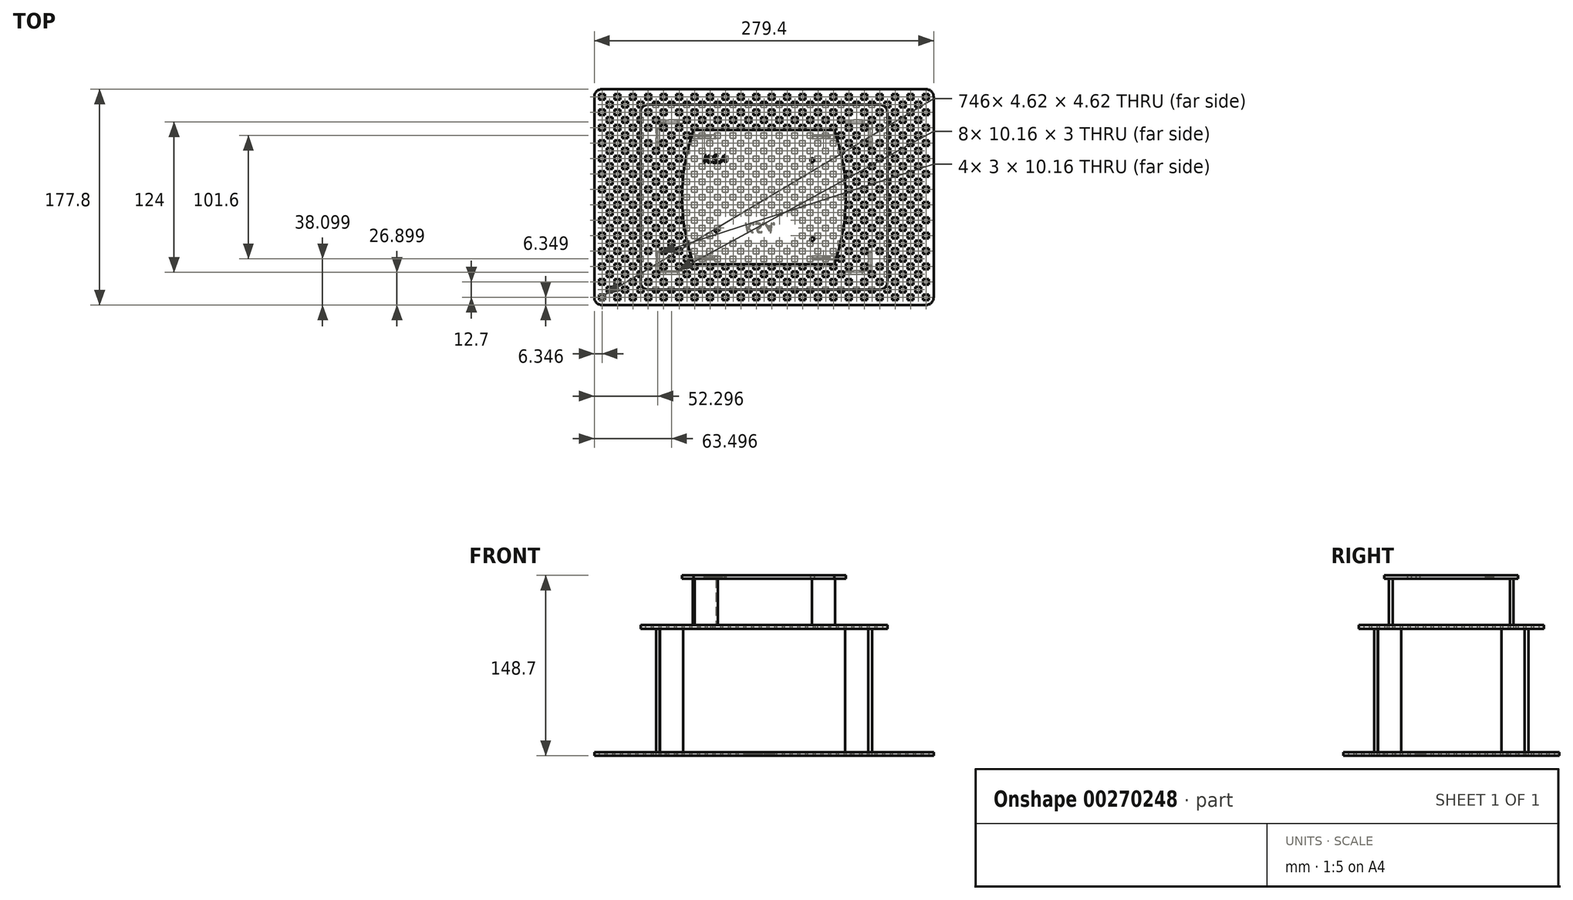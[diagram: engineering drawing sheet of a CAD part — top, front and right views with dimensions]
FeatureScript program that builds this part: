
annotation { "Feature Type Name" : "Feature", "Feature Type Description" : "" }
export const myFeature = defineFeature(function(context is Context, id is Id, definition is map)
    precondition{}
    {
        {
            var Q0;
            Q0=qCreatedBy(makeId("Top.planeOp"),FACE);
            var sketch = newSketch(context, id + "F0", { "sketchPlane" : qUnion([Q0])});
            skLineSegment(sketch, "E0.bottom", {"start": v(-86.6, 36.8) * mm, "end": v(3.9, 36.8) * mm});
            skLineSegment(sketch, "E0.top", {"start": v(-86.6, -48) * mm, "end": v(-68.74, -48) * mm});
            skLineSegment(sketch, "E0.left", {"start": v(-86.6, 36.8) * mm, "end": v(-86.6, -48) * mm});
            skLineSegment(sketch, "E0.right", {"start": v(3.9, 36.8) * mm, "end": v(3.9, -1.72) * mm});
            skLineSegment(sketch, "E1", {"start": v(-1.55, 24.76) * mm, "end": v(-1.55, -40.24) * mm});
            skLineSegment(sketch, "E2", {"start": v(-80.5, 24.76) * mm, "end": v(-1.55, 24.76) * mm});
            skLineSegment(sketch, "E3", {"start": v(-1.55, 24.76) * mm, "end": v(-1.55, 36.8) * mm});
            skLineSegment(sketch, "E4", {"start": v(-1.55, -40.24) * mm, "end": v(-1.55, -48) * mm});
            skLineSegment(sketch, "E5", {"start": v(-1.55, -40.24) * mm, "end": v(-58.83, -40.24) * mm});
            skLineSegment(sketch, "E6", {"start": v(-80.5, -40.24) * mm, "end": v(-80.5, -33.05) * mm});
            skLineSegment(sketch, "E7", {"start": v(-80.5, -33.05) * mm, "end": v(-80.5, 24.76) * mm});
            skCircle(sketch, "E8", {"center": v(-80.5, -33.05) * mm, "radius": 1.59 * mm});
            skCircle(sketch, "E9", {"center": v(-1.55, 24.76) * mm, "radius": 1.59 * mm});
            skCircle(sketch, "E10", {"center": v(-1.55, -40.24) * mm, "radius": 1.59 * mm});
            skLineSegment(sketch, "E11.bottom", {"start": v(-99.3, 49.5) * mm, "end": v(16.6, 49.5) * mm});
            skLineSegment(sketch, "E11.top", {"start": v(-99.3, -60.7) * mm, "end": v(16.6, -60.7) * mm});
            skLineSegment(sketch, "E11.left", {"start": v(-99.3, 49.5) * mm, "end": v(-99.3, -60.7) * mm});
            skLineSegment(sketch, "E11.right", {"start": v(16.6, 49.5) * mm, "end": v(16.6, -60.7) * mm});
            skLineSegment(sketch, "E12.bottom", {"start": v(-95.48, 45.7) * mm, "end": v(-85.32, 45.7) * mm});
            skLineSegment(sketch, "E12.top", {"start": v(-95.48, 42.7) * mm, "end": v(-85.32, 42.7) * mm});
            skLineSegment(sketch, "E12.left", {"start": v(-95.48, 45.7) * mm, "end": v(-95.48, 42.7) * mm});
            skLineSegment(sketch, "E12.right", {"start": v(-85.32, 45.7) * mm, "end": v(-85.32, 42.7) * mm});
            skLineSegment(sketch, "E13.bottom", {"start": v(2.64, 45.7) * mm, "end": v(12.8, 45.7) * mm});
            skLineSegment(sketch, "E13.top", {"start": v(2.64, 42.7) * mm, "end": v(12.8, 42.7) * mm});
            skLineSegment(sketch, "E13.left", {"start": v(2.64, 45.7) * mm, "end": v(2.64, 42.7) * mm});
            skLineSegment(sketch, "E13.right", {"start": v(12.8, 45.7) * mm, "end": v(12.8, 42.7) * mm});
            skLineSegment(sketch, "E14.bottom", {"start": v(-95.48, -53.88) * mm, "end": v(-85.32, -53.88) * mm});
            skLineSegment(sketch, "E14.top", {"start": v(-95.48, -56.88) * mm, "end": v(-85.32, -56.88) * mm});
            skLineSegment(sketch, "E14.left", {"start": v(-95.48, -53.88) * mm, "end": v(-95.48, -56.88) * mm});
            skLineSegment(sketch, "E14.right", {"start": v(-85.32, -53.88) * mm, "end": v(-85.32, -56.88) * mm});
            skLineSegment(sketch, "E15.bottom", {"start": v(2.64, -53.88) * mm, "end": v(12.8, -53.88) * mm});
            skLineSegment(sketch, "E15.top", {"start": v(2.64, -56.88) * mm, "end": v(12.8, -56.88) * mm});
            skLineSegment(sketch, "E15.left", {"start": v(2.64, -53.88) * mm, "end": v(2.64, -56.88) * mm});
            skLineSegment(sketch, "E15.right", {"start": v(12.8, -53.88) * mm, "end": v(12.8, -56.88) * mm});
            skPoint(sketch, "E16", {"position": v(-68.74, -48) * mm});
            skPoint(sketch, "E17", {"position": v(-60.57, -48) * mm});
            skLineSegment(sketch, "E18.trimOffspring", {"start": v(-60.57, -48) * mm, "end": v(3.9, -48) * mm});
            skLineSegment(sketch, "E19", {"start": v(12.8, 45.7) * mm, "end": v(12.8, 49.5) * mm});
            skLineSegment(sketch, "E20", {"start": v(12.8, 42.7) * mm, "end": v(16.6, 42.7) * mm});
            skLineSegment(sketch, "E21", {"start": v(-95.48, 45.7) * mm, "end": v(-95.48, 49.5) * mm});
            skLineSegment(sketch, "E22", {"start": v(-95.48, 45.7) * mm, "end": v(-99.3, 45.7) * mm});
            skLineSegment(sketch, "E23", {"start": v(12.8, -56.88) * mm, "end": v(16.6, -56.88) * mm});
            skLineSegment(sketch, "E24", {"start": v(12.8, -56.88) * mm, "end": v(12.8, -60.7) * mm});
            skLineSegment(sketch, "E25", {"start": v(-95.48, -56.88) * mm, "end": v(-95.48, -60.7) * mm});
            skLineSegment(sketch, "E26", {"start": v(-95.48, -56.88) * mm, "end": v(-99.3, -56.88) * mm});
            skPoint(sketch, "E27", {"position": v(3.9, -1.72) * mm});
            skPoint(sketch, "E28", {"position": v(3.9, -10.46) * mm});
            skLineSegment(sketch, "E29.trimOffspring", {"start": v(3.9, -10.46) * mm, "end": v(3.9, -48) * mm});
            skArc(sketch, "E30", {"start": v(-99.3, 49.5) * mm, "mid": v(-108.76, -5.6) * mm, "end": v(-99.3, -60.7) * mm});
            skArc(sketch, "E31", {"start": v(16.6, -60.7) * mm, "mid": v(26.07, -5.6) * mm, "end": v(16.6, 49.5) * mm});
            skText(sketch, "E32", { "text": "K.S.A", "fontName": "OpenSans-Italic.ttf"});
            const initialGuessF0  = {"E32": [-0.09116, 0.02265, 1, 0, 0.00642]};
            skSetInitialGuess(sketch, initialGuessF0);
            skSolve(sketch);
        }
        {
            var Q0;
            Q0 = qSketchRegion(id + "F0", true);
            extrude(context, id + "F1", {"entities" : qUnion([Q0]), "depth" : 3 * mm});
        }
        {
            var Q0;
            Q0=makeQuery(id+"F1.opExtrude","CAP_FACE",FACE,{"disambiguationData":[OSD([sQuery(id+"F0.wireOp",EDGE,"E8"),sQuery(id+"F0.wireOp",EDGE,"E9"),sQuery(id+"F0.wireOp",EDGE,"E10"),sQuery(id+"F0.wireOp",EDGE,"E11.bottom"),sQuery(id+"F0.wireOp",EDGE,"E11.top"),sQuery(id+"F0.wireOp",EDGE,"E11.left"),sQuery(id+"F0.wireOp",EDGE,"E11.right"),sQuery(id+"F0.wireOp",EDGE,"E12.bottom"),sQuery(id+"F0.wireOp",EDGE,"E12.top"),sQuery(id+"F0.wireOp",EDGE,"E12.left"),sQuery(id+"F0.wireOp",EDGE,"E12.right"),sQuery(id+"F0.wireOp",EDGE,"E13.bottom"),sQuery(id+"F0.wireOp",EDGE,"E13.top"),sQuery(id+"F0.wireOp",EDGE,"E13.left"),sQuery(id+"F0.wireOp",EDGE,"E13.right"),sQuery(id+"F0.wireOp",EDGE,"E14.bottom"),sQuery(id+"F0.wireOp",EDGE,"E14.top"),sQuery(id+"F0.wireOp",EDGE,"E14.left"),sQuery(id+"F0.wireOp",EDGE,"E14.right"),sQuery(id+"F0.wireOp",EDGE,"E15.bottom"),sQuery(id+"F0.wireOp",EDGE,"E15.top"),sQuery(id+"F0.wireOp",EDGE,"E15.left"),sQuery(id+"F0.wireOp",EDGE,"E15.right")])],"isStart":true});
            var sketch = newSketch(context, id + "F2", { "sketchPlane" : qUnion([Q0])});
            skLineSegment(sketch, "E33.bottom", {"start": v(-95.48, 56.88) * mm, "end": v(-85.32, 56.88) * mm});
            skLineSegment(sketch, "E33.top", {"start": v(-95.48, 53.88) * mm, "end": v(-85.32, 53.88) * mm});
            skLineSegment(sketch, "E33.left", {"start": v(-95.48, 56.88) * mm, "end": v(-95.48, 53.88) * mm});
            skLineSegment(sketch, "E33.right", {"start": v(-85.32, 56.88) * mm, "end": v(-85.32, 53.88) * mm});
            skLineSegment(sketch, "E34.bottom", {"start": v(2.64, 56.88) * mm, "end": v(12.8, 56.88) * mm});
            skLineSegment(sketch, "E34.top", {"start": v(2.64, 53.88) * mm, "end": v(12.8, 53.88) * mm});
            skLineSegment(sketch, "E34.left", {"start": v(2.64, 56.88) * mm, "end": v(2.64, 53.88) * mm});
            skLineSegment(sketch, "E34.right", {"start": v(12.8, 56.88) * mm, "end": v(12.8, 53.88) * mm});
            skLineSegment(sketch, "E35.bottom", {"start": v(-95.48, -42.7) * mm, "end": v(-85.32, -42.7) * mm});
            skLineSegment(sketch, "E35.top", {"start": v(-95.48, -45.7) * mm, "end": v(-85.32, -45.7) * mm});
            skLineSegment(sketch, "E35.left", {"start": v(-95.48, -42.7) * mm, "end": v(-95.48, -45.7) * mm});
            skLineSegment(sketch, "E35.right", {"start": v(-85.32, -42.7) * mm, "end": v(-85.32, -45.7) * mm});
            skLineSegment(sketch, "E36.bottom", {"start": v(2.64, -42.7) * mm, "end": v(12.8, -42.7) * mm});
            skLineSegment(sketch, "E36.top", {"start": v(2.64, -45.7) * mm, "end": v(12.8, -45.7) * mm});
            skLineSegment(sketch, "E36.left", {"start": v(2.64, -42.7) * mm, "end": v(2.64, -45.7) * mm});
            skLineSegment(sketch, "E36.right", {"start": v(12.8, -42.7) * mm, "end": v(12.8, -45.7) * mm});
            skLineSegment(sketch, "E37.left", {"start": v(-98.46, 56.88) * mm, "end": v(-98.46, 53.88) * mm});
            skLineSegment(sketch, "E37.right", {"start": v(-79.41, 56.88) * mm, "end": v(-79.41, 53.88) * mm});
            skLineSegment(sketch, "E38.left", {"start": v(-1.8, 56.88) * mm, "end": v(-1.8, 53.88) * mm});
            skLineSegment(sketch, "E38.right", {"start": v(17.24, 56.88) * mm, "end": v(17.24, 53.88) * mm});
            skPoint(sketch, "E39.firstSnap0", {"position": v(7.72, -42.7) * mm});
            skLineSegment(sketch, "E39.bottom", {"start": v(-1.8, -42.7) * mm, "end": v(17.24, -42.7) * mm});
            skLineSegment(sketch, "E39.top", {"start": v(-1.8, -45.7) * mm, "end": v(17.24, -45.7) * mm});
            skLineSegment(sketch, "E39.left", {"start": v(-1.8, -42.7) * mm, "end": v(-1.8, -45.7) * mm});
            skLineSegment(sketch, "E39.right", {"start": v(17.24, -42.7) * mm, "end": v(17.24, -45.7) * mm});
            skLineSegment(sketch, "E40.bottom", {"start": v(-99.93, -42.7) * mm, "end": v(-80.88, -42.7) * mm});
            skLineSegment(sketch, "E40.top", {"start": v(-99.93, -45.7) * mm, "end": v(-80.88, -45.7) * mm});
            skLineSegment(sketch, "E40.left", {"start": v(-99.93, -42.7) * mm, "end": v(-99.93, -45.7) * mm});
            skLineSegment(sketch, "E40.right", {"start": v(-80.88, -42.7) * mm, "end": v(-80.88, -45.7) * mm});
            skPoint(sketch, "E41", {"position": v(-90.4, 56.88) * mm});
            skLineSegment(sketch, "E42", {"start": v(-98.46, 56.88) * mm, "end": v(-79.41, 56.88) * mm});
            skLineSegment(sketch, "E43", {"start": v(-98.46, 53.88) * mm, "end": v(-79.41, 53.88) * mm});
            skLineSegment(sketch, "E44", {"start": v(-1.8, 56.88) * mm, "end": v(17.24, 56.88) * mm});
            skLineSegment(sketch, "E45", {"start": v(-1.8, 53.88) * mm, "end": v(17.24, 53.88) * mm});
            skPoint(sketch, "E46", {"position": v(7.72, 56.88) * mm});
            skPoint(sketch, "E47", {"position": v(-90.4, -42.7) * mm});
            skSolve(sketch);
        }
        {
            var Q0;
            Q0 = qSketchRegion(id + "F2", true);
            extrude(context, id + "F3", {"entities" : qUnion([Q0]), "oppositeDirection" : true, "depth" : 3 * mm});
        }
        {
            var Q0;
            Q0=makeQuery(id+"F3.opExtrude","CAP_FACE",FACE,{"disambiguationData":[OSD([sQuery(id+"F2.wireOp",EDGE,"E37.left"),sQuery(id+"F2.wireOp",EDGE,"E37.right"),sQuery(id+"F2.wireOp",EDGE,"E42"),sQuery(id+"F2.wireOp",EDGE,"E43")])],"isStart":true});
            var Q1;
            Q1=makeQuery(id+"F3.opExtrude","CAP_FACE",FACE,{"disambiguationData":[OSD([sQuery(id+"F2.wireOp",EDGE,"E38.left"),sQuery(id+"F2.wireOp",EDGE,"E38.right"),sQuery(id+"F2.wireOp",EDGE,"E44"),sQuery(id+"F2.wireOp",EDGE,"E45")])],"isStart":true});
            var Q2;
            Q2=makeQuery(id+"F3.opExtrude","CAP_FACE",FACE,{"disambiguationData":[OSD([sQuery(id+"F2.wireOp",EDGE,"E40.bottom"),sQuery(id+"F2.wireOp",EDGE,"E40.top"),sQuery(id+"F2.wireOp",EDGE,"E40.left"),sQuery(id+"F2.wireOp",EDGE,"E40.right")])],"isStart":true});
            var Q3;
            Q3=makeQuery(id+"F3.opExtrude","CAP_FACE",FACE,{"disambiguationData":[OSD([sQuery(id+"F2.wireOp",EDGE,"E39.bottom"),sQuery(id+"F2.wireOp",EDGE,"E39.top"),sQuery(id+"F2.wireOp",EDGE,"E39.left"),sQuery(id+"F2.wireOp",EDGE,"E39.right")])],"isStart":true});
            extrude(context, id + "F4", {"entities" : qUnion([Q0, Q1, Q2, Q3]), "operationType" : NewBodyOperationType.ADD, "depth" : 38.1 * mm});
        }
        {
            var Q0;
            Q0=makeQuery(id+"F4.opExtrude","CAP_FACE",FACE,{"disambiguationData":[OSD([sQuery(id+"F2.wireOp",EDGE,"E37.left"),sQuery(id+"F2.wireOp",EDGE,"E37.right"),sQuery(id+"F2.wireOp",EDGE,"E42"),sQuery(id+"F2.wireOp",EDGE,"E43")])],"isStart":false});
            var sketch = newSketch(context, id + "F5", { "sketchPlane" : qUnion([Q0])});
            skLineSegment(sketch, "E48.bottom", {"start": v(-94.02, 56.88) * mm, "end": v(-83.86, 56.88) * mm});
            skLineSegment(sketch, "E48.top", {"start": v(-94.02, 53.88) * mm, "end": v(-83.86, 53.88) * mm});
            skLineSegment(sketch, "E48.left", {"start": v(-94.02, 56.88) * mm, "end": v(-94.02, 53.88) * mm});
            skLineSegment(sketch, "E48.right", {"start": v(-83.86, 56.88) * mm, "end": v(-83.86, 53.88) * mm});
            skLineSegment(sketch, "E49.bottom", {"start": v(2.64, 56.88) * mm, "end": v(12.8, 56.88) * mm});
            skLineSegment(sketch, "E49.top", {"start": v(2.64, 53.88) * mm, "end": v(12.8, 53.88) * mm});
            skLineSegment(sketch, "E49.left", {"start": v(2.64, 56.88) * mm, "end": v(2.64, 53.88) * mm});
            skLineSegment(sketch, "E49.right", {"start": v(12.8, 56.88) * mm, "end": v(12.8, 53.88) * mm});
            skLineSegment(sketch, "E50.bottom", {"start": v(2.64, -42.7) * mm, "end": v(12.8, -42.7) * mm});
            skLineSegment(sketch, "E50.top", {"start": v(2.64, -45.7) * mm, "end": v(12.8, -45.7) * mm});
            skLineSegment(sketch, "E50.left", {"start": v(2.64, -42.7) * mm, "end": v(2.64, -45.7) * mm});
            skLineSegment(sketch, "E50.right", {"start": v(12.8, -42.7) * mm, "end": v(12.8, -45.7) * mm});
            skPoint(sketch, "E51", {"position": v(7.72, -42.7) * mm});
            skPoint(sketch, "E52", {"position": v(-88.94, 56.88) * mm});
            skPoint(sketch, "E53", {"position": v(7.72, 56.88) * mm});
            skLineSegment(sketch, "E54.bottom", {"start": v(-95.48, -42.7) * mm, "end": v(-85.32, -42.7) * mm});
            skLineSegment(sketch, "E54.top", {"start": v(-95.48, -45.7) * mm, "end": v(-85.32, -45.7) * mm});
            skLineSegment(sketch, "E54.left", {"start": v(-95.48, -42.7) * mm, "end": v(-95.48, -45.7) * mm});
            skLineSegment(sketch, "E54.right", {"start": v(-85.32, -42.7) * mm, "end": v(-85.32, -45.7) * mm});
            skPoint(sketch, "E55", {"position": v(-90.4, -42.7) * mm});
            skSolve(sketch);
        }
        {
            var Q0;
            Q0 = qSketchRegion(id + "F5", true);
            extrude(context, id + "F6", {"entities" : qUnion([Q0]), "operationType" : NewBodyOperationType.ADD, "depth" : 3 * mm});
        }
        {
            var Q0;
            Q0=makeQuery(id+"F6.opExtrude","CAP_FACE",FACE,{"disambiguationData":[OSD([sQuery(id+"F5.wireOp",EDGE,"E48.bottom"),sQuery(id+"F5.wireOp",EDGE,"E48.top"),sQuery(id+"F5.wireOp",EDGE,"E48.left"),sQuery(id+"F5.wireOp",EDGE,"E48.right")])],"isStart":false});
            var sketch = newSketch(context, id + "F7", { "sketchPlane" : qUnion([Q0])});
            skLineSegment(sketch, "E56.bottom", {"start": v(-136.6, 81.8) * mm, "end": v(53.9, 81.8) * mm});
            skLineSegment(sketch, "E56.top", {"start": v(-136.6, -70.6) * mm, "end": v(53.9, -70.6) * mm});
            skLineSegment(sketch, "E56.left", {"start": v(-142.94, 75.44) * mm, "end": v(-142.94, -64.26) * mm});
            skLineSegment(sketch, "E56.right", {"start": v(60.26, 75.44) * mm, "end": v(60.26, -64.26) * mm});
            skLineSegment(sketch, "E57.0.0", {"start": v(-83.86, 53.88) * mm, "end": v(-83.86, 56.88) * mm});
            skLineSegment(sketch, "E57.0.1", {"start": v(-83.86, 56.88) * mm, "end": v(-94.02, 56.88) * mm});
            skLineSegment(sketch, "E57.0.2", {"start": v(-94.02, 56.88) * mm, "end": v(-94.02, 53.88) * mm});
            skLineSegment(sketch, "E57.0.3", {"start": v(-94.02, 53.88) * mm, "end": v(-83.86, 53.88) * mm});
            skLineSegment(sketch, "E58.0.0", {"start": v(2.64, 56.88) * mm, "end": v(2.64, 53.88) * mm});
            skLineSegment(sketch, "E58.0.1", {"start": v(2.64, 53.88) * mm, "end": v(12.8, 53.88) * mm});
            skLineSegment(sketch, "E58.0.2", {"start": v(12.8, 53.88) * mm, "end": v(12.8, 56.88) * mm});
            skLineSegment(sketch, "E58.0.3", {"start": v(12.8, 56.88) * mm, "end": v(2.64, 56.88) * mm});
            skLineSegment(sketch, "E59.0.0", {"start": v(-95.48, -42.7) * mm, "end": v(-95.48, -45.7) * mm});
            skLineSegment(sketch, "E59.0.1", {"start": v(-95.48, -45.7) * mm, "end": v(-85.32, -45.7) * mm});
            skLineSegment(sketch, "E59.0.2", {"start": v(-85.32, -45.7) * mm, "end": v(-85.32, -42.7) * mm});
            skLineSegment(sketch, "E59.0.3", {"start": v(-85.32, -42.7) * mm, "end": v(-95.48, -42.7) * mm});
            skLineSegment(sketch, "E60.0.0", {"start": v(2.64, -42.7) * mm, "end": v(2.64, -45.7) * mm});
            skLineSegment(sketch, "E60.0.1", {"start": v(2.64, -45.7) * mm, "end": v(12.8, -45.7) * mm});
            skLineSegment(sketch, "E60.0.2", {"start": v(12.8, -45.7) * mm, "end": v(12.8, -42.7) * mm});
            skLineSegment(sketch, "E60.0.3", {"start": v(12.8, -42.7) * mm, "end": v(2.64, -42.7) * mm});
            skLineSegment(sketch, "E61", {"start": v(-41.34, -70.6) * mm, "end": v(-41.34, -49.5) * mm});
            skLineSegment(sketch, "E62", {"start": v(-41.34, 81.8) * mm, "end": v(-41.34, 60.7) * mm});
            skPoint(sketch, "E63.visualSharp", {"position": v(-142.94, 81.8) * mm});
            skArc(sketch, "E63.filletArc", {"start": v(-136.6, 81.8) * mm, "mid": v(-141.08, 79.93) * mm, "end": v(-142.94, 75.44) * mm});
            skPoint(sketch, "E64.visualSharp", {"position": v(60.26, 81.8) * mm});
            skArc(sketch, "E64.filletArc", {"start": v(60.26, 75.44) * mm, "mid": v(58.4, 79.93) * mm, "end": v(53.9, 81.8) * mm});
            skPoint(sketch, "E65.visualSharp", {"position": v(60.26, -70.6) * mm});
            skArc(sketch, "E65.filletArc", {"start": v(53.9, -70.6) * mm, "mid": v(58.4, -68.75) * mm, "end": v(60.26, -64.26) * mm});
            skPoint(sketch, "E66.visualSharp", {"position": v(-142.94, -70.6) * mm});
            skArc(sketch, "E66.filletArc", {"start": v(-142.94, -64.26) * mm, "mid": v(-141.08, -68.75) * mm, "end": v(-136.6, -70.6) * mm});
            skLineSegment(sketch, "E67.bottom", {"start": v(-130.24, 61.47) * mm, "end": v(-127.24, 61.47) * mm});
            skLineSegment(sketch, "E67.top", {"start": v(-130.24, 51.31) * mm, "end": v(-127.24, 51.31) * mm});
            skLineSegment(sketch, "E67.left", {"start": v(-130.24, 61.47) * mm, "end": v(-130.24, 51.31) * mm});
            skLineSegment(sketch, "E67.right", {"start": v(-127.24, 61.47) * mm, "end": v(-127.24, 51.31) * mm});
            skLineSegment(sketch, "E68.bottom", {"start": v(-122.62, 66.1) * mm, "end": v(-112.46, 66.1) * mm});
            skLineSegment(sketch, "E68.top", {"start": v(-122.62, 69.1) * mm, "end": v(-112.46, 69.1) * mm});
            skLineSegment(sketch, "E68.left", {"start": v(-122.62, 66.1) * mm, "end": v(-122.62, 69.1) * mm});
            skLineSegment(sketch, "E68.right", {"start": v(-112.46, 66.1) * mm, "end": v(-112.46, 69.1) * mm});
            skLineSegment(sketch, "E69.bottom", {"start": v(29.78, 69.1) * mm, "end": v(39.94, 69.1) * mm});
            skLineSegment(sketch, "E69.top", {"start": v(29.78, 66.1) * mm, "end": v(39.94, 66.1) * mm});
            skLineSegment(sketch, "E69.left", {"start": v(29.78, 69.1) * mm, "end": v(29.78, 66.1) * mm});
            skLineSegment(sketch, "E69.right", {"start": v(39.94, 69.1) * mm, "end": v(39.94, 66.1) * mm});
            skLineSegment(sketch, "E70.bottom", {"start": v(44.56, 61.47) * mm, "end": v(47.56, 61.47) * mm});
            skLineSegment(sketch, "E70.top", {"start": v(44.56, 51.31) * mm, "end": v(47.56, 51.31) * mm});
            skLineSegment(sketch, "E70.left", {"start": v(44.56, 61.47) * mm, "end": v(44.56, 51.31) * mm});
            skLineSegment(sketch, "E70.right", {"start": v(47.56, 61.47) * mm, "end": v(47.56, 51.31) * mm});
            skLineSegment(sketch, "E71.bottom", {"start": v(-130.24, -40.13) * mm, "end": v(-127.24, -40.13) * mm});
            skLineSegment(sketch, "E71.top", {"start": v(-130.24, -50.29) * mm, "end": v(-127.24, -50.29) * mm});
            skLineSegment(sketch, "E71.left", {"start": v(-130.24, -40.13) * mm, "end": v(-130.24, -50.29) * mm});
            skLineSegment(sketch, "E71.right", {"start": v(-127.24, -40.13) * mm, "end": v(-127.24, -50.29) * mm});
            skLineSegment(sketch, "E72.bottom", {"start": v(-122.62, -57.9) * mm, "end": v(-112.46, -57.9) * mm});
            skLineSegment(sketch, "E72.top", {"start": v(-122.62, -54.9) * mm, "end": v(-112.46, -54.9) * mm});
            skLineSegment(sketch, "E72.left", {"start": v(-122.62, -57.9) * mm, "end": v(-122.62, -54.9) * mm});
            skLineSegment(sketch, "E72.right", {"start": v(-112.46, -57.9) * mm, "end": v(-112.46, -54.9) * mm});
            skLineSegment(sketch, "E73.bottom", {"start": v(29.78, -57.9) * mm, "end": v(39.94, -57.9) * mm});
            skLineSegment(sketch, "E73.top", {"start": v(29.78, -54.9) * mm, "end": v(39.94, -54.9) * mm});
            skLineSegment(sketch, "E73.left", {"start": v(29.78, -57.9) * mm, "end": v(29.78, -54.9) * mm});
            skLineSegment(sketch, "E73.right", {"start": v(39.94, -57.9) * mm, "end": v(39.94, -54.9) * mm});
            skLineSegment(sketch, "E74.bottom", {"start": v(44.56, -50.29) * mm, "end": v(47.56, -50.29) * mm});
            skLineSegment(sketch, "E74.top", {"start": v(44.56, -40.13) * mm, "end": v(47.56, -40.13) * mm});
            skLineSegment(sketch, "E74.left", {"start": v(44.56, -50.29) * mm, "end": v(44.56, -40.13) * mm});
            skLineSegment(sketch, "E74.right", {"start": v(47.56, -50.29) * mm, "end": v(47.56, -40.13) * mm});
            skSolve(sketch);
        }
        {
            var Q0;
            Q0 = qSketchRegion(id + "F7", true);
            extrude(context, id + "F8", {"entities" : qUnion([Q0]), "oppositeDirection" : true, "depth" : 3 * mm});
        }
        {
            var Q0;
            Q0=makeQuery(id+"F8.opExtrude","CAP_FACE",FACE,{"disambiguationData":[OSD([sQuery(id+"F7.wireOp",EDGE,"E56.bottom"),sQuery(id+"F7.wireOp",EDGE,"E56.top"),sQuery(id+"F7.wireOp",EDGE,"E56.left"),sQuery(id+"F7.wireOp",EDGE,"E56.right"),sQuery(id+"F7.wireOp",EDGE,"E57.0.0"),sQuery(id+"F7.wireOp",EDGE,"E57.0.1"),sQuery(id+"F7.wireOp",EDGE,"E57.0.2"),sQuery(id+"F7.wireOp",EDGE,"E57.0.3"),sQuery(id+"F7.wireOp",EDGE,"E58.0.0"),sQuery(id+"F7.wireOp",EDGE,"E58.0.1"),sQuery(id+"F7.wireOp",EDGE,"E58.0.2"),sQuery(id+"F7.wireOp",EDGE,"E58.0.3"),sQuery(id+"F7.wireOp",EDGE,"E59.0.0"),sQuery(id+"F7.wireOp",EDGE,"E59.0.1"),sQuery(id+"F7.wireOp",EDGE,"E59.0.2"),sQuery(id+"F7.wireOp",EDGE,"E59.0.3"),sQuery(id+"F7.wireOp",EDGE,"E60.0.0"),sQuery(id+"F7.wireOp",EDGE,"E60.0.1"),sQuery(id+"F7.wireOp",EDGE,"E60.0.2"),sQuery(id+"F7.wireOp",EDGE,"E60.0.3"),sQuery(id+"F7.wireOp",EDGE,"E63.filletArc"),sQuery(id+"F7.wireOp",EDGE,"E64.filletArc"),sQuery(id+"F7.wireOp",EDGE,"E65.filletArc"),sQuery(id+"F7.wireOp",EDGE,"E66.filletArc"),sQuery(id+"F7.wireOp",EDGE,"E67.bottom"),sQuery(id+"F7.wireOp",EDGE,"E67.top"),sQuery(id+"F7.wireOp",EDGE,"E67.left"),sQuery(id+"F7.wireOp",EDGE,"E67.right"),sQuery(id+"F7.wireOp",EDGE,"E68.bottom"),sQuery(id+"F7.wireOp",EDGE,"E68.top"),sQuery(id+"F7.wireOp",EDGE,"E68.left"),sQuery(id+"F7.wireOp",EDGE,"E68.right"),sQuery(id+"F7.wireOp",EDGE,"E69.bottom"),sQuery(id+"F7.wireOp",EDGE,"E69.top"),sQuery(id+"F7.wireOp",EDGE,"E69.left"),sQuery(id+"F7.wireOp",EDGE,"E69.right"),sQuery(id+"F7.wireOp",EDGE,"E70.bottom"),sQuery(id+"F7.wireOp",EDGE,"E70.top"),sQuery(id+"F7.wireOp",EDGE,"E70.left"),sQuery(id+"F7.wireOp",EDGE,"E70.right"),sQuery(id+"F7.wireOp",EDGE,"E71.bottom"),sQuery(id+"F7.wireOp",EDGE,"E71.top"),sQuery(id+"F7.wireOp",EDGE,"E71.left"),sQuery(id+"F7.wireOp",EDGE,"E71.right"),sQuery(id+"F7.wireOp",EDGE,"E72.bottom"),sQuery(id+"F7.wireOp",EDGE,"E72.top"),sQuery(id+"F7.wireOp",EDGE,"E72.left"),sQuery(id+"F7.wireOp",EDGE,"E72.right"),sQuery(id+"F7.wireOp",EDGE,"E73.bottom"),sQuery(id+"F7.wireOp",EDGE,"E73.top"),sQuery(id+"F7.wireOp",EDGE,"E73.left"),sQuery(id+"F7.wireOp",EDGE,"E73.right"),sQuery(id+"F7.wireOp",EDGE,"E74.bottom"),sQuery(id+"F7.wireOp",EDGE,"E74.top"),sQuery(id+"F7.wireOp",EDGE,"E74.left"),sQuery(id+"F7.wireOp",EDGE,"E74.right")])],"isStart":true});
            var sketch = newSketch(context, id + "F9", { "sketchPlane" : qUnion([Q0])});
            skLineSegment(sketch, "E75.bottom", {"start": v(-138.9, 77.75) * mm, "end": v(-134.28, 77.75) * mm});
            skLineSegment(sketch, "E75.top", {"start": v(-138.9, 73.13) * mm, "end": v(-134.28, 73.13) * mm});
            skLineSegment(sketch, "E75.left", {"start": v(-138.9, 77.75) * mm, "end": v(-138.9, 73.13) * mm});
            skLineSegment(sketch, "E75.right", {"start": v(-134.28, 77.75) * mm, "end": v(-134.28, 73.13) * mm});
            skLineSegment(sketch, "E76", {"start": v(-136.6, 77.75) * mm, "end": v(-136.6, 81.8) * mm});
            skLineSegment(sketch, "E77", {"start": v(-138.9, 75.44) * mm, "end": v(-142.94, 75.44) * mm});
            skLineSegment(sketch, "E78.0.1.0", {"start": v(-134.28, 65.05) * mm, "end": v(-134.28, 60.43) * mm});
            skLineSegment(sketch, "E78.0.1.1", {"start": v(-138.9, 60.43) * mm, "end": v(-134.28, 60.43) * mm});
            skLineSegment(sketch, "E78.0.1.2", {"start": v(-138.9, 65.05) * mm, "end": v(-138.9, 60.43) * mm});
            skLineSegment(sketch, "E78.0.1.3", {"start": v(-138.9, 65.05) * mm, "end": v(-134.28, 65.05) * mm});
            skLineSegment(sketch, "E78.0.2.0", {"start": v(-134.28, 52.35) * mm, "end": v(-134.28, 47.73) * mm});
            skLineSegment(sketch, "E78.0.2.1", {"start": v(-138.9, 47.73) * mm, "end": v(-134.28, 47.73) * mm});
            skLineSegment(sketch, "E78.0.2.2", {"start": v(-138.9, 52.35) * mm, "end": v(-138.9, 47.73) * mm});
            skLineSegment(sketch, "E78.0.2.3", {"start": v(-138.9, 52.35) * mm, "end": v(-134.28, 52.35) * mm});
            skLineSegment(sketch, "E78.0.3.0", {"start": v(-134.28, 39.65) * mm, "end": v(-134.28, 35.03) * mm});
            skLineSegment(sketch, "E78.0.3.1", {"start": v(-138.9, 35.03) * mm, "end": v(-134.28, 35.03) * mm});
            skLineSegment(sketch, "E78.0.3.2", {"start": v(-138.9, 39.65) * mm, "end": v(-138.9, 35.03) * mm});
            skLineSegment(sketch, "E78.0.3.3", {"start": v(-138.9, 39.65) * mm, "end": v(-134.28, 39.65) * mm});
            skLineSegment(sketch, "E78.0.4.0", {"start": v(-134.28, 26.95) * mm, "end": v(-134.28, 22.33) * mm});
            skLineSegment(sketch, "E78.0.4.1", {"start": v(-138.9, 22.33) * mm, "end": v(-134.28, 22.33) * mm});
            skLineSegment(sketch, "E78.0.4.2", {"start": v(-138.9, 26.95) * mm, "end": v(-138.9, 22.33) * mm});
            skLineSegment(sketch, "E78.0.4.3", {"start": v(-138.9, 26.95) * mm, "end": v(-134.28, 26.95) * mm});
            skLineSegment(sketch, "E78.0.5.0", {"start": v(-134.28, 14.25) * mm, "end": v(-134.28, 9.63) * mm});
            skLineSegment(sketch, "E78.0.5.1", {"start": v(-138.9, 9.63) * mm, "end": v(-134.28, 9.63) * mm});
            skLineSegment(sketch, "E78.0.5.2", {"start": v(-138.9, 14.25) * mm, "end": v(-138.9, 9.63) * mm});
            skLineSegment(sketch, "E78.0.5.3", {"start": v(-138.9, 14.25) * mm, "end": v(-134.28, 14.25) * mm});
            skLineSegment(sketch, "E78.0.6.0", {"start": v(-134.28, 1.55) * mm, "end": v(-134.28, -3.07) * mm});
            skLineSegment(sketch, "E78.0.6.1", {"start": v(-138.9, -3.07) * mm, "end": v(-134.28, -3.07) * mm});
            skLineSegment(sketch, "E78.0.6.2", {"start": v(-138.9, 1.55) * mm, "end": v(-138.9, -3.07) * mm});
            skLineSegment(sketch, "E78.0.6.3", {"start": v(-138.9, 1.55) * mm, "end": v(-134.28, 1.55) * mm});
            skLineSegment(sketch, "E78.0.7.0", {"start": v(-134.28, -11.15) * mm, "end": v(-134.28, -15.77) * mm});
            skLineSegment(sketch, "E78.0.7.1", {"start": v(-138.9, -15.77) * mm, "end": v(-134.28, -15.77) * mm});
            skLineSegment(sketch, "E78.0.7.2", {"start": v(-138.9, -11.15) * mm, "end": v(-138.9, -15.77) * mm});
            skLineSegment(sketch, "E78.0.7.3", {"start": v(-138.9, -11.15) * mm, "end": v(-134.28, -11.15) * mm});
            skLineSegment(sketch, "E78.0.8.0", {"start": v(-134.28, -23.85) * mm, "end": v(-134.28, -28.47) * mm});
            skLineSegment(sketch, "E78.0.8.1", {"start": v(-138.9, -28.47) * mm, "end": v(-134.28, -28.47) * mm});
            skLineSegment(sketch, "E78.0.8.2", {"start": v(-138.9, -23.85) * mm, "end": v(-138.9, -28.47) * mm});
            skLineSegment(sketch, "E78.0.8.3", {"start": v(-138.9, -23.85) * mm, "end": v(-134.28, -23.85) * mm});
            skLineSegment(sketch, "E78.0.9.0", {"start": v(-134.28, -36.55) * mm, "end": v(-134.28, -41.17) * mm});
            skLineSegment(sketch, "E78.0.9.1", {"start": v(-138.9, -41.17) * mm, "end": v(-134.28, -41.17) * mm});
            skLineSegment(sketch, "E78.0.9.2", {"start": v(-138.9, -36.55) * mm, "end": v(-138.9, -41.17) * mm});
            skLineSegment(sketch, "E78.0.9.3", {"start": v(-138.9, -36.55) * mm, "end": v(-134.28, -36.55) * mm});
            skLineSegment(sketch, "E78.0.10.0", {"start": v(-134.28, -49.25) * mm, "end": v(-134.28, -53.87) * mm});
            skLineSegment(sketch, "E78.0.10.1", {"start": v(-138.9, -53.87) * mm, "end": v(-134.28, -53.87) * mm});
            skLineSegment(sketch, "E78.0.10.2", {"start": v(-138.9, -49.25) * mm, "end": v(-138.9, -53.87) * mm});
            skLineSegment(sketch, "E78.0.10.3", {"start": v(-138.9, -49.25) * mm, "end": v(-134.28, -49.25) * mm});
            skLineSegment(sketch, "E78.0.11.0", {"start": v(-134.28, -61.95) * mm, "end": v(-134.28, -66.57) * mm});
            skLineSegment(sketch, "E78.0.11.1", {"start": v(-138.9, -66.57) * mm, "end": v(-134.28, -66.57) * mm});
            skLineSegment(sketch, "E78.0.11.2", {"start": v(-138.9, -61.95) * mm, "end": v(-138.9, -66.57) * mm});
            skLineSegment(sketch, "E78.0.11.3", {"start": v(-138.9, -61.95) * mm, "end": v(-134.28, -61.95) * mm});
            skLineSegment(sketch, "E78.1.0.0", {"start": v(-121.58, 77.75) * mm, "end": v(-121.58, 73.13) * mm});
            skLineSegment(sketch, "E78.1.0.1", {"start": v(-126.2, 73.13) * mm, "end": v(-121.58, 73.13) * mm});
            skLineSegment(sketch, "E78.1.0.2", {"start": v(-126.2, 77.75) * mm, "end": v(-126.2, 73.13) * mm});
            skLineSegment(sketch, "E78.1.0.3", {"start": v(-126.2, 77.75) * mm, "end": v(-121.58, 77.75) * mm});
            skLineSegment(sketch, "E78.1.1.0", {"start": v(-121.58, 65.05) * mm, "end": v(-121.58, 60.43) * mm});
            skLineSegment(sketch, "E78.1.1.1", {"start": v(-126.2, 60.43) * mm, "end": v(-121.58, 60.43) * mm});
            skLineSegment(sketch, "E78.1.1.2", {"start": v(-126.2, 65.05) * mm, "end": v(-126.2, 60.43) * mm});
            skLineSegment(sketch, "E78.1.1.3", {"start": v(-126.2, 65.05) * mm, "end": v(-121.58, 65.05) * mm});
            skLineSegment(sketch, "E78.1.2.0", {"start": v(-121.58, 52.35) * mm, "end": v(-121.58, 47.73) * mm});
            skLineSegment(sketch, "E78.1.2.1", {"start": v(-126.2, 47.73) * mm, "end": v(-121.58, 47.73) * mm});
            skLineSegment(sketch, "E78.1.2.2", {"start": v(-126.2, 52.35) * mm, "end": v(-126.2, 47.73) * mm});
            skLineSegment(sketch, "E78.1.2.3", {"start": v(-126.2, 52.35) * mm, "end": v(-121.58, 52.35) * mm});
            skLineSegment(sketch, "E78.1.3.0", {"start": v(-121.58, 39.65) * mm, "end": v(-121.58, 35.03) * mm});
            skLineSegment(sketch, "E78.1.3.1", {"start": v(-126.2, 35.03) * mm, "end": v(-121.58, 35.03) * mm});
            skLineSegment(sketch, "E78.1.3.2", {"start": v(-126.2, 39.65) * mm, "end": v(-126.2, 35.03) * mm});
            skLineSegment(sketch, "E78.1.3.3", {"start": v(-126.2, 39.65) * mm, "end": v(-121.58, 39.65) * mm});
            skLineSegment(sketch, "E78.1.4.0", {"start": v(-121.58, 26.95) * mm, "end": v(-121.58, 22.33) * mm});
            skLineSegment(sketch, "E78.1.4.1", {"start": v(-126.2, 22.33) * mm, "end": v(-121.58, 22.33) * mm});
            skLineSegment(sketch, "E78.1.4.2", {"start": v(-126.2, 26.95) * mm, "end": v(-126.2, 22.33) * mm});
            skLineSegment(sketch, "E78.1.4.3", {"start": v(-126.2, 26.95) * mm, "end": v(-121.58, 26.95) * mm});
            skLineSegment(sketch, "E78.1.5.0", {"start": v(-121.58, 14.25) * mm, "end": v(-121.58, 9.63) * mm});
            skLineSegment(sketch, "E78.1.5.1", {"start": v(-126.2, 9.63) * mm, "end": v(-121.58, 9.63) * mm});
            skLineSegment(sketch, "E78.1.5.2", {"start": v(-126.2, 14.25) * mm, "end": v(-126.2, 9.63) * mm});
            skLineSegment(sketch, "E78.1.5.3", {"start": v(-126.2, 14.25) * mm, "end": v(-121.58, 14.25) * mm});
            skLineSegment(sketch, "E78.1.6.0", {"start": v(-121.58, 1.55) * mm, "end": v(-121.58, -3.07) * mm});
            skLineSegment(sketch, "E78.1.6.1", {"start": v(-126.2, -3.07) * mm, "end": v(-121.58, -3.07) * mm});
            skLineSegment(sketch, "E78.1.6.2", {"start": v(-126.2, 1.55) * mm, "end": v(-126.2, -3.07) * mm});
            skLineSegment(sketch, "E78.1.6.3", {"start": v(-126.2, 1.55) * mm, "end": v(-121.58, 1.55) * mm});
            skLineSegment(sketch, "E78.1.7.0", {"start": v(-121.58, -11.15) * mm, "end": v(-121.58, -15.77) * mm});
            skLineSegment(sketch, "E78.1.7.1", {"start": v(-126.2, -15.77) * mm, "end": v(-121.58, -15.77) * mm});
            skLineSegment(sketch, "E78.1.7.2", {"start": v(-126.2, -11.15) * mm, "end": v(-126.2, -15.77) * mm});
            skLineSegment(sketch, "E78.1.7.3", {"start": v(-126.2, -11.15) * mm, "end": v(-121.58, -11.15) * mm});
            skLineSegment(sketch, "E78.1.8.0", {"start": v(-121.58, -23.85) * mm, "end": v(-121.58, -28.47) * mm});
            skLineSegment(sketch, "E78.1.8.1", {"start": v(-126.2, -28.47) * mm, "end": v(-121.58, -28.47) * mm});
            skLineSegment(sketch, "E78.1.8.2", {"start": v(-126.2, -23.85) * mm, "end": v(-126.2, -28.47) * mm});
            skLineSegment(sketch, "E78.1.8.3", {"start": v(-126.2, -23.85) * mm, "end": v(-121.58, -23.85) * mm});
            skLineSegment(sketch, "E78.1.9.0", {"start": v(-121.58, -36.55) * mm, "end": v(-121.58, -41.17) * mm});
            skLineSegment(sketch, "E78.1.9.1", {"start": v(-126.2, -41.17) * mm, "end": v(-121.58, -41.17) * mm});
            skLineSegment(sketch, "E78.1.9.2", {"start": v(-126.2, -36.55) * mm, "end": v(-126.2, -41.17) * mm});
            skLineSegment(sketch, "E78.1.9.3", {"start": v(-126.2, -36.55) * mm, "end": v(-121.58, -36.55) * mm});
            skLineSegment(sketch, "E78.1.10.0", {"start": v(-121.58, -49.25) * mm, "end": v(-121.58, -53.87) * mm});
            skLineSegment(sketch, "E78.1.10.1", {"start": v(-126.2, -53.87) * mm, "end": v(-121.58, -53.87) * mm});
            skLineSegment(sketch, "E78.1.10.2", {"start": v(-126.2, -49.25) * mm, "end": v(-126.2, -53.87) * mm});
            skLineSegment(sketch, "E78.1.10.3", {"start": v(-126.2, -49.25) * mm, "end": v(-121.58, -49.25) * mm});
            skLineSegment(sketch, "E78.1.11.0", {"start": v(-121.58, -61.95) * mm, "end": v(-121.58, -66.57) * mm});
            skLineSegment(sketch, "E78.1.11.1", {"start": v(-126.2, -66.57) * mm, "end": v(-121.58, -66.57) * mm});
            skLineSegment(sketch, "E78.1.11.2", {"start": v(-126.2, -61.95) * mm, "end": v(-126.2, -66.57) * mm});
            skLineSegment(sketch, "E78.1.11.3", {"start": v(-126.2, -61.95) * mm, "end": v(-121.58, -61.95) * mm});
            skLineSegment(sketch, "E78.2.0.0", {"start": v(-108.88, 77.75) * mm, "end": v(-108.88, 73.13) * mm});
            skLineSegment(sketch, "E78.2.0.1", {"start": v(-113.5, 73.13) * mm, "end": v(-108.88, 73.13) * mm});
            skLineSegment(sketch, "E78.2.0.2", {"start": v(-113.5, 77.75) * mm, "end": v(-113.5, 73.13) * mm});
            skLineSegment(sketch, "E78.2.0.3", {"start": v(-113.5, 77.75) * mm, "end": v(-108.88, 77.75) * mm});
            skLineSegment(sketch, "E78.2.1.0", {"start": v(-108.88, 65.05) * mm, "end": v(-108.88, 60.43) * mm});
            skLineSegment(sketch, "E78.2.1.1", {"start": v(-113.5, 60.43) * mm, "end": v(-108.88, 60.43) * mm});
            skLineSegment(sketch, "E78.2.1.2", {"start": v(-113.5, 65.05) * mm, "end": v(-113.5, 60.43) * mm});
            skLineSegment(sketch, "E78.2.1.3", {"start": v(-113.5, 65.05) * mm, "end": v(-108.88, 65.05) * mm});
            skLineSegment(sketch, "E78.2.2.0", {"start": v(-108.88, 52.35) * mm, "end": v(-108.88, 47.73) * mm});
            skLineSegment(sketch, "E78.2.2.1", {"start": v(-113.5, 47.73) * mm, "end": v(-108.88, 47.73) * mm});
            skLineSegment(sketch, "E78.2.2.2", {"start": v(-113.5, 52.35) * mm, "end": v(-113.5, 47.73) * mm});
            skLineSegment(sketch, "E78.2.2.3", {"start": v(-113.5, 52.35) * mm, "end": v(-108.88, 52.35) * mm});
            skLineSegment(sketch, "E78.2.3.0", {"start": v(-108.88, 39.65) * mm, "end": v(-108.88, 35.03) * mm});
            skLineSegment(sketch, "E78.2.3.1", {"start": v(-113.5, 35.03) * mm, "end": v(-108.88, 35.03) * mm});
            skLineSegment(sketch, "E78.2.3.2", {"start": v(-113.5, 39.65) * mm, "end": v(-113.5, 35.03) * mm});
            skLineSegment(sketch, "E78.2.3.3", {"start": v(-113.5, 39.65) * mm, "end": v(-108.88, 39.65) * mm});
            skLineSegment(sketch, "E78.2.4.0", {"start": v(-108.88, 26.95) * mm, "end": v(-108.88, 22.33) * mm});
            skLineSegment(sketch, "E78.2.4.1", {"start": v(-113.5, 22.33) * mm, "end": v(-108.88, 22.33) * mm});
            skLineSegment(sketch, "E78.2.4.2", {"start": v(-113.5, 26.95) * mm, "end": v(-113.5, 22.33) * mm});
            skLineSegment(sketch, "E78.2.4.3", {"start": v(-113.5, 26.95) * mm, "end": v(-108.88, 26.95) * mm});
            skLineSegment(sketch, "E78.2.5.0", {"start": v(-108.88, 14.25) * mm, "end": v(-108.88, 9.63) * mm});
            skLineSegment(sketch, "E78.2.5.1", {"start": v(-113.5, 9.63) * mm, "end": v(-108.88, 9.63) * mm});
            skLineSegment(sketch, "E78.2.5.2", {"start": v(-113.5, 14.25) * mm, "end": v(-113.5, 9.63) * mm});
            skLineSegment(sketch, "E78.2.5.3", {"start": v(-113.5, 14.25) * mm, "end": v(-108.88, 14.25) * mm});
            skLineSegment(sketch, "E78.2.6.0", {"start": v(-108.88, 1.55) * mm, "end": v(-108.88, -3.07) * mm});
            skLineSegment(sketch, "E78.2.6.1", {"start": v(-113.5, -3.07) * mm, "end": v(-108.88, -3.07) * mm});
            skLineSegment(sketch, "E78.2.6.2", {"start": v(-113.5, 1.55) * mm, "end": v(-113.5, -3.07) * mm});
            skLineSegment(sketch, "E78.2.6.3", {"start": v(-113.5, 1.55) * mm, "end": v(-108.88, 1.55) * mm});
            skLineSegment(sketch, "E78.2.7.0", {"start": v(-108.88, -11.15) * mm, "end": v(-108.88, -15.77) * mm});
            skLineSegment(sketch, "E78.2.7.1", {"start": v(-113.5, -15.77) * mm, "end": v(-108.88, -15.77) * mm});
            skLineSegment(sketch, "E78.2.7.2", {"start": v(-113.5, -11.15) * mm, "end": v(-113.5, -15.77) * mm});
            skLineSegment(sketch, "E78.2.7.3", {"start": v(-113.5, -11.15) * mm, "end": v(-108.88, -11.15) * mm});
            skLineSegment(sketch, "E78.2.8.0", {"start": v(-108.88, -23.85) * mm, "end": v(-108.88, -28.47) * mm});
            skLineSegment(sketch, "E78.2.8.1", {"start": v(-113.5, -28.47) * mm, "end": v(-108.88, -28.47) * mm});
            skLineSegment(sketch, "E78.2.8.2", {"start": v(-113.5, -23.85) * mm, "end": v(-113.5, -28.47) * mm});
            skLineSegment(sketch, "E78.2.8.3", {"start": v(-113.5, -23.85) * mm, "end": v(-108.88, -23.85) * mm});
            skLineSegment(sketch, "E78.2.9.0", {"start": v(-108.88, -36.55) * mm, "end": v(-108.88, -41.17) * mm});
            skLineSegment(sketch, "E78.2.9.1", {"start": v(-113.5, -41.17) * mm, "end": v(-108.88, -41.17) * mm});
            skLineSegment(sketch, "E78.2.9.2", {"start": v(-113.5, -36.55) * mm, "end": v(-113.5, -41.17) * mm});
            skLineSegment(sketch, "E78.2.9.3", {"start": v(-113.5, -36.55) * mm, "end": v(-108.88, -36.55) * mm});
            skLineSegment(sketch, "E78.2.10.0", {"start": v(-108.88, -49.25) * mm, "end": v(-108.88, -53.87) * mm});
            skLineSegment(sketch, "E78.2.10.1", {"start": v(-113.5, -53.87) * mm, "end": v(-108.88, -53.87) * mm});
            skLineSegment(sketch, "E78.2.10.2", {"start": v(-113.5, -49.25) * mm, "end": v(-113.5, -53.87) * mm});
            skLineSegment(sketch, "E78.2.10.3", {"start": v(-113.5, -49.25) * mm, "end": v(-108.88, -49.25) * mm});
            skLineSegment(sketch, "E78.2.11.0", {"start": v(-108.88, -61.95) * mm, "end": v(-108.88, -66.57) * mm});
            skLineSegment(sketch, "E78.2.11.1", {"start": v(-113.5, -66.57) * mm, "end": v(-108.88, -66.57) * mm});
            skLineSegment(sketch, "E78.2.11.2", {"start": v(-113.5, -61.95) * mm, "end": v(-113.5, -66.57) * mm});
            skLineSegment(sketch, "E78.2.11.3", {"start": v(-113.5, -61.95) * mm, "end": v(-108.88, -61.95) * mm});
            skLineSegment(sketch, "E78.3.0.0", {"start": v(-96.18, 77.75) * mm, "end": v(-96.18, 73.13) * mm});
            skLineSegment(sketch, "E78.3.0.1", {"start": v(-100.8, 73.13) * mm, "end": v(-96.18, 73.13) * mm});
            skLineSegment(sketch, "E78.3.0.2", {"start": v(-100.8, 77.75) * mm, "end": v(-100.8, 73.13) * mm});
            skLineSegment(sketch, "E78.3.0.3", {"start": v(-100.8, 77.75) * mm, "end": v(-96.18, 77.75) * mm});
            skLineSegment(sketch, "E78.3.1.0", {"start": v(-96.18, 65.05) * mm, "end": v(-96.18, 60.43) * mm});
            skLineSegment(sketch, "E78.3.1.1", {"start": v(-100.8, 60.43) * mm, "end": v(-96.18, 60.43) * mm});
            skLineSegment(sketch, "E78.3.1.2", {"start": v(-100.8, 65.05) * mm, "end": v(-100.8, 60.43) * mm});
            skLineSegment(sketch, "E78.3.1.3", {"start": v(-100.8, 65.05) * mm, "end": v(-96.18, 65.05) * mm});
            skLineSegment(sketch, "E78.3.10.0", {"start": v(-96.18, -49.25) * mm, "end": v(-96.18, -53.87) * mm});
            skLineSegment(sketch, "E78.3.10.1", {"start": v(-100.8, -53.87) * mm, "end": v(-96.18, -53.87) * mm});
            skLineSegment(sketch, "E78.3.10.2", {"start": v(-100.8, -49.25) * mm, "end": v(-100.8, -53.87) * mm});
            skLineSegment(sketch, "E78.3.10.3", {"start": v(-100.8, -49.25) * mm, "end": v(-96.18, -49.25) * mm});
            skLineSegment(sketch, "E78.3.11.0", {"start": v(-96.18, -61.95) * mm, "end": v(-96.18, -66.57) * mm});
            skLineSegment(sketch, "E78.3.11.1", {"start": v(-100.8, -66.57) * mm, "end": v(-96.18, -66.57) * mm});
            skLineSegment(sketch, "E78.3.11.2", {"start": v(-100.8, -61.95) * mm, "end": v(-100.8, -66.57) * mm});
            skLineSegment(sketch, "E78.3.11.3", {"start": v(-100.8, -61.95) * mm, "end": v(-96.18, -61.95) * mm});
            skLineSegment(sketch, "E78.4.0.0", {"start": v(-83.48, 77.75) * mm, "end": v(-83.48, 73.13) * mm});
            skLineSegment(sketch, "E78.4.0.1", {"start": v(-88.1, 73.13) * mm, "end": v(-83.48, 73.13) * mm});
            skLineSegment(sketch, "E78.4.0.2", {"start": v(-88.1, 77.75) * mm, "end": v(-88.1, 73.13) * mm});
            skLineSegment(sketch, "E78.4.0.3", {"start": v(-88.1, 77.75) * mm, "end": v(-83.48, 77.75) * mm});
            skLineSegment(sketch, "E78.4.1.0", {"start": v(-83.48, 65.05) * mm, "end": v(-83.48, 60.43) * mm});
            skLineSegment(sketch, "E78.4.1.1", {"start": v(-88.1, 60.43) * mm, "end": v(-83.48, 60.43) * mm});
            skLineSegment(sketch, "E78.4.1.2", {"start": v(-88.1, 65.05) * mm, "end": v(-88.1, 60.43) * mm});
            skLineSegment(sketch, "E78.4.1.3", {"start": v(-88.1, 65.05) * mm, "end": v(-83.48, 65.05) * mm});
            skLineSegment(sketch, "E78.4.10.0", {"start": v(-83.48, -49.25) * mm, "end": v(-83.48, -53.87) * mm});
            skLineSegment(sketch, "E78.4.10.1", {"start": v(-88.1, -53.87) * mm, "end": v(-83.48, -53.87) * mm});
            skLineSegment(sketch, "E78.4.10.2", {"start": v(-88.1, -49.25) * mm, "end": v(-88.1, -53.87) * mm});
            skLineSegment(sketch, "E78.4.10.3", {"start": v(-88.1, -49.25) * mm, "end": v(-83.48, -49.25) * mm});
            skLineSegment(sketch, "E78.4.11.0", {"start": v(-83.48, -61.95) * mm, "end": v(-83.48, -66.57) * mm});
            skLineSegment(sketch, "E78.4.11.1", {"start": v(-88.1, -66.57) * mm, "end": v(-83.48, -66.57) * mm});
            skLineSegment(sketch, "E78.4.11.2", {"start": v(-88.1, -61.95) * mm, "end": v(-88.1, -66.57) * mm});
            skLineSegment(sketch, "E78.4.11.3", {"start": v(-88.1, -61.95) * mm, "end": v(-83.48, -61.95) * mm});
            skLineSegment(sketch, "E78.5.0.0", {"start": v(-70.78, 77.75) * mm, "end": v(-70.78, 73.13) * mm});
            skLineSegment(sketch, "E78.5.0.1", {"start": v(-75.4, 73.13) * mm, "end": v(-70.78, 73.13) * mm});
            skLineSegment(sketch, "E78.5.0.2", {"start": v(-75.4, 77.75) * mm, "end": v(-75.4, 73.13) * mm});
            skLineSegment(sketch, "E78.5.0.3", {"start": v(-75.4, 77.75) * mm, "end": v(-70.78, 77.75) * mm});
            skLineSegment(sketch, "E78.5.1.0", {"start": v(-70.78, 65.05) * mm, "end": v(-70.78, 60.43) * mm});
            skLineSegment(sketch, "E78.5.1.1", {"start": v(-75.4, 60.43) * mm, "end": v(-70.78, 60.43) * mm});
            skLineSegment(sketch, "E78.5.1.2", {"start": v(-75.4, 65.05) * mm, "end": v(-75.4, 60.43) * mm});
            skLineSegment(sketch, "E78.5.1.3", {"start": v(-75.4, 65.05) * mm, "end": v(-70.78, 65.05) * mm});
            skLineSegment(sketch, "E78.5.10.0", {"start": v(-70.78, -49.25) * mm, "end": v(-70.78, -53.87) * mm});
            skLineSegment(sketch, "E78.5.10.1", {"start": v(-75.4, -53.87) * mm, "end": v(-70.78, -53.87) * mm});
            skLineSegment(sketch, "E78.5.10.2", {"start": v(-75.4, -49.25) * mm, "end": v(-75.4, -53.87) * mm});
            skLineSegment(sketch, "E78.5.10.3", {"start": v(-75.4, -49.25) * mm, "end": v(-70.78, -49.25) * mm});
            skLineSegment(sketch, "E78.5.11.0", {"start": v(-70.78, -61.95) * mm, "end": v(-70.78, -66.57) * mm});
            skLineSegment(sketch, "E78.5.11.1", {"start": v(-75.4, -66.57) * mm, "end": v(-70.78, -66.57) * mm});
            skLineSegment(sketch, "E78.5.11.2", {"start": v(-75.4, -61.95) * mm, "end": v(-75.4, -66.57) * mm});
            skLineSegment(sketch, "E78.5.11.3", {"start": v(-75.4, -61.95) * mm, "end": v(-70.78, -61.95) * mm});
            skLineSegment(sketch, "E78.6.0.0", {"start": v(-58.08, 77.75) * mm, "end": v(-58.08, 73.13) * mm});
            skLineSegment(sketch, "E78.6.0.1", {"start": v(-62.7, 73.13) * mm, "end": v(-58.08, 73.13) * mm});
            skLineSegment(sketch, "E78.6.0.2", {"start": v(-62.7, 77.75) * mm, "end": v(-62.7, 73.13) * mm});
            skLineSegment(sketch, "E78.6.0.3", {"start": v(-62.7, 77.75) * mm, "end": v(-58.08, 77.75) * mm});
            skLineSegment(sketch, "E78.6.1.0", {"start": v(-58.08, 65.05) * mm, "end": v(-58.08, 60.43) * mm});
            skLineSegment(sketch, "E78.6.1.1", {"start": v(-62.7, 60.43) * mm, "end": v(-58.08, 60.43) * mm});
            skLineSegment(sketch, "E78.6.1.2", {"start": v(-62.7, 65.05) * mm, "end": v(-62.7, 60.43) * mm});
            skLineSegment(sketch, "E78.6.1.3", {"start": v(-62.7, 65.05) * mm, "end": v(-58.08, 65.05) * mm});
            skLineSegment(sketch, "E78.6.10.0", {"start": v(-58.08, -49.25) * mm, "end": v(-58.08, -53.87) * mm});
            skLineSegment(sketch, "E78.6.10.1", {"start": v(-62.7, -53.87) * mm, "end": v(-58.08, -53.87) * mm});
            skLineSegment(sketch, "E78.6.10.2", {"start": v(-62.7, -49.25) * mm, "end": v(-62.7, -53.87) * mm});
            skLineSegment(sketch, "E78.6.10.3", {"start": v(-62.7, -49.25) * mm, "end": v(-58.08, -49.25) * mm});
            skLineSegment(sketch, "E78.6.11.0", {"start": v(-58.08, -61.95) * mm, "end": v(-58.08, -66.57) * mm});
            skLineSegment(sketch, "E78.6.11.1", {"start": v(-62.7, -66.57) * mm, "end": v(-58.08, -66.57) * mm});
            skLineSegment(sketch, "E78.6.11.2", {"start": v(-62.7, -61.95) * mm, "end": v(-62.7, -66.57) * mm});
            skLineSegment(sketch, "E78.6.11.3", {"start": v(-62.7, -61.95) * mm, "end": v(-58.08, -61.95) * mm});
            skLineSegment(sketch, "E78.7.0.0", {"start": v(-45.38, 77.75) * mm, "end": v(-45.38, 73.13) * mm});
            skLineSegment(sketch, "E78.7.0.1", {"start": v(-50, 73.13) * mm, "end": v(-45.38, 73.13) * mm});
            skLineSegment(sketch, "E78.7.0.2", {"start": v(-50, 77.75) * mm, "end": v(-50, 73.13) * mm});
            skLineSegment(sketch, "E78.7.0.3", {"start": v(-50, 77.75) * mm, "end": v(-45.38, 77.75) * mm});
            skLineSegment(sketch, "E78.7.1.0", {"start": v(-45.38, 65.05) * mm, "end": v(-45.38, 60.43) * mm});
            skLineSegment(sketch, "E78.7.1.1", {"start": v(-50, 60.43) * mm, "end": v(-45.38, 60.43) * mm});
            skLineSegment(sketch, "E78.7.1.2", {"start": v(-50, 65.05) * mm, "end": v(-50, 60.43) * mm});
            skLineSegment(sketch, "E78.7.1.3", {"start": v(-50, 65.05) * mm, "end": v(-45.38, 65.05) * mm});
            skLineSegment(sketch, "E78.7.10.0", {"start": v(-45.38, -49.25) * mm, "end": v(-45.38, -53.87) * mm});
            skLineSegment(sketch, "E78.7.10.1", {"start": v(-50, -53.87) * mm, "end": v(-45.38, -53.87) * mm});
            skLineSegment(sketch, "E78.7.10.2", {"start": v(-50, -49.25) * mm, "end": v(-50, -53.87) * mm});
            skLineSegment(sketch, "E78.7.10.3", {"start": v(-50, -49.25) * mm, "end": v(-45.38, -49.25) * mm});
            skLineSegment(sketch, "E78.7.11.0", {"start": v(-45.38, -61.95) * mm, "end": v(-45.38, -66.57) * mm});
            skLineSegment(sketch, "E78.7.11.1", {"start": v(-50, -66.57) * mm, "end": v(-45.38, -66.57) * mm});
            skLineSegment(sketch, "E78.7.11.2", {"start": v(-50, -61.95) * mm, "end": v(-50, -66.57) * mm});
            skLineSegment(sketch, "E78.7.11.3", {"start": v(-50, -61.95) * mm, "end": v(-45.38, -61.95) * mm});
            skLineSegment(sketch, "E78.8.0.0", {"start": v(-32.68, 77.75) * mm, "end": v(-32.68, 73.13) * mm});
            skLineSegment(sketch, "E78.8.0.1", {"start": v(-37.3, 73.13) * mm, "end": v(-32.68, 73.13) * mm});
            skLineSegment(sketch, "E78.8.0.2", {"start": v(-37.3, 77.75) * mm, "end": v(-37.3, 73.13) * mm});
            skLineSegment(sketch, "E78.8.0.3", {"start": v(-37.3, 77.75) * mm, "end": v(-32.68, 77.75) * mm});
            skLineSegment(sketch, "E78.8.1.0", {"start": v(-32.68, 65.05) * mm, "end": v(-32.68, 60.43) * mm});
            skLineSegment(sketch, "E78.8.1.1", {"start": v(-37.3, 60.43) * mm, "end": v(-32.68, 60.43) * mm});
            skLineSegment(sketch, "E78.8.1.2", {"start": v(-37.3, 65.05) * mm, "end": v(-37.3, 60.43) * mm});
            skLineSegment(sketch, "E78.8.1.3", {"start": v(-37.3, 65.05) * mm, "end": v(-32.68, 65.05) * mm});
            skLineSegment(sketch, "E78.8.10.0", {"start": v(-32.68, -49.25) * mm, "end": v(-32.68, -53.87) * mm});
            skLineSegment(sketch, "E78.8.10.1", {"start": v(-37.3, -53.87) * mm, "end": v(-32.68, -53.87) * mm});
            skLineSegment(sketch, "E78.8.10.2", {"start": v(-37.3, -49.25) * mm, "end": v(-37.3, -53.87) * mm});
            skLineSegment(sketch, "E78.8.10.3", {"start": v(-37.3, -49.25) * mm, "end": v(-32.68, -49.25) * mm});
            skLineSegment(sketch, "E78.8.11.0", {"start": v(-32.68, -61.95) * mm, "end": v(-32.68, -66.57) * mm});
            skLineSegment(sketch, "E78.8.11.1", {"start": v(-37.3, -66.57) * mm, "end": v(-32.68, -66.57) * mm});
            skLineSegment(sketch, "E78.8.11.2", {"start": v(-37.3, -61.95) * mm, "end": v(-37.3, -66.57) * mm});
            skLineSegment(sketch, "E78.8.11.3", {"start": v(-37.3, -61.95) * mm, "end": v(-32.68, -61.95) * mm});
            skLineSegment(sketch, "E78.9.0.0", {"start": v(-19.98, 77.75) * mm, "end": v(-19.98, 73.13) * mm});
            skLineSegment(sketch, "E78.9.0.1", {"start": v(-24.6, 73.13) * mm, "end": v(-19.98, 73.13) * mm});
            skLineSegment(sketch, "E78.9.0.2", {"start": v(-24.6, 77.75) * mm, "end": v(-24.6, 73.13) * mm});
            skLineSegment(sketch, "E78.9.0.3", {"start": v(-24.6, 77.75) * mm, "end": v(-19.98, 77.75) * mm});
            skLineSegment(sketch, "E78.9.1.0", {"start": v(-19.98, 65.05) * mm, "end": v(-19.98, 60.43) * mm});
            skLineSegment(sketch, "E78.9.1.1", {"start": v(-24.6, 60.43) * mm, "end": v(-19.98, 60.43) * mm});
            skLineSegment(sketch, "E78.9.1.2", {"start": v(-24.6, 65.05) * mm, "end": v(-24.6, 60.43) * mm});
            skLineSegment(sketch, "E78.9.1.3", {"start": v(-24.6, 65.05) * mm, "end": v(-19.98, 65.05) * mm});
            skLineSegment(sketch, "E78.9.10.0", {"start": v(-19.98, -49.25) * mm, "end": v(-19.98, -53.87) * mm});
            skLineSegment(sketch, "E78.9.10.1", {"start": v(-24.6, -53.87) * mm, "end": v(-19.98, -53.87) * mm});
            skLineSegment(sketch, "E78.9.10.2", {"start": v(-24.6, -49.25) * mm, "end": v(-24.6, -53.87) * mm});
            skLineSegment(sketch, "E78.9.10.3", {"start": v(-24.6, -49.25) * mm, "end": v(-19.98, -49.25) * mm});
            skLineSegment(sketch, "E78.9.11.0", {"start": v(-19.98, -61.95) * mm, "end": v(-19.98, -66.57) * mm});
            skLineSegment(sketch, "E78.9.11.1", {"start": v(-24.6, -66.57) * mm, "end": v(-19.98, -66.57) * mm});
            skLineSegment(sketch, "E78.9.11.2", {"start": v(-24.6, -61.95) * mm, "end": v(-24.6, -66.57) * mm});
            skLineSegment(sketch, "E78.9.11.3", {"start": v(-24.6, -61.95) * mm, "end": v(-19.98, -61.95) * mm});
            skLineSegment(sketch, "E78.10.0.0", {"start": v(-7.28, 77.75) * mm, "end": v(-7.28, 73.13) * mm});
            skLineSegment(sketch, "E78.10.0.1", {"start": v(-11.9, 73.13) * mm, "end": v(-7.28, 73.13) * mm});
            skLineSegment(sketch, "E78.10.0.2", {"start": v(-11.9, 77.75) * mm, "end": v(-11.9, 73.13) * mm});
            skLineSegment(sketch, "E78.10.0.3", {"start": v(-11.9, 77.75) * mm, "end": v(-7.28, 77.75) * mm});
            skLineSegment(sketch, "E78.10.1.0", {"start": v(-7.28, 65.05) * mm, "end": v(-7.28, 60.43) * mm});
            skLineSegment(sketch, "E78.10.1.1", {"start": v(-11.9, 60.43) * mm, "end": v(-7.28, 60.43) * mm});
            skLineSegment(sketch, "E78.10.1.2", {"start": v(-11.9, 65.05) * mm, "end": v(-11.9, 60.43) * mm});
            skLineSegment(sketch, "E78.10.1.3", {"start": v(-11.9, 65.05) * mm, "end": v(-7.28, 65.05) * mm});
            skLineSegment(sketch, "E78.10.10.0", {"start": v(-7.28, -49.25) * mm, "end": v(-7.28, -53.87) * mm});
            skLineSegment(sketch, "E78.10.10.1", {"start": v(-11.9, -53.87) * mm, "end": v(-7.28, -53.87) * mm});
            skLineSegment(sketch, "E78.10.10.2", {"start": v(-11.9, -49.25) * mm, "end": v(-11.9, -53.87) * mm});
            skLineSegment(sketch, "E78.10.10.3", {"start": v(-11.9, -49.25) * mm, "end": v(-7.28, -49.25) * mm});
            skLineSegment(sketch, "E78.10.11.0", {"start": v(-7.28, -61.95) * mm, "end": v(-7.28, -66.57) * mm});
            skLineSegment(sketch, "E78.10.11.1", {"start": v(-11.9, -66.57) * mm, "end": v(-7.28, -66.57) * mm});
            skLineSegment(sketch, "E78.10.11.2", {"start": v(-11.9, -61.95) * mm, "end": v(-11.9, -66.57) * mm});
            skLineSegment(sketch, "E78.10.11.3", {"start": v(-11.9, -61.95) * mm, "end": v(-7.28, -61.95) * mm});
            skLineSegment(sketch, "E78.11.0.0", {"start": v(5.42, 77.75) * mm, "end": v(5.42, 73.13) * mm});
            skLineSegment(sketch, "E78.11.0.1", {"start": v(0.8, 73.13) * mm, "end": v(5.42, 73.13) * mm});
            skLineSegment(sketch, "E78.11.0.2", {"start": v(0.8, 77.75) * mm, "end": v(0.8, 73.13) * mm});
            skLineSegment(sketch, "E78.11.0.3", {"start": v(0.8, 77.75) * mm, "end": v(5.42, 77.75) * mm});
            skLineSegment(sketch, "E78.11.1.0", {"start": v(5.42, 65.05) * mm, "end": v(5.42, 60.43) * mm});
            skLineSegment(sketch, "E78.11.1.1", {"start": v(0.8, 60.43) * mm, "end": v(5.42, 60.43) * mm});
            skLineSegment(sketch, "E78.11.1.2", {"start": v(0.8, 65.05) * mm, "end": v(0.8, 60.43) * mm});
            skLineSegment(sketch, "E78.11.1.3", {"start": v(0.8, 65.05) * mm, "end": v(5.42, 65.05) * mm});
            skLineSegment(sketch, "E78.11.10.0", {"start": v(5.42, -49.25) * mm, "end": v(5.42, -53.87) * mm});
            skLineSegment(sketch, "E78.11.10.1", {"start": v(0.8, -53.87) * mm, "end": v(5.42, -53.87) * mm});
            skLineSegment(sketch, "E78.11.10.2", {"start": v(0.8, -49.25) * mm, "end": v(0.8, -53.87) * mm});
            skLineSegment(sketch, "E78.11.10.3", {"start": v(0.8, -49.25) * mm, "end": v(5.42, -49.25) * mm});
            skLineSegment(sketch, "E78.11.11.0", {"start": v(5.42, -61.95) * mm, "end": v(5.42, -66.57) * mm});
            skLineSegment(sketch, "E78.11.11.1", {"start": v(0.8, -66.57) * mm, "end": v(5.42, -66.57) * mm});
            skLineSegment(sketch, "E78.11.11.2", {"start": v(0.8, -61.95) * mm, "end": v(0.8, -66.57) * mm});
            skLineSegment(sketch, "E78.11.11.3", {"start": v(0.8, -61.95) * mm, "end": v(5.42, -61.95) * mm});
            skLineSegment(sketch, "E78.12.0.0", {"start": v(18.12, 77.75) * mm, "end": v(18.12, 73.13) * mm});
            skLineSegment(sketch, "E78.12.0.1", {"start": v(13.5, 73.13) * mm, "end": v(18.12, 73.13) * mm});
            skLineSegment(sketch, "E78.12.0.2", {"start": v(13.5, 77.75) * mm, "end": v(13.5, 73.13) * mm});
            skLineSegment(sketch, "E78.12.0.3", {"start": v(13.5, 77.75) * mm, "end": v(18.12, 77.75) * mm});
            skLineSegment(sketch, "E78.12.1.0", {"start": v(18.12, 65.05) * mm, "end": v(18.12, 60.43) * mm});
            skLineSegment(sketch, "E78.12.1.1", {"start": v(13.5, 60.43) * mm, "end": v(18.12, 60.43) * mm});
            skLineSegment(sketch, "E78.12.1.2", {"start": v(13.5, 65.05) * mm, "end": v(13.5, 60.43) * mm});
            skLineSegment(sketch, "E78.12.1.3", {"start": v(13.5, 65.05) * mm, "end": v(18.12, 65.05) * mm});
            skLineSegment(sketch, "E78.12.10.0", {"start": v(18.12, -49.25) * mm, "end": v(18.12, -53.87) * mm});
            skLineSegment(sketch, "E78.12.10.1", {"start": v(13.5, -53.87) * mm, "end": v(18.12, -53.87) * mm});
            skLineSegment(sketch, "E78.12.10.2", {"start": v(13.5, -49.25) * mm, "end": v(13.5, -53.87) * mm});
            skLineSegment(sketch, "E78.12.10.3", {"start": v(13.5, -49.25) * mm, "end": v(18.12, -49.25) * mm});
            skLineSegment(sketch, "E78.12.11.0", {"start": v(18.12, -61.95) * mm, "end": v(18.12, -66.57) * mm});
            skLineSegment(sketch, "E78.12.11.1", {"start": v(13.5, -66.57) * mm, "end": v(18.12, -66.57) * mm});
            skLineSegment(sketch, "E78.12.11.2", {"start": v(13.5, -61.95) * mm, "end": v(13.5, -66.57) * mm});
            skLineSegment(sketch, "E78.12.11.3", {"start": v(13.5, -61.95) * mm, "end": v(18.12, -61.95) * mm});
            skLineSegment(sketch, "E78.13.0.0", {"start": v(30.82, 77.75) * mm, "end": v(30.82, 73.13) * mm});
            skLineSegment(sketch, "E78.13.0.1", {"start": v(26.2, 73.13) * mm, "end": v(30.82, 73.13) * mm});
            skLineSegment(sketch, "E78.13.0.2", {"start": v(26.2, 77.75) * mm, "end": v(26.2, 73.13) * mm});
            skLineSegment(sketch, "E78.13.0.3", {"start": v(26.2, 77.75) * mm, "end": v(30.82, 77.75) * mm});
            skLineSegment(sketch, "E78.13.1.0", {"start": v(30.82, 65.05) * mm, "end": v(30.82, 60.43) * mm});
            skLineSegment(sketch, "E78.13.1.1", {"start": v(26.2, 60.43) * mm, "end": v(30.82, 60.43) * mm});
            skLineSegment(sketch, "E78.13.1.2", {"start": v(26.2, 65.05) * mm, "end": v(26.2, 60.43) * mm});
            skLineSegment(sketch, "E78.13.1.3", {"start": v(26.2, 65.05) * mm, "end": v(30.82, 65.05) * mm});
            skLineSegment(sketch, "E78.13.2.0", {"start": v(30.82, 52.35) * mm, "end": v(30.82, 47.73) * mm});
            skLineSegment(sketch, "E78.13.2.1", {"start": v(26.2, 47.73) * mm, "end": v(30.82, 47.73) * mm});
            skLineSegment(sketch, "E78.13.2.2", {"start": v(26.2, 52.35) * mm, "end": v(26.2, 47.73) * mm});
            skLineSegment(sketch, "E78.13.2.3", {"start": v(26.2, 52.35) * mm, "end": v(30.82, 52.35) * mm});
            skLineSegment(sketch, "E78.13.3.0", {"start": v(30.82, 39.65) * mm, "end": v(30.82, 35.03) * mm});
            skLineSegment(sketch, "E78.13.3.1", {"start": v(26.2, 35.03) * mm, "end": v(30.82, 35.03) * mm});
            skLineSegment(sketch, "E78.13.3.2", {"start": v(26.2, 39.65) * mm, "end": v(26.2, 35.03) * mm});
            skLineSegment(sketch, "E78.13.3.3", {"start": v(26.2, 39.65) * mm, "end": v(30.82, 39.65) * mm});
            skLineSegment(sketch, "E78.13.4.0", {"start": v(30.82, 26.95) * mm, "end": v(30.82, 22.33) * mm});
            skLineSegment(sketch, "E78.13.4.1", {"start": v(26.2, 22.33) * mm, "end": v(30.82, 22.33) * mm});
            skLineSegment(sketch, "E78.13.4.2", {"start": v(26.2, 26.95) * mm, "end": v(26.2, 22.33) * mm});
            skLineSegment(sketch, "E78.13.4.3", {"start": v(26.2, 26.95) * mm, "end": v(30.82, 26.95) * mm});
            skLineSegment(sketch, "E78.13.5.0", {"start": v(30.82, 14.25) * mm, "end": v(30.82, 9.63) * mm});
            skLineSegment(sketch, "E78.13.5.1", {"start": v(26.2, 9.63) * mm, "end": v(30.82, 9.63) * mm});
            skLineSegment(sketch, "E78.13.5.2", {"start": v(26.2, 14.25) * mm, "end": v(26.2, 9.63) * mm});
            skLineSegment(sketch, "E78.13.5.3", {"start": v(26.2, 14.25) * mm, "end": v(30.82, 14.25) * mm});
            skLineSegment(sketch, "E78.13.6.0", {"start": v(30.82, 1.55) * mm, "end": v(30.82, -3.07) * mm});
            skLineSegment(sketch, "E78.13.6.1", {"start": v(26.2, -3.07) * mm, "end": v(30.82, -3.07) * mm});
            skLineSegment(sketch, "E78.13.6.2", {"start": v(26.2, 1.55) * mm, "end": v(26.2, -3.07) * mm});
            skLineSegment(sketch, "E78.13.6.3", {"start": v(26.2, 1.55) * mm, "end": v(30.82, 1.55) * mm});
            skLineSegment(sketch, "E78.13.7.0", {"start": v(30.82, -11.15) * mm, "end": v(30.82, -15.77) * mm});
            skLineSegment(sketch, "E78.13.7.1", {"start": v(26.2, -15.77) * mm, "end": v(30.82, -15.77) * mm});
            skLineSegment(sketch, "E78.13.7.2", {"start": v(26.2, -11.15) * mm, "end": v(26.2, -15.77) * mm});
            skLineSegment(sketch, "E78.13.7.3", {"start": v(26.2, -11.15) * mm, "end": v(30.82, -11.15) * mm});
            skLineSegment(sketch, "E78.13.8.0", {"start": v(30.82, -23.85) * mm, "end": v(30.82, -28.47) * mm});
            skLineSegment(sketch, "E78.13.8.1", {"start": v(26.2, -28.47) * mm, "end": v(30.82, -28.47) * mm});
            skLineSegment(sketch, "E78.13.8.2", {"start": v(26.2, -23.85) * mm, "end": v(26.2, -28.47) * mm});
            skLineSegment(sketch, "E78.13.8.3", {"start": v(26.2, -23.85) * mm, "end": v(30.82, -23.85) * mm});
            skLineSegment(sketch, "E78.13.9.0", {"start": v(30.82, -36.55) * mm, "end": v(30.82, -41.17) * mm});
            skLineSegment(sketch, "E78.13.9.1", {"start": v(26.2, -41.17) * mm, "end": v(30.82, -41.17) * mm});
            skLineSegment(sketch, "E78.13.9.2", {"start": v(26.2, -36.55) * mm, "end": v(26.2, -41.17) * mm});
            skLineSegment(sketch, "E78.13.9.3", {"start": v(26.2, -36.55) * mm, "end": v(30.82, -36.55) * mm});
            skLineSegment(sketch, "E78.13.10.0", {"start": v(30.82, -49.25) * mm, "end": v(30.82, -53.87) * mm});
            skLineSegment(sketch, "E78.13.10.1", {"start": v(26.2, -53.87) * mm, "end": v(30.82, -53.87) * mm});
            skLineSegment(sketch, "E78.13.10.2", {"start": v(26.2, -49.25) * mm, "end": v(26.2, -53.87) * mm});
            skLineSegment(sketch, "E78.13.10.3", {"start": v(26.2, -49.25) * mm, "end": v(30.82, -49.25) * mm});
            skLineSegment(sketch, "E78.13.11.0", {"start": v(30.82, -61.95) * mm, "end": v(30.82, -66.57) * mm});
            skLineSegment(sketch, "E78.13.11.1", {"start": v(26.2, -66.57) * mm, "end": v(30.82, -66.57) * mm});
            skLineSegment(sketch, "E78.13.11.2", {"start": v(26.2, -61.95) * mm, "end": v(26.2, -66.57) * mm});
            skLineSegment(sketch, "E78.13.11.3", {"start": v(26.2, -61.95) * mm, "end": v(30.82, -61.95) * mm});
            skLineSegment(sketch, "E78.14.0.0", {"start": v(43.52, 77.75) * mm, "end": v(43.52, 73.13) * mm});
            skLineSegment(sketch, "E78.14.0.1", {"start": v(38.9, 73.13) * mm, "end": v(43.52, 73.13) * mm});
            skLineSegment(sketch, "E78.14.0.2", {"start": v(38.9, 77.75) * mm, "end": v(38.9, 73.13) * mm});
            skLineSegment(sketch, "E78.14.0.3", {"start": v(38.9, 77.75) * mm, "end": v(43.52, 77.75) * mm});
            skLineSegment(sketch, "E78.14.1.0", {"start": v(43.52, 65.05) * mm, "end": v(43.52, 60.43) * mm});
            skLineSegment(sketch, "E78.14.1.1", {"start": v(38.9, 60.43) * mm, "end": v(43.52, 60.43) * mm});
            skLineSegment(sketch, "E78.14.1.2", {"start": v(38.9, 65.05) * mm, "end": v(38.9, 60.43) * mm});
            skLineSegment(sketch, "E78.14.1.3", {"start": v(38.9, 65.05) * mm, "end": v(43.52, 65.05) * mm});
            skLineSegment(sketch, "E78.14.2.0", {"start": v(43.52, 52.35) * mm, "end": v(43.52, 47.73) * mm});
            skLineSegment(sketch, "E78.14.2.1", {"start": v(38.9, 47.73) * mm, "end": v(43.52, 47.73) * mm});
            skLineSegment(sketch, "E78.14.2.2", {"start": v(38.9, 52.35) * mm, "end": v(38.9, 47.73) * mm});
            skLineSegment(sketch, "E78.14.2.3", {"start": v(38.9, 52.35) * mm, "end": v(43.52, 52.35) * mm});
            skLineSegment(sketch, "E78.14.3.0", {"start": v(43.52, 39.65) * mm, "end": v(43.52, 35.03) * mm});
            skLineSegment(sketch, "E78.14.3.1", {"start": v(38.9, 35.03) * mm, "end": v(43.52, 35.03) * mm});
            skLineSegment(sketch, "E78.14.3.2", {"start": v(38.9, 39.65) * mm, "end": v(38.9, 35.03) * mm});
            skLineSegment(sketch, "E78.14.3.3", {"start": v(38.9, 39.65) * mm, "end": v(43.52, 39.65) * mm});
            skLineSegment(sketch, "E78.14.4.0", {"start": v(43.52, 26.95) * mm, "end": v(43.52, 22.33) * mm});
            skLineSegment(sketch, "E78.14.4.1", {"start": v(38.9, 22.33) * mm, "end": v(43.52, 22.33) * mm});
            skLineSegment(sketch, "E78.14.4.2", {"start": v(38.9, 26.95) * mm, "end": v(38.9, 22.33) * mm});
            skLineSegment(sketch, "E78.14.4.3", {"start": v(38.9, 26.95) * mm, "end": v(43.52, 26.95) * mm});
            skLineSegment(sketch, "E78.14.5.0", {"start": v(43.52, 14.25) * mm, "end": v(43.52, 9.63) * mm});
            skLineSegment(sketch, "E78.14.5.1", {"start": v(38.9, 9.63) * mm, "end": v(43.52, 9.63) * mm});
            skLineSegment(sketch, "E78.14.5.2", {"start": v(38.9, 14.25) * mm, "end": v(38.9, 9.63) * mm});
            skLineSegment(sketch, "E78.14.5.3", {"start": v(38.9, 14.25) * mm, "end": v(43.52, 14.25) * mm});
            skLineSegment(sketch, "E78.14.6.0", {"start": v(43.52, 1.55) * mm, "end": v(43.52, -3.07) * mm});
            skLineSegment(sketch, "E78.14.6.1", {"start": v(38.9, -3.07) * mm, "end": v(43.52, -3.07) * mm});
            skLineSegment(sketch, "E78.14.6.2", {"start": v(38.9, 1.55) * mm, "end": v(38.9, -3.07) * mm});
            skLineSegment(sketch, "E78.14.6.3", {"start": v(38.9, 1.55) * mm, "end": v(43.52, 1.55) * mm});
            skLineSegment(sketch, "E78.14.7.0", {"start": v(43.52, -11.15) * mm, "end": v(43.52, -15.77) * mm});
            skLineSegment(sketch, "E78.14.7.1", {"start": v(38.9, -15.77) * mm, "end": v(43.52, -15.77) * mm});
            skLineSegment(sketch, "E78.14.7.2", {"start": v(38.9, -11.15) * mm, "end": v(38.9, -15.77) * mm});
            skLineSegment(sketch, "E78.14.7.3", {"start": v(38.9, -11.15) * mm, "end": v(43.52, -11.15) * mm});
            skLineSegment(sketch, "E78.14.8.0", {"start": v(43.52, -23.85) * mm, "end": v(43.52, -28.47) * mm});
            skLineSegment(sketch, "E78.14.8.1", {"start": v(38.9, -28.47) * mm, "end": v(43.52, -28.47) * mm});
            skLineSegment(sketch, "E78.14.8.2", {"start": v(38.9, -23.85) * mm, "end": v(38.9, -28.47) * mm});
            skLineSegment(sketch, "E78.14.8.3", {"start": v(38.9, -23.85) * mm, "end": v(43.52, -23.85) * mm});
            skLineSegment(sketch, "E78.14.9.0", {"start": v(43.52, -36.55) * mm, "end": v(43.52, -41.17) * mm});
            skLineSegment(sketch, "E78.14.9.1", {"start": v(38.9, -41.17) * mm, "end": v(43.52, -41.17) * mm});
            skLineSegment(sketch, "E78.14.9.2", {"start": v(38.9, -36.55) * mm, "end": v(38.9, -41.17) * mm});
            skLineSegment(sketch, "E78.14.9.3", {"start": v(38.9, -36.55) * mm, "end": v(43.52, -36.55) * mm});
            skLineSegment(sketch, "E78.14.10.0", {"start": v(43.52, -49.25) * mm, "end": v(43.52, -53.87) * mm});
            skLineSegment(sketch, "E78.14.10.1", {"start": v(38.9, -53.87) * mm, "end": v(43.52, -53.87) * mm});
            skLineSegment(sketch, "E78.14.10.2", {"start": v(38.9, -49.25) * mm, "end": v(38.9, -53.87) * mm});
            skLineSegment(sketch, "E78.14.10.3", {"start": v(38.9, -49.25) * mm, "end": v(43.52, -49.25) * mm});
            skLineSegment(sketch, "E78.14.11.0", {"start": v(43.52, -61.95) * mm, "end": v(43.52, -66.57) * mm});
            skLineSegment(sketch, "E78.14.11.1", {"start": v(38.9, -66.57) * mm, "end": v(43.52, -66.57) * mm});
            skLineSegment(sketch, "E78.14.11.2", {"start": v(38.9, -61.95) * mm, "end": v(38.9, -66.57) * mm});
            skLineSegment(sketch, "E78.14.11.3", {"start": v(38.9, -61.95) * mm, "end": v(43.52, -61.95) * mm});
            skLineSegment(sketch, "E78.15.0.0", {"start": v(56.22, 77.75) * mm, "end": v(56.22, 73.13) * mm});
            skLineSegment(sketch, "E78.15.0.1", {"start": v(51.6, 73.13) * mm, "end": v(56.22, 73.13) * mm});
            skLineSegment(sketch, "E78.15.0.2", {"start": v(51.6, 77.75) * mm, "end": v(51.6, 73.13) * mm});
            skLineSegment(sketch, "E78.15.0.3", {"start": v(51.6, 77.75) * mm, "end": v(56.22, 77.75) * mm});
            skLineSegment(sketch, "E78.15.1.0", {"start": v(56.22, 65.05) * mm, "end": v(56.22, 60.43) * mm});
            skLineSegment(sketch, "E78.15.1.1", {"start": v(51.6, 60.43) * mm, "end": v(56.22, 60.43) * mm});
            skLineSegment(sketch, "E78.15.1.2", {"start": v(51.6, 65.05) * mm, "end": v(51.6, 60.43) * mm});
            skLineSegment(sketch, "E78.15.1.3", {"start": v(51.6, 65.05) * mm, "end": v(56.22, 65.05) * mm});
            skLineSegment(sketch, "E78.15.2.0", {"start": v(56.22, 52.35) * mm, "end": v(56.22, 47.73) * mm});
            skLineSegment(sketch, "E78.15.2.1", {"start": v(51.6, 47.73) * mm, "end": v(56.22, 47.73) * mm});
            skLineSegment(sketch, "E78.15.2.2", {"start": v(51.6, 52.35) * mm, "end": v(51.6, 47.73) * mm});
            skLineSegment(sketch, "E78.15.2.3", {"start": v(51.6, 52.35) * mm, "end": v(56.22, 52.35) * mm});
            skLineSegment(sketch, "E78.15.3.0", {"start": v(56.22, 39.65) * mm, "end": v(56.22, 35.03) * mm});
            skLineSegment(sketch, "E78.15.3.1", {"start": v(51.6, 35.03) * mm, "end": v(56.22, 35.03) * mm});
            skLineSegment(sketch, "E78.15.3.2", {"start": v(51.6, 39.65) * mm, "end": v(51.6, 35.03) * mm});
            skLineSegment(sketch, "E78.15.3.3", {"start": v(51.6, 39.65) * mm, "end": v(56.22, 39.65) * mm});
            skLineSegment(sketch, "E78.15.4.0", {"start": v(56.22, 26.95) * mm, "end": v(56.22, 22.33) * mm});
            skLineSegment(sketch, "E78.15.4.1", {"start": v(51.6, 22.33) * mm, "end": v(56.22, 22.33) * mm});
            skLineSegment(sketch, "E78.15.4.2", {"start": v(51.6, 26.95) * mm, "end": v(51.6, 22.33) * mm});
            skLineSegment(sketch, "E78.15.4.3", {"start": v(51.6, 26.95) * mm, "end": v(56.22, 26.95) * mm});
            skLineSegment(sketch, "E78.15.5.0", {"start": v(56.22, 14.25) * mm, "end": v(56.22, 9.63) * mm});
            skLineSegment(sketch, "E78.15.5.1", {"start": v(51.6, 9.63) * mm, "end": v(56.22, 9.63) * mm});
            skLineSegment(sketch, "E78.15.5.2", {"start": v(51.6, 14.25) * mm, "end": v(51.6, 9.63) * mm});
            skLineSegment(sketch, "E78.15.5.3", {"start": v(51.6, 14.25) * mm, "end": v(56.22, 14.25) * mm});
            skLineSegment(sketch, "E78.15.6.0", {"start": v(56.22, 1.55) * mm, "end": v(56.22, -3.07) * mm});
            skLineSegment(sketch, "E78.15.6.1", {"start": v(51.6, -3.07) * mm, "end": v(56.22, -3.07) * mm});
            skLineSegment(sketch, "E78.15.6.2", {"start": v(51.6, 1.55) * mm, "end": v(51.6, -3.07) * mm});
            skLineSegment(sketch, "E78.15.6.3", {"start": v(51.6, 1.55) * mm, "end": v(56.22, 1.55) * mm});
            skLineSegment(sketch, "E78.15.7.0", {"start": v(56.22, -11.15) * mm, "end": v(56.22, -15.77) * mm});
            skLineSegment(sketch, "E78.15.7.1", {"start": v(51.6, -15.77) * mm, "end": v(56.22, -15.77) * mm});
            skLineSegment(sketch, "E78.15.7.2", {"start": v(51.6, -11.15) * mm, "end": v(51.6, -15.77) * mm});
            skLineSegment(sketch, "E78.15.7.3", {"start": v(51.6, -11.15) * mm, "end": v(56.22, -11.15) * mm});
            skLineSegment(sketch, "E78.15.8.0", {"start": v(56.22, -23.85) * mm, "end": v(56.22, -28.47) * mm});
            skLineSegment(sketch, "E78.15.8.1", {"start": v(51.6, -28.47) * mm, "end": v(56.22, -28.47) * mm});
            skLineSegment(sketch, "E78.15.8.2", {"start": v(51.6, -23.85) * mm, "end": v(51.6, -28.47) * mm});
            skLineSegment(sketch, "E78.15.8.3", {"start": v(51.6, -23.85) * mm, "end": v(56.22, -23.85) * mm});
            skLineSegment(sketch, "E78.15.9.0", {"start": v(56.22, -36.55) * mm, "end": v(56.22, -41.17) * mm});
            skLineSegment(sketch, "E78.15.9.1", {"start": v(51.6, -41.17) * mm, "end": v(56.22, -41.17) * mm});
            skLineSegment(sketch, "E78.15.9.2", {"start": v(51.6, -36.55) * mm, "end": v(51.6, -41.17) * mm});
            skLineSegment(sketch, "E78.15.9.3", {"start": v(51.6, -36.55) * mm, "end": v(56.22, -36.55) * mm});
            skLineSegment(sketch, "E78.15.10.0", {"start": v(56.22, -49.25) * mm, "end": v(56.22, -53.87) * mm});
            skLineSegment(sketch, "E78.15.10.1", {"start": v(51.6, -53.87) * mm, "end": v(56.22, -53.87) * mm});
            skLineSegment(sketch, "E78.15.10.2", {"start": v(51.6, -49.25) * mm, "end": v(51.6, -53.87) * mm});
            skLineSegment(sketch, "E78.15.10.3", {"start": v(51.6, -49.25) * mm, "end": v(56.22, -49.25) * mm});
            skLineSegment(sketch, "E78.15.11.0", {"start": v(56.22, -61.95) * mm, "end": v(56.22, -66.57) * mm});
            skLineSegment(sketch, "E78.15.11.1", {"start": v(51.6, -66.57) * mm, "end": v(56.22, -66.57) * mm});
            skLineSegment(sketch, "E78.15.11.2", {"start": v(51.6, -61.95) * mm, "end": v(51.6, -66.57) * mm});
            skLineSegment(sketch, "E78.15.11.3", {"start": v(51.6, -61.95) * mm, "end": v(56.22, -61.95) * mm});
            skLineSegment(sketch, "E78.direction1", {"start": v(-138.9, 73.13) * mm, "end": v(-126.2, 73.13) * mm, "construction": true});
            skLineSegment(sketch, "E78.direction2", {"start": v(-138.9, 73.13) * mm, "end": v(-138.9, 60.43) * mm, "construction": true});
            skLineSegment(sketch, "E79", {"start": v(56.22, 75.44) * mm, "end": v(60.26, 75.44) * mm});
            skLineSegment(sketch, "E80", {"start": v(-136.6, -66.57) * mm, "end": v(-136.6, -70.6) * mm});
            skLineSegment(sketch, "E81.bottom", {"start": v(-132.56, 71.4) * mm, "end": v(-127.93, 71.4) * mm});
            skLineSegment(sketch, "E81.top", {"start": v(-132.56, 66.78) * mm, "end": v(-127.93, 66.78) * mm});
            skLineSegment(sketch, "E81.left", {"start": v(-132.56, 71.4) * mm, "end": v(-132.56, 66.78) * mm});
            skLineSegment(sketch, "E81.right", {"start": v(-127.93, 71.4) * mm, "end": v(-127.93, 66.78) * mm});
            skLineSegment(sketch, "E82", {"start": v(-134.28, 73.13) * mm, "end": v(-134.28, 71.4) * mm});
            skLineSegment(sketch, "E83", {"start": v(-134.28, 71.4) * mm, "end": v(-132.56, 71.4) * mm});
            skLineSegment(sketch, "E84", {"start": v(-127.93, 71.4) * mm, "end": v(-126.2, 71.4) * mm});
            skLineSegment(sketch, "E85", {"start": v(-126.2, 71.4) * mm, "end": v(-126.2, 73.13) * mm});
            skLineSegment(sketch, "E86", {"start": v(-134.28, 65.05) * mm, "end": v(-134.28, 66.78) * mm});
            skLineSegment(sketch, "E87", {"start": v(-134.28, 66.78) * mm, "end": v(-132.56, 66.78) * mm});
            skLineSegment(sketch, "E88.0.1.1", {"start": v(-132.56, 58.7) * mm, "end": v(-132.56, 54.08) * mm});
            skLineSegment(sketch, "E88.0.2.0", {"start": v(-132.56, 46) * mm, "end": v(-127.93, 46) * mm});
            skLineSegment(sketch, "E88.0.2.1", {"start": v(-132.56, 46) * mm, "end": v(-132.56, 41.38) * mm});
            skLineSegment(sketch, "E88.0.2.2", {"start": v(-132.56, 41.38) * mm, "end": v(-127.93, 41.38) * mm});
            skLineSegment(sketch, "E88.0.2.3", {"start": v(-127.93, 46) * mm, "end": v(-127.93, 41.38) * mm});
            skLineSegment(sketch, "E88.0.3.0", {"start": v(-132.56, 33.3) * mm, "end": v(-127.93, 33.3) * mm});
            skLineSegment(sketch, "E88.0.3.1", {"start": v(-132.56, 33.3) * mm, "end": v(-132.56, 28.68) * mm});
            skLineSegment(sketch, "E88.0.3.2", {"start": v(-132.56, 28.68) * mm, "end": v(-127.93, 28.68) * mm});
            skLineSegment(sketch, "E88.0.3.3", {"start": v(-127.93, 33.3) * mm, "end": v(-127.93, 28.68) * mm});
            skLineSegment(sketch, "E88.0.4.0", {"start": v(-132.56, 20.6) * mm, "end": v(-127.93, 20.6) * mm});
            skLineSegment(sketch, "E88.0.4.1", {"start": v(-132.56, 20.6) * mm, "end": v(-132.56, 15.98) * mm});
            skLineSegment(sketch, "E88.0.4.2", {"start": v(-132.56, 15.98) * mm, "end": v(-127.93, 15.98) * mm});
            skLineSegment(sketch, "E88.0.4.3", {"start": v(-127.93, 20.6) * mm, "end": v(-127.93, 15.98) * mm});
            skLineSegment(sketch, "E88.0.5.0", {"start": v(-132.56, 7.9) * mm, "end": v(-127.93, 7.9) * mm});
            skLineSegment(sketch, "E88.0.5.1", {"start": v(-132.56, 7.9) * mm, "end": v(-132.56, 3.28) * mm});
            skLineSegment(sketch, "E88.0.5.2", {"start": v(-132.56, 3.28) * mm, "end": v(-127.93, 3.28) * mm});
            skLineSegment(sketch, "E88.0.5.3", {"start": v(-127.93, 7.9) * mm, "end": v(-127.93, 3.28) * mm});
            skLineSegment(sketch, "E88.0.6.0", {"start": v(-132.56, -4.8) * mm, "end": v(-127.93, -4.8) * mm});
            skLineSegment(sketch, "E88.0.6.1", {"start": v(-132.56, -4.8) * mm, "end": v(-132.56, -9.42) * mm});
            skLineSegment(sketch, "E88.0.6.2", {"start": v(-132.56, -9.42) * mm, "end": v(-127.93, -9.42) * mm});
            skLineSegment(sketch, "E88.0.6.3", {"start": v(-127.93, -4.8) * mm, "end": v(-127.93, -9.42) * mm});
            skLineSegment(sketch, "E88.0.7.0", {"start": v(-132.56, -17.5) * mm, "end": v(-127.93, -17.5) * mm});
            skLineSegment(sketch, "E88.0.7.1", {"start": v(-132.56, -17.5) * mm, "end": v(-132.56, -22.12) * mm});
            skLineSegment(sketch, "E88.0.7.2", {"start": v(-132.56, -22.12) * mm, "end": v(-127.93, -22.12) * mm});
            skLineSegment(sketch, "E88.0.7.3", {"start": v(-127.93, -17.5) * mm, "end": v(-127.93, -22.12) * mm});
            skLineSegment(sketch, "E88.0.8.0", {"start": v(-132.56, -30.2) * mm, "end": v(-127.93, -30.2) * mm});
            skLineSegment(sketch, "E88.0.8.1", {"start": v(-132.56, -30.2) * mm, "end": v(-132.56, -34.82) * mm});
            skLineSegment(sketch, "E88.0.8.2", {"start": v(-132.56, -34.82) * mm, "end": v(-127.93, -34.82) * mm});
            skLineSegment(sketch, "E88.0.8.3", {"start": v(-127.93, -30.2) * mm, "end": v(-127.93, -34.82) * mm});
            skLineSegment(sketch, "E88.0.10.0", {"start": v(-132.56, -55.6) * mm, "end": v(-127.93, -55.6) * mm});
            skLineSegment(sketch, "E88.0.10.1", {"start": v(-132.56, -55.6) * mm, "end": v(-132.56, -60.22) * mm});
            skLineSegment(sketch, "E88.0.10.2", {"start": v(-132.56, -60.22) * mm, "end": v(-127.93, -60.22) * mm});
            skLineSegment(sketch, "E88.0.10.3", {"start": v(-127.93, -55.6) * mm, "end": v(-127.93, -60.22) * mm});
            skLineSegment(sketch, "E88.1.1.0", {"start": v(-119.86, 58.7) * mm, "end": v(-115.23, 58.7) * mm});
            skLineSegment(sketch, "E88.1.1.1", {"start": v(-119.86, 58.7) * mm, "end": v(-119.86, 54.08) * mm});
            skLineSegment(sketch, "E88.1.1.2", {"start": v(-119.86, 54.08) * mm, "end": v(-115.23, 54.08) * mm});
            skLineSegment(sketch, "E88.1.1.3", {"start": v(-115.23, 58.7) * mm, "end": v(-115.23, 54.08) * mm});
            skLineSegment(sketch, "E88.1.2.0", {"start": v(-119.86, 46) * mm, "end": v(-115.23, 46) * mm});
            skLineSegment(sketch, "E88.1.2.1", {"start": v(-119.86, 46) * mm, "end": v(-119.86, 41.38) * mm});
            skLineSegment(sketch, "E88.1.2.2", {"start": v(-119.86, 41.38) * mm, "end": v(-115.23, 41.38) * mm});
            skLineSegment(sketch, "E88.1.2.3", {"start": v(-115.23, 46) * mm, "end": v(-115.23, 41.38) * mm});
            skLineSegment(sketch, "E88.1.3.0", {"start": v(-119.86, 33.3) * mm, "end": v(-115.23, 33.3) * mm});
            skLineSegment(sketch, "E88.1.3.1", {"start": v(-119.86, 33.3) * mm, "end": v(-119.86, 28.68) * mm});
            skLineSegment(sketch, "E88.1.3.2", {"start": v(-119.86, 28.68) * mm, "end": v(-115.23, 28.68) * mm});
            skLineSegment(sketch, "E88.1.3.3", {"start": v(-115.23, 33.3) * mm, "end": v(-115.23, 28.68) * mm});
            skLineSegment(sketch, "E88.1.4.0", {"start": v(-119.86, 20.6) * mm, "end": v(-115.23, 20.6) * mm});
            skLineSegment(sketch, "E88.1.4.1", {"start": v(-119.86, 20.6) * mm, "end": v(-119.86, 15.98) * mm});
            skLineSegment(sketch, "E88.1.4.2", {"start": v(-119.86, 15.98) * mm, "end": v(-115.23, 15.98) * mm});
            skLineSegment(sketch, "E88.1.4.3", {"start": v(-115.23, 20.6) * mm, "end": v(-115.23, 15.98) * mm});
            skLineSegment(sketch, "E88.1.5.0", {"start": v(-119.86, 7.9) * mm, "end": v(-115.23, 7.9) * mm});
            skLineSegment(sketch, "E88.1.5.1", {"start": v(-119.86, 7.9) * mm, "end": v(-119.86, 3.28) * mm});
            skLineSegment(sketch, "E88.1.5.2", {"start": v(-119.86, 3.28) * mm, "end": v(-115.23, 3.28) * mm});
            skLineSegment(sketch, "E88.1.5.3", {"start": v(-115.23, 7.9) * mm, "end": v(-115.23, 3.28) * mm});
            skLineSegment(sketch, "E88.1.6.0", {"start": v(-119.86, -4.8) * mm, "end": v(-115.23, -4.8) * mm});
            skLineSegment(sketch, "E88.1.6.1", {"start": v(-119.86, -4.8) * mm, "end": v(-119.86, -9.42) * mm});
            skLineSegment(sketch, "E88.1.6.2", {"start": v(-119.86, -9.42) * mm, "end": v(-115.23, -9.42) * mm});
            skLineSegment(sketch, "E88.1.6.3", {"start": v(-115.23, -4.8) * mm, "end": v(-115.23, -9.42) * mm});
            skLineSegment(sketch, "E88.1.7.0", {"start": v(-119.86, -17.5) * mm, "end": v(-115.23, -17.5) * mm});
            skLineSegment(sketch, "E88.1.7.1", {"start": v(-119.86, -17.5) * mm, "end": v(-119.86, -22.12) * mm});
            skLineSegment(sketch, "E88.1.7.2", {"start": v(-119.86, -22.12) * mm, "end": v(-115.23, -22.12) * mm});
            skLineSegment(sketch, "E88.1.7.3", {"start": v(-115.23, -17.5) * mm, "end": v(-115.23, -22.12) * mm});
            skLineSegment(sketch, "E88.1.8.0", {"start": v(-119.86, -30.2) * mm, "end": v(-115.23, -30.2) * mm});
            skLineSegment(sketch, "E88.1.8.1", {"start": v(-119.86, -30.2) * mm, "end": v(-119.86, -34.82) * mm});
            skLineSegment(sketch, "E88.1.8.2", {"start": v(-119.86, -34.82) * mm, "end": v(-115.23, -34.82) * mm});
            skLineSegment(sketch, "E88.1.8.3", {"start": v(-115.23, -30.2) * mm, "end": v(-115.23, -34.82) * mm});
            skLineSegment(sketch, "E88.1.9.0", {"start": v(-119.86, -42.9) * mm, "end": v(-115.23, -42.9) * mm});
            skLineSegment(sketch, "E88.1.9.1", {"start": v(-119.86, -42.9) * mm, "end": v(-119.86, -47.52) * mm});
            skLineSegment(sketch, "E88.1.9.2", {"start": v(-119.86, -47.52) * mm, "end": v(-115.23, -47.52) * mm});
            skLineSegment(sketch, "E88.1.9.3", {"start": v(-115.23, -42.9) * mm, "end": v(-115.23, -47.52) * mm});
            skLineSegment(sketch, "E88.2.0.0", {"start": v(-107.16, 71.4) * mm, "end": v(-102.53, 71.4) * mm});
            skLineSegment(sketch, "E88.2.0.1", {"start": v(-107.16, 71.4) * mm, "end": v(-107.16, 66.78) * mm});
            skLineSegment(sketch, "E88.2.0.2", {"start": v(-107.16, 66.78) * mm, "end": v(-102.53, 66.78) * mm});
            skLineSegment(sketch, "E88.2.0.3", {"start": v(-102.53, 71.4) * mm, "end": v(-102.53, 66.78) * mm});
            skLineSegment(sketch, "E88.2.1.0", {"start": v(-107.16, 58.7) * mm, "end": v(-102.53, 58.7) * mm});
            skLineSegment(sketch, "E88.2.1.1", {"start": v(-107.16, 58.7) * mm, "end": v(-107.16, 54.08) * mm});
            skLineSegment(sketch, "E88.2.1.2", {"start": v(-107.16, 54.08) * mm, "end": v(-102.53, 54.08) * mm});
            skLineSegment(sketch, "E88.2.1.3", {"start": v(-102.53, 58.7) * mm, "end": v(-102.53, 54.08) * mm});
            skLineSegment(sketch, "E88.2.2.0", {"start": v(-107.16, 46) * mm, "end": v(-102.53, 46) * mm});
            skLineSegment(sketch, "E88.2.2.1", {"start": v(-107.16, 46) * mm, "end": v(-107.16, 41.38) * mm});
            skLineSegment(sketch, "E88.2.2.2", {"start": v(-107.16, 41.38) * mm, "end": v(-102.53, 41.38) * mm});
            skLineSegment(sketch, "E88.2.2.3", {"start": v(-102.53, 46) * mm, "end": v(-102.53, 41.38) * mm});
            skLineSegment(sketch, "E88.2.3.0", {"start": v(-107.16, 33.3) * mm, "end": v(-102.53, 33.3) * mm});
            skLineSegment(sketch, "E88.2.3.1", {"start": v(-107.16, 33.3) * mm, "end": v(-107.16, 28.68) * mm});
            skLineSegment(sketch, "E88.2.3.2", {"start": v(-107.16, 28.68) * mm, "end": v(-102.53, 28.68) * mm});
            skLineSegment(sketch, "E88.2.3.3", {"start": v(-102.53, 33.3) * mm, "end": v(-102.53, 28.68) * mm});
            skLineSegment(sketch, "E88.2.4.0", {"start": v(-107.16, 20.6) * mm, "end": v(-102.53, 20.6) * mm});
            skLineSegment(sketch, "E88.2.4.1", {"start": v(-107.16, 20.6) * mm, "end": v(-107.16, 15.98) * mm});
            skLineSegment(sketch, "E88.2.4.2", {"start": v(-107.16, 15.98) * mm, "end": v(-102.53, 15.98) * mm});
            skLineSegment(sketch, "E88.2.4.3", {"start": v(-102.53, 20.6) * mm, "end": v(-102.53, 15.98) * mm});
            skLineSegment(sketch, "E88.2.5.0", {"start": v(-107.16, 7.9) * mm, "end": v(-102.53, 7.9) * mm});
            skLineSegment(sketch, "E88.2.5.1", {"start": v(-107.16, 7.9) * mm, "end": v(-107.16, 3.28) * mm});
            skLineSegment(sketch, "E88.2.5.2", {"start": v(-107.16, 3.28) * mm, "end": v(-102.53, 3.28) * mm});
            skLineSegment(sketch, "E88.2.5.3", {"start": v(-102.53, 7.9) * mm, "end": v(-102.53, 3.28) * mm});
            skLineSegment(sketch, "E88.2.6.0", {"start": v(-107.16, -4.8) * mm, "end": v(-102.53, -4.8) * mm});
            skLineSegment(sketch, "E88.2.6.1", {"start": v(-107.16, -4.8) * mm, "end": v(-107.16, -9.42) * mm});
            skLineSegment(sketch, "E88.2.6.2", {"start": v(-107.16, -9.42) * mm, "end": v(-102.53, -9.42) * mm});
            skLineSegment(sketch, "E88.2.6.3", {"start": v(-102.53, -4.8) * mm, "end": v(-102.53, -9.42) * mm});
            skLineSegment(sketch, "E88.2.7.0", {"start": v(-107.16, -17.5) * mm, "end": v(-102.53, -17.5) * mm});
            skLineSegment(sketch, "E88.2.7.1", {"start": v(-107.16, -17.5) * mm, "end": v(-107.16, -22.12) * mm});
            skLineSegment(sketch, "E88.2.7.2", {"start": v(-107.16, -22.12) * mm, "end": v(-102.53, -22.12) * mm});
            skLineSegment(sketch, "E88.2.7.3", {"start": v(-102.53, -17.5) * mm, "end": v(-102.53, -22.12) * mm});
            skLineSegment(sketch, "E88.2.8.0", {"start": v(-107.16, -30.2) * mm, "end": v(-102.53, -30.2) * mm});
            skLineSegment(sketch, "E88.2.8.1", {"start": v(-107.16, -30.2) * mm, "end": v(-107.16, -34.82) * mm});
            skLineSegment(sketch, "E88.2.8.2", {"start": v(-107.16, -34.82) * mm, "end": v(-102.53, -34.82) * mm});
            skLineSegment(sketch, "E88.2.8.3", {"start": v(-102.53, -30.2) * mm, "end": v(-102.53, -34.82) * mm});
            skLineSegment(sketch, "E88.2.9.0", {"start": v(-107.16, -42.9) * mm, "end": v(-102.53, -42.9) * mm});
            skLineSegment(sketch, "E88.2.9.1", {"start": v(-107.16, -42.9) * mm, "end": v(-107.16, -47.52) * mm});
            skLineSegment(sketch, "E88.2.9.2", {"start": v(-107.16, -47.52) * mm, "end": v(-102.53, -47.52) * mm});
            skLineSegment(sketch, "E88.2.9.3", {"start": v(-102.53, -42.9) * mm, "end": v(-102.53, -47.52) * mm});
            skLineSegment(sketch, "E88.2.10.0", {"start": v(-107.16, -55.6) * mm, "end": v(-102.53, -55.6) * mm});
            skLineSegment(sketch, "E88.2.10.1", {"start": v(-107.16, -55.6) * mm, "end": v(-107.16, -60.22) * mm});
            skLineSegment(sketch, "E88.2.10.2", {"start": v(-107.16, -60.22) * mm, "end": v(-102.53, -60.22) * mm});
            skLineSegment(sketch, "E88.2.10.3", {"start": v(-102.53, -55.6) * mm, "end": v(-102.53, -60.22) * mm});
            skLineSegment(sketch, "E88.3.0.0", {"start": v(-94.46, 71.4) * mm, "end": v(-89.83, 71.4) * mm});
            skLineSegment(sketch, "E88.3.0.1", {"start": v(-94.46, 71.4) * mm, "end": v(-94.46, 66.78) * mm});
            skLineSegment(sketch, "E88.3.0.2", {"start": v(-94.46, 66.78) * mm, "end": v(-89.83, 66.78) * mm});
            skLineSegment(sketch, "E88.3.0.3", {"start": v(-89.83, 71.4) * mm, "end": v(-89.83, 66.78) * mm});
            skLineSegment(sketch, "E88.3.10.0", {"start": v(-94.46, -55.6) * mm, "end": v(-89.83, -55.6) * mm});
            skLineSegment(sketch, "E88.3.10.1", {"start": v(-94.46, -55.6) * mm, "end": v(-94.46, -60.22) * mm});
            skLineSegment(sketch, "E88.3.10.2", {"start": v(-94.46, -60.22) * mm, "end": v(-89.83, -60.22) * mm});
            skLineSegment(sketch, "E88.3.10.3", {"start": v(-89.83, -55.6) * mm, "end": v(-89.83, -60.22) * mm});
            skLineSegment(sketch, "E88.4.0.0", {"start": v(-81.76, 71.4) * mm, "end": v(-77.13, 71.4) * mm});
            skLineSegment(sketch, "E88.4.0.1", {"start": v(-81.76, 71.4) * mm, "end": v(-81.76, 66.78) * mm});
            skLineSegment(sketch, "E88.4.0.2", {"start": v(-81.76, 66.78) * mm, "end": v(-77.13, 66.78) * mm});
            skLineSegment(sketch, "E88.4.0.3", {"start": v(-77.13, 71.4) * mm, "end": v(-77.13, 66.78) * mm});
            skLineSegment(sketch, "E88.4.10.0", {"start": v(-81.76, -55.6) * mm, "end": v(-77.13, -55.6) * mm});
            skLineSegment(sketch, "E88.4.10.1", {"start": v(-81.76, -55.6) * mm, "end": v(-81.76, -60.22) * mm});
            skLineSegment(sketch, "E88.4.10.2", {"start": v(-81.76, -60.22) * mm, "end": v(-77.13, -60.22) * mm});
            skLineSegment(sketch, "E88.4.10.3", {"start": v(-77.13, -55.6) * mm, "end": v(-77.13, -60.22) * mm});
            skLineSegment(sketch, "E88.5.0.0", {"start": v(-69.06, 71.4) * mm, "end": v(-64.43, 71.4) * mm});
            skLineSegment(sketch, "E88.5.0.1", {"start": v(-69.06, 71.4) * mm, "end": v(-69.06, 66.78) * mm});
            skLineSegment(sketch, "E88.5.0.2", {"start": v(-69.06, 66.78) * mm, "end": v(-64.43, 66.78) * mm});
            skLineSegment(sketch, "E88.5.0.3", {"start": v(-64.43, 71.4) * mm, "end": v(-64.43, 66.78) * mm});
            skLineSegment(sketch, "E88.5.10.0", {"start": v(-69.06, -55.6) * mm, "end": v(-64.43, -55.6) * mm});
            skLineSegment(sketch, "E88.5.10.1", {"start": v(-69.06, -55.6) * mm, "end": v(-69.06, -60.22) * mm});
            skLineSegment(sketch, "E88.5.10.2", {"start": v(-69.06, -60.22) * mm, "end": v(-64.43, -60.22) * mm});
            skLineSegment(sketch, "E88.5.10.3", {"start": v(-64.43, -55.6) * mm, "end": v(-64.43, -60.22) * mm});
            skLineSegment(sketch, "E88.6.0.0", {"start": v(-56.36, 71.4) * mm, "end": v(-51.73, 71.4) * mm});
            skLineSegment(sketch, "E88.6.0.1", {"start": v(-56.36, 71.4) * mm, "end": v(-56.36, 66.78) * mm});
            skLineSegment(sketch, "E88.6.0.2", {"start": v(-56.36, 66.78) * mm, "end": v(-51.73, 66.78) * mm});
            skLineSegment(sketch, "E88.6.0.3", {"start": v(-51.73, 71.4) * mm, "end": v(-51.73, 66.78) * mm});
            skLineSegment(sketch, "E88.6.10.0", {"start": v(-56.36, -55.6) * mm, "end": v(-51.73, -55.6) * mm});
            skLineSegment(sketch, "E88.6.10.1", {"start": v(-56.36, -55.6) * mm, "end": v(-56.36, -60.22) * mm});
            skLineSegment(sketch, "E88.6.10.2", {"start": v(-56.36, -60.22) * mm, "end": v(-51.73, -60.22) * mm});
            skLineSegment(sketch, "E88.6.10.3", {"start": v(-51.73, -55.6) * mm, "end": v(-51.73, -60.22) * mm});
            skLineSegment(sketch, "E88.7.0.0", {"start": v(-43.66, 71.4) * mm, "end": v(-39.03, 71.4) * mm});
            skLineSegment(sketch, "E88.7.0.1", {"start": v(-43.66, 71.4) * mm, "end": v(-43.66, 66.78) * mm});
            skLineSegment(sketch, "E88.7.0.2", {"start": v(-43.66, 66.78) * mm, "end": v(-39.03, 66.78) * mm});
            skLineSegment(sketch, "E88.7.0.3", {"start": v(-39.03, 71.4) * mm, "end": v(-39.03, 66.78) * mm});
            skLineSegment(sketch, "E88.7.10.0", {"start": v(-43.66, -55.6) * mm, "end": v(-39.03, -55.6) * mm});
            skLineSegment(sketch, "E88.7.10.1", {"start": v(-43.66, -55.6) * mm, "end": v(-43.66, -60.22) * mm});
            skLineSegment(sketch, "E88.7.10.2", {"start": v(-43.66, -60.22) * mm, "end": v(-39.03, -60.22) * mm});
            skLineSegment(sketch, "E88.7.10.3", {"start": v(-39.03, -55.6) * mm, "end": v(-39.03, -60.22) * mm});
            skLineSegment(sketch, "E88.8.0.0", {"start": v(-30.96, 71.4) * mm, "end": v(-26.33, 71.4) * mm});
            skLineSegment(sketch, "E88.8.0.1", {"start": v(-30.96, 71.4) * mm, "end": v(-30.96, 66.78) * mm});
            skLineSegment(sketch, "E88.8.0.2", {"start": v(-30.96, 66.78) * mm, "end": v(-26.33, 66.78) * mm});
            skLineSegment(sketch, "E88.8.0.3", {"start": v(-26.33, 71.4) * mm, "end": v(-26.33, 66.78) * mm});
            skLineSegment(sketch, "E88.8.10.0", {"start": v(-30.96, -55.6) * mm, "end": v(-26.33, -55.6) * mm});
            skLineSegment(sketch, "E88.8.10.1", {"start": v(-30.96, -55.6) * mm, "end": v(-30.96, -60.22) * mm});
            skLineSegment(sketch, "E88.8.10.2", {"start": v(-30.96, -60.22) * mm, "end": v(-26.33, -60.22) * mm});
            skLineSegment(sketch, "E88.8.10.3", {"start": v(-26.33, -55.6) * mm, "end": v(-26.33, -60.22) * mm});
            skLineSegment(sketch, "E88.9.0.0", {"start": v(-18.26, 71.4) * mm, "end": v(-13.63, 71.4) * mm});
            skLineSegment(sketch, "E88.9.0.1", {"start": v(-18.26, 71.4) * mm, "end": v(-18.26, 66.78) * mm});
            skLineSegment(sketch, "E88.9.0.2", {"start": v(-18.26, 66.78) * mm, "end": v(-13.63, 66.78) * mm});
            skLineSegment(sketch, "E88.9.0.3", {"start": v(-13.63, 71.4) * mm, "end": v(-13.63, 66.78) * mm});
            skLineSegment(sketch, "E88.9.10.0", {"start": v(-18.26, -55.6) * mm, "end": v(-13.63, -55.6) * mm});
            skLineSegment(sketch, "E88.9.10.1", {"start": v(-18.26, -55.6) * mm, "end": v(-18.26, -60.22) * mm});
            skLineSegment(sketch, "E88.9.10.2", {"start": v(-18.26, -60.22) * mm, "end": v(-13.63, -60.22) * mm});
            skLineSegment(sketch, "E88.9.10.3", {"start": v(-13.63, -55.6) * mm, "end": v(-13.63, -60.22) * mm});
            skLineSegment(sketch, "E88.10.0.0", {"start": v(-5.56, 71.4) * mm, "end": v(-0.93, 71.4) * mm});
            skLineSegment(sketch, "E88.10.0.1", {"start": v(-5.56, 71.4) * mm, "end": v(-5.56, 66.78) * mm});
            skLineSegment(sketch, "E88.10.0.2", {"start": v(-5.56, 66.78) * mm, "end": v(-0.93, 66.78) * mm});
            skLineSegment(sketch, "E88.10.0.3", {"start": v(-0.93, 71.4) * mm, "end": v(-0.93, 66.78) * mm});
            skLineSegment(sketch, "E88.10.10.0", {"start": v(-5.56, -55.6) * mm, "end": v(-0.93, -55.6) * mm});
            skLineSegment(sketch, "E88.10.10.1", {"start": v(-5.56, -55.6) * mm, "end": v(-5.56, -60.22) * mm});
            skLineSegment(sketch, "E88.10.10.2", {"start": v(-5.56, -60.22) * mm, "end": v(-0.93, -60.22) * mm});
            skLineSegment(sketch, "E88.10.10.3", {"start": v(-0.93, -55.6) * mm, "end": v(-0.93, -60.22) * mm});
            skLineSegment(sketch, "E88.11.0.0", {"start": v(7.14, 71.4) * mm, "end": v(11.77, 71.4) * mm});
            skLineSegment(sketch, "E88.11.0.1", {"start": v(7.14, 71.4) * mm, "end": v(7.14, 66.78) * mm});
            skLineSegment(sketch, "E88.11.0.2", {"start": v(7.14, 66.78) * mm, "end": v(11.77, 66.78) * mm});
            skLineSegment(sketch, "E88.11.0.3", {"start": v(11.77, 71.4) * mm, "end": v(11.77, 66.78) * mm});
            skLineSegment(sketch, "E88.11.10.0", {"start": v(7.14, -55.6) * mm, "end": v(11.77, -55.6) * mm});
            skLineSegment(sketch, "E88.11.10.1", {"start": v(7.14, -55.6) * mm, "end": v(7.14, -60.22) * mm});
            skLineSegment(sketch, "E88.11.10.2", {"start": v(7.14, -60.22) * mm, "end": v(11.77, -60.22) * mm});
            skLineSegment(sketch, "E88.11.10.3", {"start": v(11.77, -55.6) * mm, "end": v(11.77, -60.22) * mm});
            skLineSegment(sketch, "E88.12.0.0", {"start": v(19.84, 71.4) * mm, "end": v(24.47, 71.4) * mm});
            skLineSegment(sketch, "E88.12.0.1", {"start": v(19.84, 71.4) * mm, "end": v(19.84, 66.78) * mm});
            skLineSegment(sketch, "E88.12.0.2", {"start": v(19.84, 66.78) * mm, "end": v(24.47, 66.78) * mm});
            skLineSegment(sketch, "E88.12.0.3", {"start": v(24.47, 71.4) * mm, "end": v(24.47, 66.78) * mm});
            skLineSegment(sketch, "E88.12.1.0", {"start": v(19.84, 58.7) * mm, "end": v(24.47, 58.7) * mm});
            skLineSegment(sketch, "E88.12.1.1", {"start": v(19.84, 58.7) * mm, "end": v(19.84, 54.08) * mm});
            skLineSegment(sketch, "E88.12.1.2", {"start": v(19.84, 54.08) * mm, "end": v(24.47, 54.08) * mm});
            skLineSegment(sketch, "E88.12.1.3", {"start": v(24.47, 58.7) * mm, "end": v(24.47, 54.08) * mm});
            skLineSegment(sketch, "E88.12.2.0", {"start": v(19.84, 46) * mm, "end": v(24.47, 46) * mm});
            skLineSegment(sketch, "E88.12.2.1", {"start": v(19.84, 46) * mm, "end": v(19.84, 41.38) * mm});
            skLineSegment(sketch, "E88.12.2.2", {"start": v(19.84, 41.38) * mm, "end": v(24.47, 41.38) * mm});
            skLineSegment(sketch, "E88.12.2.3", {"start": v(24.47, 46) * mm, "end": v(24.47, 41.38) * mm});
            skLineSegment(sketch, "E88.12.3.0", {"start": v(19.84, 33.3) * mm, "end": v(24.47, 33.3) * mm});
            skLineSegment(sketch, "E88.12.3.1", {"start": v(19.84, 33.3) * mm, "end": v(19.84, 28.68) * mm});
            skLineSegment(sketch, "E88.12.3.2", {"start": v(19.84, 28.68) * mm, "end": v(24.47, 28.68) * mm});
            skLineSegment(sketch, "E88.12.3.3", {"start": v(24.47, 33.3) * mm, "end": v(24.47, 28.68) * mm});
            skLineSegment(sketch, "E88.12.4.0", {"start": v(19.84, 20.6) * mm, "end": v(24.47, 20.6) * mm});
            skLineSegment(sketch, "E88.12.4.1", {"start": v(19.84, 20.6) * mm, "end": v(19.84, 15.98) * mm});
            skLineSegment(sketch, "E88.12.4.2", {"start": v(19.84, 15.98) * mm, "end": v(24.47, 15.98) * mm});
            skLineSegment(sketch, "E88.12.4.3", {"start": v(24.47, 20.6) * mm, "end": v(24.47, 15.98) * mm});
            skLineSegment(sketch, "E88.12.5.0", {"start": v(19.84, 7.9) * mm, "end": v(24.47, 7.9) * mm});
            skLineSegment(sketch, "E88.12.5.1", {"start": v(19.84, 7.9) * mm, "end": v(19.84, 3.28) * mm});
            skLineSegment(sketch, "E88.12.5.2", {"start": v(19.84, 3.28) * mm, "end": v(24.47, 3.28) * mm});
            skLineSegment(sketch, "E88.12.5.3", {"start": v(24.47, 7.9) * mm, "end": v(24.47, 3.28) * mm});
            skLineSegment(sketch, "E88.12.6.0", {"start": v(19.84, -4.8) * mm, "end": v(24.47, -4.8) * mm});
            skLineSegment(sketch, "E88.12.6.1", {"start": v(19.84, -4.8) * mm, "end": v(19.84, -9.42) * mm});
            skLineSegment(sketch, "E88.12.6.2", {"start": v(19.84, -9.42) * mm, "end": v(24.47, -9.42) * mm});
            skLineSegment(sketch, "E88.12.6.3", {"start": v(24.47, -4.8) * mm, "end": v(24.47, -9.42) * mm});
            skLineSegment(sketch, "E88.12.7.0", {"start": v(19.84, -17.5) * mm, "end": v(24.47, -17.5) * mm});
            skLineSegment(sketch, "E88.12.7.1", {"start": v(19.84, -17.5) * mm, "end": v(19.84, -22.12) * mm});
            skLineSegment(sketch, "E88.12.7.2", {"start": v(19.84, -22.12) * mm, "end": v(24.47, -22.12) * mm});
            skLineSegment(sketch, "E88.12.7.3", {"start": v(24.47, -17.5) * mm, "end": v(24.47, -22.12) * mm});
            skLineSegment(sketch, "E88.12.8.0", {"start": v(19.84, -30.2) * mm, "end": v(24.47, -30.2) * mm});
            skLineSegment(sketch, "E88.12.8.1", {"start": v(19.84, -30.2) * mm, "end": v(19.84, -34.82) * mm});
            skLineSegment(sketch, "E88.12.8.2", {"start": v(19.84, -34.82) * mm, "end": v(24.47, -34.82) * mm});
            skLineSegment(sketch, "E88.12.8.3", {"start": v(24.47, -30.2) * mm, "end": v(24.47, -34.82) * mm});
            skLineSegment(sketch, "E88.12.9.0", {"start": v(19.84, -42.9) * mm, "end": v(24.47, -42.9) * mm});
            skLineSegment(sketch, "E88.12.9.1", {"start": v(19.84, -42.9) * mm, "end": v(19.84, -47.52) * mm});
            skLineSegment(sketch, "E88.12.9.2", {"start": v(19.84, -47.52) * mm, "end": v(24.47, -47.52) * mm});
            skLineSegment(sketch, "E88.12.9.3", {"start": v(24.47, -42.9) * mm, "end": v(24.47, -47.52) * mm});
            skLineSegment(sketch, "E88.12.10.0", {"start": v(19.84, -55.6) * mm, "end": v(24.47, -55.6) * mm});
            skLineSegment(sketch, "E88.12.10.1", {"start": v(19.84, -55.6) * mm, "end": v(19.84, -60.22) * mm});
            skLineSegment(sketch, "E88.12.10.2", {"start": v(19.84, -60.22) * mm, "end": v(24.47, -60.22) * mm});
            skLineSegment(sketch, "E88.12.10.3", {"start": v(24.47, -55.6) * mm, "end": v(24.47, -60.22) * mm});
            skLineSegment(sketch, "E88.13.1.0", {"start": v(32.54, 58.7) * mm, "end": v(37.17, 58.7) * mm});
            skLineSegment(sketch, "E88.13.1.1", {"start": v(32.54, 58.7) * mm, "end": v(32.54, 54.08) * mm});
            skLineSegment(sketch, "E88.13.1.2", {"start": v(32.54, 54.08) * mm, "end": v(37.17, 54.08) * mm});
            skLineSegment(sketch, "E88.13.1.3", {"start": v(37.17, 58.7) * mm, "end": v(37.17, 54.08) * mm});
            skLineSegment(sketch, "E88.13.2.0", {"start": v(32.54, 46) * mm, "end": v(37.17, 46) * mm});
            skLineSegment(sketch, "E88.13.2.1", {"start": v(32.54, 46) * mm, "end": v(32.54, 41.38) * mm});
            skLineSegment(sketch, "E88.13.2.2", {"start": v(32.54, 41.38) * mm, "end": v(37.17, 41.38) * mm});
            skLineSegment(sketch, "E88.13.2.3", {"start": v(37.17, 46) * mm, "end": v(37.17, 41.38) * mm});
            skLineSegment(sketch, "E88.13.3.0", {"start": v(32.54, 33.3) * mm, "end": v(37.17, 33.3) * mm});
            skLineSegment(sketch, "E88.13.3.1", {"start": v(32.54, 33.3) * mm, "end": v(32.54, 28.68) * mm});
            skLineSegment(sketch, "E88.13.3.2", {"start": v(32.54, 28.68) * mm, "end": v(37.17, 28.68) * mm});
            skLineSegment(sketch, "E88.13.3.3", {"start": v(37.17, 33.3) * mm, "end": v(37.17, 28.68) * mm});
            skLineSegment(sketch, "E88.13.4.0", {"start": v(32.54, 20.6) * mm, "end": v(37.17, 20.6) * mm});
            skLineSegment(sketch, "E88.13.4.1", {"start": v(32.54, 20.6) * mm, "end": v(32.54, 15.98) * mm});
            skLineSegment(sketch, "E88.13.4.2", {"start": v(32.54, 15.98) * mm, "end": v(37.17, 15.98) * mm});
            skLineSegment(sketch, "E88.13.4.3", {"start": v(37.17, 20.6) * mm, "end": v(37.17, 15.98) * mm});
            skLineSegment(sketch, "E88.13.5.0", {"start": v(32.54, 7.9) * mm, "end": v(37.17, 7.9) * mm});
            skLineSegment(sketch, "E88.13.5.1", {"start": v(32.54, 7.9) * mm, "end": v(32.54, 3.28) * mm});
            skLineSegment(sketch, "E88.13.5.2", {"start": v(32.54, 3.28) * mm, "end": v(37.17, 3.28) * mm});
            skLineSegment(sketch, "E88.13.5.3", {"start": v(37.17, 7.9) * mm, "end": v(37.17, 3.28) * mm});
            skLineSegment(sketch, "E88.13.6.0", {"start": v(32.54, -4.8) * mm, "end": v(37.17, -4.8) * mm});
            skLineSegment(sketch, "E88.13.6.1", {"start": v(32.54, -4.8) * mm, "end": v(32.54, -9.42) * mm});
            skLineSegment(sketch, "E88.13.6.2", {"start": v(32.54, -9.42) * mm, "end": v(37.17, -9.42) * mm});
            skLineSegment(sketch, "E88.13.6.3", {"start": v(37.17, -4.8) * mm, "end": v(37.17, -9.42) * mm});
            skLineSegment(sketch, "E88.13.7.0", {"start": v(32.54, -17.5) * mm, "end": v(37.17, -17.5) * mm});
            skLineSegment(sketch, "E88.13.7.1", {"start": v(32.54, -17.5) * mm, "end": v(32.54, -22.12) * mm});
            skLineSegment(sketch, "E88.13.7.2", {"start": v(32.54, -22.12) * mm, "end": v(37.17, -22.12) * mm});
            skLineSegment(sketch, "E88.13.7.3", {"start": v(37.17, -17.5) * mm, "end": v(37.17, -22.12) * mm});
            skLineSegment(sketch, "E88.13.8.0", {"start": v(32.54, -30.2) * mm, "end": v(37.17, -30.2) * mm});
            skLineSegment(sketch, "E88.13.8.1", {"start": v(32.54, -30.2) * mm, "end": v(32.54, -34.82) * mm});
            skLineSegment(sketch, "E88.13.8.2", {"start": v(32.54, -34.82) * mm, "end": v(37.17, -34.82) * mm});
            skLineSegment(sketch, "E88.13.8.3", {"start": v(37.17, -30.2) * mm, "end": v(37.17, -34.82) * mm});
            skLineSegment(sketch, "E88.13.9.0", {"start": v(32.54, -42.9) * mm, "end": v(37.17, -42.9) * mm});
            skLineSegment(sketch, "E88.13.9.1", {"start": v(32.54, -42.9) * mm, "end": v(32.54, -47.52) * mm});
            skLineSegment(sketch, "E88.13.9.2", {"start": v(32.54, -47.52) * mm, "end": v(37.17, -47.52) * mm});
            skLineSegment(sketch, "E88.13.9.3", {"start": v(37.17, -42.9) * mm, "end": v(37.17, -47.52) * mm});
            skLineSegment(sketch, "E88.14.0.0", {"start": v(45.24, 71.4) * mm, "end": v(49.87, 71.4) * mm});
            skLineSegment(sketch, "E88.14.0.1", {"start": v(45.24, 71.4) * mm, "end": v(45.24, 66.78) * mm});
            skLineSegment(sketch, "E88.14.0.2", {"start": v(45.24, 66.78) * mm, "end": v(49.87, 66.78) * mm});
            skLineSegment(sketch, "E88.14.0.3", {"start": v(49.87, 71.4) * mm, "end": v(49.87, 66.78) * mm});
            skLineSegment(sketch, "E88.14.2.0", {"start": v(45.24, 46) * mm, "end": v(49.87, 46) * mm});
            skLineSegment(sketch, "E88.14.2.1", {"start": v(45.24, 46) * mm, "end": v(45.24, 41.38) * mm});
            skLineSegment(sketch, "E88.14.2.2", {"start": v(45.24, 41.38) * mm, "end": v(49.87, 41.38) * mm});
            skLineSegment(sketch, "E88.14.2.3", {"start": v(49.87, 46) * mm, "end": v(49.87, 41.38) * mm});
            skLineSegment(sketch, "E88.14.3.0", {"start": v(45.24, 33.3) * mm, "end": v(49.87, 33.3) * mm});
            skLineSegment(sketch, "E88.14.3.1", {"start": v(45.24, 33.3) * mm, "end": v(45.24, 28.68) * mm});
            skLineSegment(sketch, "E88.14.3.2", {"start": v(45.24, 28.68) * mm, "end": v(49.87, 28.68) * mm});
            skLineSegment(sketch, "E88.14.3.3", {"start": v(49.87, 33.3) * mm, "end": v(49.87, 28.68) * mm});
            skLineSegment(sketch, "E88.14.4.0", {"start": v(45.24, 20.6) * mm, "end": v(49.87, 20.6) * mm});
            skLineSegment(sketch, "E88.14.4.1", {"start": v(45.24, 20.6) * mm, "end": v(45.24, 15.98) * mm});
            skLineSegment(sketch, "E88.14.4.2", {"start": v(45.24, 15.98) * mm, "end": v(49.87, 15.98) * mm});
            skLineSegment(sketch, "E88.14.4.3", {"start": v(49.87, 20.6) * mm, "end": v(49.87, 15.98) * mm});
            skLineSegment(sketch, "E88.14.5.0", {"start": v(45.24, 7.9) * mm, "end": v(49.87, 7.9) * mm});
            skLineSegment(sketch, "E88.14.5.1", {"start": v(45.24, 7.9) * mm, "end": v(45.24, 3.28) * mm});
            skLineSegment(sketch, "E88.14.5.2", {"start": v(45.24, 3.28) * mm, "end": v(49.87, 3.28) * mm});
            skLineSegment(sketch, "E88.14.5.3", {"start": v(49.87, 7.9) * mm, "end": v(49.87, 3.28) * mm});
            skLineSegment(sketch, "E88.14.6.0", {"start": v(45.24, -4.8) * mm, "end": v(49.87, -4.8) * mm});
            skLineSegment(sketch, "E88.14.6.1", {"start": v(45.24, -4.8) * mm, "end": v(45.24, -9.42) * mm});
            skLineSegment(sketch, "E88.14.6.2", {"start": v(45.24, -9.42) * mm, "end": v(49.87, -9.42) * mm});
            skLineSegment(sketch, "E88.14.6.3", {"start": v(49.87, -4.8) * mm, "end": v(49.87, -9.42) * mm});
            skLineSegment(sketch, "E88.14.7.0", {"start": v(45.24, -17.5) * mm, "end": v(49.87, -17.5) * mm});
            skLineSegment(sketch, "E88.14.7.1", {"start": v(45.24, -17.5) * mm, "end": v(45.24, -22.12) * mm});
            skLineSegment(sketch, "E88.14.7.2", {"start": v(45.24, -22.12) * mm, "end": v(49.87, -22.12) * mm});
            skLineSegment(sketch, "E88.14.7.3", {"start": v(49.87, -17.5) * mm, "end": v(49.87, -22.12) * mm});
            skLineSegment(sketch, "E88.14.8.0", {"start": v(45.24, -30.2) * mm, "end": v(49.87, -30.2) * mm});
            skLineSegment(sketch, "E88.14.8.1", {"start": v(45.24, -30.2) * mm, "end": v(45.24, -34.82) * mm});
            skLineSegment(sketch, "E88.14.8.2", {"start": v(45.24, -34.82) * mm, "end": v(49.87, -34.82) * mm});
            skLineSegment(sketch, "E88.14.8.3", {"start": v(49.87, -30.2) * mm, "end": v(49.87, -34.82) * mm});
            skLineSegment(sketch, "E88.14.10.0", {"start": v(45.24, -55.6) * mm, "end": v(49.87, -55.6) * mm});
            skLineSegment(sketch, "E88.14.10.1", {"start": v(45.24, -55.6) * mm, "end": v(45.24, -60.22) * mm});
            skLineSegment(sketch, "E88.14.10.2", {"start": v(45.24, -60.22) * mm, "end": v(49.87, -60.22) * mm});
            skLineSegment(sketch, "E88.14.10.3", {"start": v(49.87, -55.6) * mm, "end": v(49.87, -60.22) * mm});
            skLineSegment(sketch, "E88.direction1", {"start": v(-132.56, 66.78) * mm, "end": v(-119.86, 66.78) * mm, "construction": true});
            skLineSegment(sketch, "E88.direction2", {"start": v(-132.56, 66.78) * mm, "end": v(-132.56, 54.08) * mm, "construction": true});
            skSolve(sketch);
        }
        {
            var Q0;
            Q0 = qSketchRegion(id + "F9", true);
            extrude(context, id + "F10", {"entities" : qUnion([Q0]), "operationType" : NewBodyOperationType.REMOVE, "oppositeDirection" : true, "depth" : 25.4 * mm});
        }
        {
            var Q0;
            Q0=makeQuery(id+"F8.opExtrude","CAP_FACE",FACE,{"disambiguationData":[OSD([sQuery(id+"F7.wireOp",EDGE,"E56.bottom"),sQuery(id+"F7.wireOp",EDGE,"E56.top"),sQuery(id+"F7.wireOp",EDGE,"E56.left"),sQuery(id+"F7.wireOp",EDGE,"E56.right"),sQuery(id+"F7.wireOp",EDGE,"E57.0.0"),sQuery(id+"F7.wireOp",EDGE,"E57.0.1"),sQuery(id+"F7.wireOp",EDGE,"E57.0.2"),sQuery(id+"F7.wireOp",EDGE,"E57.0.3"),sQuery(id+"F7.wireOp",EDGE,"E58.0.0"),sQuery(id+"F7.wireOp",EDGE,"E58.0.1"),sQuery(id+"F7.wireOp",EDGE,"E58.0.2"),sQuery(id+"F7.wireOp",EDGE,"E58.0.3"),sQuery(id+"F7.wireOp",EDGE,"E59.0.0"),sQuery(id+"F7.wireOp",EDGE,"E59.0.1"),sQuery(id+"F7.wireOp",EDGE,"E59.0.2"),sQuery(id+"F7.wireOp",EDGE,"E59.0.3"),sQuery(id+"F7.wireOp",EDGE,"E60.0.0"),sQuery(id+"F7.wireOp",EDGE,"E60.0.1"),sQuery(id+"F7.wireOp",EDGE,"E60.0.2"),sQuery(id+"F7.wireOp",EDGE,"E60.0.3"),sQuery(id+"F7.wireOp",EDGE,"E63.filletArc"),sQuery(id+"F7.wireOp",EDGE,"E64.filletArc"),sQuery(id+"F7.wireOp",EDGE,"E65.filletArc"),sQuery(id+"F7.wireOp",EDGE,"E66.filletArc"),sQuery(id+"F7.wireOp",EDGE,"E67.bottom"),sQuery(id+"F7.wireOp",EDGE,"E67.top"),sQuery(id+"F7.wireOp",EDGE,"E67.left"),sQuery(id+"F7.wireOp",EDGE,"E67.right"),sQuery(id+"F7.wireOp",EDGE,"E68.bottom"),sQuery(id+"F7.wireOp",EDGE,"E68.top"),sQuery(id+"F7.wireOp",EDGE,"E68.left"),sQuery(id+"F7.wireOp",EDGE,"E68.right"),sQuery(id+"F7.wireOp",EDGE,"E69.bottom"),sQuery(id+"F7.wireOp",EDGE,"E69.top"),sQuery(id+"F7.wireOp",EDGE,"E69.left"),sQuery(id+"F7.wireOp",EDGE,"E69.right"),sQuery(id+"F7.wireOp",EDGE,"E70.bottom"),sQuery(id+"F7.wireOp",EDGE,"E70.top"),sQuery(id+"F7.wireOp",EDGE,"E70.left"),sQuery(id+"F7.wireOp",EDGE,"E70.right"),sQuery(id+"F7.wireOp",EDGE,"E71.bottom"),sQuery(id+"F7.wireOp",EDGE,"E71.top"),sQuery(id+"F7.wireOp",EDGE,"E71.left"),sQuery(id+"F7.wireOp",EDGE,"E71.right"),sQuery(id+"F7.wireOp",EDGE,"E72.bottom"),sQuery(id+"F7.wireOp",EDGE,"E72.top"),sQuery(id+"F7.wireOp",EDGE,"E72.left"),sQuery(id+"F7.wireOp",EDGE,"E72.right"),sQuery(id+"F7.wireOp",EDGE,"E73.bottom"),sQuery(id+"F7.wireOp",EDGE,"E73.top"),sQuery(id+"F7.wireOp",EDGE,"E73.left"),sQuery(id+"F7.wireOp",EDGE,"E73.right"),sQuery(id+"F7.wireOp",EDGE,"E74.bottom"),sQuery(id+"F7.wireOp",EDGE,"E74.top"),sQuery(id+"F7.wireOp",EDGE,"E74.left"),sQuery(id+"F7.wireOp",EDGE,"E74.right")])],"isStart":true});
            var sketch = newSketch(context, id + "F11", { "sketchPlane" : qUnion([Q0])});
            skLineSegment(sketch, "E89.0", {"start": v(-122.62, 69.1) * mm, "end": v(-112.46, 69.1) * mm});
            skLineSegment(sketch, "E90.0", {"start": v(-122.62, 66.1) * mm, "end": v(-112.46, 66.1) * mm});
            skLineSegment(sketch, "E91.0", {"start": v(-112.46, 66.1) * mm, "end": v(-112.46, 69.1) * mm});
            skLineSegment(sketch, "E92.0", {"start": v(-122.62, 66.1) * mm, "end": v(-122.62, 69.1) * mm});
            skLineSegment(sketch, "E93.0", {"start": v(-127.24, 61.47) * mm, "end": v(-127.24, 51.31) * mm});
            skLineSegment(sketch, "E94.0", {"start": v(-130.24, 61.47) * mm, "end": v(-130.24, 51.31) * mm});
            skLineSegment(sketch, "E95.0", {"start": v(-130.24, 61.47) * mm, "end": v(-127.24, 61.47) * mm});
            skLineSegment(sketch, "E96.0", {"start": v(-130.24, 51.31) * mm, "end": v(-127.24, 51.31) * mm});
            skLineSegment(sketch, "E97.0", {"start": v(-130.24, -40.13) * mm, "end": v(-130.24, -50.29) * mm});
            skLineSegment(sketch, "E98.0", {"start": v(-127.24, -40.13) * mm, "end": v(-127.24, -50.29) * mm});
            skLineSegment(sketch, "E99.0", {"start": v(-130.24, -40.13) * mm, "end": v(-127.24, -40.13) * mm});
            skLineSegment(sketch, "E100.0", {"start": v(-130.24, -50.29) * mm, "end": v(-127.24, -50.29) * mm});
            skLineSegment(sketch, "E101.0", {"start": v(-122.62, -54.9) * mm, "end": v(-112.46, -54.9) * mm});
            skLineSegment(sketch, "E102.0", {"start": v(-122.62, -57.9) * mm, "end": v(-122.62, -54.9) * mm});
            skLineSegment(sketch, "E103.0", {"start": v(-122.62, -57.9) * mm, "end": v(-112.46, -57.9) * mm});
            skLineSegment(sketch, "E104.0", {"start": v(-112.46, -57.9) * mm, "end": v(-112.46, -54.9) * mm});
            skLineSegment(sketch, "E105.0", {"start": v(29.78, -54.9) * mm, "end": v(39.94, -54.9) * mm});
            skLineSegment(sketch, "E106.0", {"start": v(29.78, -57.9) * mm, "end": v(39.94, -57.9) * mm});
            skLineSegment(sketch, "E107.0", {"start": v(39.94, -57.9) * mm, "end": v(39.94, -54.9) * mm});
            skLineSegment(sketch, "E108.0", {"start": v(29.78, -57.9) * mm, "end": v(29.78, -54.9) * mm});
            skLineSegment(sketch, "E109.0", {"start": v(44.56, -50.29) * mm, "end": v(44.56, -40.13) * mm});
            skLineSegment(sketch, "E110.0", {"start": v(44.56, -40.13) * mm, "end": v(47.56, -40.13) * mm});
            skLineSegment(sketch, "E111.0", {"start": v(47.56, -50.29) * mm, "end": v(47.56, -40.13) * mm});
            skLineSegment(sketch, "E112.0", {"start": v(44.56, -50.29) * mm, "end": v(47.56, -50.29) * mm});
            skLineSegment(sketch, "E113.0", {"start": v(29.78, 66.1) * mm, "end": v(39.94, 66.1) * mm});
            skLineSegment(sketch, "E114.0", {"start": v(29.78, 69.1) * mm, "end": v(39.94, 69.1) * mm});
            skLineSegment(sketch, "E115.0", {"start": v(39.94, 69.1) * mm, "end": v(39.94, 66.1) * mm});
            skLineSegment(sketch, "E116.0", {"start": v(29.78, 69.1) * mm, "end": v(29.78, 66.1) * mm});
            skLineSegment(sketch, "E117.0", {"start": v(44.56, 61.47) * mm, "end": v(47.56, 61.47) * mm});
            skLineSegment(sketch, "E118.0", {"start": v(44.56, 61.47) * mm, "end": v(44.56, 51.31) * mm});
            skLineSegment(sketch, "E119.0", {"start": v(47.56, 61.47) * mm, "end": v(47.56, 51.31) * mm});
            skLineSegment(sketch, "E120.0", {"start": v(44.56, 51.31) * mm, "end": v(47.56, 51.31) * mm});
            skSolve(sketch);
        }
        {
            var Q0;
            Q0 = qSketchRegion(id + "F11", true);
            extrude(context, id + "F12", {"entities" : qUnion([Q0]), "oppositeDirection" : true, "depth" : 3 * mm});
        }
        {
            var Q0;
            Q0=makeQuery(id+"F12.opExtrude","CAP_FACE",FACE,{"disambiguationData":[OSD([sQuery(id+"F11.wireOp",EDGE,"E89.0"),sQuery(id+"F11.wireOp",EDGE,"E90.0"),sQuery(id+"F11.wireOp",EDGE,"E91.0"),sQuery(id+"F11.wireOp",EDGE,"E92.0")])],"isStart":true});
            var sketch = newSketch(context, id + "F13", { "sketchPlane" : qUnion([Q0])});
            skLineSegment(sketch, "E121.bottom", {"start": v(-127.07, 69.1) * mm, "end": v(-108.02, 69.1) * mm});
            skLineSegment(sketch, "E121.top", {"start": v(-127.07, 66.1) * mm, "end": v(-108.02, 66.1) * mm});
            skLineSegment(sketch, "E121.left", {"start": v(-127.07, 69.1) * mm, "end": v(-127.07, 66.1) * mm});
            skLineSegment(sketch, "E121.right", {"start": v(-108.02, 69.1) * mm, "end": v(-108.02, 66.1) * mm});
            skLineSegment(sketch, "E122.bottom", {"start": v(-130.24, 65.92) * mm, "end": v(-127.24, 65.92) * mm});
            skLineSegment(sketch, "E122.top", {"start": v(-130.24, 46.87) * mm, "end": v(-127.24, 46.87) * mm});
            skLineSegment(sketch, "E122.left", {"start": v(-130.24, 65.92) * mm, "end": v(-130.24, 46.87) * mm});
            skLineSegment(sketch, "E122.right", {"start": v(-127.24, 65.92) * mm, "end": v(-127.24, 46.87) * mm});
            skLineSegment(sketch, "E123.bottom", {"start": v(44.56, 65.92) * mm, "end": v(47.56, 65.92) * mm});
            skLineSegment(sketch, "E123.top", {"start": v(44.56, 46.87) * mm, "end": v(47.56, 46.87) * mm});
            skLineSegment(sketch, "E123.left", {"start": v(44.56, 65.92) * mm, "end": v(44.56, 46.87) * mm});
            skLineSegment(sketch, "E123.right", {"start": v(47.56, 65.92) * mm, "end": v(47.56, 46.87) * mm});
            skLineSegment(sketch, "E124.bottom", {"start": v(44.56, -35.68) * mm, "end": v(47.56, -35.68) * mm});
            skLineSegment(sketch, "E124.top", {"start": v(44.56, -54.73) * mm, "end": v(47.56, -54.73) * mm});
            skLineSegment(sketch, "E124.left", {"start": v(44.56, -35.68) * mm, "end": v(44.56, -54.73) * mm});
            skLineSegment(sketch, "E124.right", {"start": v(47.56, -35.68) * mm, "end": v(47.56, -54.73) * mm});
            skLineSegment(sketch, "E125.bottom", {"start": v(25.33, -54.9) * mm, "end": v(44.38, -54.9) * mm});
            skLineSegment(sketch, "E125.top", {"start": v(25.33, -57.9) * mm, "end": v(44.38, -57.9) * mm});
            skLineSegment(sketch, "E125.left", {"start": v(25.33, -54.9) * mm, "end": v(25.33, -57.9) * mm});
            skLineSegment(sketch, "E125.right", {"start": v(44.38, -54.9) * mm, "end": v(44.38, -57.9) * mm});
            skLineSegment(sketch, "E126.bottom", {"start": v(-130.24, -35.68) * mm, "end": v(-127.24, -35.68) * mm});
            skLineSegment(sketch, "E126.top", {"start": v(-130.24, -54.73) * mm, "end": v(-127.24, -54.73) * mm});
            skLineSegment(sketch, "E126.left", {"start": v(-130.24, -35.68) * mm, "end": v(-130.24, -54.73) * mm});
            skLineSegment(sketch, "E126.right", {"start": v(-127.24, -35.68) * mm, "end": v(-127.24, -54.73) * mm});
            skLineSegment(sketch, "E127.bottom", {"start": v(-108.02, -57.9) * mm, "end": v(-127.07, -57.9) * mm});
            skLineSegment(sketch, "E127.top", {"start": v(-108.02, -54.9) * mm, "end": v(-127.07, -54.9) * mm});
            skLineSegment(sketch, "E127.left", {"start": v(-108.02, -57.9) * mm, "end": v(-108.02, -54.9) * mm});
            skLineSegment(sketch, "E127.right", {"start": v(-127.07, -57.9) * mm, "end": v(-127.07, -54.9) * mm});
            skPoint(sketch, "E128", {"position": v(-130.24, -45.2) * mm});
            skPoint(sketch, "E129", {"position": v(-117.54, -54.9) * mm});
            skPoint(sketch, "E130", {"position": v(-117.54, 69.1) * mm});
            skPoint(sketch, "E131", {"position": v(-127.24, 56.4) * mm});
            skPoint(sketch, "E132", {"position": v(34.86, 66.1) * mm});
            skPoint(sketch, "E133", {"position": v(44.56, 56.4) * mm});
            skPoint(sketch, "E134", {"position": v(34.86, -54.9) * mm});
            skPoint(sketch, "E135", {"position": v(44.56, -45.2) * mm});
            skLineSegment(sketch, "E136.bottom", {"start": v(25.33, 69.1) * mm, "end": v(44.38, 69.1) * mm});
            skLineSegment(sketch, "E136.top", {"start": v(25.33, 66.1) * mm, "end": v(44.38, 66.1) * mm});
            skLineSegment(sketch, "E136.left", {"start": v(25.33, 69.1) * mm, "end": v(25.33, 66.1) * mm});
            skLineSegment(sketch, "E136.right", {"start": v(44.38, 69.1) * mm, "end": v(44.38, 66.1) * mm});
            skSolve(sketch);
        }
        {
            var Q0;
            Q0 = qSketchRegion(id + "F13", true);
            extrude(context, id + "F14", {"entities" : qUnion([Q0]), "operationType" : NewBodyOperationType.ADD, "depth" : 101.6 * mm});
        }
        {
            var Q0;
            Q0=makeQuery(id+"F14.opExtrude","CAP_FACE",FACE,{"disambiguationData":[OSD([sQuery(id+"F13.wireOp",EDGE,"E121.bottom"),sQuery(id+"F13.wireOp",EDGE,"E121.top"),sQuery(id+"F13.wireOp",EDGE,"E121.left"),sQuery(id+"F13.wireOp",EDGE,"E121.right")])],"isStart":false});
            var sketch = newSketch(context, id + "F15", { "sketchPlane" : qUnion([Q0])});
            skLineSegment(sketch, "E137.0.0", {"start": v(-122.62, 66.1) * mm, "end": v(-122.62, 69.1) * mm});
            skLineSegment(sketch, "E137.0.1", {"start": v(-122.62, 69.1) * mm, "end": v(-112.46, 69.1) * mm});
            skLineSegment(sketch, "E137.0.2", {"start": v(-112.46, 69.1) * mm, "end": v(-112.46, 66.1) * mm});
            skLineSegment(sketch, "E137.0.3", {"start": v(-112.46, 66.1) * mm, "end": v(-122.62, 66.1) * mm});
            skLineSegment(sketch, "E138.0.0", {"start": v(-130.24, 51.31) * mm, "end": v(-130.24, 61.47) * mm});
            skLineSegment(sketch, "E138.0.1", {"start": v(-130.24, 61.47) * mm, "end": v(-127.24, 61.47) * mm});
            skLineSegment(sketch, "E138.0.2", {"start": v(-127.24, 61.47) * mm, "end": v(-127.24, 51.31) * mm});
            skLineSegment(sketch, "E138.0.3", {"start": v(-127.24, 51.31) * mm, "end": v(-130.24, 51.31) * mm});
            skLineSegment(sketch, "E139.0.0", {"start": v(29.78, 66.1) * mm, "end": v(29.78, 69.1) * mm});
            skLineSegment(sketch, "E139.0.1", {"start": v(29.78, 69.1) * mm, "end": v(39.94, 69.1) * mm});
            skLineSegment(sketch, "E139.0.2", {"start": v(39.94, 69.1) * mm, "end": v(39.94, 66.1) * mm});
            skLineSegment(sketch, "E139.0.3", {"start": v(39.94, 66.1) * mm, "end": v(29.78, 66.1) * mm});
            skLineSegment(sketch, "E140.0.0", {"start": v(44.56, 51.31) * mm, "end": v(44.56, 61.47) * mm});
            skLineSegment(sketch, "E140.0.1", {"start": v(44.56, 61.47) * mm, "end": v(47.56, 61.47) * mm});
            skLineSegment(sketch, "E140.0.2", {"start": v(47.56, 61.47) * mm, "end": v(47.56, 51.31) * mm});
            skLineSegment(sketch, "E140.0.3", {"start": v(47.56, 51.31) * mm, "end": v(44.56, 51.31) * mm});
            skLineSegment(sketch, "E141.0.0", {"start": v(44.56, -50.29) * mm, "end": v(44.56, -40.13) * mm});
            skLineSegment(sketch, "E141.0.1", {"start": v(44.56, -40.13) * mm, "end": v(47.56, -40.13) * mm});
            skLineSegment(sketch, "E141.0.2", {"start": v(47.56, -40.13) * mm, "end": v(47.56, -50.29) * mm});
            skLineSegment(sketch, "E141.0.3", {"start": v(47.56, -50.29) * mm, "end": v(44.56, -50.29) * mm});
            skLineSegment(sketch, "E142.0.0", {"start": v(29.78, -57.9) * mm, "end": v(29.78, -54.9) * mm});
            skLineSegment(sketch, "E142.0.1", {"start": v(29.78, -54.9) * mm, "end": v(39.94, -54.9) * mm});
            skLineSegment(sketch, "E142.0.2", {"start": v(39.94, -54.9) * mm, "end": v(39.94, -57.9) * mm});
            skLineSegment(sketch, "E142.0.3", {"start": v(39.94, -57.9) * mm, "end": v(29.78, -57.9) * mm});
            skLineSegment(sketch, "E143.0.0", {"start": v(-122.62, -57.9) * mm, "end": v(-122.62, -54.9) * mm});
            skLineSegment(sketch, "E143.0.1", {"start": v(-122.62, -54.9) * mm, "end": v(-112.46, -54.9) * mm});
            skLineSegment(sketch, "E143.0.2", {"start": v(-112.46, -54.9) * mm, "end": v(-112.46, -57.9) * mm});
            skLineSegment(sketch, "E143.0.3", {"start": v(-112.46, -57.9) * mm, "end": v(-122.62, -57.9) * mm});
            skLineSegment(sketch, "E144.0.0", {"start": v(-130.24, -50.29) * mm, "end": v(-130.24, -40.13) * mm});
            skLineSegment(sketch, "E144.0.1", {"start": v(-130.24, -40.13) * mm, "end": v(-127.24, -40.13) * mm});
            skLineSegment(sketch, "E144.0.2", {"start": v(-127.24, -40.13) * mm, "end": v(-127.24, -50.29) * mm});
            skLineSegment(sketch, "E144.0.3", {"start": v(-127.24, -50.29) * mm, "end": v(-130.24, -50.29) * mm});
            skSolve(sketch);
        }
        {
            var Q0;
            Q0 = qSketchRegion(id + "F15", true);
            extrude(context, id + "F16", {"entities" : qUnion([Q0]), "operationType" : NewBodyOperationType.ADD, "depth" : 3 * mm});
        }
        {
            var Q0;
            Q0=makeQuery(id+"F16.opExtrude","CAP_FACE",FACE,{"disambiguationData":[OSD([sQuery(id+"F15.wireOp",EDGE,"E143.0.0"),sQuery(id+"F15.wireOp",EDGE,"E143.0.1"),sQuery(id+"F15.wireOp",EDGE,"E143.0.2"),sQuery(id+"F15.wireOp",EDGE,"E143.0.3")])],"isStart":false});
            var sketch = newSketch(context, id + "F17", { "sketchPlane" : qUnion([Q0])});
            skLineSegment(sketch, "E145.bottom", {"start": v(-174.7, 94.5) * mm, "end": v(92, 94.5) * mm});
            skLineSegment(sketch, "E145.top", {"start": v(-174.7, -83.3) * mm, "end": v(92, -83.3) * mm});
            skLineSegment(sketch, "E145.left", {"start": v(-181.04, 88.14) * mm, "end": v(-181.04, -76.96) * mm});
            skLineSegment(sketch, "E145.right", {"start": v(98.36, 88.14) * mm, "end": v(98.36, -76.96) * mm});
            skLineSegment(sketch, "E146", {"start": v(-41.34, 81.8) * mm, "end": v(-41.34, 94.5) * mm});
            skLineSegment(sketch, "E147", {"start": v(-181.04, 5.6) * mm, "end": v(-142.94, 5.6) * mm});
            skPoint(sketch, "E148.visualSharp", {"position": v(-181.04, 94.5) * mm});
            skArc(sketch, "E148.filletArc", {"start": v(-174.7, 94.5) * mm, "mid": v(-179.18, 92.63) * mm, "end": v(-181.04, 88.14) * mm});
            skPoint(sketch, "E149.visualSharp", {"position": v(98.36, 94.5) * mm});
            skArc(sketch, "E149.filletArc", {"start": v(98.36, 88.14) * mm, "mid": v(96.5, 92.63) * mm, "end": v(92, 94.5) * mm});
            skPoint(sketch, "E150.visualSharp", {"position": v(98.36, -83.3) * mm});
            skArc(sketch, "E150.filletArc", {"start": v(92, -83.3) * mm, "mid": v(96.5, -81.45) * mm, "end": v(98.36, -76.96) * mm});
            skPoint(sketch, "E151.visualSharp", {"position": v(-181.04, -83.3) * mm});
            skArc(sketch, "E151.filletArc", {"start": v(-181.04, -76.96) * mm, "mid": v(-179.18, -81.45) * mm, "end": v(-174.7, -83.3) * mm});
            skLineSegment(sketch, "E152.0.0", {"start": v(-130.24, 51.31) * mm, "end": v(-127.24, 51.31) * mm});
            skLineSegment(sketch, "E152.0.1", {"start": v(-127.24, 51.31) * mm, "end": v(-127.24, 61.47) * mm});
            skLineSegment(sketch, "E152.0.2", {"start": v(-127.24, 61.47) * mm, "end": v(-130.24, 61.47) * mm});
            skLineSegment(sketch, "E152.0.3", {"start": v(-130.24, 61.47) * mm, "end": v(-130.24, 51.31) * mm});
            skLineSegment(sketch, "E153.0.0", {"start": v(-112.46, 66.1) * mm, "end": v(-112.46, 69.1) * mm});
            skLineSegment(sketch, "E153.0.1", {"start": v(-112.46, 69.1) * mm, "end": v(-122.62, 69.1) * mm});
            skLineSegment(sketch, "E153.0.2", {"start": v(-122.62, 69.1) * mm, "end": v(-122.62, 66.1) * mm});
            skLineSegment(sketch, "E153.0.3", {"start": v(-122.62, 66.1) * mm, "end": v(-112.46, 66.1) * mm});
            skLineSegment(sketch, "E154.0.0", {"start": v(29.78, 66.1) * mm, "end": v(39.94, 66.1) * mm});
            skLineSegment(sketch, "E154.0.1", {"start": v(39.94, 66.1) * mm, "end": v(39.94, 69.1) * mm});
            skLineSegment(sketch, "E154.0.2", {"start": v(39.94, 69.1) * mm, "end": v(29.78, 69.1) * mm});
            skLineSegment(sketch, "E154.0.3", {"start": v(29.78, 69.1) * mm, "end": v(29.78, 66.1) * mm});
            skLineSegment(sketch, "E155.0.0", {"start": v(44.56, 51.31) * mm, "end": v(47.56, 51.31) * mm});
            skLineSegment(sketch, "E155.0.1", {"start": v(47.56, 51.31) * mm, "end": v(47.56, 61.47) * mm});
            skLineSegment(sketch, "E155.0.2", {"start": v(47.56, 61.47) * mm, "end": v(44.56, 61.47) * mm});
            skLineSegment(sketch, "E155.0.3", {"start": v(44.56, 61.47) * mm, "end": v(44.56, 51.31) * mm});
            skLineSegment(sketch, "E156.0.0", {"start": v(44.56, -50.29) * mm, "end": v(47.56, -50.29) * mm});
            skLineSegment(sketch, "E156.0.1", {"start": v(47.56, -50.29) * mm, "end": v(47.56, -40.13) * mm});
            skLineSegment(sketch, "E156.0.2", {"start": v(47.56, -40.13) * mm, "end": v(44.56, -40.13) * mm});
            skLineSegment(sketch, "E156.0.3", {"start": v(44.56, -40.13) * mm, "end": v(44.56, -50.29) * mm});
            skLineSegment(sketch, "E157.0.0", {"start": v(29.78, -57.9) * mm, "end": v(39.94, -57.9) * mm});
            skLineSegment(sketch, "E157.0.1", {"start": v(39.94, -57.9) * mm, "end": v(39.94, -54.9) * mm});
            skLineSegment(sketch, "E157.0.2", {"start": v(39.94, -54.9) * mm, "end": v(29.78, -54.9) * mm});
            skLineSegment(sketch, "E157.0.3", {"start": v(29.78, -54.9) * mm, "end": v(29.78, -57.9) * mm});
            skLineSegment(sketch, "E158.0.0", {"start": v(-122.62, -57.9) * mm, "end": v(-112.46, -57.9) * mm});
            skLineSegment(sketch, "E158.0.1", {"start": v(-112.46, -57.9) * mm, "end": v(-112.46, -54.9) * mm});
            skLineSegment(sketch, "E158.0.2", {"start": v(-112.46, -54.9) * mm, "end": v(-122.62, -54.9) * mm});
            skLineSegment(sketch, "E158.0.3", {"start": v(-122.62, -54.9) * mm, "end": v(-122.62, -57.9) * mm});
            skLineSegment(sketch, "E159.0.0", {"start": v(-130.24, -50.29) * mm, "end": v(-127.24, -50.29) * mm});
            skLineSegment(sketch, "E159.0.1", {"start": v(-127.24, -50.29) * mm, "end": v(-127.24, -40.13) * mm});
            skLineSegment(sketch, "E159.0.2", {"start": v(-127.24, -40.13) * mm, "end": v(-130.24, -40.13) * mm});
            skLineSegment(sketch, "E159.0.3", {"start": v(-130.24, -40.13) * mm, "end": v(-130.24, -50.29) * mm});
            skSolve(sketch);
        }
        {
            var Q0;
            Q0 = qSketchRegion(id + "F17", true);
            extrude(context, id + "F18", {"entities" : qUnion([Q0]), "oppositeDirection" : true, "depth" : 3 * mm});
        }
        {
            var Q0;
            Q0=makeQuery(id+"F18.opExtrude","CAP_FACE",FACE,{"disambiguationData":[OSD([sQuery(id+"F17.wireOp",EDGE,"E145.bottom"),sQuery(id+"F17.wireOp",EDGE,"E145.top"),sQuery(id+"F17.wireOp",EDGE,"E145.left"),sQuery(id+"F17.wireOp",EDGE,"E145.right"),sQuery(id+"F17.wireOp",EDGE,"E148.filletArc"),sQuery(id+"F17.wireOp",EDGE,"E149.filletArc"),sQuery(id+"F17.wireOp",EDGE,"E150.filletArc"),sQuery(id+"F17.wireOp",EDGE,"E151.filletArc"),sQuery(id+"F17.wireOp",EDGE,"E152.0.0"),sQuery(id+"F17.wireOp",EDGE,"E152.0.1"),sQuery(id+"F17.wireOp",EDGE,"E152.0.2"),sQuery(id+"F17.wireOp",EDGE,"E152.0.3"),sQuery(id+"F17.wireOp",EDGE,"E153.0.0"),sQuery(id+"F17.wireOp",EDGE,"E153.0.1"),sQuery(id+"F17.wireOp",EDGE,"E153.0.2"),sQuery(id+"F17.wireOp",EDGE,"E153.0.3"),sQuery(id+"F17.wireOp",EDGE,"E154.0.0"),sQuery(id+"F17.wireOp",EDGE,"E154.0.1"),sQuery(id+"F17.wireOp",EDGE,"E154.0.2"),sQuery(id+"F17.wireOp",EDGE,"E154.0.3"),sQuery(id+"F17.wireOp",EDGE,"E155.0.0"),sQuery(id+"F17.wireOp",EDGE,"E155.0.1"),sQuery(id+"F17.wireOp",EDGE,"E155.0.2"),sQuery(id+"F17.wireOp",EDGE,"E155.0.3"),sQuery(id+"F17.wireOp",EDGE,"E156.0.0"),sQuery(id+"F17.wireOp",EDGE,"E156.0.1"),sQuery(id+"F17.wireOp",EDGE,"E156.0.2"),sQuery(id+"F17.wireOp",EDGE,"E156.0.3"),sQuery(id+"F17.wireOp",EDGE,"E157.0.0"),sQuery(id+"F17.wireOp",EDGE,"E157.0.1"),sQuery(id+"F17.wireOp",EDGE,"E157.0.2"),sQuery(id+"F17.wireOp",EDGE,"E157.0.3"),sQuery(id+"F17.wireOp",EDGE,"E158.0.0"),sQuery(id+"F17.wireOp",EDGE,"E158.0.1"),sQuery(id+"F17.wireOp",EDGE,"E158.0.2"),sQuery(id+"F17.wireOp",EDGE,"E158.0.3"),sQuery(id+"F17.wireOp",EDGE,"E159.0.0"),sQuery(id+"F17.wireOp",EDGE,"E159.0.1"),sQuery(id+"F17.wireOp",EDGE,"E159.0.2"),sQuery(id+"F17.wireOp",EDGE,"E159.0.3")])],"isStart":true});
            var sketch = newSketch(context, id + "F19", { "sketchPlane" : qUnion([Q0])});
            skLineSegment(sketch, "E160.bottom", {"start": v(-177, 90.45) * mm, "end": v(-172.38, 90.45) * mm});
            skLineSegment(sketch, "E160.top", {"start": v(-177, 85.83) * mm, "end": v(-172.38, 85.83) * mm});
            skLineSegment(sketch, "E160.left", {"start": v(-177, 90.45) * mm, "end": v(-177, 85.83) * mm});
            skLineSegment(sketch, "E160.right", {"start": v(-172.38, 90.45) * mm, "end": v(-172.38, 85.83) * mm});
            skLineSegment(sketch, "E161.0.1.0", {"start": v(-177, 77.75) * mm, "end": v(-172.38, 77.75) * mm});
            skLineSegment(sketch, "E161.0.1.1", {"start": v(-177, 77.75) * mm, "end": v(-177, 73.13) * mm});
            skLineSegment(sketch, "E161.0.1.2", {"start": v(-177, 73.13) * mm, "end": v(-172.38, 73.13) * mm});
            skLineSegment(sketch, "E161.0.1.3", {"start": v(-172.38, 77.75) * mm, "end": v(-172.38, 73.13) * mm});
            skLineSegment(sketch, "E161.0.2.0", {"start": v(-177, 65.05) * mm, "end": v(-172.38, 65.05) * mm});
            skLineSegment(sketch, "E161.0.2.1", {"start": v(-177, 65.05) * mm, "end": v(-177, 60.43) * mm});
            skLineSegment(sketch, "E161.0.2.2", {"start": v(-177, 60.43) * mm, "end": v(-172.38, 60.43) * mm});
            skLineSegment(sketch, "E161.0.2.3", {"start": v(-172.38, 65.05) * mm, "end": v(-172.38, 60.43) * mm});
            skLineSegment(sketch, "E161.0.3.0", {"start": v(-177, 52.35) * mm, "end": v(-172.38, 52.35) * mm});
            skLineSegment(sketch, "E161.0.3.1", {"start": v(-177, 52.35) * mm, "end": v(-177, 47.73) * mm});
            skLineSegment(sketch, "E161.0.3.2", {"start": v(-177, 47.73) * mm, "end": v(-172.38, 47.73) * mm});
            skLineSegment(sketch, "E161.0.3.3", {"start": v(-172.38, 52.35) * mm, "end": v(-172.38, 47.73) * mm});
            skLineSegment(sketch, "E161.0.4.0", {"start": v(-177, 39.65) * mm, "end": v(-172.38, 39.65) * mm});
            skLineSegment(sketch, "E161.0.4.1", {"start": v(-177, 39.65) * mm, "end": v(-177, 35.03) * mm});
            skLineSegment(sketch, "E161.0.4.2", {"start": v(-177, 35.03) * mm, "end": v(-172.38, 35.03) * mm});
            skLineSegment(sketch, "E161.0.4.3", {"start": v(-172.38, 39.65) * mm, "end": v(-172.38, 35.03) * mm});
            skLineSegment(sketch, "E161.0.5.0", {"start": v(-177, 26.95) * mm, "end": v(-172.38, 26.95) * mm});
            skLineSegment(sketch, "E161.0.5.1", {"start": v(-177, 26.95) * mm, "end": v(-177, 22.33) * mm});
            skLineSegment(sketch, "E161.0.5.2", {"start": v(-177, 22.33) * mm, "end": v(-172.38, 22.33) * mm});
            skLineSegment(sketch, "E161.0.5.3", {"start": v(-172.38, 26.95) * mm, "end": v(-172.38, 22.33) * mm});
            skLineSegment(sketch, "E161.0.6.0", {"start": v(-177, 14.25) * mm, "end": v(-172.38, 14.25) * mm});
            skLineSegment(sketch, "E161.0.6.1", {"start": v(-177, 14.25) * mm, "end": v(-177, 9.63) * mm});
            skLineSegment(sketch, "E161.0.6.2", {"start": v(-177, 9.63) * mm, "end": v(-172.38, 9.63) * mm});
            skLineSegment(sketch, "E161.0.6.3", {"start": v(-172.38, 14.25) * mm, "end": v(-172.38, 9.63) * mm});
            skLineSegment(sketch, "E161.0.7.0", {"start": v(-177, 1.55) * mm, "end": v(-172.38, 1.55) * mm});
            skLineSegment(sketch, "E161.0.7.1", {"start": v(-177, 1.55) * mm, "end": v(-177, -3.07) * mm});
            skLineSegment(sketch, "E161.0.7.2", {"start": v(-177, -3.07) * mm, "end": v(-172.38, -3.07) * mm});
            skLineSegment(sketch, "E161.0.7.3", {"start": v(-172.38, 1.55) * mm, "end": v(-172.38, -3.07) * mm});
            skLineSegment(sketch, "E161.0.8.0", {"start": v(-177, -11.15) * mm, "end": v(-172.38, -11.15) * mm});
            skLineSegment(sketch, "E161.0.8.1", {"start": v(-177, -11.15) * mm, "end": v(-177, -15.77) * mm});
            skLineSegment(sketch, "E161.0.8.2", {"start": v(-177, -15.77) * mm, "end": v(-172.38, -15.77) * mm});
            skLineSegment(sketch, "E161.0.8.3", {"start": v(-172.38, -11.15) * mm, "end": v(-172.38, -15.77) * mm});
            skLineSegment(sketch, "E161.0.9.0", {"start": v(-177, -23.85) * mm, "end": v(-172.38, -23.85) * mm});
            skLineSegment(sketch, "E161.0.9.1", {"start": v(-177, -23.85) * mm, "end": v(-177, -28.47) * mm});
            skLineSegment(sketch, "E161.0.9.2", {"start": v(-177, -28.47) * mm, "end": v(-172.38, -28.47) * mm});
            skLineSegment(sketch, "E161.0.9.3", {"start": v(-172.38, -23.85) * mm, "end": v(-172.38, -28.47) * mm});
            skLineSegment(sketch, "E161.0.10.0", {"start": v(-177, -36.55) * mm, "end": v(-172.38, -36.55) * mm});
            skLineSegment(sketch, "E161.0.10.1", {"start": v(-177, -36.55) * mm, "end": v(-177, -41.17) * mm});
            skLineSegment(sketch, "E161.0.10.2", {"start": v(-177, -41.17) * mm, "end": v(-172.38, -41.17) * mm});
            skLineSegment(sketch, "E161.0.10.3", {"start": v(-172.38, -36.55) * mm, "end": v(-172.38, -41.17) * mm});
            skLineSegment(sketch, "E161.0.11.0", {"start": v(-177, -49.25) * mm, "end": v(-172.38, -49.25) * mm});
            skLineSegment(sketch, "E161.0.11.1", {"start": v(-177, -49.25) * mm, "end": v(-177, -53.87) * mm});
            skLineSegment(sketch, "E161.0.11.2", {"start": v(-177, -53.87) * mm, "end": v(-172.38, -53.87) * mm});
            skLineSegment(sketch, "E161.0.11.3", {"start": v(-172.38, -49.25) * mm, "end": v(-172.38, -53.87) * mm});
            skLineSegment(sketch, "E161.0.12.0", {"start": v(-177, -61.95) * mm, "end": v(-172.38, -61.95) * mm});
            skLineSegment(sketch, "E161.0.12.1", {"start": v(-177, -61.95) * mm, "end": v(-177, -66.57) * mm});
            skLineSegment(sketch, "E161.0.12.2", {"start": v(-177, -66.57) * mm, "end": v(-172.38, -66.57) * mm});
            skLineSegment(sketch, "E161.0.12.3", {"start": v(-172.38, -61.95) * mm, "end": v(-172.38, -66.57) * mm});
            skLineSegment(sketch, "E161.1.0.0", {"start": v(-164.3, 90.45) * mm, "end": v(-159.68, 90.45) * mm});
            skLineSegment(sketch, "E161.1.0.1", {"start": v(-164.3, 90.45) * mm, "end": v(-164.3, 85.83) * mm});
            skLineSegment(sketch, "E161.1.0.2", {"start": v(-164.3, 85.83) * mm, "end": v(-159.68, 85.83) * mm});
            skLineSegment(sketch, "E161.1.0.3", {"start": v(-159.68, 90.45) * mm, "end": v(-159.68, 85.83) * mm});
            skLineSegment(sketch, "E161.1.1.0", {"start": v(-164.3, 77.75) * mm, "end": v(-159.68, 77.75) * mm});
            skLineSegment(sketch, "E161.1.1.1", {"start": v(-164.3, 77.75) * mm, "end": v(-164.3, 73.13) * mm});
            skLineSegment(sketch, "E161.1.1.2", {"start": v(-164.3, 73.13) * mm, "end": v(-159.68, 73.13) * mm});
            skLineSegment(sketch, "E161.1.1.3", {"start": v(-159.68, 77.75) * mm, "end": v(-159.68, 73.13) * mm});
            skLineSegment(sketch, "E161.1.2.0", {"start": v(-164.3, 65.05) * mm, "end": v(-159.68, 65.05) * mm});
            skLineSegment(sketch, "E161.1.2.1", {"start": v(-164.3, 65.05) * mm, "end": v(-164.3, 60.43) * mm});
            skLineSegment(sketch, "E161.1.2.2", {"start": v(-164.3, 60.43) * mm, "end": v(-159.68, 60.43) * mm});
            skLineSegment(sketch, "E161.1.2.3", {"start": v(-159.68, 65.05) * mm, "end": v(-159.68, 60.43) * mm});
            skLineSegment(sketch, "E161.1.3.0", {"start": v(-164.3, 52.35) * mm, "end": v(-159.68, 52.35) * mm});
            skLineSegment(sketch, "E161.1.3.1", {"start": v(-164.3, 52.35) * mm, "end": v(-164.3, 47.73) * mm});
            skLineSegment(sketch, "E161.1.3.2", {"start": v(-164.3, 47.73) * mm, "end": v(-159.68, 47.73) * mm});
            skLineSegment(sketch, "E161.1.3.3", {"start": v(-159.68, 52.35) * mm, "end": v(-159.68, 47.73) * mm});
            skLineSegment(sketch, "E161.1.4.0", {"start": v(-164.3, 39.65) * mm, "end": v(-159.68, 39.65) * mm});
            skLineSegment(sketch, "E161.1.4.1", {"start": v(-164.3, 39.65) * mm, "end": v(-164.3, 35.03) * mm});
            skLineSegment(sketch, "E161.1.4.2", {"start": v(-164.3, 35.03) * mm, "end": v(-159.68, 35.03) * mm});
            skLineSegment(sketch, "E161.1.4.3", {"start": v(-159.68, 39.65) * mm, "end": v(-159.68, 35.03) * mm});
            skLineSegment(sketch, "E161.1.5.0", {"start": v(-164.3, 26.95) * mm, "end": v(-159.68, 26.95) * mm});
            skLineSegment(sketch, "E161.1.5.1", {"start": v(-164.3, 26.95) * mm, "end": v(-164.3, 22.33) * mm});
            skLineSegment(sketch, "E161.1.5.2", {"start": v(-164.3, 22.33) * mm, "end": v(-159.68, 22.33) * mm});
            skLineSegment(sketch, "E161.1.5.3", {"start": v(-159.68, 26.95) * mm, "end": v(-159.68, 22.33) * mm});
            skLineSegment(sketch, "E161.1.6.0", {"start": v(-164.3, 14.25) * mm, "end": v(-159.68, 14.25) * mm});
            skLineSegment(sketch, "E161.1.6.1", {"start": v(-164.3, 14.25) * mm, "end": v(-164.3, 9.63) * mm});
            skLineSegment(sketch, "E161.1.6.2", {"start": v(-164.3, 9.63) * mm, "end": v(-159.68, 9.63) * mm});
            skLineSegment(sketch, "E161.1.6.3", {"start": v(-159.68, 14.25) * mm, "end": v(-159.68, 9.63) * mm});
            skLineSegment(sketch, "E161.1.7.0", {"start": v(-164.3, 1.55) * mm, "end": v(-159.68, 1.55) * mm});
            skLineSegment(sketch, "E161.1.7.1", {"start": v(-164.3, 1.55) * mm, "end": v(-164.3, -3.07) * mm});
            skLineSegment(sketch, "E161.1.7.2", {"start": v(-164.3, -3.07) * mm, "end": v(-159.68, -3.07) * mm});
            skLineSegment(sketch, "E161.1.7.3", {"start": v(-159.68, 1.55) * mm, "end": v(-159.68, -3.07) * mm});
            skLineSegment(sketch, "E161.1.8.0", {"start": v(-164.3, -11.15) * mm, "end": v(-159.68, -11.15) * mm});
            skLineSegment(sketch, "E161.1.8.1", {"start": v(-164.3, -11.15) * mm, "end": v(-164.3, -15.77) * mm});
            skLineSegment(sketch, "E161.1.8.2", {"start": v(-164.3, -15.77) * mm, "end": v(-159.68, -15.77) * mm});
            skLineSegment(sketch, "E161.1.8.3", {"start": v(-159.68, -11.15) * mm, "end": v(-159.68, -15.77) * mm});
            skLineSegment(sketch, "E161.1.9.0", {"start": v(-164.3, -23.85) * mm, "end": v(-159.68, -23.85) * mm});
            skLineSegment(sketch, "E161.1.9.1", {"start": v(-164.3, -23.85) * mm, "end": v(-164.3, -28.47) * mm});
            skLineSegment(sketch, "E161.1.9.2", {"start": v(-164.3, -28.47) * mm, "end": v(-159.68, -28.47) * mm});
            skLineSegment(sketch, "E161.1.9.3", {"start": v(-159.68, -23.85) * mm, "end": v(-159.68, -28.47) * mm});
            skLineSegment(sketch, "E161.1.10.0", {"start": v(-164.3, -36.55) * mm, "end": v(-159.68, -36.55) * mm});
            skLineSegment(sketch, "E161.1.10.1", {"start": v(-164.3, -36.55) * mm, "end": v(-164.3, -41.17) * mm});
            skLineSegment(sketch, "E161.1.10.2", {"start": v(-164.3, -41.17) * mm, "end": v(-159.68, -41.17) * mm});
            skLineSegment(sketch, "E161.1.10.3", {"start": v(-159.68, -36.55) * mm, "end": v(-159.68, -41.17) * mm});
            skLineSegment(sketch, "E161.1.11.0", {"start": v(-164.3, -49.25) * mm, "end": v(-159.68, -49.25) * mm});
            skLineSegment(sketch, "E161.1.11.1", {"start": v(-164.3, -49.25) * mm, "end": v(-164.3, -53.87) * mm});
            skLineSegment(sketch, "E161.1.11.2", {"start": v(-164.3, -53.87) * mm, "end": v(-159.68, -53.87) * mm});
            skLineSegment(sketch, "E161.1.11.3", {"start": v(-159.68, -49.25) * mm, "end": v(-159.68, -53.87) * mm});
            skLineSegment(sketch, "E161.1.12.0", {"start": v(-164.3, -61.95) * mm, "end": v(-159.68, -61.95) * mm});
            skLineSegment(sketch, "E161.1.12.1", {"start": v(-164.3, -61.95) * mm, "end": v(-164.3, -66.57) * mm});
            skLineSegment(sketch, "E161.1.12.2", {"start": v(-164.3, -66.57) * mm, "end": v(-159.68, -66.57) * mm});
            skLineSegment(sketch, "E161.1.12.3", {"start": v(-159.68, -61.95) * mm, "end": v(-159.68, -66.57) * mm});
            skLineSegment(sketch, "E161.2.0.0", {"start": v(-151.6, 90.45) * mm, "end": v(-146.98, 90.45) * mm});
            skLineSegment(sketch, "E161.2.0.1", {"start": v(-151.6, 90.45) * mm, "end": v(-151.6, 85.83) * mm});
            skLineSegment(sketch, "E161.2.0.2", {"start": v(-151.6, 85.83) * mm, "end": v(-146.98, 85.83) * mm});
            skLineSegment(sketch, "E161.2.0.3", {"start": v(-146.98, 90.45) * mm, "end": v(-146.98, 85.83) * mm});
            skLineSegment(sketch, "E161.2.1.0", {"start": v(-151.6, 77.75) * mm, "end": v(-146.98, 77.75) * mm});
            skLineSegment(sketch, "E161.2.1.1", {"start": v(-151.6, 77.75) * mm, "end": v(-151.6, 73.13) * mm});
            skLineSegment(sketch, "E161.2.1.2", {"start": v(-151.6, 73.13) * mm, "end": v(-146.98, 73.13) * mm});
            skLineSegment(sketch, "E161.2.1.3", {"start": v(-146.98, 77.75) * mm, "end": v(-146.98, 73.13) * mm});
            skLineSegment(sketch, "E161.2.2.0", {"start": v(-151.6, 65.05) * mm, "end": v(-146.98, 65.05) * mm});
            skLineSegment(sketch, "E161.2.2.1", {"start": v(-151.6, 65.05) * mm, "end": v(-151.6, 60.43) * mm});
            skLineSegment(sketch, "E161.2.2.2", {"start": v(-151.6, 60.43) * mm, "end": v(-146.98, 60.43) * mm});
            skLineSegment(sketch, "E161.2.2.3", {"start": v(-146.98, 65.05) * mm, "end": v(-146.98, 60.43) * mm});
            skLineSegment(sketch, "E161.2.3.0", {"start": v(-151.6, 52.35) * mm, "end": v(-146.98, 52.35) * mm});
            skLineSegment(sketch, "E161.2.3.1", {"start": v(-151.6, 52.35) * mm, "end": v(-151.6, 47.73) * mm});
            skLineSegment(sketch, "E161.2.3.2", {"start": v(-151.6, 47.73) * mm, "end": v(-146.98, 47.73) * mm});
            skLineSegment(sketch, "E161.2.3.3", {"start": v(-146.98, 52.35) * mm, "end": v(-146.98, 47.73) * mm});
            skLineSegment(sketch, "E161.2.4.0", {"start": v(-151.6, 39.65) * mm, "end": v(-146.98, 39.65) * mm});
            skLineSegment(sketch, "E161.2.4.1", {"start": v(-151.6, 39.65) * mm, "end": v(-151.6, 35.03) * mm});
            skLineSegment(sketch, "E161.2.4.2", {"start": v(-151.6, 35.03) * mm, "end": v(-146.98, 35.03) * mm});
            skLineSegment(sketch, "E161.2.4.3", {"start": v(-146.98, 39.65) * mm, "end": v(-146.98, 35.03) * mm});
            skLineSegment(sketch, "E161.2.5.0", {"start": v(-151.6, 26.95) * mm, "end": v(-146.98, 26.95) * mm});
            skLineSegment(sketch, "E161.2.5.1", {"start": v(-151.6, 26.95) * mm, "end": v(-151.6, 22.33) * mm});
            skLineSegment(sketch, "E161.2.5.2", {"start": v(-151.6, 22.33) * mm, "end": v(-146.98, 22.33) * mm});
            skLineSegment(sketch, "E161.2.5.3", {"start": v(-146.98, 26.95) * mm, "end": v(-146.98, 22.33) * mm});
            skLineSegment(sketch, "E161.2.6.0", {"start": v(-151.6, 14.25) * mm, "end": v(-146.98, 14.25) * mm});
            skLineSegment(sketch, "E161.2.6.1", {"start": v(-151.6, 14.25) * mm, "end": v(-151.6, 9.63) * mm});
            skLineSegment(sketch, "E161.2.6.2", {"start": v(-151.6, 9.63) * mm, "end": v(-146.98, 9.63) * mm});
            skLineSegment(sketch, "E161.2.6.3", {"start": v(-146.98, 14.25) * mm, "end": v(-146.98, 9.63) * mm});
            skLineSegment(sketch, "E161.2.7.0", {"start": v(-151.6, 1.55) * mm, "end": v(-146.98, 1.55) * mm});
            skLineSegment(sketch, "E161.2.7.1", {"start": v(-151.6, 1.55) * mm, "end": v(-151.6, -3.07) * mm});
            skLineSegment(sketch, "E161.2.7.2", {"start": v(-151.6, -3.07) * mm, "end": v(-146.98, -3.07) * mm});
            skLineSegment(sketch, "E161.2.7.3", {"start": v(-146.98, 1.55) * mm, "end": v(-146.98, -3.07) * mm});
            skLineSegment(sketch, "E161.2.8.0", {"start": v(-151.6, -11.15) * mm, "end": v(-146.98, -11.15) * mm});
            skLineSegment(sketch, "E161.2.8.1", {"start": v(-151.6, -11.15) * mm, "end": v(-151.6, -15.77) * mm});
            skLineSegment(sketch, "E161.2.8.2", {"start": v(-151.6, -15.77) * mm, "end": v(-146.98, -15.77) * mm});
            skLineSegment(sketch, "E161.2.8.3", {"start": v(-146.98, -11.15) * mm, "end": v(-146.98, -15.77) * mm});
            skLineSegment(sketch, "E161.2.9.0", {"start": v(-151.6, -23.85) * mm, "end": v(-146.98, -23.85) * mm});
            skLineSegment(sketch, "E161.2.9.1", {"start": v(-151.6, -23.85) * mm, "end": v(-151.6, -28.47) * mm});
            skLineSegment(sketch, "E161.2.9.2", {"start": v(-151.6, -28.47) * mm, "end": v(-146.98, -28.47) * mm});
            skLineSegment(sketch, "E161.2.9.3", {"start": v(-146.98, -23.85) * mm, "end": v(-146.98, -28.47) * mm});
            skLineSegment(sketch, "E161.2.10.0", {"start": v(-151.6, -36.55) * mm, "end": v(-146.98, -36.55) * mm});
            skLineSegment(sketch, "E161.2.10.1", {"start": v(-151.6, -36.55) * mm, "end": v(-151.6, -41.17) * mm});
            skLineSegment(sketch, "E161.2.10.2", {"start": v(-151.6, -41.17) * mm, "end": v(-146.98, -41.17) * mm});
            skLineSegment(sketch, "E161.2.10.3", {"start": v(-146.98, -36.55) * mm, "end": v(-146.98, -41.17) * mm});
            skLineSegment(sketch, "E161.2.11.0", {"start": v(-151.6, -49.25) * mm, "end": v(-146.98, -49.25) * mm});
            skLineSegment(sketch, "E161.2.11.1", {"start": v(-151.6, -49.25) * mm, "end": v(-151.6, -53.87) * mm});
            skLineSegment(sketch, "E161.2.11.2", {"start": v(-151.6, -53.87) * mm, "end": v(-146.98, -53.87) * mm});
            skLineSegment(sketch, "E161.2.11.3", {"start": v(-146.98, -49.25) * mm, "end": v(-146.98, -53.87) * mm});
            skLineSegment(sketch, "E161.2.12.0", {"start": v(-151.6, -61.95) * mm, "end": v(-146.98, -61.95) * mm});
            skLineSegment(sketch, "E161.2.12.1", {"start": v(-151.6, -61.95) * mm, "end": v(-151.6, -66.57) * mm});
            skLineSegment(sketch, "E161.2.12.2", {"start": v(-151.6, -66.57) * mm, "end": v(-146.98, -66.57) * mm});
            skLineSegment(sketch, "E161.2.12.3", {"start": v(-146.98, -61.95) * mm, "end": v(-146.98, -66.57) * mm});
            skLineSegment(sketch, "E161.3.0.0", {"start": v(-138.9, 90.45) * mm, "end": v(-134.28, 90.45) * mm});
            skLineSegment(sketch, "E161.3.0.1", {"start": v(-138.9, 90.45) * mm, "end": v(-138.9, 85.83) * mm});
            skLineSegment(sketch, "E161.3.0.2", {"start": v(-138.9, 85.83) * mm, "end": v(-134.28, 85.83) * mm});
            skLineSegment(sketch, "E161.3.0.3", {"start": v(-134.28, 90.45) * mm, "end": v(-134.28, 85.83) * mm});
            skLineSegment(sketch, "E161.3.1.0", {"start": v(-138.9, 77.75) * mm, "end": v(-134.28, 77.75) * mm});
            skLineSegment(sketch, "E161.3.1.1", {"start": v(-138.9, 77.75) * mm, "end": v(-138.9, 73.13) * mm});
            skLineSegment(sketch, "E161.3.1.2", {"start": v(-138.9, 73.13) * mm, "end": v(-134.28, 73.13) * mm});
            skLineSegment(sketch, "E161.3.1.3", {"start": v(-134.28, 77.75) * mm, "end": v(-134.28, 73.13) * mm});
            skLineSegment(sketch, "E161.3.2.0", {"start": v(-138.9, 65.05) * mm, "end": v(-134.28, 65.05) * mm});
            skLineSegment(sketch, "E161.3.2.1", {"start": v(-138.9, 65.05) * mm, "end": v(-138.9, 60.43) * mm});
            skLineSegment(sketch, "E161.3.2.2", {"start": v(-138.9, 60.43) * mm, "end": v(-134.28, 60.43) * mm});
            skLineSegment(sketch, "E161.3.2.3", {"start": v(-134.28, 65.05) * mm, "end": v(-134.28, 60.43) * mm});
            skLineSegment(sketch, "E161.3.3.0", {"start": v(-138.9, 52.35) * mm, "end": v(-134.28, 52.35) * mm});
            skLineSegment(sketch, "E161.3.3.1", {"start": v(-138.9, 52.35) * mm, "end": v(-138.9, 47.73) * mm});
            skLineSegment(sketch, "E161.3.3.2", {"start": v(-138.9, 47.73) * mm, "end": v(-134.28, 47.73) * mm});
            skLineSegment(sketch, "E161.3.3.3", {"start": v(-134.28, 52.35) * mm, "end": v(-134.28, 47.73) * mm});
            skLineSegment(sketch, "E161.3.4.0", {"start": v(-138.9, 39.65) * mm, "end": v(-134.28, 39.65) * mm});
            skLineSegment(sketch, "E161.3.4.1", {"start": v(-138.9, 39.65) * mm, "end": v(-138.9, 35.03) * mm});
            skLineSegment(sketch, "E161.3.4.2", {"start": v(-138.9, 35.03) * mm, "end": v(-134.28, 35.03) * mm});
            skLineSegment(sketch, "E161.3.4.3", {"start": v(-134.28, 39.65) * mm, "end": v(-134.28, 35.03) * mm});
            skLineSegment(sketch, "E161.3.5.0", {"start": v(-138.9, 26.95) * mm, "end": v(-134.28, 26.95) * mm});
            skLineSegment(sketch, "E161.3.5.1", {"start": v(-138.9, 26.95) * mm, "end": v(-138.9, 22.33) * mm});
            skLineSegment(sketch, "E161.3.5.2", {"start": v(-138.9, 22.33) * mm, "end": v(-134.28, 22.33) * mm});
            skLineSegment(sketch, "E161.3.5.3", {"start": v(-134.28, 26.95) * mm, "end": v(-134.28, 22.33) * mm});
            skLineSegment(sketch, "E161.3.6.0", {"start": v(-138.9, 14.25) * mm, "end": v(-134.28, 14.25) * mm});
            skLineSegment(sketch, "E161.3.6.1", {"start": v(-138.9, 14.25) * mm, "end": v(-138.9, 9.63) * mm});
            skLineSegment(sketch, "E161.3.6.2", {"start": v(-138.9, 9.63) * mm, "end": v(-134.28, 9.63) * mm});
            skLineSegment(sketch, "E161.3.6.3", {"start": v(-134.28, 14.25) * mm, "end": v(-134.28, 9.63) * mm});
            skLineSegment(sketch, "E161.3.7.0", {"start": v(-138.9, 1.55) * mm, "end": v(-134.28, 1.55) * mm});
            skLineSegment(sketch, "E161.3.7.1", {"start": v(-138.9, 1.55) * mm, "end": v(-138.9, -3.07) * mm});
            skLineSegment(sketch, "E161.3.7.2", {"start": v(-138.9, -3.07) * mm, "end": v(-134.28, -3.07) * mm});
            skLineSegment(sketch, "E161.3.7.3", {"start": v(-134.28, 1.55) * mm, "end": v(-134.28, -3.07) * mm});
            skLineSegment(sketch, "E161.3.8.0", {"start": v(-138.9, -11.15) * mm, "end": v(-134.28, -11.15) * mm});
            skLineSegment(sketch, "E161.3.8.1", {"start": v(-138.9, -11.15) * mm, "end": v(-138.9, -15.77) * mm});
            skLineSegment(sketch, "E161.3.8.2", {"start": v(-138.9, -15.77) * mm, "end": v(-134.28, -15.77) * mm});
            skLineSegment(sketch, "E161.3.8.3", {"start": v(-134.28, -11.15) * mm, "end": v(-134.28, -15.77) * mm});
            skLineSegment(sketch, "E161.3.9.0", {"start": v(-138.9, -23.85) * mm, "end": v(-134.28, -23.85) * mm});
            skLineSegment(sketch, "E161.3.9.1", {"start": v(-138.9, -23.85) * mm, "end": v(-138.9, -28.47) * mm});
            skLineSegment(sketch, "E161.3.9.2", {"start": v(-138.9, -28.47) * mm, "end": v(-134.28, -28.47) * mm});
            skLineSegment(sketch, "E161.3.9.3", {"start": v(-134.28, -23.85) * mm, "end": v(-134.28, -28.47) * mm});
            skLineSegment(sketch, "E161.3.10.0", {"start": v(-138.9, -36.55) * mm, "end": v(-134.28, -36.55) * mm});
            skLineSegment(sketch, "E161.3.10.1", {"start": v(-138.9, -36.55) * mm, "end": v(-138.9, -41.17) * mm});
            skLineSegment(sketch, "E161.3.10.2", {"start": v(-138.9, -41.17) * mm, "end": v(-134.28, -41.17) * mm});
            skLineSegment(sketch, "E161.3.10.3", {"start": v(-134.28, -36.55) * mm, "end": v(-134.28, -41.17) * mm});
            skLineSegment(sketch, "E161.3.11.0", {"start": v(-138.9, -49.25) * mm, "end": v(-134.28, -49.25) * mm});
            skLineSegment(sketch, "E161.3.11.1", {"start": v(-138.9, -49.25) * mm, "end": v(-138.9, -53.87) * mm});
            skLineSegment(sketch, "E161.3.11.2", {"start": v(-138.9, -53.87) * mm, "end": v(-134.28, -53.87) * mm});
            skLineSegment(sketch, "E161.3.11.3", {"start": v(-134.28, -49.25) * mm, "end": v(-134.28, -53.87) * mm});
            skLineSegment(sketch, "E161.3.12.0", {"start": v(-138.9, -61.95) * mm, "end": v(-134.28, -61.95) * mm});
            skLineSegment(sketch, "E161.3.12.1", {"start": v(-138.9, -61.95) * mm, "end": v(-138.9, -66.57) * mm});
            skLineSegment(sketch, "E161.3.12.2", {"start": v(-138.9, -66.57) * mm, "end": v(-134.28, -66.57) * mm});
            skLineSegment(sketch, "E161.3.12.3", {"start": v(-134.28, -61.95) * mm, "end": v(-134.28, -66.57) * mm});
            skLineSegment(sketch, "E161.4.0.0", {"start": v(-126.2, 90.45) * mm, "end": v(-121.58, 90.45) * mm});
            skLineSegment(sketch, "E161.4.0.1", {"start": v(-126.2, 90.45) * mm, "end": v(-126.2, 85.83) * mm});
            skLineSegment(sketch, "E161.4.0.2", {"start": v(-126.2, 85.83) * mm, "end": v(-121.58, 85.83) * mm});
            skLineSegment(sketch, "E161.4.0.3", {"start": v(-121.58, 90.45) * mm, "end": v(-121.58, 85.83) * mm});
            skLineSegment(sketch, "E161.4.1.0", {"start": v(-126.2, 77.75) * mm, "end": v(-121.58, 77.75) * mm});
            skLineSegment(sketch, "E161.4.1.1", {"start": v(-126.2, 77.75) * mm, "end": v(-126.2, 73.13) * mm});
            skLineSegment(sketch, "E161.4.1.2", {"start": v(-126.2, 73.13) * mm, "end": v(-121.58, 73.13) * mm});
            skLineSegment(sketch, "E161.4.1.3", {"start": v(-121.58, 77.75) * mm, "end": v(-121.58, 73.13) * mm});
            skLineSegment(sketch, "E161.4.2.0", {"start": v(-126.2, 65.05) * mm, "end": v(-121.58, 65.05) * mm});
            skLineSegment(sketch, "E161.4.2.1", {"start": v(-126.2, 65.05) * mm, "end": v(-126.2, 60.43) * mm});
            skLineSegment(sketch, "E161.4.2.2", {"start": v(-126.2, 60.43) * mm, "end": v(-121.58, 60.43) * mm});
            skLineSegment(sketch, "E161.4.2.3", {"start": v(-121.58, 65.05) * mm, "end": v(-121.58, 60.43) * mm});
            skLineSegment(sketch, "E161.4.3.0", {"start": v(-126.2, 52.35) * mm, "end": v(-121.58, 52.35) * mm});
            skLineSegment(sketch, "E161.4.3.1", {"start": v(-126.2, 52.35) * mm, "end": v(-126.2, 47.73) * mm});
            skLineSegment(sketch, "E161.4.3.2", {"start": v(-126.2, 47.73) * mm, "end": v(-121.58, 47.73) * mm});
            skLineSegment(sketch, "E161.4.3.3", {"start": v(-121.58, 52.35) * mm, "end": v(-121.58, 47.73) * mm});
            skLineSegment(sketch, "E161.4.4.0", {"start": v(-126.2, 39.65) * mm, "end": v(-121.58, 39.65) * mm});
            skLineSegment(sketch, "E161.4.4.1", {"start": v(-126.2, 39.65) * mm, "end": v(-126.2, 35.03) * mm});
            skLineSegment(sketch, "E161.4.4.2", {"start": v(-126.2, 35.03) * mm, "end": v(-121.58, 35.03) * mm});
            skLineSegment(sketch, "E161.4.4.3", {"start": v(-121.58, 39.65) * mm, "end": v(-121.58, 35.03) * mm});
            skLineSegment(sketch, "E161.4.5.0", {"start": v(-126.2, 26.95) * mm, "end": v(-121.58, 26.95) * mm});
            skLineSegment(sketch, "E161.4.5.1", {"start": v(-126.2, 26.95) * mm, "end": v(-126.2, 22.33) * mm});
            skLineSegment(sketch, "E161.4.5.2", {"start": v(-126.2, 22.33) * mm, "end": v(-121.58, 22.33) * mm});
            skLineSegment(sketch, "E161.4.5.3", {"start": v(-121.58, 26.95) * mm, "end": v(-121.58, 22.33) * mm});
            skLineSegment(sketch, "E161.4.6.0", {"start": v(-126.2, 14.25) * mm, "end": v(-121.58, 14.25) * mm});
            skLineSegment(sketch, "E161.4.6.1", {"start": v(-126.2, 14.25) * mm, "end": v(-126.2, 9.63) * mm});
            skLineSegment(sketch, "E161.4.6.2", {"start": v(-126.2, 9.63) * mm, "end": v(-121.58, 9.63) * mm});
            skLineSegment(sketch, "E161.4.6.3", {"start": v(-121.58, 14.25) * mm, "end": v(-121.58, 9.63) * mm});
            skLineSegment(sketch, "E161.4.7.0", {"start": v(-126.2, 1.55) * mm, "end": v(-121.58, 1.55) * mm});
            skLineSegment(sketch, "E161.4.7.1", {"start": v(-126.2, 1.55) * mm, "end": v(-126.2, -3.07) * mm});
            skLineSegment(sketch, "E161.4.7.2", {"start": v(-126.2, -3.07) * mm, "end": v(-121.58, -3.07) * mm});
            skLineSegment(sketch, "E161.4.7.3", {"start": v(-121.58, 1.55) * mm, "end": v(-121.58, -3.07) * mm});
            skLineSegment(sketch, "E161.4.8.0", {"start": v(-126.2, -11.15) * mm, "end": v(-121.58, -11.15) * mm});
            skLineSegment(sketch, "E161.4.8.1", {"start": v(-126.2, -11.15) * mm, "end": v(-126.2, -15.77) * mm});
            skLineSegment(sketch, "E161.4.8.2", {"start": v(-126.2, -15.77) * mm, "end": v(-121.58, -15.77) * mm});
            skLineSegment(sketch, "E161.4.8.3", {"start": v(-121.58, -11.15) * mm, "end": v(-121.58, -15.77) * mm});
            skLineSegment(sketch, "E161.4.9.0", {"start": v(-126.2, -23.85) * mm, "end": v(-121.58, -23.85) * mm});
            skLineSegment(sketch, "E161.4.9.1", {"start": v(-126.2, -23.85) * mm, "end": v(-126.2, -28.47) * mm});
            skLineSegment(sketch, "E161.4.9.2", {"start": v(-126.2, -28.47) * mm, "end": v(-121.58, -28.47) * mm});
            skLineSegment(sketch, "E161.4.9.3", {"start": v(-121.58, -23.85) * mm, "end": v(-121.58, -28.47) * mm});
            skLineSegment(sketch, "E161.4.10.0", {"start": v(-126.2, -36.55) * mm, "end": v(-121.58, -36.55) * mm});
            skLineSegment(sketch, "E161.4.10.1", {"start": v(-126.2, -36.55) * mm, "end": v(-126.2, -41.17) * mm});
            skLineSegment(sketch, "E161.4.10.2", {"start": v(-126.2, -41.17) * mm, "end": v(-121.58, -41.17) * mm});
            skLineSegment(sketch, "E161.4.10.3", {"start": v(-121.58, -36.55) * mm, "end": v(-121.58, -41.17) * mm});
            skLineSegment(sketch, "E161.4.11.0", {"start": v(-126.2, -49.25) * mm, "end": v(-121.58, -49.25) * mm});
            skLineSegment(sketch, "E161.4.11.1", {"start": v(-126.2, -49.25) * mm, "end": v(-126.2, -53.87) * mm});
            skLineSegment(sketch, "E161.4.11.2", {"start": v(-126.2, -53.87) * mm, "end": v(-121.58, -53.87) * mm});
            skLineSegment(sketch, "E161.4.11.3", {"start": v(-121.58, -49.25) * mm, "end": v(-121.58, -53.87) * mm});
            skLineSegment(sketch, "E161.4.12.0", {"start": v(-126.2, -61.95) * mm, "end": v(-121.58, -61.95) * mm});
            skLineSegment(sketch, "E161.4.12.1", {"start": v(-126.2, -61.95) * mm, "end": v(-126.2, -66.57) * mm});
            skLineSegment(sketch, "E161.4.12.2", {"start": v(-126.2, -66.57) * mm, "end": v(-121.58, -66.57) * mm});
            skLineSegment(sketch, "E161.4.12.3", {"start": v(-121.58, -61.95) * mm, "end": v(-121.58, -66.57) * mm});
            skLineSegment(sketch, "E161.5.0.0", {"start": v(-113.5, 90.45) * mm, "end": v(-108.88, 90.45) * mm});
            skLineSegment(sketch, "E161.5.0.1", {"start": v(-113.5, 90.45) * mm, "end": v(-113.5, 85.83) * mm});
            skLineSegment(sketch, "E161.5.0.2", {"start": v(-113.5, 85.83) * mm, "end": v(-108.88, 85.83) * mm});
            skLineSegment(sketch, "E161.5.0.3", {"start": v(-108.88, 90.45) * mm, "end": v(-108.88, 85.83) * mm});
            skLineSegment(sketch, "E161.5.1.0", {"start": v(-113.5, 77.75) * mm, "end": v(-108.88, 77.75) * mm});
            skLineSegment(sketch, "E161.5.1.1", {"start": v(-113.5, 77.75) * mm, "end": v(-113.5, 73.13) * mm});
            skLineSegment(sketch, "E161.5.1.2", {"start": v(-113.5, 73.13) * mm, "end": v(-108.88, 73.13) * mm});
            skLineSegment(sketch, "E161.5.1.3", {"start": v(-108.88, 77.75) * mm, "end": v(-108.88, 73.13) * mm});
            skLineSegment(sketch, "E161.5.2.0", {"start": v(-113.5, 65.05) * mm, "end": v(-108.88, 65.05) * mm});
            skLineSegment(sketch, "E161.5.2.1", {"start": v(-113.5, 65.05) * mm, "end": v(-113.5, 60.43) * mm});
            skLineSegment(sketch, "E161.5.2.2", {"start": v(-113.5, 60.43) * mm, "end": v(-108.88, 60.43) * mm});
            skLineSegment(sketch, "E161.5.2.3", {"start": v(-108.88, 65.05) * mm, "end": v(-108.88, 60.43) * mm});
            skLineSegment(sketch, "E161.5.3.0", {"start": v(-113.5, 52.35) * mm, "end": v(-108.88, 52.35) * mm});
            skLineSegment(sketch, "E161.5.3.1", {"start": v(-113.5, 52.35) * mm, "end": v(-113.5, 47.73) * mm});
            skLineSegment(sketch, "E161.5.3.2", {"start": v(-113.5, 47.73) * mm, "end": v(-108.88, 47.73) * mm});
            skLineSegment(sketch, "E161.5.3.3", {"start": v(-108.88, 52.35) * mm, "end": v(-108.88, 47.73) * mm});
            skLineSegment(sketch, "E161.5.4.0", {"start": v(-113.5, 39.65) * mm, "end": v(-108.88, 39.65) * mm});
            skLineSegment(sketch, "E161.5.4.1", {"start": v(-113.5, 39.65) * mm, "end": v(-113.5, 35.03) * mm});
            skLineSegment(sketch, "E161.5.4.2", {"start": v(-113.5, 35.03) * mm, "end": v(-108.88, 35.03) * mm});
            skLineSegment(sketch, "E161.5.4.3", {"start": v(-108.88, 39.65) * mm, "end": v(-108.88, 35.03) * mm});
            skLineSegment(sketch, "E161.5.5.0", {"start": v(-113.5, 26.95) * mm, "end": v(-108.88, 26.95) * mm});
            skLineSegment(sketch, "E161.5.5.1", {"start": v(-113.5, 26.95) * mm, "end": v(-113.5, 22.33) * mm});
            skLineSegment(sketch, "E161.5.5.2", {"start": v(-113.5, 22.33) * mm, "end": v(-108.88, 22.33) * mm});
            skLineSegment(sketch, "E161.5.5.3", {"start": v(-108.88, 26.95) * mm, "end": v(-108.88, 22.33) * mm});
            skLineSegment(sketch, "E161.5.6.0", {"start": v(-113.5, 14.25) * mm, "end": v(-108.88, 14.25) * mm});
            skLineSegment(sketch, "E161.5.6.1", {"start": v(-113.5, 14.25) * mm, "end": v(-113.5, 9.63) * mm});
            skLineSegment(sketch, "E161.5.6.2", {"start": v(-113.5, 9.63) * mm, "end": v(-108.88, 9.63) * mm});
            skLineSegment(sketch, "E161.5.6.3", {"start": v(-108.88, 14.25) * mm, "end": v(-108.88, 9.63) * mm});
            skLineSegment(sketch, "E161.5.7.0", {"start": v(-113.5, 1.55) * mm, "end": v(-108.88, 1.55) * mm});
            skLineSegment(sketch, "E161.5.7.1", {"start": v(-113.5, 1.55) * mm, "end": v(-113.5, -3.07) * mm});
            skLineSegment(sketch, "E161.5.7.2", {"start": v(-113.5, -3.07) * mm, "end": v(-108.88, -3.07) * mm});
            skLineSegment(sketch, "E161.5.7.3", {"start": v(-108.88, 1.55) * mm, "end": v(-108.88, -3.07) * mm});
            skLineSegment(sketch, "E161.5.8.0", {"start": v(-113.5, -11.15) * mm, "end": v(-108.88, -11.15) * mm});
            skLineSegment(sketch, "E161.5.8.1", {"start": v(-113.5, -11.15) * mm, "end": v(-113.5, -15.77) * mm});
            skLineSegment(sketch, "E161.5.8.2", {"start": v(-113.5, -15.77) * mm, "end": v(-108.88, -15.77) * mm});
            skLineSegment(sketch, "E161.5.8.3", {"start": v(-108.88, -11.15) * mm, "end": v(-108.88, -15.77) * mm});
            skLineSegment(sketch, "E161.5.9.0", {"start": v(-113.5, -23.85) * mm, "end": v(-108.88, -23.85) * mm});
            skLineSegment(sketch, "E161.5.9.1", {"start": v(-113.5, -23.85) * mm, "end": v(-113.5, -28.47) * mm});
            skLineSegment(sketch, "E161.5.9.2", {"start": v(-113.5, -28.47) * mm, "end": v(-108.88, -28.47) * mm});
            skLineSegment(sketch, "E161.5.9.3", {"start": v(-108.88, -23.85) * mm, "end": v(-108.88, -28.47) * mm});
            skLineSegment(sketch, "E161.5.10.0", {"start": v(-113.5, -36.55) * mm, "end": v(-108.88, -36.55) * mm});
            skLineSegment(sketch, "E161.5.10.1", {"start": v(-113.5, -36.55) * mm, "end": v(-113.5, -41.17) * mm});
            skLineSegment(sketch, "E161.5.10.2", {"start": v(-113.5, -41.17) * mm, "end": v(-108.88, -41.17) * mm});
            skLineSegment(sketch, "E161.5.10.3", {"start": v(-108.88, -36.55) * mm, "end": v(-108.88, -41.17) * mm});
            skLineSegment(sketch, "E161.5.11.0", {"start": v(-113.5, -49.25) * mm, "end": v(-108.88, -49.25) * mm});
            skLineSegment(sketch, "E161.5.11.1", {"start": v(-113.5, -49.25) * mm, "end": v(-113.5, -53.87) * mm});
            skLineSegment(sketch, "E161.5.11.2", {"start": v(-113.5, -53.87) * mm, "end": v(-108.88, -53.87) * mm});
            skLineSegment(sketch, "E161.5.11.3", {"start": v(-108.88, -49.25) * mm, "end": v(-108.88, -53.87) * mm});
            skLineSegment(sketch, "E161.5.12.0", {"start": v(-113.5, -61.95) * mm, "end": v(-108.88, -61.95) * mm});
            skLineSegment(sketch, "E161.5.12.1", {"start": v(-113.5, -61.95) * mm, "end": v(-113.5, -66.57) * mm});
            skLineSegment(sketch, "E161.5.12.2", {"start": v(-113.5, -66.57) * mm, "end": v(-108.88, -66.57) * mm});
            skLineSegment(sketch, "E161.5.12.3", {"start": v(-108.88, -61.95) * mm, "end": v(-108.88, -66.57) * mm});
            skLineSegment(sketch, "E161.6.0.0", {"start": v(-100.8, 90.45) * mm, "end": v(-96.18, 90.45) * mm});
            skLineSegment(sketch, "E161.6.0.1", {"start": v(-100.8, 90.45) * mm, "end": v(-100.8, 85.83) * mm});
            skLineSegment(sketch, "E161.6.0.2", {"start": v(-100.8, 85.83) * mm, "end": v(-96.18, 85.83) * mm});
            skLineSegment(sketch, "E161.6.0.3", {"start": v(-96.18, 90.45) * mm, "end": v(-96.18, 85.83) * mm});
            skLineSegment(sketch, "E161.6.1.0", {"start": v(-100.8, 77.75) * mm, "end": v(-96.18, 77.75) * mm});
            skLineSegment(sketch, "E161.6.1.1", {"start": v(-100.8, 77.75) * mm, "end": v(-100.8, 73.13) * mm});
            skLineSegment(sketch, "E161.6.1.2", {"start": v(-100.8, 73.13) * mm, "end": v(-96.18, 73.13) * mm});
            skLineSegment(sketch, "E161.6.1.3", {"start": v(-96.18, 77.75) * mm, "end": v(-96.18, 73.13) * mm});
            skLineSegment(sketch, "E161.6.2.0", {"start": v(-100.8, 65.05) * mm, "end": v(-96.18, 65.05) * mm});
            skLineSegment(sketch, "E161.6.2.1", {"start": v(-100.8, 65.05) * mm, "end": v(-100.8, 60.43) * mm});
            skLineSegment(sketch, "E161.6.2.2", {"start": v(-100.8, 60.43) * mm, "end": v(-96.18, 60.43) * mm});
            skLineSegment(sketch, "E161.6.2.3", {"start": v(-96.18, 65.05) * mm, "end": v(-96.18, 60.43) * mm});
            skLineSegment(sketch, "E161.6.3.0", {"start": v(-100.8, 52.35) * mm, "end": v(-96.18, 52.35) * mm});
            skLineSegment(sketch, "E161.6.3.1", {"start": v(-100.8, 52.35) * mm, "end": v(-100.8, 47.73) * mm});
            skLineSegment(sketch, "E161.6.3.2", {"start": v(-100.8, 47.73) * mm, "end": v(-96.18, 47.73) * mm});
            skLineSegment(sketch, "E161.6.3.3", {"start": v(-96.18, 52.35) * mm, "end": v(-96.18, 47.73) * mm});
            skLineSegment(sketch, "E161.6.4.0", {"start": v(-100.8, 39.65) * mm, "end": v(-96.18, 39.65) * mm});
            skLineSegment(sketch, "E161.6.4.1", {"start": v(-100.8, 39.65) * mm, "end": v(-100.8, 35.03) * mm});
            skLineSegment(sketch, "E161.6.4.2", {"start": v(-100.8, 35.03) * mm, "end": v(-96.18, 35.03) * mm});
            skLineSegment(sketch, "E161.6.4.3", {"start": v(-96.18, 39.65) * mm, "end": v(-96.18, 35.03) * mm});
            skLineSegment(sketch, "E161.6.5.0", {"start": v(-100.8, 26.95) * mm, "end": v(-96.18, 26.95) * mm});
            skLineSegment(sketch, "E161.6.5.1", {"start": v(-100.8, 26.95) * mm, "end": v(-100.8, 22.33) * mm});
            skLineSegment(sketch, "E161.6.5.2", {"start": v(-100.8, 22.33) * mm, "end": v(-96.18, 22.33) * mm});
            skLineSegment(sketch, "E161.6.5.3", {"start": v(-96.18, 26.95) * mm, "end": v(-96.18, 22.33) * mm});
            skLineSegment(sketch, "E161.6.6.0", {"start": v(-100.8, 14.25) * mm, "end": v(-96.18, 14.25) * mm});
            skLineSegment(sketch, "E161.6.6.1", {"start": v(-100.8, 14.25) * mm, "end": v(-100.8, 9.63) * mm});
            skLineSegment(sketch, "E161.6.6.2", {"start": v(-100.8, 9.63) * mm, "end": v(-96.18, 9.63) * mm});
            skLineSegment(sketch, "E161.6.6.3", {"start": v(-96.18, 14.25) * mm, "end": v(-96.18, 9.63) * mm});
            skLineSegment(sketch, "E161.6.7.0", {"start": v(-100.8, 1.55) * mm, "end": v(-96.18, 1.55) * mm});
            skLineSegment(sketch, "E161.6.7.1", {"start": v(-100.8, 1.55) * mm, "end": v(-100.8, -3.07) * mm});
            skLineSegment(sketch, "E161.6.7.2", {"start": v(-100.8, -3.07) * mm, "end": v(-96.18, -3.07) * mm});
            skLineSegment(sketch, "E161.6.7.3", {"start": v(-96.18, 1.55) * mm, "end": v(-96.18, -3.07) * mm});
            skLineSegment(sketch, "E161.6.8.0", {"start": v(-100.8, -11.15) * mm, "end": v(-96.18, -11.15) * mm});
            skLineSegment(sketch, "E161.6.8.1", {"start": v(-100.8, -11.15) * mm, "end": v(-100.8, -15.77) * mm});
            skLineSegment(sketch, "E161.6.8.2", {"start": v(-100.8, -15.77) * mm, "end": v(-96.18, -15.77) * mm});
            skLineSegment(sketch, "E161.6.8.3", {"start": v(-96.18, -11.15) * mm, "end": v(-96.18, -15.77) * mm});
            skLineSegment(sketch, "E161.6.9.0", {"start": v(-100.8, -23.85) * mm, "end": v(-96.18, -23.85) * mm});
            skLineSegment(sketch, "E161.6.9.1", {"start": v(-100.8, -23.85) * mm, "end": v(-100.8, -28.47) * mm});
            skLineSegment(sketch, "E161.6.9.2", {"start": v(-100.8, -28.47) * mm, "end": v(-96.18, -28.47) * mm});
            skLineSegment(sketch, "E161.6.9.3", {"start": v(-96.18, -23.85) * mm, "end": v(-96.18, -28.47) * mm});
            skLineSegment(sketch, "E161.6.10.0", {"start": v(-100.8, -36.55) * mm, "end": v(-96.18, -36.55) * mm});
            skLineSegment(sketch, "E161.6.10.1", {"start": v(-100.8, -36.55) * mm, "end": v(-100.8, -41.17) * mm});
            skLineSegment(sketch, "E161.6.10.2", {"start": v(-100.8, -41.17) * mm, "end": v(-96.18, -41.17) * mm});
            skLineSegment(sketch, "E161.6.10.3", {"start": v(-96.18, -36.55) * mm, "end": v(-96.18, -41.17) * mm});
            skLineSegment(sketch, "E161.6.11.0", {"start": v(-100.8, -49.25) * mm, "end": v(-96.18, -49.25) * mm});
            skLineSegment(sketch, "E161.6.11.1", {"start": v(-100.8, -49.25) * mm, "end": v(-100.8, -53.87) * mm});
            skLineSegment(sketch, "E161.6.11.2", {"start": v(-100.8, -53.87) * mm, "end": v(-96.18, -53.87) * mm});
            skLineSegment(sketch, "E161.6.11.3", {"start": v(-96.18, -49.25) * mm, "end": v(-96.18, -53.87) * mm});
            skLineSegment(sketch, "E161.6.12.0", {"start": v(-100.8, -61.95) * mm, "end": v(-96.18, -61.95) * mm});
            skLineSegment(sketch, "E161.6.12.1", {"start": v(-100.8, -61.95) * mm, "end": v(-100.8, -66.57) * mm});
            skLineSegment(sketch, "E161.6.12.2", {"start": v(-100.8, -66.57) * mm, "end": v(-96.18, -66.57) * mm});
            skLineSegment(sketch, "E161.6.12.3", {"start": v(-96.18, -61.95) * mm, "end": v(-96.18, -66.57) * mm});
            skLineSegment(sketch, "E161.7.0.0", {"start": v(-88.1, 90.45) * mm, "end": v(-83.48, 90.45) * mm});
            skLineSegment(sketch, "E161.7.0.1", {"start": v(-88.1, 90.45) * mm, "end": v(-88.1, 85.83) * mm});
            skLineSegment(sketch, "E161.7.0.2", {"start": v(-88.1, 85.83) * mm, "end": v(-83.48, 85.83) * mm});
            skLineSegment(sketch, "E161.7.0.3", {"start": v(-83.48, 90.45) * mm, "end": v(-83.48, 85.83) * mm});
            skLineSegment(sketch, "E161.7.1.0", {"start": v(-88.1, 77.75) * mm, "end": v(-83.48, 77.75) * mm});
            skLineSegment(sketch, "E161.7.1.1", {"start": v(-88.1, 77.75) * mm, "end": v(-88.1, 73.13) * mm});
            skLineSegment(sketch, "E161.7.1.2", {"start": v(-88.1, 73.13) * mm, "end": v(-83.48, 73.13) * mm});
            skLineSegment(sketch, "E161.7.1.3", {"start": v(-83.48, 77.75) * mm, "end": v(-83.48, 73.13) * mm});
            skLineSegment(sketch, "E161.7.2.0", {"start": v(-88.1, 65.05) * mm, "end": v(-83.48, 65.05) * mm});
            skLineSegment(sketch, "E161.7.2.1", {"start": v(-88.1, 65.05) * mm, "end": v(-88.1, 60.43) * mm});
            skLineSegment(sketch, "E161.7.2.2", {"start": v(-88.1, 60.43) * mm, "end": v(-83.48, 60.43) * mm});
            skLineSegment(sketch, "E161.7.2.3", {"start": v(-83.48, 65.05) * mm, "end": v(-83.48, 60.43) * mm});
            skLineSegment(sketch, "E161.7.3.0", {"start": v(-88.1, 52.35) * mm, "end": v(-83.48, 52.35) * mm});
            skLineSegment(sketch, "E161.7.3.1", {"start": v(-88.1, 52.35) * mm, "end": v(-88.1, 47.73) * mm});
            skLineSegment(sketch, "E161.7.3.2", {"start": v(-88.1, 47.73) * mm, "end": v(-83.48, 47.73) * mm});
            skLineSegment(sketch, "E161.7.3.3", {"start": v(-83.48, 52.35) * mm, "end": v(-83.48, 47.73) * mm});
            skLineSegment(sketch, "E161.7.4.0", {"start": v(-88.1, 39.65) * mm, "end": v(-83.48, 39.65) * mm});
            skLineSegment(sketch, "E161.7.4.1", {"start": v(-88.1, 39.65) * mm, "end": v(-88.1, 35.03) * mm});
            skLineSegment(sketch, "E161.7.4.2", {"start": v(-88.1, 35.03) * mm, "end": v(-83.48, 35.03) * mm});
            skLineSegment(sketch, "E161.7.4.3", {"start": v(-83.48, 39.65) * mm, "end": v(-83.48, 35.03) * mm});
            skLineSegment(sketch, "E161.7.5.0", {"start": v(-88.1, 26.95) * mm, "end": v(-83.48, 26.95) * mm});
            skLineSegment(sketch, "E161.7.5.1", {"start": v(-88.1, 26.95) * mm, "end": v(-88.1, 22.33) * mm});
            skLineSegment(sketch, "E161.7.5.2", {"start": v(-88.1, 22.33) * mm, "end": v(-83.48, 22.33) * mm});
            skLineSegment(sketch, "E161.7.5.3", {"start": v(-83.48, 26.95) * mm, "end": v(-83.48, 22.33) * mm});
            skLineSegment(sketch, "E161.7.6.0", {"start": v(-88.1, 14.25) * mm, "end": v(-83.48, 14.25) * mm});
            skLineSegment(sketch, "E161.7.6.1", {"start": v(-88.1, 14.25) * mm, "end": v(-88.1, 9.63) * mm});
            skLineSegment(sketch, "E161.7.6.2", {"start": v(-88.1, 9.63) * mm, "end": v(-83.48, 9.63) * mm});
            skLineSegment(sketch, "E161.7.6.3", {"start": v(-83.48, 14.25) * mm, "end": v(-83.48, 9.63) * mm});
            skLineSegment(sketch, "E161.7.7.0", {"start": v(-88.1, 1.55) * mm, "end": v(-83.48, 1.55) * mm});
            skLineSegment(sketch, "E161.7.7.1", {"start": v(-88.1, 1.55) * mm, "end": v(-88.1, -3.07) * mm});
            skLineSegment(sketch, "E161.7.7.2", {"start": v(-88.1, -3.07) * mm, "end": v(-83.48, -3.07) * mm});
            skLineSegment(sketch, "E161.7.7.3", {"start": v(-83.48, 1.55) * mm, "end": v(-83.48, -3.07) * mm});
            skLineSegment(sketch, "E161.7.8.0", {"start": v(-88.1, -11.15) * mm, "end": v(-83.48, -11.15) * mm});
            skLineSegment(sketch, "E161.7.8.1", {"start": v(-88.1, -11.15) * mm, "end": v(-88.1, -15.77) * mm});
            skLineSegment(sketch, "E161.7.8.2", {"start": v(-88.1, -15.77) * mm, "end": v(-83.48, -15.77) * mm});
            skLineSegment(sketch, "E161.7.8.3", {"start": v(-83.48, -11.15) * mm, "end": v(-83.48, -15.77) * mm});
            skLineSegment(sketch, "E161.7.9.0", {"start": v(-88.1, -23.85) * mm, "end": v(-83.48, -23.85) * mm});
            skLineSegment(sketch, "E161.7.9.1", {"start": v(-88.1, -23.85) * mm, "end": v(-88.1, -28.47) * mm});
            skLineSegment(sketch, "E161.7.9.2", {"start": v(-88.1, -28.47) * mm, "end": v(-83.48, -28.47) * mm});
            skLineSegment(sketch, "E161.7.9.3", {"start": v(-83.48, -23.85) * mm, "end": v(-83.48, -28.47) * mm});
            skLineSegment(sketch, "E161.7.10.0", {"start": v(-88.1, -36.55) * mm, "end": v(-83.48, -36.55) * mm});
            skLineSegment(sketch, "E161.7.10.1", {"start": v(-88.1, -36.55) * mm, "end": v(-88.1, -41.17) * mm});
            skLineSegment(sketch, "E161.7.10.2", {"start": v(-88.1, -41.17) * mm, "end": v(-83.48, -41.17) * mm});
            skLineSegment(sketch, "E161.7.10.3", {"start": v(-83.48, -36.55) * mm, "end": v(-83.48, -41.17) * mm});
            skLineSegment(sketch, "E161.7.11.0", {"start": v(-88.1, -49.25) * mm, "end": v(-83.48, -49.25) * mm});
            skLineSegment(sketch, "E161.7.11.1", {"start": v(-88.1, -49.25) * mm, "end": v(-88.1, -53.87) * mm});
            skLineSegment(sketch, "E161.7.11.2", {"start": v(-88.1, -53.87) * mm, "end": v(-83.48, -53.87) * mm});
            skLineSegment(sketch, "E161.7.11.3", {"start": v(-83.48, -49.25) * mm, "end": v(-83.48, -53.87) * mm});
            skLineSegment(sketch, "E161.7.12.0", {"start": v(-88.1, -61.95) * mm, "end": v(-83.48, -61.95) * mm});
            skLineSegment(sketch, "E161.7.12.1", {"start": v(-88.1, -61.95) * mm, "end": v(-88.1, -66.57) * mm});
            skLineSegment(sketch, "E161.7.12.2", {"start": v(-88.1, -66.57) * mm, "end": v(-83.48, -66.57) * mm});
            skLineSegment(sketch, "E161.7.12.3", {"start": v(-83.48, -61.95) * mm, "end": v(-83.48, -66.57) * mm});
            skLineSegment(sketch, "E161.8.0.0", {"start": v(-75.4, 90.45) * mm, "end": v(-70.78, 90.45) * mm});
            skLineSegment(sketch, "E161.8.0.1", {"start": v(-75.4, 90.45) * mm, "end": v(-75.4, 85.83) * mm});
            skLineSegment(sketch, "E161.8.0.2", {"start": v(-75.4, 85.83) * mm, "end": v(-70.78, 85.83) * mm});
            skLineSegment(sketch, "E161.8.0.3", {"start": v(-70.78, 90.45) * mm, "end": v(-70.78, 85.83) * mm});
            skLineSegment(sketch, "E161.8.1.0", {"start": v(-75.4, 77.75) * mm, "end": v(-70.78, 77.75) * mm});
            skLineSegment(sketch, "E161.8.1.1", {"start": v(-75.4, 77.75) * mm, "end": v(-75.4, 73.13) * mm});
            skLineSegment(sketch, "E161.8.1.2", {"start": v(-75.4, 73.13) * mm, "end": v(-70.78, 73.13) * mm});
            skLineSegment(sketch, "E161.8.1.3", {"start": v(-70.78, 77.75) * mm, "end": v(-70.78, 73.13) * mm});
            skLineSegment(sketch, "E161.8.2.0", {"start": v(-75.4, 65.05) * mm, "end": v(-70.78, 65.05) * mm});
            skLineSegment(sketch, "E161.8.2.1", {"start": v(-75.4, 65.05) * mm, "end": v(-75.4, 60.43) * mm});
            skLineSegment(sketch, "E161.8.2.2", {"start": v(-75.4, 60.43) * mm, "end": v(-70.78, 60.43) * mm});
            skLineSegment(sketch, "E161.8.2.3", {"start": v(-70.78, 65.05) * mm, "end": v(-70.78, 60.43) * mm});
            skLineSegment(sketch, "E161.8.3.0", {"start": v(-75.4, 52.35) * mm, "end": v(-70.78, 52.35) * mm});
            skLineSegment(sketch, "E161.8.3.1", {"start": v(-75.4, 52.35) * mm, "end": v(-75.4, 47.73) * mm});
            skLineSegment(sketch, "E161.8.3.2", {"start": v(-75.4, 47.73) * mm, "end": v(-70.78, 47.73) * mm});
            skLineSegment(sketch, "E161.8.3.3", {"start": v(-70.78, 52.35) * mm, "end": v(-70.78, 47.73) * mm});
            skLineSegment(sketch, "E161.8.6.0", {"start": v(-75.4, 14.25) * mm, "end": v(-70.78, 14.25) * mm});
            skLineSegment(sketch, "E161.8.6.1", {"start": v(-75.4, 14.25) * mm, "end": v(-75.4, 9.63) * mm});
            skLineSegment(sketch, "E161.8.6.2", {"start": v(-75.4, 9.63) * mm, "end": v(-70.78, 9.63) * mm});
            skLineSegment(sketch, "E161.8.6.3", {"start": v(-70.78, 14.25) * mm, "end": v(-70.78, 9.63) * mm});
            skLineSegment(sketch, "E161.8.7.0", {"start": v(-75.4, 1.55) * mm, "end": v(-70.78, 1.55) * mm});
            skLineSegment(sketch, "E161.8.7.1", {"start": v(-75.4, 1.55) * mm, "end": v(-75.4, -3.07) * mm});
            skLineSegment(sketch, "E161.8.7.2", {"start": v(-75.4, -3.07) * mm, "end": v(-70.78, -3.07) * mm});
            skLineSegment(sketch, "E161.8.7.3", {"start": v(-70.78, 1.55) * mm, "end": v(-70.78, -3.07) * mm});
            skLineSegment(sketch, "E161.8.8.0", {"start": v(-75.4, -11.15) * mm, "end": v(-70.78, -11.15) * mm});
            skLineSegment(sketch, "E161.8.8.1", {"start": v(-75.4, -11.15) * mm, "end": v(-75.4, -15.77) * mm});
            skLineSegment(sketch, "E161.8.8.2", {"start": v(-75.4, -15.77) * mm, "end": v(-70.78, -15.77) * mm});
            skLineSegment(sketch, "E161.8.8.3", {"start": v(-70.78, -11.15) * mm, "end": v(-70.78, -15.77) * mm});
            skLineSegment(sketch, "E161.8.9.0", {"start": v(-75.4, -23.85) * mm, "end": v(-70.78, -23.85) * mm});
            skLineSegment(sketch, "E161.8.9.1", {"start": v(-75.4, -23.85) * mm, "end": v(-75.4, -28.47) * mm});
            skLineSegment(sketch, "E161.8.9.2", {"start": v(-75.4, -28.47) * mm, "end": v(-70.78, -28.47) * mm});
            skLineSegment(sketch, "E161.8.9.3", {"start": v(-70.78, -23.85) * mm, "end": v(-70.78, -28.47) * mm});
            skLineSegment(sketch, "E161.8.10.0", {"start": v(-75.4, -36.55) * mm, "end": v(-70.78, -36.55) * mm});
            skLineSegment(sketch, "E161.8.10.1", {"start": v(-75.4, -36.55) * mm, "end": v(-75.4, -41.17) * mm});
            skLineSegment(sketch, "E161.8.10.2", {"start": v(-75.4, -41.17) * mm, "end": v(-70.78, -41.17) * mm});
            skLineSegment(sketch, "E161.8.10.3", {"start": v(-70.78, -36.55) * mm, "end": v(-70.78, -41.17) * mm});
            skLineSegment(sketch, "E161.8.11.0", {"start": v(-75.4, -49.25) * mm, "end": v(-70.78, -49.25) * mm});
            skLineSegment(sketch, "E161.8.11.1", {"start": v(-75.4, -49.25) * mm, "end": v(-75.4, -53.87) * mm});
            skLineSegment(sketch, "E161.8.11.2", {"start": v(-75.4, -53.87) * mm, "end": v(-70.78, -53.87) * mm});
            skLineSegment(sketch, "E161.8.11.3", {"start": v(-70.78, -49.25) * mm, "end": v(-70.78, -53.87) * mm});
            skLineSegment(sketch, "E161.8.12.0", {"start": v(-75.4, -61.95) * mm, "end": v(-70.78, -61.95) * mm});
            skLineSegment(sketch, "E161.8.12.1", {"start": v(-75.4, -61.95) * mm, "end": v(-75.4, -66.57) * mm});
            skLineSegment(sketch, "E161.8.12.2", {"start": v(-75.4, -66.57) * mm, "end": v(-70.78, -66.57) * mm});
            skLineSegment(sketch, "E161.8.12.3", {"start": v(-70.78, -61.95) * mm, "end": v(-70.78, -66.57) * mm});
            skLineSegment(sketch, "E161.9.0.0", {"start": v(-62.7, 90.45) * mm, "end": v(-58.08, 90.45) * mm});
            skLineSegment(sketch, "E161.9.0.1", {"start": v(-62.7, 90.45) * mm, "end": v(-62.7, 85.83) * mm});
            skLineSegment(sketch, "E161.9.0.2", {"start": v(-62.7, 85.83) * mm, "end": v(-58.08, 85.83) * mm});
            skLineSegment(sketch, "E161.9.0.3", {"start": v(-58.08, 90.45) * mm, "end": v(-58.08, 85.83) * mm});
            skLineSegment(sketch, "E161.9.1.0", {"start": v(-62.7, 77.75) * mm, "end": v(-58.08, 77.75) * mm});
            skLineSegment(sketch, "E161.9.1.1", {"start": v(-62.7, 77.75) * mm, "end": v(-62.7, 73.13) * mm});
            skLineSegment(sketch, "E161.9.1.2", {"start": v(-62.7, 73.13) * mm, "end": v(-58.08, 73.13) * mm});
            skLineSegment(sketch, "E161.9.1.3", {"start": v(-58.08, 77.75) * mm, "end": v(-58.08, 73.13) * mm});
            skLineSegment(sketch, "E161.9.2.0", {"start": v(-62.7, 65.05) * mm, "end": v(-58.08, 65.05) * mm});
            skLineSegment(sketch, "E161.9.2.1", {"start": v(-62.7, 65.05) * mm, "end": v(-62.7, 60.43) * mm});
            skLineSegment(sketch, "E161.9.2.2", {"start": v(-62.7, 60.43) * mm, "end": v(-58.08, 60.43) * mm});
            skLineSegment(sketch, "E161.9.2.3", {"start": v(-58.08, 65.05) * mm, "end": v(-58.08, 60.43) * mm});
            skLineSegment(sketch, "E161.9.3.0", {"start": v(-62.7, 52.35) * mm, "end": v(-58.08, 52.35) * mm});
            skLineSegment(sketch, "E161.9.3.1", {"start": v(-62.7, 52.35) * mm, "end": v(-62.7, 47.73) * mm});
            skLineSegment(sketch, "E161.9.3.2", {"start": v(-62.7, 47.73) * mm, "end": v(-58.08, 47.73) * mm});
            skLineSegment(sketch, "E161.9.3.3", {"start": v(-58.08, 52.35) * mm, "end": v(-58.08, 47.73) * mm});
            skLineSegment(sketch, "E161.9.6.0", {"start": v(-62.7, 14.25) * mm, "end": v(-58.08, 14.25) * mm});
            skLineSegment(sketch, "E161.9.6.1", {"start": v(-62.7, 14.25) * mm, "end": v(-62.7, 9.63) * mm});
            skLineSegment(sketch, "E161.9.6.2", {"start": v(-62.7, 9.63) * mm, "end": v(-58.08, 9.63) * mm});
            skLineSegment(sketch, "E161.9.6.3", {"start": v(-58.08, 14.25) * mm, "end": v(-58.08, 9.63) * mm});
            skLineSegment(sketch, "E161.9.7.0", {"start": v(-62.7, 1.55) * mm, "end": v(-58.08, 1.55) * mm});
            skLineSegment(sketch, "E161.9.7.1", {"start": v(-62.7, 1.55) * mm, "end": v(-62.7, -3.07) * mm});
            skLineSegment(sketch, "E161.9.7.2", {"start": v(-62.7, -3.07) * mm, "end": v(-58.08, -3.07) * mm});
            skLineSegment(sketch, "E161.9.7.3", {"start": v(-58.08, 1.55) * mm, "end": v(-58.08, -3.07) * mm});
            skLineSegment(sketch, "E161.9.8.0", {"start": v(-62.7, -11.15) * mm, "end": v(-58.08, -11.15) * mm});
            skLineSegment(sketch, "E161.9.8.1", {"start": v(-62.7, -11.15) * mm, "end": v(-62.7, -15.77) * mm});
            skLineSegment(sketch, "E161.9.8.2", {"start": v(-62.7, -15.77) * mm, "end": v(-58.08, -15.77) * mm});
            skLineSegment(sketch, "E161.9.8.3", {"start": v(-58.08, -11.15) * mm, "end": v(-58.08, -15.77) * mm});
            skLineSegment(sketch, "E161.9.9.0", {"start": v(-62.7, -23.85) * mm, "end": v(-58.08, -23.85) * mm});
            skLineSegment(sketch, "E161.9.9.1", {"start": v(-62.7, -23.85) * mm, "end": v(-62.7, -28.47) * mm});
            skLineSegment(sketch, "E161.9.9.2", {"start": v(-62.7, -28.47) * mm, "end": v(-58.08, -28.47) * mm});
            skLineSegment(sketch, "E161.9.9.3", {"start": v(-58.08, -23.85) * mm, "end": v(-58.08, -28.47) * mm});
            skLineSegment(sketch, "E161.9.10.0", {"start": v(-62.7, -36.55) * mm, "end": v(-58.08, -36.55) * mm});
            skLineSegment(sketch, "E161.9.10.1", {"start": v(-62.7, -36.55) * mm, "end": v(-62.7, -41.17) * mm});
            skLineSegment(sketch, "E161.9.10.2", {"start": v(-62.7, -41.17) * mm, "end": v(-58.08, -41.17) * mm});
            skLineSegment(sketch, "E161.9.10.3", {"start": v(-58.08, -36.55) * mm, "end": v(-58.08, -41.17) * mm});
            skLineSegment(sketch, "E161.9.11.0", {"start": v(-62.7, -49.25) * mm, "end": v(-58.08, -49.25) * mm});
            skLineSegment(sketch, "E161.9.11.1", {"start": v(-62.7, -49.25) * mm, "end": v(-62.7, -53.87) * mm});
            skLineSegment(sketch, "E161.9.11.2", {"start": v(-62.7, -53.87) * mm, "end": v(-58.08, -53.87) * mm});
            skLineSegment(sketch, "E161.9.11.3", {"start": v(-58.08, -49.25) * mm, "end": v(-58.08, -53.87) * mm});
            skLineSegment(sketch, "E161.9.12.0", {"start": v(-62.7, -61.95) * mm, "end": v(-58.08, -61.95) * mm});
            skLineSegment(sketch, "E161.9.12.1", {"start": v(-62.7, -61.95) * mm, "end": v(-62.7, -66.57) * mm});
            skLineSegment(sketch, "E161.9.12.2", {"start": v(-62.7, -66.57) * mm, "end": v(-58.08, -66.57) * mm});
            skLineSegment(sketch, "E161.9.12.3", {"start": v(-58.08, -61.95) * mm, "end": v(-58.08, -66.57) * mm});
            skLineSegment(sketch, "E161.10.0.0", {"start": v(-50, 90.45) * mm, "end": v(-45.38, 90.45) * mm});
            skLineSegment(sketch, "E161.10.0.1", {"start": v(-50, 90.45) * mm, "end": v(-50, 85.83) * mm});
            skLineSegment(sketch, "E161.10.0.2", {"start": v(-50, 85.83) * mm, "end": v(-45.38, 85.83) * mm});
            skLineSegment(sketch, "E161.10.0.3", {"start": v(-45.38, 90.45) * mm, "end": v(-45.38, 85.83) * mm});
            skLineSegment(sketch, "E161.10.1.0", {"start": v(-50, 77.75) * mm, "end": v(-45.38, 77.75) * mm});
            skLineSegment(sketch, "E161.10.1.1", {"start": v(-50, 77.75) * mm, "end": v(-50, 73.13) * mm});
            skLineSegment(sketch, "E161.10.1.2", {"start": v(-50, 73.13) * mm, "end": v(-45.38, 73.13) * mm});
            skLineSegment(sketch, "E161.10.1.3", {"start": v(-45.38, 77.75) * mm, "end": v(-45.38, 73.13) * mm});
            skLineSegment(sketch, "E161.10.2.0", {"start": v(-50, 65.05) * mm, "end": v(-45.38, 65.05) * mm});
            skLineSegment(sketch, "E161.10.2.1", {"start": v(-50, 65.05) * mm, "end": v(-50, 60.43) * mm});
            skLineSegment(sketch, "E161.10.2.2", {"start": v(-50, 60.43) * mm, "end": v(-45.38, 60.43) * mm});
            skLineSegment(sketch, "E161.10.2.3", {"start": v(-45.38, 65.05) * mm, "end": v(-45.38, 60.43) * mm});
            skLineSegment(sketch, "E161.10.3.0", {"start": v(-50, 52.35) * mm, "end": v(-45.38, 52.35) * mm});
            skLineSegment(sketch, "E161.10.3.1", {"start": v(-50, 52.35) * mm, "end": v(-50, 47.73) * mm});
            skLineSegment(sketch, "E161.10.3.2", {"start": v(-50, 47.73) * mm, "end": v(-45.38, 47.73) * mm});
            skLineSegment(sketch, "E161.10.3.3", {"start": v(-45.38, 52.35) * mm, "end": v(-45.38, 47.73) * mm});
            skLineSegment(sketch, "E161.10.6.0", {"start": v(-50, 14.25) * mm, "end": v(-45.38, 14.25) * mm});
            skLineSegment(sketch, "E161.10.6.1", {"start": v(-50, 14.25) * mm, "end": v(-50, 9.63) * mm});
            skLineSegment(sketch, "E161.10.6.2", {"start": v(-50, 9.63) * mm, "end": v(-45.38, 9.63) * mm});
            skLineSegment(sketch, "E161.10.6.3", {"start": v(-45.38, 14.25) * mm, "end": v(-45.38, 9.63) * mm});
            skLineSegment(sketch, "E161.10.7.0", {"start": v(-50, 1.55) * mm, "end": v(-45.38, 1.55) * mm});
            skLineSegment(sketch, "E161.10.7.1", {"start": v(-50, 1.55) * mm, "end": v(-50, -3.07) * mm});
            skLineSegment(sketch, "E161.10.7.2", {"start": v(-50, -3.07) * mm, "end": v(-45.38, -3.07) * mm});
            skLineSegment(sketch, "E161.10.7.3", {"start": v(-45.38, 1.55) * mm, "end": v(-45.38, -3.07) * mm});
            skLineSegment(sketch, "E161.10.8.0", {"start": v(-50, -11.15) * mm, "end": v(-45.38, -11.15) * mm});
            skLineSegment(sketch, "E161.10.8.1", {"start": v(-50, -11.15) * mm, "end": v(-50, -15.77) * mm});
            skLineSegment(sketch, "E161.10.8.2", {"start": v(-50, -15.77) * mm, "end": v(-45.38, -15.77) * mm});
            skLineSegment(sketch, "E161.10.8.3", {"start": v(-45.38, -11.15) * mm, "end": v(-45.38, -15.77) * mm});
            skLineSegment(sketch, "E161.10.9.0", {"start": v(-50, -23.85) * mm, "end": v(-45.38, -23.85) * mm});
            skLineSegment(sketch, "E161.10.9.1", {"start": v(-50, -23.85) * mm, "end": v(-50, -28.47) * mm});
            skLineSegment(sketch, "E161.10.9.2", {"start": v(-50, -28.47) * mm, "end": v(-45.38, -28.47) * mm});
            skLineSegment(sketch, "E161.10.9.3", {"start": v(-45.38, -23.85) * mm, "end": v(-45.38, -28.47) * mm});
            skLineSegment(sketch, "E161.10.10.0", {"start": v(-50, -36.55) * mm, "end": v(-45.38, -36.55) * mm});
            skLineSegment(sketch, "E161.10.10.1", {"start": v(-50, -36.55) * mm, "end": v(-50, -41.17) * mm});
            skLineSegment(sketch, "E161.10.10.2", {"start": v(-50, -41.17) * mm, "end": v(-45.38, -41.17) * mm});
            skLineSegment(sketch, "E161.10.10.3", {"start": v(-45.38, -36.55) * mm, "end": v(-45.38, -41.17) * mm});
            skLineSegment(sketch, "E161.10.11.0", {"start": v(-50, -49.25) * mm, "end": v(-45.38, -49.25) * mm});
            skLineSegment(sketch, "E161.10.11.1", {"start": v(-50, -49.25) * mm, "end": v(-50, -53.87) * mm});
            skLineSegment(sketch, "E161.10.11.2", {"start": v(-50, -53.87) * mm, "end": v(-45.38, -53.87) * mm});
            skLineSegment(sketch, "E161.10.11.3", {"start": v(-45.38, -49.25) * mm, "end": v(-45.38, -53.87) * mm});
            skLineSegment(sketch, "E161.10.12.0", {"start": v(-50, -61.95) * mm, "end": v(-45.38, -61.95) * mm});
            skLineSegment(sketch, "E161.10.12.1", {"start": v(-50, -61.95) * mm, "end": v(-50, -66.57) * mm});
            skLineSegment(sketch, "E161.10.12.2", {"start": v(-50, -66.57) * mm, "end": v(-45.38, -66.57) * mm});
            skLineSegment(sketch, "E161.10.12.3", {"start": v(-45.38, -61.95) * mm, "end": v(-45.38, -66.57) * mm});
            skLineSegment(sketch, "E161.11.0.0", {"start": v(-37.3, 90.45) * mm, "end": v(-32.68, 90.45) * mm});
            skLineSegment(sketch, "E161.11.0.1", {"start": v(-37.3, 90.45) * mm, "end": v(-37.3, 85.83) * mm});
            skLineSegment(sketch, "E161.11.0.2", {"start": v(-37.3, 85.83) * mm, "end": v(-32.68, 85.83) * mm});
            skLineSegment(sketch, "E161.11.0.3", {"start": v(-32.68, 90.45) * mm, "end": v(-32.68, 85.83) * mm});
            skLineSegment(sketch, "E161.11.1.0", {"start": v(-37.3, 77.75) * mm, "end": v(-32.68, 77.75) * mm});
            skLineSegment(sketch, "E161.11.1.1", {"start": v(-37.3, 77.75) * mm, "end": v(-37.3, 73.13) * mm});
            skLineSegment(sketch, "E161.11.1.2", {"start": v(-37.3, 73.13) * mm, "end": v(-32.68, 73.13) * mm});
            skLineSegment(sketch, "E161.11.1.3", {"start": v(-32.68, 77.75) * mm, "end": v(-32.68, 73.13) * mm});
            skLineSegment(sketch, "E161.11.2.0", {"start": v(-37.3, 65.05) * mm, "end": v(-32.68, 65.05) * mm});
            skLineSegment(sketch, "E161.11.2.1", {"start": v(-37.3, 65.05) * mm, "end": v(-37.3, 60.43) * mm});
            skLineSegment(sketch, "E161.11.2.2", {"start": v(-37.3, 60.43) * mm, "end": v(-32.68, 60.43) * mm});
            skLineSegment(sketch, "E161.11.2.3", {"start": v(-32.68, 65.05) * mm, "end": v(-32.68, 60.43) * mm});
            skLineSegment(sketch, "E161.11.3.0", {"start": v(-37.3, 52.35) * mm, "end": v(-32.68, 52.35) * mm});
            skLineSegment(sketch, "E161.11.3.1", {"start": v(-37.3, 52.35) * mm, "end": v(-37.3, 47.73) * mm});
            skLineSegment(sketch, "E161.11.3.2", {"start": v(-37.3, 47.73) * mm, "end": v(-32.68, 47.73) * mm});
            skLineSegment(sketch, "E161.11.3.3", {"start": v(-32.68, 52.35) * mm, "end": v(-32.68, 47.73) * mm});
            skLineSegment(sketch, "E161.11.6.0", {"start": v(-37.3, 14.25) * mm, "end": v(-32.68, 14.25) * mm});
            skLineSegment(sketch, "E161.11.6.1", {"start": v(-37.3, 14.25) * mm, "end": v(-37.3, 9.63) * mm});
            skLineSegment(sketch, "E161.11.6.2", {"start": v(-37.3, 9.63) * mm, "end": v(-32.68, 9.63) * mm});
            skLineSegment(sketch, "E161.11.6.3", {"start": v(-32.68, 14.25) * mm, "end": v(-32.68, 9.63) * mm});
            skLineSegment(sketch, "E161.11.7.0", {"start": v(-37.3, 1.55) * mm, "end": v(-32.68, 1.55) * mm});
            skLineSegment(sketch, "E161.11.7.1", {"start": v(-37.3, 1.55) * mm, "end": v(-37.3, -3.07) * mm});
            skLineSegment(sketch, "E161.11.7.2", {"start": v(-37.3, -3.07) * mm, "end": v(-32.68, -3.07) * mm});
            skLineSegment(sketch, "E161.11.7.3", {"start": v(-32.68, 1.55) * mm, "end": v(-32.68, -3.07) * mm});
            skLineSegment(sketch, "E161.11.8.0", {"start": v(-37.3, -11.15) * mm, "end": v(-32.68, -11.15) * mm});
            skLineSegment(sketch, "E161.11.8.1", {"start": v(-37.3, -11.15) * mm, "end": v(-37.3, -15.77) * mm});
            skLineSegment(sketch, "E161.11.8.2", {"start": v(-37.3, -15.77) * mm, "end": v(-32.68, -15.77) * mm});
            skLineSegment(sketch, "E161.11.8.3", {"start": v(-32.68, -11.15) * mm, "end": v(-32.68, -15.77) * mm});
            skLineSegment(sketch, "E161.11.9.0", {"start": v(-37.3, -23.85) * mm, "end": v(-32.68, -23.85) * mm});
            skLineSegment(sketch, "E161.11.9.1", {"start": v(-37.3, -23.85) * mm, "end": v(-37.3, -28.47) * mm});
            skLineSegment(sketch, "E161.11.9.2", {"start": v(-37.3, -28.47) * mm, "end": v(-32.68, -28.47) * mm});
            skLineSegment(sketch, "E161.11.9.3", {"start": v(-32.68, -23.85) * mm, "end": v(-32.68, -28.47) * mm});
            skLineSegment(sketch, "E161.11.10.0", {"start": v(-37.3, -36.55) * mm, "end": v(-32.68, -36.55) * mm});
            skLineSegment(sketch, "E161.11.10.1", {"start": v(-37.3, -36.55) * mm, "end": v(-37.3, -41.17) * mm});
            skLineSegment(sketch, "E161.11.10.2", {"start": v(-37.3, -41.17) * mm, "end": v(-32.68, -41.17) * mm});
            skLineSegment(sketch, "E161.11.10.3", {"start": v(-32.68, -36.55) * mm, "end": v(-32.68, -41.17) * mm});
            skLineSegment(sketch, "E161.11.11.0", {"start": v(-37.3, -49.25) * mm, "end": v(-32.68, -49.25) * mm});
            skLineSegment(sketch, "E161.11.11.1", {"start": v(-37.3, -49.25) * mm, "end": v(-37.3, -53.87) * mm});
            skLineSegment(sketch, "E161.11.11.2", {"start": v(-37.3, -53.87) * mm, "end": v(-32.68, -53.87) * mm});
            skLineSegment(sketch, "E161.11.11.3", {"start": v(-32.68, -49.25) * mm, "end": v(-32.68, -53.87) * mm});
            skLineSegment(sketch, "E161.11.12.0", {"start": v(-37.3, -61.95) * mm, "end": v(-32.68, -61.95) * mm});
            skLineSegment(sketch, "E161.11.12.1", {"start": v(-37.3, -61.95) * mm, "end": v(-37.3, -66.57) * mm});
            skLineSegment(sketch, "E161.11.12.2", {"start": v(-37.3, -66.57) * mm, "end": v(-32.68, -66.57) * mm});
            skLineSegment(sketch, "E161.11.12.3", {"start": v(-32.68, -61.95) * mm, "end": v(-32.68, -66.57) * mm});
            skLineSegment(sketch, "E161.12.0.0", {"start": v(-24.6, 90.45) * mm, "end": v(-19.98, 90.45) * mm});
            skLineSegment(sketch, "E161.12.0.1", {"start": v(-24.6, 90.45) * mm, "end": v(-24.6, 85.83) * mm});
            skLineSegment(sketch, "E161.12.0.2", {"start": v(-24.6, 85.83) * mm, "end": v(-19.98, 85.83) * mm});
            skLineSegment(sketch, "E161.12.0.3", {"start": v(-19.98, 90.45) * mm, "end": v(-19.98, 85.83) * mm});
            skLineSegment(sketch, "E161.12.1.0", {"start": v(-24.6, 77.75) * mm, "end": v(-19.98, 77.75) * mm});
            skLineSegment(sketch, "E161.12.1.1", {"start": v(-24.6, 77.75) * mm, "end": v(-24.6, 73.13) * mm});
            skLineSegment(sketch, "E161.12.1.2", {"start": v(-24.6, 73.13) * mm, "end": v(-19.98, 73.13) * mm});
            skLineSegment(sketch, "E161.12.1.3", {"start": v(-19.98, 77.75) * mm, "end": v(-19.98, 73.13) * mm});
            skLineSegment(sketch, "E161.12.2.0", {"start": v(-24.6, 65.05) * mm, "end": v(-19.98, 65.05) * mm});
            skLineSegment(sketch, "E161.12.2.1", {"start": v(-24.6, 65.05) * mm, "end": v(-24.6, 60.43) * mm});
            skLineSegment(sketch, "E161.12.2.2", {"start": v(-24.6, 60.43) * mm, "end": v(-19.98, 60.43) * mm});
            skLineSegment(sketch, "E161.12.2.3", {"start": v(-19.98, 65.05) * mm, "end": v(-19.98, 60.43) * mm});
            skLineSegment(sketch, "E161.12.3.0", {"start": v(-24.6, 52.35) * mm, "end": v(-19.98, 52.35) * mm});
            skLineSegment(sketch, "E161.12.3.1", {"start": v(-24.6, 52.35) * mm, "end": v(-24.6, 47.73) * mm});
            skLineSegment(sketch, "E161.12.3.2", {"start": v(-24.6, 47.73) * mm, "end": v(-19.98, 47.73) * mm});
            skLineSegment(sketch, "E161.12.3.3", {"start": v(-19.98, 52.35) * mm, "end": v(-19.98, 47.73) * mm});
            skLineSegment(sketch, "E161.12.6.0", {"start": v(-24.6, 14.25) * mm, "end": v(-19.98, 14.25) * mm});
            skLineSegment(sketch, "E161.12.6.1", {"start": v(-24.6, 14.25) * mm, "end": v(-24.6, 9.63) * mm});
            skLineSegment(sketch, "E161.12.6.2", {"start": v(-24.6, 9.63) * mm, "end": v(-19.98, 9.63) * mm});
            skLineSegment(sketch, "E161.12.6.3", {"start": v(-19.98, 14.25) * mm, "end": v(-19.98, 9.63) * mm});
            skLineSegment(sketch, "E161.12.7.0", {"start": v(-24.6, 1.55) * mm, "end": v(-19.98, 1.55) * mm});
            skLineSegment(sketch, "E161.12.7.1", {"start": v(-24.6, 1.55) * mm, "end": v(-24.6, -3.07) * mm});
            skLineSegment(sketch, "E161.12.7.2", {"start": v(-24.6, -3.07) * mm, "end": v(-19.98, -3.07) * mm});
            skLineSegment(sketch, "E161.12.7.3", {"start": v(-19.98, 1.55) * mm, "end": v(-19.98, -3.07) * mm});
            skLineSegment(sketch, "E161.12.8.0", {"start": v(-24.6, -11.15) * mm, "end": v(-19.98, -11.15) * mm});
            skLineSegment(sketch, "E161.12.8.1", {"start": v(-24.6, -11.15) * mm, "end": v(-24.6, -15.77) * mm});
            skLineSegment(sketch, "E161.12.8.2", {"start": v(-24.6, -15.77) * mm, "end": v(-19.98, -15.77) * mm});
            skLineSegment(sketch, "E161.12.8.3", {"start": v(-19.98, -11.15) * mm, "end": v(-19.98, -15.77) * mm});
            skLineSegment(sketch, "E161.12.9.0", {"start": v(-24.6, -23.85) * mm, "end": v(-19.98, -23.85) * mm});
            skLineSegment(sketch, "E161.12.9.1", {"start": v(-24.6, -23.85) * mm, "end": v(-24.6, -28.47) * mm});
            skLineSegment(sketch, "E161.12.9.2", {"start": v(-24.6, -28.47) * mm, "end": v(-19.98, -28.47) * mm});
            skLineSegment(sketch, "E161.12.9.3", {"start": v(-19.98, -23.85) * mm, "end": v(-19.98, -28.47) * mm});
            skLineSegment(sketch, "E161.12.10.0", {"start": v(-24.6, -36.55) * mm, "end": v(-19.98, -36.55) * mm});
            skLineSegment(sketch, "E161.12.10.1", {"start": v(-24.6, -36.55) * mm, "end": v(-24.6, -41.17) * mm});
            skLineSegment(sketch, "E161.12.10.2", {"start": v(-24.6, -41.17) * mm, "end": v(-19.98, -41.17) * mm});
            skLineSegment(sketch, "E161.12.10.3", {"start": v(-19.98, -36.55) * mm, "end": v(-19.98, -41.17) * mm});
            skLineSegment(sketch, "E161.12.11.0", {"start": v(-24.6, -49.25) * mm, "end": v(-19.98, -49.25) * mm});
            skLineSegment(sketch, "E161.12.11.1", {"start": v(-24.6, -49.25) * mm, "end": v(-24.6, -53.87) * mm});
            skLineSegment(sketch, "E161.12.11.2", {"start": v(-24.6, -53.87) * mm, "end": v(-19.98, -53.87) * mm});
            skLineSegment(sketch, "E161.12.11.3", {"start": v(-19.98, -49.25) * mm, "end": v(-19.98, -53.87) * mm});
            skLineSegment(sketch, "E161.12.12.0", {"start": v(-24.6, -61.95) * mm, "end": v(-19.98, -61.95) * mm});
            skLineSegment(sketch, "E161.12.12.1", {"start": v(-24.6, -61.95) * mm, "end": v(-24.6, -66.57) * mm});
            skLineSegment(sketch, "E161.12.12.2", {"start": v(-24.6, -66.57) * mm, "end": v(-19.98, -66.57) * mm});
            skLineSegment(sketch, "E161.12.12.3", {"start": v(-19.98, -61.95) * mm, "end": v(-19.98, -66.57) * mm});
            skLineSegment(sketch, "E161.13.0.0", {"start": v(-11.9, 90.45) * mm, "end": v(-7.28, 90.45) * mm});
            skLineSegment(sketch, "E161.13.0.1", {"start": v(-11.9, 90.45) * mm, "end": v(-11.9, 85.83) * mm});
            skLineSegment(sketch, "E161.13.0.2", {"start": v(-11.9, 85.83) * mm, "end": v(-7.28, 85.83) * mm});
            skLineSegment(sketch, "E161.13.0.3", {"start": v(-7.28, 90.45) * mm, "end": v(-7.28, 85.83) * mm});
            skLineSegment(sketch, "E161.13.1.0", {"start": v(-11.9, 77.75) * mm, "end": v(-7.28, 77.75) * mm});
            skLineSegment(sketch, "E161.13.1.1", {"start": v(-11.9, 77.75) * mm, "end": v(-11.9, 73.13) * mm});
            skLineSegment(sketch, "E161.13.1.2", {"start": v(-11.9, 73.13) * mm, "end": v(-7.28, 73.13) * mm});
            skLineSegment(sketch, "E161.13.1.3", {"start": v(-7.28, 77.75) * mm, "end": v(-7.28, 73.13) * mm});
            skLineSegment(sketch, "E161.13.2.0", {"start": v(-11.9, 65.05) * mm, "end": v(-7.28, 65.05) * mm});
            skLineSegment(sketch, "E161.13.2.1", {"start": v(-11.9, 65.05) * mm, "end": v(-11.9, 60.43) * mm});
            skLineSegment(sketch, "E161.13.2.2", {"start": v(-11.9, 60.43) * mm, "end": v(-7.28, 60.43) * mm});
            skLineSegment(sketch, "E161.13.2.3", {"start": v(-7.28, 65.05) * mm, "end": v(-7.28, 60.43) * mm});
            skLineSegment(sketch, "E161.13.3.0", {"start": v(-11.9, 52.35) * mm, "end": v(-7.28, 52.35) * mm});
            skLineSegment(sketch, "E161.13.3.1", {"start": v(-11.9, 52.35) * mm, "end": v(-11.9, 47.73) * mm});
            skLineSegment(sketch, "E161.13.3.2", {"start": v(-11.9, 47.73) * mm, "end": v(-7.28, 47.73) * mm});
            skLineSegment(sketch, "E161.13.3.3", {"start": v(-7.28, 52.35) * mm, "end": v(-7.28, 47.73) * mm});
            skLineSegment(sketch, "E161.13.4.0", {"start": v(-11.9, 39.65) * mm, "end": v(-7.28, 39.65) * mm});
            skLineSegment(sketch, "E161.13.4.1", {"start": v(-11.9, 39.65) * mm, "end": v(-11.9, 35.03) * mm});
            skLineSegment(sketch, "E161.13.4.2", {"start": v(-11.9, 35.03) * mm, "end": v(-7.28, 35.03) * mm});
            skLineSegment(sketch, "E161.13.4.3", {"start": v(-7.28, 39.65) * mm, "end": v(-7.28, 35.03) * mm});
            skLineSegment(sketch, "E161.13.5.0", {"start": v(-11.9, 26.95) * mm, "end": v(-7.28, 26.95) * mm});
            skLineSegment(sketch, "E161.13.5.2", {"start": v(-11.9, 22.33) * mm, "end": v(-7.28, 22.33) * mm});
            skLineSegment(sketch, "E161.13.5.3", {"start": v(-7.28, 26.95) * mm, "end": v(-7.28, 22.33) * mm});
            skLineSegment(sketch, "E161.13.6.0", {"start": v(-11.9, 14.25) * mm, "end": v(-7.28, 14.25) * mm});
            skLineSegment(sketch, "E161.13.6.1", {"start": v(-11.9, 14.25) * mm, "end": v(-11.9, 9.63) * mm});
            skLineSegment(sketch, "E161.13.6.2", {"start": v(-11.9, 9.63) * mm, "end": v(-7.28, 9.63) * mm});
            skLineSegment(sketch, "E161.13.6.3", {"start": v(-7.28, 14.25) * mm, "end": v(-7.28, 9.63) * mm});
            skLineSegment(sketch, "E161.13.7.0", {"start": v(-11.9, 1.55) * mm, "end": v(-7.28, 1.55) * mm});
            skLineSegment(sketch, "E161.13.7.1", {"start": v(-11.9, 1.55) * mm, "end": v(-11.9, -3.07) * mm});
            skLineSegment(sketch, "E161.13.7.2", {"start": v(-11.9, -3.07) * mm, "end": v(-7.28, -3.07) * mm});
            skLineSegment(sketch, "E161.13.7.3", {"start": v(-7.28, 1.55) * mm, "end": v(-7.28, -3.07) * mm});
            skLineSegment(sketch, "E161.13.8.0", {"start": v(-11.9, -11.15) * mm, "end": v(-7.28, -11.15) * mm});
            skLineSegment(sketch, "E161.13.8.1", {"start": v(-11.9, -11.15) * mm, "end": v(-11.9, -15.77) * mm});
            skLineSegment(sketch, "E161.13.8.2", {"start": v(-11.9, -15.77) * mm, "end": v(-7.28, -15.77) * mm});
            skLineSegment(sketch, "E161.13.8.3", {"start": v(-7.28, -11.15) * mm, "end": v(-7.28, -15.77) * mm});
            skLineSegment(sketch, "E161.13.9.0", {"start": v(-11.9, -23.85) * mm, "end": v(-7.28, -23.85) * mm});
            skLineSegment(sketch, "E161.13.9.1", {"start": v(-11.9, -23.85) * mm, "end": v(-11.9, -28.47) * mm});
            skLineSegment(sketch, "E161.13.9.2", {"start": v(-11.9, -28.47) * mm, "end": v(-7.28, -28.47) * mm});
            skLineSegment(sketch, "E161.13.9.3", {"start": v(-7.28, -23.85) * mm, "end": v(-7.28, -28.47) * mm});
            skLineSegment(sketch, "E161.13.10.0", {"start": v(-11.9, -36.55) * mm, "end": v(-7.28, -36.55) * mm});
            skLineSegment(sketch, "E161.13.10.1", {"start": v(-11.9, -36.55) * mm, "end": v(-11.9, -41.17) * mm});
            skLineSegment(sketch, "E161.13.10.2", {"start": v(-11.9, -41.17) * mm, "end": v(-7.28, -41.17) * mm});
            skLineSegment(sketch, "E161.13.10.3", {"start": v(-7.28, -36.55) * mm, "end": v(-7.28, -41.17) * mm});
            skLineSegment(sketch, "E161.13.11.0", {"start": v(-11.9, -49.25) * mm, "end": v(-7.28, -49.25) * mm});
            skLineSegment(sketch, "E161.13.11.1", {"start": v(-11.9, -49.25) * mm, "end": v(-11.9, -53.87) * mm});
            skLineSegment(sketch, "E161.13.11.2", {"start": v(-11.9, -53.87) * mm, "end": v(-7.28, -53.87) * mm});
            skLineSegment(sketch, "E161.13.11.3", {"start": v(-7.28, -49.25) * mm, "end": v(-7.28, -53.87) * mm});
            skLineSegment(sketch, "E161.13.12.0", {"start": v(-11.9, -61.95) * mm, "end": v(-7.28, -61.95) * mm});
            skLineSegment(sketch, "E161.13.12.1", {"start": v(-11.9, -61.95) * mm, "end": v(-11.9, -66.57) * mm});
            skLineSegment(sketch, "E161.13.12.2", {"start": v(-11.9, -66.57) * mm, "end": v(-7.28, -66.57) * mm});
            skLineSegment(sketch, "E161.13.12.3", {"start": v(-7.28, -61.95) * mm, "end": v(-7.28, -66.57) * mm});
            skLineSegment(sketch, "E161.14.0.0", {"start": v(0.8, 90.45) * mm, "end": v(5.42, 90.45) * mm});
            skLineSegment(sketch, "E161.14.0.1", {"start": v(0.8, 90.45) * mm, "end": v(0.8, 85.83) * mm});
            skLineSegment(sketch, "E161.14.0.2", {"start": v(0.8, 85.83) * mm, "end": v(5.42, 85.83) * mm});
            skLineSegment(sketch, "E161.14.0.3", {"start": v(5.42, 90.45) * mm, "end": v(5.42, 85.83) * mm});
            skLineSegment(sketch, "E161.14.1.0", {"start": v(0.8, 77.75) * mm, "end": v(5.42, 77.75) * mm});
            skLineSegment(sketch, "E161.14.1.1", {"start": v(0.8, 77.75) * mm, "end": v(0.8, 73.13) * mm});
            skLineSegment(sketch, "E161.14.1.2", {"start": v(0.8, 73.13) * mm, "end": v(5.42, 73.13) * mm});
            skLineSegment(sketch, "E161.14.1.3", {"start": v(5.42, 77.75) * mm, "end": v(5.42, 73.13) * mm});
            skLineSegment(sketch, "E161.14.2.0", {"start": v(0.8, 65.05) * mm, "end": v(5.42, 65.05) * mm});
            skLineSegment(sketch, "E161.14.2.1", {"start": v(0.8, 65.05) * mm, "end": v(0.8, 60.43) * mm});
            skLineSegment(sketch, "E161.14.2.2", {"start": v(0.8, 60.43) * mm, "end": v(5.42, 60.43) * mm});
            skLineSegment(sketch, "E161.14.2.3", {"start": v(5.42, 65.05) * mm, "end": v(5.42, 60.43) * mm});
            skLineSegment(sketch, "E161.14.3.0", {"start": v(0.8, 52.35) * mm, "end": v(5.42, 52.35) * mm});
            skLineSegment(sketch, "E161.14.3.1", {"start": v(0.8, 52.35) * mm, "end": v(0.8, 47.73) * mm});
            skLineSegment(sketch, "E161.14.3.2", {"start": v(0.8, 47.73) * mm, "end": v(5.42, 47.73) * mm});
            skLineSegment(sketch, "E161.14.3.3", {"start": v(5.42, 52.35) * mm, "end": v(5.42, 47.73) * mm});
            skLineSegment(sketch, "E161.14.4.0", {"start": v(0.8, 39.65) * mm, "end": v(5.42, 39.65) * mm});
            skLineSegment(sketch, "E161.14.4.1", {"start": v(0.8, 39.65) * mm, "end": v(0.8, 35.03) * mm});
            skLineSegment(sketch, "E161.14.4.2", {"start": v(0.8, 35.03) * mm, "end": v(5.42, 35.03) * mm});
            skLineSegment(sketch, "E161.14.4.3", {"start": v(5.42, 39.65) * mm, "end": v(5.42, 35.03) * mm});
            skLineSegment(sketch, "E161.14.5.0", {"start": v(0.8, 26.95) * mm, "end": v(5.42, 26.95) * mm});
            skLineSegment(sketch, "E161.14.5.1", {"start": v(0.8, 26.95) * mm, "end": v(0.8, 22.33) * mm});
            skLineSegment(sketch, "E161.14.5.2", {"start": v(0.8, 22.33) * mm, "end": v(5.42, 22.33) * mm});
            skLineSegment(sketch, "E161.14.5.3", {"start": v(5.42, 26.95) * mm, "end": v(5.42, 22.33) * mm});
            skLineSegment(sketch, "E161.14.6.0", {"start": v(0.8, 14.25) * mm, "end": v(5.42, 14.25) * mm});
            skLineSegment(sketch, "E161.14.6.1", {"start": v(0.8, 14.25) * mm, "end": v(0.8, 9.63) * mm});
            skLineSegment(sketch, "E161.14.6.2", {"start": v(0.8, 9.63) * mm, "end": v(5.42, 9.63) * mm});
            skLineSegment(sketch, "E161.14.6.3", {"start": v(5.42, 14.25) * mm, "end": v(5.42, 9.63) * mm});
            skLineSegment(sketch, "E161.14.7.0", {"start": v(0.8, 1.55) * mm, "end": v(5.42, 1.55) * mm});
            skLineSegment(sketch, "E161.14.7.1", {"start": v(0.8, 1.55) * mm, "end": v(0.8, -3.07) * mm});
            skLineSegment(sketch, "E161.14.7.2", {"start": v(0.8, -3.07) * mm, "end": v(5.42, -3.07) * mm});
            skLineSegment(sketch, "E161.14.7.3", {"start": v(5.42, 1.55) * mm, "end": v(5.42, -3.07) * mm});
            skLineSegment(sketch, "E161.14.8.0", {"start": v(0.8, -11.15) * mm, "end": v(5.42, -11.15) * mm});
            skLineSegment(sketch, "E161.14.8.1", {"start": v(0.8, -11.15) * mm, "end": v(0.8, -15.77) * mm});
            skLineSegment(sketch, "E161.14.8.2", {"start": v(0.8, -15.77) * mm, "end": v(5.42, -15.77) * mm});
            skLineSegment(sketch, "E161.14.8.3", {"start": v(5.42, -11.15) * mm, "end": v(5.42, -15.77) * mm});
            skLineSegment(sketch, "E161.14.9.0", {"start": v(0.8, -23.85) * mm, "end": v(5.42, -23.85) * mm});
            skLineSegment(sketch, "E161.14.9.1", {"start": v(0.8, -23.85) * mm, "end": v(0.8, -28.47) * mm});
            skLineSegment(sketch, "E161.14.9.2", {"start": v(0.8, -28.47) * mm, "end": v(5.42, -28.47) * mm});
            skLineSegment(sketch, "E161.14.9.3", {"start": v(5.42, -23.85) * mm, "end": v(5.42, -28.47) * mm});
            skLineSegment(sketch, "E161.14.10.0", {"start": v(0.8, -36.55) * mm, "end": v(5.42, -36.55) * mm});
            skLineSegment(sketch, "E161.14.10.1", {"start": v(0.8, -36.55) * mm, "end": v(0.8, -41.17) * mm});
            skLineSegment(sketch, "E161.14.10.2", {"start": v(0.8, -41.17) * mm, "end": v(5.42, -41.17) * mm});
            skLineSegment(sketch, "E161.14.10.3", {"start": v(5.42, -36.55) * mm, "end": v(5.42, -41.17) * mm});
            skLineSegment(sketch, "E161.14.11.0", {"start": v(0.8, -49.25) * mm, "end": v(5.42, -49.25) * mm});
            skLineSegment(sketch, "E161.14.11.1", {"start": v(0.8, -49.25) * mm, "end": v(0.8, -53.87) * mm});
            skLineSegment(sketch, "E161.14.11.2", {"start": v(0.8, -53.87) * mm, "end": v(5.42, -53.87) * mm});
            skLineSegment(sketch, "E161.14.11.3", {"start": v(5.42, -49.25) * mm, "end": v(5.42, -53.87) * mm});
            skLineSegment(sketch, "E161.14.12.0", {"start": v(0.8, -61.95) * mm, "end": v(5.42, -61.95) * mm});
            skLineSegment(sketch, "E161.14.12.1", {"start": v(0.8, -61.95) * mm, "end": v(0.8, -66.57) * mm});
            skLineSegment(sketch, "E161.14.12.2", {"start": v(0.8, -66.57) * mm, "end": v(5.42, -66.57) * mm});
            skLineSegment(sketch, "E161.14.12.3", {"start": v(5.42, -61.95) * mm, "end": v(5.42, -66.57) * mm});
            skLineSegment(sketch, "E161.15.0.0", {"start": v(13.5, 90.45) * mm, "end": v(18.12, 90.45) * mm});
            skLineSegment(sketch, "E161.15.0.1", {"start": v(13.5, 90.45) * mm, "end": v(13.5, 85.83) * mm});
            skLineSegment(sketch, "E161.15.0.2", {"start": v(13.5, 85.83) * mm, "end": v(18.12, 85.83) * mm});
            skLineSegment(sketch, "E161.15.0.3", {"start": v(18.12, 90.45) * mm, "end": v(18.12, 85.83) * mm});
            skLineSegment(sketch, "E161.15.1.0", {"start": v(13.5, 77.75) * mm, "end": v(18.12, 77.75) * mm});
            skLineSegment(sketch, "E161.15.1.1", {"start": v(13.5, 77.75) * mm, "end": v(13.5, 73.13) * mm});
            skLineSegment(sketch, "E161.15.1.2", {"start": v(13.5, 73.13) * mm, "end": v(18.12, 73.13) * mm});
            skLineSegment(sketch, "E161.15.1.3", {"start": v(18.12, 77.75) * mm, "end": v(18.12, 73.13) * mm});
            skLineSegment(sketch, "E161.15.2.0", {"start": v(13.5, 65.05) * mm, "end": v(18.12, 65.05) * mm});
            skLineSegment(sketch, "E161.15.2.1", {"start": v(13.5, 65.05) * mm, "end": v(13.5, 60.43) * mm});
            skLineSegment(sketch, "E161.15.2.2", {"start": v(13.5, 60.43) * mm, "end": v(18.12, 60.43) * mm});
            skLineSegment(sketch, "E161.15.2.3", {"start": v(18.12, 65.05) * mm, "end": v(18.12, 60.43) * mm});
            skLineSegment(sketch, "E161.15.3.0", {"start": v(13.5, 52.35) * mm, "end": v(18.12, 52.35) * mm});
            skLineSegment(sketch, "E161.15.3.1", {"start": v(13.5, 52.35) * mm, "end": v(13.5, 47.73) * mm});
            skLineSegment(sketch, "E161.15.3.2", {"start": v(13.5, 47.73) * mm, "end": v(18.12, 47.73) * mm});
            skLineSegment(sketch, "E161.15.3.3", {"start": v(18.12, 52.35) * mm, "end": v(18.12, 47.73) * mm});
            skLineSegment(sketch, "E161.15.4.0", {"start": v(13.5, 39.65) * mm, "end": v(18.12, 39.65) * mm});
            skLineSegment(sketch, "E161.15.4.1", {"start": v(13.5, 39.65) * mm, "end": v(13.5, 35.03) * mm});
            skLineSegment(sketch, "E161.15.4.2", {"start": v(13.5, 35.03) * mm, "end": v(18.12, 35.03) * mm});
            skLineSegment(sketch, "E161.15.4.3", {"start": v(18.12, 39.65) * mm, "end": v(18.12, 35.03) * mm});
            skLineSegment(sketch, "E161.15.5.0", {"start": v(13.5, 26.95) * mm, "end": v(18.12, 26.95) * mm});
            skLineSegment(sketch, "E161.15.5.1", {"start": v(13.5, 26.95) * mm, "end": v(13.5, 22.33) * mm});
            skLineSegment(sketch, "E161.15.5.2", {"start": v(13.5, 22.33) * mm, "end": v(18.12, 22.33) * mm});
            skLineSegment(sketch, "E161.15.5.3", {"start": v(18.12, 26.95) * mm, "end": v(18.12, 22.33) * mm});
            skLineSegment(sketch, "E161.15.6.0", {"start": v(13.5, 14.25) * mm, "end": v(18.12, 14.25) * mm});
            skLineSegment(sketch, "E161.15.6.1", {"start": v(13.5, 14.25) * mm, "end": v(13.5, 9.63) * mm});
            skLineSegment(sketch, "E161.15.6.2", {"start": v(13.5, 9.63) * mm, "end": v(18.12, 9.63) * mm});
            skLineSegment(sketch, "E161.15.6.3", {"start": v(18.12, 14.25) * mm, "end": v(18.12, 9.63) * mm});
            skLineSegment(sketch, "E161.15.7.0", {"start": v(13.5, 1.55) * mm, "end": v(18.12, 1.55) * mm});
            skLineSegment(sketch, "E161.15.7.1", {"start": v(13.5, 1.55) * mm, "end": v(13.5, -3.07) * mm});
            skLineSegment(sketch, "E161.15.7.2", {"start": v(13.5, -3.07) * mm, "end": v(18.12, -3.07) * mm});
            skLineSegment(sketch, "E161.15.7.3", {"start": v(18.12, 1.55) * mm, "end": v(18.12, -3.07) * mm});
            skLineSegment(sketch, "E161.15.8.0", {"start": v(13.5, -11.15) * mm, "end": v(18.12, -11.15) * mm});
            skLineSegment(sketch, "E161.15.8.1", {"start": v(13.5, -11.15) * mm, "end": v(13.5, -15.77) * mm});
            skLineSegment(sketch, "E161.15.8.2", {"start": v(13.5, -15.77) * mm, "end": v(18.12, -15.77) * mm});
            skLineSegment(sketch, "E161.15.8.3", {"start": v(18.12, -11.15) * mm, "end": v(18.12, -15.77) * mm});
            skLineSegment(sketch, "E161.15.9.0", {"start": v(13.5, -23.85) * mm, "end": v(18.12, -23.85) * mm});
            skLineSegment(sketch, "E161.15.9.1", {"start": v(13.5, -23.85) * mm, "end": v(13.5, -28.47) * mm});
            skLineSegment(sketch, "E161.15.9.2", {"start": v(13.5, -28.47) * mm, "end": v(18.12, -28.47) * mm});
            skLineSegment(sketch, "E161.15.9.3", {"start": v(18.12, -23.85) * mm, "end": v(18.12, -28.47) * mm});
            skLineSegment(sketch, "E161.15.10.0", {"start": v(13.5, -36.55) * mm, "end": v(18.12, -36.55) * mm});
            skLineSegment(sketch, "E161.15.10.1", {"start": v(13.5, -36.55) * mm, "end": v(13.5, -41.17) * mm});
            skLineSegment(sketch, "E161.15.10.2", {"start": v(13.5, -41.17) * mm, "end": v(18.12, -41.17) * mm});
            skLineSegment(sketch, "E161.15.10.3", {"start": v(18.12, -36.55) * mm, "end": v(18.12, -41.17) * mm});
            skLineSegment(sketch, "E161.15.11.0", {"start": v(13.5, -49.25) * mm, "end": v(18.12, -49.25) * mm});
            skLineSegment(sketch, "E161.15.11.1", {"start": v(13.5, -49.25) * mm, "end": v(13.5, -53.87) * mm});
            skLineSegment(sketch, "E161.15.11.2", {"start": v(13.5, -53.87) * mm, "end": v(18.12, -53.87) * mm});
            skLineSegment(sketch, "E161.15.11.3", {"start": v(18.12, -49.25) * mm, "end": v(18.12, -53.87) * mm});
            skLineSegment(sketch, "E161.15.12.0", {"start": v(13.5, -61.95) * mm, "end": v(18.12, -61.95) * mm});
            skLineSegment(sketch, "E161.15.12.1", {"start": v(13.5, -61.95) * mm, "end": v(13.5, -66.57) * mm});
            skLineSegment(sketch, "E161.15.12.2", {"start": v(13.5, -66.57) * mm, "end": v(18.12, -66.57) * mm});
            skLineSegment(sketch, "E161.15.12.3", {"start": v(18.12, -61.95) * mm, "end": v(18.12, -66.57) * mm});
            skLineSegment(sketch, "E161.16.0.0", {"start": v(26.2, 90.45) * mm, "end": v(30.82, 90.45) * mm});
            skLineSegment(sketch, "E161.16.0.1", {"start": v(26.2, 90.45) * mm, "end": v(26.2, 85.83) * mm});
            skLineSegment(sketch, "E161.16.0.2", {"start": v(26.2, 85.83) * mm, "end": v(30.82, 85.83) * mm});
            skLineSegment(sketch, "E161.16.0.3", {"start": v(30.82, 90.45) * mm, "end": v(30.82, 85.83) * mm});
            skLineSegment(sketch, "E161.16.1.0", {"start": v(26.2, 77.75) * mm, "end": v(30.82, 77.75) * mm});
            skLineSegment(sketch, "E161.16.1.1", {"start": v(26.2, 77.75) * mm, "end": v(26.2, 73.13) * mm});
            skLineSegment(sketch, "E161.16.1.2", {"start": v(26.2, 73.13) * mm, "end": v(30.82, 73.13) * mm});
            skLineSegment(sketch, "E161.16.1.3", {"start": v(30.82, 77.75) * mm, "end": v(30.82, 73.13) * mm});
            skLineSegment(sketch, "E161.16.2.0", {"start": v(26.2, 65.05) * mm, "end": v(30.82, 65.05) * mm});
            skLineSegment(sketch, "E161.16.2.1", {"start": v(26.2, 65.05) * mm, "end": v(26.2, 60.43) * mm});
            skLineSegment(sketch, "E161.16.2.2", {"start": v(26.2, 60.43) * mm, "end": v(30.82, 60.43) * mm});
            skLineSegment(sketch, "E161.16.2.3", {"start": v(30.82, 65.05) * mm, "end": v(30.82, 60.43) * mm});
            skLineSegment(sketch, "E161.16.3.0", {"start": v(26.2, 52.35) * mm, "end": v(30.82, 52.35) * mm});
            skLineSegment(sketch, "E161.16.3.1", {"start": v(26.2, 52.35) * mm, "end": v(26.2, 47.73) * mm});
            skLineSegment(sketch, "E161.16.3.2", {"start": v(26.2, 47.73) * mm, "end": v(30.82, 47.73) * mm});
            skLineSegment(sketch, "E161.16.3.3", {"start": v(30.82, 52.35) * mm, "end": v(30.82, 47.73) * mm});
            skLineSegment(sketch, "E161.16.4.0", {"start": v(26.2, 39.65) * mm, "end": v(30.82, 39.65) * mm});
            skLineSegment(sketch, "E161.16.4.1", {"start": v(26.2, 39.65) * mm, "end": v(26.2, 35.03) * mm});
            skLineSegment(sketch, "E161.16.4.2", {"start": v(26.2, 35.03) * mm, "end": v(30.82, 35.03) * mm});
            skLineSegment(sketch, "E161.16.4.3", {"start": v(30.82, 39.65) * mm, "end": v(30.82, 35.03) * mm});
            skLineSegment(sketch, "E161.16.5.0", {"start": v(26.2, 26.95) * mm, "end": v(30.82, 26.95) * mm});
            skLineSegment(sketch, "E161.16.5.1", {"start": v(26.2, 26.95) * mm, "end": v(26.2, 22.33) * mm});
            skLineSegment(sketch, "E161.16.5.2", {"start": v(26.2, 22.33) * mm, "end": v(30.82, 22.33) * mm});
            skLineSegment(sketch, "E161.16.5.3", {"start": v(30.82, 26.95) * mm, "end": v(30.82, 22.33) * mm});
            skLineSegment(sketch, "E161.16.6.0", {"start": v(26.2, 14.25) * mm, "end": v(30.82, 14.25) * mm});
            skLineSegment(sketch, "E161.16.6.1", {"start": v(26.2, 14.25) * mm, "end": v(26.2, 9.63) * mm});
            skLineSegment(sketch, "E161.16.6.2", {"start": v(26.2, 9.63) * mm, "end": v(30.82, 9.63) * mm});
            skLineSegment(sketch, "E161.16.6.3", {"start": v(30.82, 14.25) * mm, "end": v(30.82, 9.63) * mm});
            skLineSegment(sketch, "E161.16.7.0", {"start": v(26.2, 1.55) * mm, "end": v(30.82, 1.55) * mm});
            skLineSegment(sketch, "E161.16.7.1", {"start": v(26.2, 1.55) * mm, "end": v(26.2, -3.07) * mm});
            skLineSegment(sketch, "E161.16.7.2", {"start": v(26.2, -3.07) * mm, "end": v(30.82, -3.07) * mm});
            skLineSegment(sketch, "E161.16.7.3", {"start": v(30.82, 1.55) * mm, "end": v(30.82, -3.07) * mm});
            skLineSegment(sketch, "E161.16.8.0", {"start": v(26.2, -11.15) * mm, "end": v(30.82, -11.15) * mm});
            skLineSegment(sketch, "E161.16.8.1", {"start": v(26.2, -11.15) * mm, "end": v(26.2, -15.77) * mm});
            skLineSegment(sketch, "E161.16.8.2", {"start": v(26.2, -15.77) * mm, "end": v(30.82, -15.77) * mm});
            skLineSegment(sketch, "E161.16.8.3", {"start": v(30.82, -11.15) * mm, "end": v(30.82, -15.77) * mm});
            skLineSegment(sketch, "E161.16.9.0", {"start": v(26.2, -23.85) * mm, "end": v(30.82, -23.85) * mm});
            skLineSegment(sketch, "E161.16.9.1", {"start": v(26.2, -23.85) * mm, "end": v(26.2, -28.47) * mm});
            skLineSegment(sketch, "E161.16.9.2", {"start": v(26.2, -28.47) * mm, "end": v(30.82, -28.47) * mm});
            skLineSegment(sketch, "E161.16.9.3", {"start": v(30.82, -23.85) * mm, "end": v(30.82, -28.47) * mm});
            skLineSegment(sketch, "E161.16.10.0", {"start": v(26.2, -36.55) * mm, "end": v(30.82, -36.55) * mm});
            skLineSegment(sketch, "E161.16.10.1", {"start": v(26.2, -36.55) * mm, "end": v(26.2, -41.17) * mm});
            skLineSegment(sketch, "E161.16.10.2", {"start": v(26.2, -41.17) * mm, "end": v(30.82, -41.17) * mm});
            skLineSegment(sketch, "E161.16.10.3", {"start": v(30.82, -36.55) * mm, "end": v(30.82, -41.17) * mm});
            skLineSegment(sketch, "E161.16.11.0", {"start": v(26.2, -49.25) * mm, "end": v(30.82, -49.25) * mm});
            skLineSegment(sketch, "E161.16.11.1", {"start": v(26.2, -49.25) * mm, "end": v(26.2, -53.87) * mm});
            skLineSegment(sketch, "E161.16.11.2", {"start": v(26.2, -53.87) * mm, "end": v(30.82, -53.87) * mm});
            skLineSegment(sketch, "E161.16.11.3", {"start": v(30.82, -49.25) * mm, "end": v(30.82, -53.87) * mm});
            skLineSegment(sketch, "E161.16.12.0", {"start": v(26.2, -61.95) * mm, "end": v(30.82, -61.95) * mm});
            skLineSegment(sketch, "E161.16.12.1", {"start": v(26.2, -61.95) * mm, "end": v(26.2, -66.57) * mm});
            skLineSegment(sketch, "E161.16.12.2", {"start": v(26.2, -66.57) * mm, "end": v(30.82, -66.57) * mm});
            skLineSegment(sketch, "E161.16.12.3", {"start": v(30.82, -61.95) * mm, "end": v(30.82, -66.57) * mm});
            skLineSegment(sketch, "E161.17.0.0", {"start": v(38.9, 90.45) * mm, "end": v(43.52, 90.45) * mm});
            skLineSegment(sketch, "E161.17.0.1", {"start": v(38.9, 90.45) * mm, "end": v(38.9, 85.83) * mm});
            skLineSegment(sketch, "E161.17.0.2", {"start": v(38.9, 85.83) * mm, "end": v(43.52, 85.83) * mm});
            skLineSegment(sketch, "E161.17.0.3", {"start": v(43.52, 90.45) * mm, "end": v(43.52, 85.83) * mm});
            skLineSegment(sketch, "E161.17.1.0", {"start": v(38.9, 77.75) * mm, "end": v(43.52, 77.75) * mm});
            skLineSegment(sketch, "E161.17.1.1", {"start": v(38.9, 77.75) * mm, "end": v(38.9, 73.13) * mm});
            skLineSegment(sketch, "E161.17.1.2", {"start": v(38.9, 73.13) * mm, "end": v(43.52, 73.13) * mm});
            skLineSegment(sketch, "E161.17.1.3", {"start": v(43.52, 77.75) * mm, "end": v(43.52, 73.13) * mm});
            skLineSegment(sketch, "E161.17.2.0", {"start": v(38.9, 65.05) * mm, "end": v(43.52, 65.05) * mm});
            skLineSegment(sketch, "E161.17.2.1", {"start": v(38.9, 65.05) * mm, "end": v(38.9, 60.43) * mm});
            skLineSegment(sketch, "E161.17.2.2", {"start": v(38.9, 60.43) * mm, "end": v(43.52, 60.43) * mm});
            skLineSegment(sketch, "E161.17.2.3", {"start": v(43.52, 65.05) * mm, "end": v(43.52, 60.43) * mm});
            skLineSegment(sketch, "E161.17.3.0", {"start": v(38.9, 52.35) * mm, "end": v(43.52, 52.35) * mm});
            skLineSegment(sketch, "E161.17.3.1", {"start": v(38.9, 52.35) * mm, "end": v(38.9, 47.73) * mm});
            skLineSegment(sketch, "E161.17.3.2", {"start": v(38.9, 47.73) * mm, "end": v(43.52, 47.73) * mm});
            skLineSegment(sketch, "E161.17.3.3", {"start": v(43.52, 52.35) * mm, "end": v(43.52, 47.73) * mm});
            skLineSegment(sketch, "E161.17.4.0", {"start": v(38.9, 39.65) * mm, "end": v(43.52, 39.65) * mm});
            skLineSegment(sketch, "E161.17.4.1", {"start": v(38.9, 39.65) * mm, "end": v(38.9, 35.03) * mm});
            skLineSegment(sketch, "E161.17.4.2", {"start": v(38.9, 35.03) * mm, "end": v(43.52, 35.03) * mm});
            skLineSegment(sketch, "E161.17.4.3", {"start": v(43.52, 39.65) * mm, "end": v(43.52, 35.03) * mm});
            skLineSegment(sketch, "E161.17.5.0", {"start": v(38.9, 26.95) * mm, "end": v(43.52, 26.95) * mm});
            skLineSegment(sketch, "E161.17.5.1", {"start": v(38.9, 26.95) * mm, "end": v(38.9, 22.33) * mm});
            skLineSegment(sketch, "E161.17.5.2", {"start": v(38.9, 22.33) * mm, "end": v(43.52, 22.33) * mm});
            skLineSegment(sketch, "E161.17.5.3", {"start": v(43.52, 26.95) * mm, "end": v(43.52, 22.33) * mm});
            skLineSegment(sketch, "E161.17.6.0", {"start": v(38.9, 14.25) * mm, "end": v(43.52, 14.25) * mm});
            skLineSegment(sketch, "E161.17.6.1", {"start": v(38.9, 14.25) * mm, "end": v(38.9, 9.63) * mm});
            skLineSegment(sketch, "E161.17.6.2", {"start": v(38.9, 9.63) * mm, "end": v(43.52, 9.63) * mm});
            skLineSegment(sketch, "E161.17.6.3", {"start": v(43.52, 14.25) * mm, "end": v(43.52, 9.63) * mm});
            skLineSegment(sketch, "E161.17.7.0", {"start": v(38.9, 1.55) * mm, "end": v(43.52, 1.55) * mm});
            skLineSegment(sketch, "E161.17.7.1", {"start": v(38.9, 1.55) * mm, "end": v(38.9, -3.07) * mm});
            skLineSegment(sketch, "E161.17.7.2", {"start": v(38.9, -3.07) * mm, "end": v(43.52, -3.07) * mm});
            skLineSegment(sketch, "E161.17.7.3", {"start": v(43.52, 1.55) * mm, "end": v(43.52, -3.07) * mm});
            skLineSegment(sketch, "E161.17.8.0", {"start": v(38.9, -11.15) * mm, "end": v(43.52, -11.15) * mm});
            skLineSegment(sketch, "E161.17.8.1", {"start": v(38.9, -11.15) * mm, "end": v(38.9, -15.77) * mm});
            skLineSegment(sketch, "E161.17.8.2", {"start": v(38.9, -15.77) * mm, "end": v(43.52, -15.77) * mm});
            skLineSegment(sketch, "E161.17.8.3", {"start": v(43.52, -11.15) * mm, "end": v(43.52, -15.77) * mm});
            skLineSegment(sketch, "E161.17.9.0", {"start": v(38.9, -23.85) * mm, "end": v(43.52, -23.85) * mm});
            skLineSegment(sketch, "E161.17.9.1", {"start": v(38.9, -23.85) * mm, "end": v(38.9, -28.47) * mm});
            skLineSegment(sketch, "E161.17.9.2", {"start": v(38.9, -28.47) * mm, "end": v(43.52, -28.47) * mm});
            skLineSegment(sketch, "E161.17.9.3", {"start": v(43.52, -23.85) * mm, "end": v(43.52, -28.47) * mm});
            skLineSegment(sketch, "E161.17.10.0", {"start": v(38.9, -36.55) * mm, "end": v(43.52, -36.55) * mm});
            skLineSegment(sketch, "E161.17.10.1", {"start": v(38.9, -36.55) * mm, "end": v(38.9, -41.17) * mm});
            skLineSegment(sketch, "E161.17.10.2", {"start": v(38.9, -41.17) * mm, "end": v(43.52, -41.17) * mm});
            skLineSegment(sketch, "E161.17.10.3", {"start": v(43.52, -36.55) * mm, "end": v(43.52, -41.17) * mm});
            skLineSegment(sketch, "E161.17.11.0", {"start": v(38.9, -49.25) * mm, "end": v(43.52, -49.25) * mm});
            skLineSegment(sketch, "E161.17.11.1", {"start": v(38.9, -49.25) * mm, "end": v(38.9, -53.87) * mm});
            skLineSegment(sketch, "E161.17.11.2", {"start": v(38.9, -53.87) * mm, "end": v(43.52, -53.87) * mm});
            skLineSegment(sketch, "E161.17.11.3", {"start": v(43.52, -49.25) * mm, "end": v(43.52, -53.87) * mm});
            skLineSegment(sketch, "E161.17.12.0", {"start": v(38.9, -61.95) * mm, "end": v(43.52, -61.95) * mm});
            skLineSegment(sketch, "E161.17.12.1", {"start": v(38.9, -61.95) * mm, "end": v(38.9, -66.57) * mm});
            skLineSegment(sketch, "E161.17.12.2", {"start": v(38.9, -66.57) * mm, "end": v(43.52, -66.57) * mm});
            skLineSegment(sketch, "E161.17.12.3", {"start": v(43.52, -61.95) * mm, "end": v(43.52, -66.57) * mm});
            skLineSegment(sketch, "E161.18.0.0", {"start": v(51.6, 90.45) * mm, "end": v(56.22, 90.45) * mm});
            skLineSegment(sketch, "E161.18.0.1", {"start": v(51.6, 90.45) * mm, "end": v(51.6, 85.83) * mm});
            skLineSegment(sketch, "E161.18.0.2", {"start": v(51.6, 85.83) * mm, "end": v(56.22, 85.83) * mm});
            skLineSegment(sketch, "E161.18.0.3", {"start": v(56.22, 90.45) * mm, "end": v(56.22, 85.83) * mm});
            skLineSegment(sketch, "E161.18.1.0", {"start": v(51.6, 77.75) * mm, "end": v(56.22, 77.75) * mm});
            skLineSegment(sketch, "E161.18.1.1", {"start": v(51.6, 77.75) * mm, "end": v(51.6, 73.13) * mm});
            skLineSegment(sketch, "E161.18.1.2", {"start": v(51.6, 73.13) * mm, "end": v(56.22, 73.13) * mm});
            skLineSegment(sketch, "E161.18.1.3", {"start": v(56.22, 77.75) * mm, "end": v(56.22, 73.13) * mm});
            skLineSegment(sketch, "E161.18.2.0", {"start": v(51.6, 65.05) * mm, "end": v(56.22, 65.05) * mm});
            skLineSegment(sketch, "E161.18.2.1", {"start": v(51.6, 65.05) * mm, "end": v(51.6, 60.43) * mm});
            skLineSegment(sketch, "E161.18.2.2", {"start": v(51.6, 60.43) * mm, "end": v(56.22, 60.43) * mm});
            skLineSegment(sketch, "E161.18.2.3", {"start": v(56.22, 65.05) * mm, "end": v(56.22, 60.43) * mm});
            skLineSegment(sketch, "E161.18.3.0", {"start": v(51.6, 52.35) * mm, "end": v(56.22, 52.35) * mm});
            skLineSegment(sketch, "E161.18.3.1", {"start": v(51.6, 52.35) * mm, "end": v(51.6, 47.73) * mm});
            skLineSegment(sketch, "E161.18.3.2", {"start": v(51.6, 47.73) * mm, "end": v(56.22, 47.73) * mm});
            skLineSegment(sketch, "E161.18.3.3", {"start": v(56.22, 52.35) * mm, "end": v(56.22, 47.73) * mm});
            skLineSegment(sketch, "E161.18.4.0", {"start": v(51.6, 39.65) * mm, "end": v(56.22, 39.65) * mm});
            skLineSegment(sketch, "E161.18.4.1", {"start": v(51.6, 39.65) * mm, "end": v(51.6, 35.03) * mm});
            skLineSegment(sketch, "E161.18.4.2", {"start": v(51.6, 35.03) * mm, "end": v(56.22, 35.03) * mm});
            skLineSegment(sketch, "E161.18.4.3", {"start": v(56.22, 39.65) * mm, "end": v(56.22, 35.03) * mm});
            skLineSegment(sketch, "E161.18.5.0", {"start": v(51.6, 26.95) * mm, "end": v(56.22, 26.95) * mm});
            skLineSegment(sketch, "E161.18.5.1", {"start": v(51.6, 26.95) * mm, "end": v(51.6, 22.33) * mm});
            skLineSegment(sketch, "E161.18.5.2", {"start": v(51.6, 22.33) * mm, "end": v(56.22, 22.33) * mm});
            skLineSegment(sketch, "E161.18.5.3", {"start": v(56.22, 26.95) * mm, "end": v(56.22, 22.33) * mm});
            skLineSegment(sketch, "E161.18.6.0", {"start": v(51.6, 14.25) * mm, "end": v(56.22, 14.25) * mm});
            skLineSegment(sketch, "E161.18.6.1", {"start": v(51.6, 14.25) * mm, "end": v(51.6, 9.63) * mm});
            skLineSegment(sketch, "E161.18.6.2", {"start": v(51.6, 9.63) * mm, "end": v(56.22, 9.63) * mm});
            skLineSegment(sketch, "E161.18.6.3", {"start": v(56.22, 14.25) * mm, "end": v(56.22, 9.63) * mm});
            skLineSegment(sketch, "E161.18.7.0", {"start": v(51.6, 1.55) * mm, "end": v(56.22, 1.55) * mm});
            skLineSegment(sketch, "E161.18.7.1", {"start": v(51.6, 1.55) * mm, "end": v(51.6, -3.07) * mm});
            skLineSegment(sketch, "E161.18.7.2", {"start": v(51.6, -3.07) * mm, "end": v(56.22, -3.07) * mm});
            skLineSegment(sketch, "E161.18.7.3", {"start": v(56.22, 1.55) * mm, "end": v(56.22, -3.07) * mm});
            skLineSegment(sketch, "E161.18.8.0", {"start": v(51.6, -11.15) * mm, "end": v(56.22, -11.15) * mm});
            skLineSegment(sketch, "E161.18.8.1", {"start": v(51.6, -11.15) * mm, "end": v(51.6, -15.77) * mm});
            skLineSegment(sketch, "E161.18.8.2", {"start": v(51.6, -15.77) * mm, "end": v(56.22, -15.77) * mm});
            skLineSegment(sketch, "E161.18.8.3", {"start": v(56.22, -11.15) * mm, "end": v(56.22, -15.77) * mm});
            skLineSegment(sketch, "E161.18.9.0", {"start": v(51.6, -23.85) * mm, "end": v(56.22, -23.85) * mm});
            skLineSegment(sketch, "E161.18.9.1", {"start": v(51.6, -23.85) * mm, "end": v(51.6, -28.47) * mm});
            skLineSegment(sketch, "E161.18.9.2", {"start": v(51.6, -28.47) * mm, "end": v(56.22, -28.47) * mm});
            skLineSegment(sketch, "E161.18.9.3", {"start": v(56.22, -23.85) * mm, "end": v(56.22, -28.47) * mm});
            skLineSegment(sketch, "E161.18.10.0", {"start": v(51.6, -36.55) * mm, "end": v(56.22, -36.55) * mm});
            skLineSegment(sketch, "E161.18.10.1", {"start": v(51.6, -36.55) * mm, "end": v(51.6, -41.17) * mm});
            skLineSegment(sketch, "E161.18.10.2", {"start": v(51.6, -41.17) * mm, "end": v(56.22, -41.17) * mm});
            skLineSegment(sketch, "E161.18.10.3", {"start": v(56.22, -36.55) * mm, "end": v(56.22, -41.17) * mm});
            skLineSegment(sketch, "E161.18.11.0", {"start": v(51.6, -49.25) * mm, "end": v(56.22, -49.25) * mm});
            skLineSegment(sketch, "E161.18.11.1", {"start": v(51.6, -49.25) * mm, "end": v(51.6, -53.87) * mm});
            skLineSegment(sketch, "E161.18.11.2", {"start": v(51.6, -53.87) * mm, "end": v(56.22, -53.87) * mm});
            skLineSegment(sketch, "E161.18.11.3", {"start": v(56.22, -49.25) * mm, "end": v(56.22, -53.87) * mm});
            skLineSegment(sketch, "E161.18.12.0", {"start": v(51.6, -61.95) * mm, "end": v(56.22, -61.95) * mm});
            skLineSegment(sketch, "E161.18.12.1", {"start": v(51.6, -61.95) * mm, "end": v(51.6, -66.57) * mm});
            skLineSegment(sketch, "E161.18.12.2", {"start": v(51.6, -66.57) * mm, "end": v(56.22, -66.57) * mm});
            skLineSegment(sketch, "E161.18.12.3", {"start": v(56.22, -61.95) * mm, "end": v(56.22, -66.57) * mm});
            skLineSegment(sketch, "E161.19.0.0", {"start": v(64.3, 90.45) * mm, "end": v(68.92, 90.45) * mm});
            skLineSegment(sketch, "E161.19.0.1", {"start": v(64.3, 90.45) * mm, "end": v(64.3, 85.83) * mm});
            skLineSegment(sketch, "E161.19.0.2", {"start": v(64.3, 85.83) * mm, "end": v(68.92, 85.83) * mm});
            skLineSegment(sketch, "E161.19.0.3", {"start": v(68.92, 90.45) * mm, "end": v(68.92, 85.83) * mm});
            skLineSegment(sketch, "E161.19.1.0", {"start": v(64.3, 77.75) * mm, "end": v(68.92, 77.75) * mm});
            skLineSegment(sketch, "E161.19.1.1", {"start": v(64.3, 77.75) * mm, "end": v(64.3, 73.13) * mm});
            skLineSegment(sketch, "E161.19.1.2", {"start": v(64.3, 73.13) * mm, "end": v(68.92, 73.13) * mm});
            skLineSegment(sketch, "E161.19.1.3", {"start": v(68.92, 77.75) * mm, "end": v(68.92, 73.13) * mm});
            skLineSegment(sketch, "E161.19.2.0", {"start": v(64.3, 65.05) * mm, "end": v(68.92, 65.05) * mm});
            skLineSegment(sketch, "E161.19.2.1", {"start": v(64.3, 65.05) * mm, "end": v(64.3, 60.43) * mm});
            skLineSegment(sketch, "E161.19.2.2", {"start": v(64.3, 60.43) * mm, "end": v(68.92, 60.43) * mm});
            skLineSegment(sketch, "E161.19.2.3", {"start": v(68.92, 65.05) * mm, "end": v(68.92, 60.43) * mm});
            skLineSegment(sketch, "E161.19.3.0", {"start": v(64.3, 52.35) * mm, "end": v(68.92, 52.35) * mm});
            skLineSegment(sketch, "E161.19.3.1", {"start": v(64.3, 52.35) * mm, "end": v(64.3, 47.73) * mm});
            skLineSegment(sketch, "E161.19.3.2", {"start": v(64.3, 47.73) * mm, "end": v(68.92, 47.73) * mm});
            skLineSegment(sketch, "E161.19.3.3", {"start": v(68.92, 52.35) * mm, "end": v(68.92, 47.73) * mm});
            skLineSegment(sketch, "E161.19.4.0", {"start": v(64.3, 39.65) * mm, "end": v(68.92, 39.65) * mm});
            skLineSegment(sketch, "E161.19.4.1", {"start": v(64.3, 39.65) * mm, "end": v(64.3, 35.03) * mm});
            skLineSegment(sketch, "E161.19.4.2", {"start": v(64.3, 35.03) * mm, "end": v(68.92, 35.03) * mm});
            skLineSegment(sketch, "E161.19.4.3", {"start": v(68.92, 39.65) * mm, "end": v(68.92, 35.03) * mm});
            skLineSegment(sketch, "E161.19.5.0", {"start": v(64.3, 26.95) * mm, "end": v(68.92, 26.95) * mm});
            skLineSegment(sketch, "E161.19.5.1", {"start": v(64.3, 26.95) * mm, "end": v(64.3, 22.33) * mm});
            skLineSegment(sketch, "E161.19.5.2", {"start": v(64.3, 22.33) * mm, "end": v(68.92, 22.33) * mm});
            skLineSegment(sketch, "E161.19.5.3", {"start": v(68.92, 26.95) * mm, "end": v(68.92, 22.33) * mm});
            skLineSegment(sketch, "E161.19.6.0", {"start": v(64.3, 14.25) * mm, "end": v(68.92, 14.25) * mm});
            skLineSegment(sketch, "E161.19.6.1", {"start": v(64.3, 14.25) * mm, "end": v(64.3, 9.63) * mm});
            skLineSegment(sketch, "E161.19.6.2", {"start": v(64.3, 9.63) * mm, "end": v(68.92, 9.63) * mm});
            skLineSegment(sketch, "E161.19.6.3", {"start": v(68.92, 14.25) * mm, "end": v(68.92, 9.63) * mm});
            skLineSegment(sketch, "E161.19.7.0", {"start": v(64.3, 1.55) * mm, "end": v(68.92, 1.55) * mm});
            skLineSegment(sketch, "E161.19.7.1", {"start": v(64.3, 1.55) * mm, "end": v(64.3, -3.07) * mm});
            skLineSegment(sketch, "E161.19.7.2", {"start": v(64.3, -3.07) * mm, "end": v(68.92, -3.07) * mm});
            skLineSegment(sketch, "E161.19.7.3", {"start": v(68.92, 1.55) * mm, "end": v(68.92, -3.07) * mm});
            skLineSegment(sketch, "E161.19.8.0", {"start": v(64.3, -11.15) * mm, "end": v(68.92, -11.15) * mm});
            skLineSegment(sketch, "E161.19.8.1", {"start": v(64.3, -11.15) * mm, "end": v(64.3, -15.77) * mm});
            skLineSegment(sketch, "E161.19.8.2", {"start": v(64.3, -15.77) * mm, "end": v(68.92, -15.77) * mm});
            skLineSegment(sketch, "E161.19.8.3", {"start": v(68.92, -11.15) * mm, "end": v(68.92, -15.77) * mm});
            skLineSegment(sketch, "E161.19.9.0", {"start": v(64.3, -23.85) * mm, "end": v(68.92, -23.85) * mm});
            skLineSegment(sketch, "E161.19.9.1", {"start": v(64.3, -23.85) * mm, "end": v(64.3, -28.47) * mm});
            skLineSegment(sketch, "E161.19.9.2", {"start": v(64.3, -28.47) * mm, "end": v(68.92, -28.47) * mm});
            skLineSegment(sketch, "E161.19.9.3", {"start": v(68.92, -23.85) * mm, "end": v(68.92, -28.47) * mm});
            skLineSegment(sketch, "E161.19.10.0", {"start": v(64.3, -36.55) * mm, "end": v(68.92, -36.55) * mm});
            skLineSegment(sketch, "E161.19.10.1", {"start": v(64.3, -36.55) * mm, "end": v(64.3, -41.17) * mm});
            skLineSegment(sketch, "E161.19.10.2", {"start": v(64.3, -41.17) * mm, "end": v(68.92, -41.17) * mm});
            skLineSegment(sketch, "E161.19.10.3", {"start": v(68.92, -36.55) * mm, "end": v(68.92, -41.17) * mm});
            skLineSegment(sketch, "E161.19.11.0", {"start": v(64.3, -49.25) * mm, "end": v(68.92, -49.25) * mm});
            skLineSegment(sketch, "E161.19.11.1", {"start": v(64.3, -49.25) * mm, "end": v(64.3, -53.87) * mm});
            skLineSegment(sketch, "E161.19.11.2", {"start": v(64.3, -53.87) * mm, "end": v(68.92, -53.87) * mm});
            skLineSegment(sketch, "E161.19.11.3", {"start": v(68.92, -49.25) * mm, "end": v(68.92, -53.87) * mm});
            skLineSegment(sketch, "E161.19.12.0", {"start": v(64.3, -61.95) * mm, "end": v(68.92, -61.95) * mm});
            skLineSegment(sketch, "E161.19.12.1", {"start": v(64.3, -61.95) * mm, "end": v(64.3, -66.57) * mm});
            skLineSegment(sketch, "E161.19.12.2", {"start": v(64.3, -66.57) * mm, "end": v(68.92, -66.57) * mm});
            skLineSegment(sketch, "E161.19.12.3", {"start": v(68.92, -61.95) * mm, "end": v(68.92, -66.57) * mm});
            skLineSegment(sketch, "E161.20.0.0", {"start": v(77, 90.45) * mm, "end": v(81.62, 90.45) * mm});
            skLineSegment(sketch, "E161.20.0.1", {"start": v(77, 90.45) * mm, "end": v(77, 85.83) * mm});
            skLineSegment(sketch, "E161.20.0.2", {"start": v(77, 85.83) * mm, "end": v(81.62, 85.83) * mm});
            skLineSegment(sketch, "E161.20.0.3", {"start": v(81.62, 90.45) * mm, "end": v(81.62, 85.83) * mm});
            skLineSegment(sketch, "E161.20.1.0", {"start": v(77, 77.75) * mm, "end": v(81.62, 77.75) * mm});
            skLineSegment(sketch, "E161.20.1.1", {"start": v(77, 77.75) * mm, "end": v(77, 73.13) * mm});
            skLineSegment(sketch, "E161.20.1.2", {"start": v(77, 73.13) * mm, "end": v(81.62, 73.13) * mm});
            skLineSegment(sketch, "E161.20.1.3", {"start": v(81.62, 77.75) * mm, "end": v(81.62, 73.13) * mm});
            skLineSegment(sketch, "E161.20.2.0", {"start": v(77, 65.05) * mm, "end": v(81.62, 65.05) * mm});
            skLineSegment(sketch, "E161.20.2.1", {"start": v(77, 65.05) * mm, "end": v(77, 60.43) * mm});
            skLineSegment(sketch, "E161.20.2.2", {"start": v(77, 60.43) * mm, "end": v(81.62, 60.43) * mm});
            skLineSegment(sketch, "E161.20.2.3", {"start": v(81.62, 65.05) * mm, "end": v(81.62, 60.43) * mm});
            skLineSegment(sketch, "E161.20.3.0", {"start": v(77, 52.35) * mm, "end": v(81.62, 52.35) * mm});
            skLineSegment(sketch, "E161.20.3.1", {"start": v(77, 52.35) * mm, "end": v(77, 47.73) * mm});
            skLineSegment(sketch, "E161.20.3.2", {"start": v(77, 47.73) * mm, "end": v(81.62, 47.73) * mm});
            skLineSegment(sketch, "E161.20.3.3", {"start": v(81.62, 52.35) * mm, "end": v(81.62, 47.73) * mm});
            skLineSegment(sketch, "E161.20.4.0", {"start": v(77, 39.65) * mm, "end": v(81.62, 39.65) * mm});
            skLineSegment(sketch, "E161.20.4.1", {"start": v(77, 39.65) * mm, "end": v(77, 35.03) * mm});
            skLineSegment(sketch, "E161.20.4.2", {"start": v(77, 35.03) * mm, "end": v(81.62, 35.03) * mm});
            skLineSegment(sketch, "E161.20.4.3", {"start": v(81.62, 39.65) * mm, "end": v(81.62, 35.03) * mm});
            skLineSegment(sketch, "E161.20.5.0", {"start": v(77, 26.95) * mm, "end": v(81.62, 26.95) * mm});
            skLineSegment(sketch, "E161.20.5.1", {"start": v(77, 26.95) * mm, "end": v(77, 22.33) * mm});
            skLineSegment(sketch, "E161.20.5.2", {"start": v(77, 22.33) * mm, "end": v(81.62, 22.33) * mm});
            skLineSegment(sketch, "E161.20.5.3", {"start": v(81.62, 26.95) * mm, "end": v(81.62, 22.33) * mm});
            skLineSegment(sketch, "E161.20.6.0", {"start": v(77, 14.25) * mm, "end": v(81.62, 14.25) * mm});
            skLineSegment(sketch, "E161.20.6.1", {"start": v(77, 14.25) * mm, "end": v(77, 9.63) * mm});
            skLineSegment(sketch, "E161.20.6.2", {"start": v(77, 9.63) * mm, "end": v(81.62, 9.63) * mm});
            skLineSegment(sketch, "E161.20.6.3", {"start": v(81.62, 14.25) * mm, "end": v(81.62, 9.63) * mm});
            skLineSegment(sketch, "E161.20.7.0", {"start": v(77, 1.55) * mm, "end": v(81.62, 1.55) * mm});
            skLineSegment(sketch, "E161.20.7.1", {"start": v(77, 1.55) * mm, "end": v(77, -3.07) * mm});
            skLineSegment(sketch, "E161.20.7.2", {"start": v(77, -3.07) * mm, "end": v(81.62, -3.07) * mm});
            skLineSegment(sketch, "E161.20.7.3", {"start": v(81.62, 1.55) * mm, "end": v(81.62, -3.07) * mm});
            skLineSegment(sketch, "E161.20.8.0", {"start": v(77, -11.15) * mm, "end": v(81.62, -11.15) * mm});
            skLineSegment(sketch, "E161.20.8.1", {"start": v(77, -11.15) * mm, "end": v(77, -15.77) * mm});
            skLineSegment(sketch, "E161.20.8.2", {"start": v(77, -15.77) * mm, "end": v(81.62, -15.77) * mm});
            skLineSegment(sketch, "E161.20.8.3", {"start": v(81.62, -11.15) * mm, "end": v(81.62, -15.77) * mm});
            skLineSegment(sketch, "E161.20.9.0", {"start": v(77, -23.85) * mm, "end": v(81.62, -23.85) * mm});
            skLineSegment(sketch, "E161.20.9.1", {"start": v(77, -23.85) * mm, "end": v(77, -28.47) * mm});
            skLineSegment(sketch, "E161.20.9.2", {"start": v(77, -28.47) * mm, "end": v(81.62, -28.47) * mm});
            skLineSegment(sketch, "E161.20.9.3", {"start": v(81.62, -23.85) * mm, "end": v(81.62, -28.47) * mm});
            skLineSegment(sketch, "E161.20.10.0", {"start": v(77, -36.55) * mm, "end": v(81.62, -36.55) * mm});
            skLineSegment(sketch, "E161.20.10.1", {"start": v(77, -36.55) * mm, "end": v(77, -41.17) * mm});
            skLineSegment(sketch, "E161.20.10.2", {"start": v(77, -41.17) * mm, "end": v(81.62, -41.17) * mm});
            skLineSegment(sketch, "E161.20.10.3", {"start": v(81.62, -36.55) * mm, "end": v(81.62, -41.17) * mm});
            skLineSegment(sketch, "E161.20.11.0", {"start": v(77, -49.25) * mm, "end": v(81.62, -49.25) * mm});
            skLineSegment(sketch, "E161.20.11.1", {"start": v(77, -49.25) * mm, "end": v(77, -53.87) * mm});
            skLineSegment(sketch, "E161.20.11.2", {"start": v(77, -53.87) * mm, "end": v(81.62, -53.87) * mm});
            skLineSegment(sketch, "E161.20.11.3", {"start": v(81.62, -49.25) * mm, "end": v(81.62, -53.87) * mm});
            skLineSegment(sketch, "E161.20.12.0", {"start": v(77, -61.95) * mm, "end": v(81.62, -61.95) * mm});
            skLineSegment(sketch, "E161.20.12.1", {"start": v(77, -61.95) * mm, "end": v(77, -66.57) * mm});
            skLineSegment(sketch, "E161.20.12.2", {"start": v(77, -66.57) * mm, "end": v(81.62, -66.57) * mm});
            skLineSegment(sketch, "E161.20.12.3", {"start": v(81.62, -61.95) * mm, "end": v(81.62, -66.57) * mm});
            skLineSegment(sketch, "E161.direction1", {"start": v(-177, 90.45) * mm, "end": v(-164.3, 90.45) * mm, "construction": true});
            skLineSegment(sketch, "E161.direction2", {"start": v(-177, 90.45) * mm, "end": v(-177, 77.75) * mm, "construction": true});
            skLineSegment(sketch, "E162", {"start": v(-174.7, 90.45) * mm, "end": v(-174.7, 94.5) * mm});
            skLineSegment(sketch, "E163.0.21.0", {"start": v(89.7, 90.45) * mm, "end": v(94.32, 90.45) * mm});
            skLineSegment(sketch, "E163.3.21.0", {"start": v(89.7, 90.45) * mm, "end": v(89.7, 85.83) * mm});
            skLineSegment(sketch, "E163.6.21.0", {"start": v(89.7, 85.83) * mm, "end": v(94.32, 85.83) * mm});
            skLineSegment(sketch, "E163.9.21.0", {"start": v(94.32, 90.45) * mm, "end": v(94.32, 85.83) * mm});
            skLineSegment(sketch, "E163.0.21.1", {"start": v(89.7, 77.75) * mm, "end": v(94.32, 77.75) * mm});
            skLineSegment(sketch, "E163.3.21.1", {"start": v(89.7, 77.75) * mm, "end": v(89.7, 73.13) * mm});
            skLineSegment(sketch, "E163.6.21.1", {"start": v(89.7, 73.13) * mm, "end": v(94.32, 73.13) * mm});
            skLineSegment(sketch, "E163.9.21.1", {"start": v(94.32, 77.75) * mm, "end": v(94.32, 73.13) * mm});
            skLineSegment(sketch, "E163.0.21.2", {"start": v(89.7, 65.05) * mm, "end": v(94.32, 65.05) * mm});
            skLineSegment(sketch, "E163.3.21.2", {"start": v(89.7, 65.05) * mm, "end": v(89.7, 60.43) * mm});
            skLineSegment(sketch, "E163.6.21.2", {"start": v(89.7, 60.43) * mm, "end": v(94.32, 60.43) * mm});
            skLineSegment(sketch, "E163.9.21.2", {"start": v(94.32, 65.05) * mm, "end": v(94.32, 60.43) * mm});
            skLineSegment(sketch, "E163.0.21.3", {"start": v(89.7, 52.35) * mm, "end": v(94.32, 52.35) * mm});
            skLineSegment(sketch, "E163.3.21.3", {"start": v(89.7, 52.35) * mm, "end": v(89.7, 47.73) * mm});
            skLineSegment(sketch, "E163.6.21.3", {"start": v(89.7, 47.73) * mm, "end": v(94.32, 47.73) * mm});
            skLineSegment(sketch, "E163.9.21.3", {"start": v(94.32, 52.35) * mm, "end": v(94.32, 47.73) * mm});
            skLineSegment(sketch, "E163.0.21.4", {"start": v(89.7, 39.65) * mm, "end": v(94.32, 39.65) * mm});
            skLineSegment(sketch, "E163.3.21.4", {"start": v(89.7, 39.65) * mm, "end": v(89.7, 35.03) * mm});
            skLineSegment(sketch, "E163.6.21.4", {"start": v(89.7, 35.03) * mm, "end": v(94.32, 35.03) * mm});
            skLineSegment(sketch, "E163.9.21.4", {"start": v(94.32, 39.65) * mm, "end": v(94.32, 35.03) * mm});
            skLineSegment(sketch, "E163.0.21.5", {"start": v(89.7, 26.95) * mm, "end": v(94.32, 26.95) * mm});
            skLineSegment(sketch, "E163.3.21.5", {"start": v(89.7, 26.95) * mm, "end": v(89.7, 22.33) * mm});
            skLineSegment(sketch, "E163.6.21.5", {"start": v(89.7, 22.33) * mm, "end": v(94.32, 22.33) * mm});
            skLineSegment(sketch, "E163.9.21.5", {"start": v(94.32, 26.95) * mm, "end": v(94.32, 22.33) * mm});
            skLineSegment(sketch, "E163.0.21.6", {"start": v(89.7, 14.25) * mm, "end": v(94.32, 14.25) * mm});
            skLineSegment(sketch, "E163.3.21.6", {"start": v(89.7, 14.25) * mm, "end": v(89.7, 9.63) * mm});
            skLineSegment(sketch, "E163.6.21.6", {"start": v(89.7, 9.63) * mm, "end": v(94.32, 9.63) * mm});
            skLineSegment(sketch, "E163.9.21.6", {"start": v(94.32, 14.25) * mm, "end": v(94.32, 9.63) * mm});
            skLineSegment(sketch, "E163.0.21.7", {"start": v(89.7, 1.55) * mm, "end": v(94.32, 1.55) * mm});
            skLineSegment(sketch, "E163.3.21.7", {"start": v(89.7, 1.55) * mm, "end": v(89.7, -3.07) * mm});
            skLineSegment(sketch, "E163.6.21.7", {"start": v(89.7, -3.07) * mm, "end": v(94.32, -3.07) * mm});
            skLineSegment(sketch, "E163.9.21.7", {"start": v(94.32, 1.55) * mm, "end": v(94.32, -3.07) * mm});
            skLineSegment(sketch, "E163.0.21.8", {"start": v(89.7, -11.15) * mm, "end": v(94.32, -11.15) * mm});
            skLineSegment(sketch, "E163.3.21.8", {"start": v(89.7, -11.15) * mm, "end": v(89.7, -15.77) * mm});
            skLineSegment(sketch, "E163.6.21.8", {"start": v(89.7, -15.77) * mm, "end": v(94.32, -15.77) * mm});
            skLineSegment(sketch, "E163.9.21.8", {"start": v(94.32, -11.15) * mm, "end": v(94.32, -15.77) * mm});
            skLineSegment(sketch, "E163.0.21.9", {"start": v(89.7, -23.85) * mm, "end": v(94.32, -23.85) * mm});
            skLineSegment(sketch, "E163.3.21.9", {"start": v(89.7, -23.85) * mm, "end": v(89.7, -28.47) * mm});
            skLineSegment(sketch, "E163.6.21.9", {"start": v(89.7, -28.47) * mm, "end": v(94.32, -28.47) * mm});
            skLineSegment(sketch, "E163.9.21.9", {"start": v(94.32, -23.85) * mm, "end": v(94.32, -28.47) * mm});
            skLineSegment(sketch, "E163.0.21.10", {"start": v(89.7, -36.55) * mm, "end": v(94.32, -36.55) * mm});
            skLineSegment(sketch, "E163.3.21.10", {"start": v(89.7, -36.55) * mm, "end": v(89.7, -41.17) * mm});
            skLineSegment(sketch, "E163.6.21.10", {"start": v(89.7, -41.17) * mm, "end": v(94.32, -41.17) * mm});
            skLineSegment(sketch, "E163.9.21.10", {"start": v(94.32, -36.55) * mm, "end": v(94.32, -41.17) * mm});
            skLineSegment(sketch, "E163.0.21.11", {"start": v(89.7, -49.25) * mm, "end": v(94.32, -49.25) * mm});
            skLineSegment(sketch, "E163.3.21.11", {"start": v(89.7, -49.25) * mm, "end": v(89.7, -53.87) * mm});
            skLineSegment(sketch, "E163.6.21.11", {"start": v(89.7, -53.87) * mm, "end": v(94.32, -53.87) * mm});
            skLineSegment(sketch, "E163.9.21.11", {"start": v(94.32, -49.25) * mm, "end": v(94.32, -53.87) * mm});
            skLineSegment(sketch, "E163.0.21.12", {"start": v(89.7, -61.95) * mm, "end": v(94.32, -61.95) * mm});
            skLineSegment(sketch, "E163.3.21.12", {"start": v(89.7, -61.95) * mm, "end": v(89.7, -66.57) * mm});
            skLineSegment(sketch, "E163.6.21.12", {"start": v(89.7, -66.57) * mm, "end": v(94.32, -66.57) * mm});
            skLineSegment(sketch, "E163.9.21.12", {"start": v(94.32, -61.95) * mm, "end": v(94.32, -66.57) * mm});
            skLineSegment(sketch, "E164.0.0.13", {"start": v(-177, -74.65) * mm, "end": v(-172.38, -74.65) * mm});
            skLineSegment(sketch, "E164.3.0.13", {"start": v(-177, -74.65) * mm, "end": v(-177, -79.27) * mm});
            skLineSegment(sketch, "E164.6.0.13", {"start": v(-177, -79.27) * mm, "end": v(-172.38, -79.27) * mm});
            skLineSegment(sketch, "E164.9.0.13", {"start": v(-172.38, -74.65) * mm, "end": v(-172.38, -79.27) * mm});
            skLineSegment(sketch, "E164.0.1.13", {"start": v(-164.3, -74.65) * mm, "end": v(-159.68, -74.65) * mm});
            skLineSegment(sketch, "E164.3.1.13", {"start": v(-164.3, -74.65) * mm, "end": v(-164.3, -79.27) * mm});
            skLineSegment(sketch, "E164.6.1.13", {"start": v(-164.3, -79.27) * mm, "end": v(-159.68, -79.27) * mm});
            skLineSegment(sketch, "E164.9.1.13", {"start": v(-159.68, -74.65) * mm, "end": v(-159.68, -79.27) * mm});
            skLineSegment(sketch, "E164.0.2.13", {"start": v(-151.6, -74.65) * mm, "end": v(-146.98, -74.65) * mm});
            skLineSegment(sketch, "E164.3.2.13", {"start": v(-151.6, -74.65) * mm, "end": v(-151.6, -79.27) * mm});
            skLineSegment(sketch, "E164.6.2.13", {"start": v(-151.6, -79.27) * mm, "end": v(-146.98, -79.27) * mm});
            skLineSegment(sketch, "E164.9.2.13", {"start": v(-146.98, -74.65) * mm, "end": v(-146.98, -79.27) * mm});
            skLineSegment(sketch, "E164.0.3.13", {"start": v(-138.9, -74.65) * mm, "end": v(-134.28, -74.65) * mm});
            skLineSegment(sketch, "E164.3.3.13", {"start": v(-138.9, -74.65) * mm, "end": v(-138.9, -79.27) * mm});
            skLineSegment(sketch, "E164.6.3.13", {"start": v(-138.9, -79.27) * mm, "end": v(-134.28, -79.27) * mm});
            skLineSegment(sketch, "E164.9.3.13", {"start": v(-134.28, -74.65) * mm, "end": v(-134.28, -79.27) * mm});
            skLineSegment(sketch, "E164.0.4.13", {"start": v(-126.2, -74.65) * mm, "end": v(-121.58, -74.65) * mm});
            skLineSegment(sketch, "E164.3.4.13", {"start": v(-126.2, -74.65) * mm, "end": v(-126.2, -79.27) * mm});
            skLineSegment(sketch, "E164.6.4.13", {"start": v(-126.2, -79.27) * mm, "end": v(-121.58, -79.27) * mm});
            skLineSegment(sketch, "E164.9.4.13", {"start": v(-121.58, -74.65) * mm, "end": v(-121.58, -79.27) * mm});
            skLineSegment(sketch, "E164.0.5.13", {"start": v(-113.5, -74.65) * mm, "end": v(-108.88, -74.65) * mm});
            skLineSegment(sketch, "E164.3.5.13", {"start": v(-113.5, -74.65) * mm, "end": v(-113.5, -79.27) * mm});
            skLineSegment(sketch, "E164.6.5.13", {"start": v(-113.5, -79.27) * mm, "end": v(-108.88, -79.27) * mm});
            skLineSegment(sketch, "E164.9.5.13", {"start": v(-108.88, -74.65) * mm, "end": v(-108.88, -79.27) * mm});
            skLineSegment(sketch, "E164.0.6.13", {"start": v(-100.8, -74.65) * mm, "end": v(-96.18, -74.65) * mm});
            skLineSegment(sketch, "E164.3.6.13", {"start": v(-100.8, -74.65) * mm, "end": v(-100.8, -79.27) * mm});
            skLineSegment(sketch, "E164.6.6.13", {"start": v(-100.8, -79.27) * mm, "end": v(-96.18, -79.27) * mm});
            skLineSegment(sketch, "E164.9.6.13", {"start": v(-96.18, -74.65) * mm, "end": v(-96.18, -79.27) * mm});
            skLineSegment(sketch, "E164.0.7.13", {"start": v(-88.1, -74.65) * mm, "end": v(-83.48, -74.65) * mm});
            skLineSegment(sketch, "E164.3.7.13", {"start": v(-88.1, -74.65) * mm, "end": v(-88.1, -79.27) * mm});
            skLineSegment(sketch, "E164.6.7.13", {"start": v(-88.1, -79.27) * mm, "end": v(-83.48, -79.27) * mm});
            skLineSegment(sketch, "E164.9.7.13", {"start": v(-83.48, -74.65) * mm, "end": v(-83.48, -79.27) * mm});
            skLineSegment(sketch, "E164.0.8.13", {"start": v(-75.4, -74.65) * mm, "end": v(-70.78, -74.65) * mm});
            skLineSegment(sketch, "E164.3.8.13", {"start": v(-75.4, -74.65) * mm, "end": v(-75.4, -79.27) * mm});
            skLineSegment(sketch, "E164.6.8.13", {"start": v(-75.4, -79.27) * mm, "end": v(-70.78, -79.27) * mm});
            skLineSegment(sketch, "E164.9.8.13", {"start": v(-70.78, -74.65) * mm, "end": v(-70.78, -79.27) * mm});
            skLineSegment(sketch, "E164.0.9.13", {"start": v(-62.7, -74.65) * mm, "end": v(-58.08, -74.65) * mm});
            skLineSegment(sketch, "E164.3.9.13", {"start": v(-62.7, -74.65) * mm, "end": v(-62.7, -79.27) * mm});
            skLineSegment(sketch, "E164.6.9.13", {"start": v(-62.7, -79.27) * mm, "end": v(-58.08, -79.27) * mm});
            skLineSegment(sketch, "E164.9.9.13", {"start": v(-58.08, -74.65) * mm, "end": v(-58.08, -79.27) * mm});
            skLineSegment(sketch, "E164.0.10.13", {"start": v(-50, -74.65) * mm, "end": v(-45.38, -74.65) * mm});
            skLineSegment(sketch, "E164.3.10.13", {"start": v(-50, -74.65) * mm, "end": v(-50, -79.27) * mm});
            skLineSegment(sketch, "E164.6.10.13", {"start": v(-50, -79.27) * mm, "end": v(-45.38, -79.27) * mm});
            skLineSegment(sketch, "E164.9.10.13", {"start": v(-45.38, -74.65) * mm, "end": v(-45.38, -79.27) * mm});
            skLineSegment(sketch, "E164.0.11.13", {"start": v(-37.3, -74.65) * mm, "end": v(-32.68, -74.65) * mm});
            skLineSegment(sketch, "E164.3.11.13", {"start": v(-37.3, -74.65) * mm, "end": v(-37.3, -79.27) * mm});
            skLineSegment(sketch, "E164.6.11.13", {"start": v(-37.3, -79.27) * mm, "end": v(-32.68, -79.27) * mm});
            skLineSegment(sketch, "E164.9.11.13", {"start": v(-32.68, -74.65) * mm, "end": v(-32.68, -79.27) * mm});
            skLineSegment(sketch, "E164.0.12.13", {"start": v(-24.6, -74.65) * mm, "end": v(-19.98, -74.65) * mm});
            skLineSegment(sketch, "E164.3.12.13", {"start": v(-24.6, -74.65) * mm, "end": v(-24.6, -79.27) * mm});
            skLineSegment(sketch, "E164.6.12.13", {"start": v(-24.6, -79.27) * mm, "end": v(-19.98, -79.27) * mm});
            skLineSegment(sketch, "E164.9.12.13", {"start": v(-19.98, -74.65) * mm, "end": v(-19.98, -79.27) * mm});
            skLineSegment(sketch, "E164.0.13.13", {"start": v(-11.9, -74.65) * mm, "end": v(-7.28, -74.65) * mm});
            skLineSegment(sketch, "E164.3.13.13", {"start": v(-11.9, -74.65) * mm, "end": v(-11.9, -79.27) * mm});
            skLineSegment(sketch, "E164.6.13.13", {"start": v(-11.9, -79.27) * mm, "end": v(-7.28, -79.27) * mm});
            skLineSegment(sketch, "E164.9.13.13", {"start": v(-7.28, -74.65) * mm, "end": v(-7.28, -79.27) * mm});
            skLineSegment(sketch, "E164.0.14.13", {"start": v(0.8, -74.65) * mm, "end": v(5.42, -74.65) * mm});
            skLineSegment(sketch, "E164.3.14.13", {"start": v(0.8, -74.65) * mm, "end": v(0.8, -79.27) * mm});
            skLineSegment(sketch, "E164.6.14.13", {"start": v(0.8, -79.27) * mm, "end": v(5.42, -79.27) * mm});
            skLineSegment(sketch, "E164.9.14.13", {"start": v(5.42, -74.65) * mm, "end": v(5.42, -79.27) * mm});
            skLineSegment(sketch, "E164.0.15.13", {"start": v(13.5, -74.65) * mm, "end": v(18.12, -74.65) * mm});
            skLineSegment(sketch, "E164.3.15.13", {"start": v(13.5, -74.65) * mm, "end": v(13.5, -79.27) * mm});
            skLineSegment(sketch, "E164.6.15.13", {"start": v(13.5, -79.27) * mm, "end": v(18.12, -79.27) * mm});
            skLineSegment(sketch, "E164.9.15.13", {"start": v(18.12, -74.65) * mm, "end": v(18.12, -79.27) * mm});
            skLineSegment(sketch, "E164.0.16.13", {"start": v(26.2, -74.65) * mm, "end": v(30.82, -74.65) * mm});
            skLineSegment(sketch, "E164.3.16.13", {"start": v(26.2, -74.65) * mm, "end": v(26.2, -79.27) * mm});
            skLineSegment(sketch, "E164.6.16.13", {"start": v(26.2, -79.27) * mm, "end": v(30.82, -79.27) * mm});
            skLineSegment(sketch, "E164.9.16.13", {"start": v(30.82, -74.65) * mm, "end": v(30.82, -79.27) * mm});
            skLineSegment(sketch, "E164.0.17.13", {"start": v(38.9, -74.65) * mm, "end": v(43.52, -74.65) * mm});
            skLineSegment(sketch, "E164.3.17.13", {"start": v(38.9, -74.65) * mm, "end": v(38.9, -79.27) * mm});
            skLineSegment(sketch, "E164.6.17.13", {"start": v(38.9, -79.27) * mm, "end": v(43.52, -79.27) * mm});
            skLineSegment(sketch, "E164.9.17.13", {"start": v(43.52, -74.65) * mm, "end": v(43.52, -79.27) * mm});
            skLineSegment(sketch, "E164.0.18.13", {"start": v(51.6, -74.65) * mm, "end": v(56.22, -74.65) * mm});
            skLineSegment(sketch, "E164.3.18.13", {"start": v(51.6, -74.65) * mm, "end": v(51.6, -79.27) * mm});
            skLineSegment(sketch, "E164.6.18.13", {"start": v(51.6, -79.27) * mm, "end": v(56.22, -79.27) * mm});
            skLineSegment(sketch, "E164.9.18.13", {"start": v(56.22, -74.65) * mm, "end": v(56.22, -79.27) * mm});
            skLineSegment(sketch, "E164.0.19.13", {"start": v(64.3, -74.65) * mm, "end": v(68.92, -74.65) * mm});
            skLineSegment(sketch, "E164.3.19.13", {"start": v(64.3, -74.65) * mm, "end": v(64.3, -79.27) * mm});
            skLineSegment(sketch, "E164.6.19.13", {"start": v(64.3, -79.27) * mm, "end": v(68.92, -79.27) * mm});
            skLineSegment(sketch, "E164.9.19.13", {"start": v(68.92, -74.65) * mm, "end": v(68.92, -79.27) * mm});
            skLineSegment(sketch, "E164.0.20.13", {"start": v(77, -74.65) * mm, "end": v(81.62, -74.65) * mm});
            skLineSegment(sketch, "E164.3.20.13", {"start": v(77, -74.65) * mm, "end": v(77, -79.27) * mm});
            skLineSegment(sketch, "E164.6.20.13", {"start": v(77, -79.27) * mm, "end": v(81.62, -79.27) * mm});
            skLineSegment(sketch, "E164.9.20.13", {"start": v(81.62, -74.65) * mm, "end": v(81.62, -79.27) * mm});
            skLineSegment(sketch, "E164.0.21.13", {"start": v(89.7, -74.65) * mm, "end": v(94.32, -74.65) * mm});
            skLineSegment(sketch, "E164.3.21.13", {"start": v(89.7, -74.65) * mm, "end": v(89.7, -79.27) * mm});
            skLineSegment(sketch, "E164.6.21.13", {"start": v(89.7, -79.27) * mm, "end": v(94.32, -79.27) * mm});
            skLineSegment(sketch, "E164.9.21.13", {"start": v(94.32, -74.65) * mm, "end": v(94.32, -79.27) * mm});
            skLineSegment(sketch, "E165.bottom", {"start": v(-170.66, 84.1) * mm, "end": v(-166.03, 84.1) * mm});
            skLineSegment(sketch, "E165.top", {"start": v(-170.66, 79.48) * mm, "end": v(-166.03, 79.48) * mm});
            skLineSegment(sketch, "E165.left", {"start": v(-170.66, 84.1) * mm, "end": v(-170.66, 79.48) * mm});
            skLineSegment(sketch, "E165.right", {"start": v(-166.03, 84.1) * mm, "end": v(-166.03, 79.48) * mm});
            skLineSegment(sketch, "E166.0.1.0", {"start": v(-170.66, 71.4) * mm, "end": v(-166.03, 71.4) * mm});
            skLineSegment(sketch, "E166.0.1.1", {"start": v(-170.66, 71.4) * mm, "end": v(-170.66, 66.78) * mm});
            skLineSegment(sketch, "E166.0.1.2", {"start": v(-170.66, 66.78) * mm, "end": v(-166.03, 66.78) * mm});
            skLineSegment(sketch, "E166.0.1.3", {"start": v(-166.03, 71.4) * mm, "end": v(-166.03, 66.78) * mm});
            skLineSegment(sketch, "E166.0.2.0", {"start": v(-170.66, 58.7) * mm, "end": v(-166.03, 58.7) * mm});
            skLineSegment(sketch, "E166.0.2.1", {"start": v(-170.66, 58.7) * mm, "end": v(-170.66, 54.08) * mm});
            skLineSegment(sketch, "E166.0.2.2", {"start": v(-170.66, 54.08) * mm, "end": v(-166.03, 54.08) * mm});
            skLineSegment(sketch, "E166.0.2.3", {"start": v(-166.03, 58.7) * mm, "end": v(-166.03, 54.08) * mm});
            skLineSegment(sketch, "E166.0.3.0", {"start": v(-170.66, 46) * mm, "end": v(-166.03, 46) * mm});
            skLineSegment(sketch, "E166.0.3.1", {"start": v(-170.66, 46) * mm, "end": v(-170.66, 41.38) * mm});
            skLineSegment(sketch, "E166.0.3.2", {"start": v(-170.66, 41.38) * mm, "end": v(-166.03, 41.38) * mm});
            skLineSegment(sketch, "E166.0.3.3", {"start": v(-166.03, 46) * mm, "end": v(-166.03, 41.38) * mm});
            skLineSegment(sketch, "E166.0.4.0", {"start": v(-170.66, 33.3) * mm, "end": v(-166.03, 33.3) * mm});
            skLineSegment(sketch, "E166.0.4.1", {"start": v(-170.66, 33.3) * mm, "end": v(-170.66, 28.68) * mm});
            skLineSegment(sketch, "E166.0.4.2", {"start": v(-170.66, 28.68) * mm, "end": v(-166.03, 28.68) * mm});
            skLineSegment(sketch, "E166.0.4.3", {"start": v(-166.03, 33.3) * mm, "end": v(-166.03, 28.68) * mm});
            skLineSegment(sketch, "E166.0.5.0", {"start": v(-170.66, 20.6) * mm, "end": v(-166.03, 20.6) * mm});
            skLineSegment(sketch, "E166.0.5.1", {"start": v(-170.66, 20.6) * mm, "end": v(-170.66, 15.98) * mm});
            skLineSegment(sketch, "E166.0.5.2", {"start": v(-170.66, 15.98) * mm, "end": v(-166.03, 15.98) * mm});
            skLineSegment(sketch, "E166.0.5.3", {"start": v(-166.03, 20.6) * mm, "end": v(-166.03, 15.98) * mm});
            skLineSegment(sketch, "E166.0.6.0", {"start": v(-170.66, 7.9) * mm, "end": v(-166.03, 7.9) * mm});
            skLineSegment(sketch, "E166.0.6.1", {"start": v(-170.66, 7.9) * mm, "end": v(-170.66, 3.28) * mm});
            skLineSegment(sketch, "E166.0.6.2", {"start": v(-170.66, 3.28) * mm, "end": v(-166.03, 3.28) * mm});
            skLineSegment(sketch, "E166.0.6.3", {"start": v(-166.03, 7.9) * mm, "end": v(-166.03, 3.28) * mm});
            skLineSegment(sketch, "E166.0.7.0", {"start": v(-170.66, -4.8) * mm, "end": v(-166.03, -4.8) * mm});
            skLineSegment(sketch, "E166.0.7.1", {"start": v(-170.66, -4.8) * mm, "end": v(-170.66, -9.42) * mm});
            skLineSegment(sketch, "E166.0.7.2", {"start": v(-170.66, -9.42) * mm, "end": v(-166.03, -9.42) * mm});
            skLineSegment(sketch, "E166.0.7.3", {"start": v(-166.03, -4.8) * mm, "end": v(-166.03, -9.42) * mm});
            skLineSegment(sketch, "E166.0.8.0", {"start": v(-170.66, -17.5) * mm, "end": v(-166.03, -17.5) * mm});
            skLineSegment(sketch, "E166.0.8.1", {"start": v(-170.66, -17.5) * mm, "end": v(-170.66, -22.12) * mm});
            skLineSegment(sketch, "E166.0.8.2", {"start": v(-170.66, -22.12) * mm, "end": v(-166.03, -22.12) * mm});
            skLineSegment(sketch, "E166.0.8.3", {"start": v(-166.03, -17.5) * mm, "end": v(-166.03, -22.12) * mm});
            skLineSegment(sketch, "E166.0.9.0", {"start": v(-170.66, -30.2) * mm, "end": v(-166.03, -30.2) * mm});
            skLineSegment(sketch, "E166.0.9.1", {"start": v(-170.66, -30.2) * mm, "end": v(-170.66, -34.82) * mm});
            skLineSegment(sketch, "E166.0.9.2", {"start": v(-170.66, -34.82) * mm, "end": v(-166.03, -34.82) * mm});
            skLineSegment(sketch, "E166.0.9.3", {"start": v(-166.03, -30.2) * mm, "end": v(-166.03, -34.82) * mm});
            skLineSegment(sketch, "E166.0.10.0", {"start": v(-170.66, -42.9) * mm, "end": v(-166.03, -42.9) * mm});
            skLineSegment(sketch, "E166.0.10.1", {"start": v(-170.66, -42.9) * mm, "end": v(-170.66, -47.52) * mm});
            skLineSegment(sketch, "E166.0.10.2", {"start": v(-170.66, -47.52) * mm, "end": v(-166.03, -47.52) * mm});
            skLineSegment(sketch, "E166.0.10.3", {"start": v(-166.03, -42.9) * mm, "end": v(-166.03, -47.52) * mm});
            skLineSegment(sketch, "E166.0.11.0", {"start": v(-170.66, -55.6) * mm, "end": v(-166.03, -55.6) * mm});
            skLineSegment(sketch, "E166.0.11.1", {"start": v(-170.66, -55.6) * mm, "end": v(-170.66, -60.22) * mm});
            skLineSegment(sketch, "E166.0.11.2", {"start": v(-170.66, -60.22) * mm, "end": v(-166.03, -60.22) * mm});
            skLineSegment(sketch, "E166.0.11.3", {"start": v(-166.03, -55.6) * mm, "end": v(-166.03, -60.22) * mm});
            skLineSegment(sketch, "E166.0.12.0", {"start": v(-170.66, -68.3) * mm, "end": v(-166.03, -68.3) * mm});
            skLineSegment(sketch, "E166.0.12.1", {"start": v(-170.66, -68.3) * mm, "end": v(-170.66, -72.92) * mm});
            skLineSegment(sketch, "E166.0.12.2", {"start": v(-170.66, -72.92) * mm, "end": v(-166.03, -72.92) * mm});
            skLineSegment(sketch, "E166.0.12.3", {"start": v(-166.03, -68.3) * mm, "end": v(-166.03, -72.92) * mm});
            skLineSegment(sketch, "E166.1.0.0", {"start": v(-157.96, 84.1) * mm, "end": v(-153.33, 84.1) * mm});
            skLineSegment(sketch, "E166.1.0.1", {"start": v(-157.96, 84.1) * mm, "end": v(-157.96, 79.48) * mm});
            skLineSegment(sketch, "E166.1.0.2", {"start": v(-157.96, 79.48) * mm, "end": v(-153.33, 79.48) * mm});
            skLineSegment(sketch, "E166.1.0.3", {"start": v(-153.33, 84.1) * mm, "end": v(-153.33, 79.48) * mm});
            skLineSegment(sketch, "E166.1.1.0", {"start": v(-157.96, 71.4) * mm, "end": v(-153.33, 71.4) * mm});
            skLineSegment(sketch, "E166.1.1.1", {"start": v(-157.96, 71.4) * mm, "end": v(-157.96, 66.78) * mm});
            skLineSegment(sketch, "E166.1.1.2", {"start": v(-157.96, 66.78) * mm, "end": v(-153.33, 66.78) * mm});
            skLineSegment(sketch, "E166.1.1.3", {"start": v(-153.33, 71.4) * mm, "end": v(-153.33, 66.78) * mm});
            skLineSegment(sketch, "E166.1.2.0", {"start": v(-157.96, 58.7) * mm, "end": v(-153.33, 58.7) * mm});
            skLineSegment(sketch, "E166.1.2.1", {"start": v(-157.96, 58.7) * mm, "end": v(-157.96, 54.08) * mm});
            skLineSegment(sketch, "E166.1.2.2", {"start": v(-157.96, 54.08) * mm, "end": v(-153.33, 54.08) * mm});
            skLineSegment(sketch, "E166.1.2.3", {"start": v(-153.33, 58.7) * mm, "end": v(-153.33, 54.08) * mm});
            skLineSegment(sketch, "E166.1.3.0", {"start": v(-157.96, 46) * mm, "end": v(-153.33, 46) * mm});
            skLineSegment(sketch, "E166.1.3.1", {"start": v(-157.96, 46) * mm, "end": v(-157.96, 41.38) * mm});
            skLineSegment(sketch, "E166.1.3.2", {"start": v(-157.96, 41.38) * mm, "end": v(-153.33, 41.38) * mm});
            skLineSegment(sketch, "E166.1.3.3", {"start": v(-153.33, 46) * mm, "end": v(-153.33, 41.38) * mm});
            skLineSegment(sketch, "E166.1.4.0", {"start": v(-157.96, 33.3) * mm, "end": v(-153.33, 33.3) * mm});
            skLineSegment(sketch, "E166.1.4.1", {"start": v(-157.96, 33.3) * mm, "end": v(-157.96, 28.68) * mm});
            skLineSegment(sketch, "E166.1.4.2", {"start": v(-157.96, 28.68) * mm, "end": v(-153.33, 28.68) * mm});
            skLineSegment(sketch, "E166.1.4.3", {"start": v(-153.33, 33.3) * mm, "end": v(-153.33, 28.68) * mm});
            skLineSegment(sketch, "E166.1.5.0", {"start": v(-157.96, 20.6) * mm, "end": v(-153.33, 20.6) * mm});
            skLineSegment(sketch, "E166.1.5.1", {"start": v(-157.96, 20.6) * mm, "end": v(-157.96, 15.98) * mm});
            skLineSegment(sketch, "E166.1.5.2", {"start": v(-157.96, 15.98) * mm, "end": v(-153.33, 15.98) * mm});
            skLineSegment(sketch, "E166.1.5.3", {"start": v(-153.33, 20.6) * mm, "end": v(-153.33, 15.98) * mm});
            skLineSegment(sketch, "E166.1.6.0", {"start": v(-157.96, 7.9) * mm, "end": v(-153.33, 7.9) * mm});
            skLineSegment(sketch, "E166.1.6.1", {"start": v(-157.96, 7.9) * mm, "end": v(-157.96, 3.28) * mm});
            skLineSegment(sketch, "E166.1.6.2", {"start": v(-157.96, 3.28) * mm, "end": v(-153.33, 3.28) * mm});
            skLineSegment(sketch, "E166.1.6.3", {"start": v(-153.33, 7.9) * mm, "end": v(-153.33, 3.28) * mm});
            skLineSegment(sketch, "E166.1.7.0", {"start": v(-157.96, -4.8) * mm, "end": v(-153.33, -4.8) * mm});
            skLineSegment(sketch, "E166.1.7.1", {"start": v(-157.96, -4.8) * mm, "end": v(-157.96, -9.42) * mm});
            skLineSegment(sketch, "E166.1.7.2", {"start": v(-157.96, -9.42) * mm, "end": v(-153.33, -9.42) * mm});
            skLineSegment(sketch, "E166.1.7.3", {"start": v(-153.33, -4.8) * mm, "end": v(-153.33, -9.42) * mm});
            skLineSegment(sketch, "E166.1.8.0", {"start": v(-157.96, -17.5) * mm, "end": v(-153.33, -17.5) * mm});
            skLineSegment(sketch, "E166.1.8.1", {"start": v(-157.96, -17.5) * mm, "end": v(-157.96, -22.12) * mm});
            skLineSegment(sketch, "E166.1.8.2", {"start": v(-157.96, -22.12) * mm, "end": v(-153.33, -22.12) * mm});
            skLineSegment(sketch, "E166.1.8.3", {"start": v(-153.33, -17.5) * mm, "end": v(-153.33, -22.12) * mm});
            skLineSegment(sketch, "E166.1.9.0", {"start": v(-157.96, -30.2) * mm, "end": v(-153.33, -30.2) * mm});
            skLineSegment(sketch, "E166.1.9.1", {"start": v(-157.96, -30.2) * mm, "end": v(-157.96, -34.82) * mm});
            skLineSegment(sketch, "E166.1.9.2", {"start": v(-157.96, -34.82) * mm, "end": v(-153.33, -34.82) * mm});
            skLineSegment(sketch, "E166.1.9.3", {"start": v(-153.33, -30.2) * mm, "end": v(-153.33, -34.82) * mm});
            skLineSegment(sketch, "E166.1.10.0", {"start": v(-157.96, -42.9) * mm, "end": v(-153.33, -42.9) * mm});
            skLineSegment(sketch, "E166.1.10.1", {"start": v(-157.96, -42.9) * mm, "end": v(-157.96, -47.52) * mm});
            skLineSegment(sketch, "E166.1.10.2", {"start": v(-157.96, -47.52) * mm, "end": v(-153.33, -47.52) * mm});
            skLineSegment(sketch, "E166.1.10.3", {"start": v(-153.33, -42.9) * mm, "end": v(-153.33, -47.52) * mm});
            skLineSegment(sketch, "E166.1.11.0", {"start": v(-157.96, -55.6) * mm, "end": v(-153.33, -55.6) * mm});
            skLineSegment(sketch, "E166.1.11.1", {"start": v(-157.96, -55.6) * mm, "end": v(-157.96, -60.22) * mm});
            skLineSegment(sketch, "E166.1.11.2", {"start": v(-157.96, -60.22) * mm, "end": v(-153.33, -60.22) * mm});
            skLineSegment(sketch, "E166.1.11.3", {"start": v(-153.33, -55.6) * mm, "end": v(-153.33, -60.22) * mm});
            skLineSegment(sketch, "E166.1.12.0", {"start": v(-157.96, -68.3) * mm, "end": v(-153.33, -68.3) * mm});
            skLineSegment(sketch, "E166.1.12.1", {"start": v(-157.96, -68.3) * mm, "end": v(-157.96, -72.92) * mm});
            skLineSegment(sketch, "E166.1.12.2", {"start": v(-157.96, -72.92) * mm, "end": v(-153.33, -72.92) * mm});
            skLineSegment(sketch, "E166.1.12.3", {"start": v(-153.33, -68.3) * mm, "end": v(-153.33, -72.92) * mm});
            skLineSegment(sketch, "E166.2.0.0", {"start": v(-145.26, 84.1) * mm, "end": v(-140.63, 84.1) * mm});
            skLineSegment(sketch, "E166.2.0.1", {"start": v(-145.26, 84.1) * mm, "end": v(-145.26, 79.48) * mm});
            skLineSegment(sketch, "E166.2.0.2", {"start": v(-145.26, 79.48) * mm, "end": v(-140.63, 79.48) * mm});
            skLineSegment(sketch, "E166.2.0.3", {"start": v(-140.63, 84.1) * mm, "end": v(-140.63, 79.48) * mm});
            skLineSegment(sketch, "E166.2.1.0", {"start": v(-145.26, 71.4) * mm, "end": v(-140.63, 71.4) * mm});
            skLineSegment(sketch, "E166.2.1.1", {"start": v(-145.26, 71.4) * mm, "end": v(-145.26, 66.78) * mm});
            skLineSegment(sketch, "E166.2.1.2", {"start": v(-145.26, 66.78) * mm, "end": v(-140.63, 66.78) * mm});
            skLineSegment(sketch, "E166.2.1.3", {"start": v(-140.63, 71.4) * mm, "end": v(-140.63, 66.78) * mm});
            skLineSegment(sketch, "E166.2.2.0", {"start": v(-145.26, 58.7) * mm, "end": v(-140.63, 58.7) * mm});
            skLineSegment(sketch, "E166.2.2.1", {"start": v(-145.26, 58.7) * mm, "end": v(-145.26, 54.08) * mm});
            skLineSegment(sketch, "E166.2.2.2", {"start": v(-145.26, 54.08) * mm, "end": v(-140.63, 54.08) * mm});
            skLineSegment(sketch, "E166.2.2.3", {"start": v(-140.63, 58.7) * mm, "end": v(-140.63, 54.08) * mm});
            skLineSegment(sketch, "E166.2.3.0", {"start": v(-145.26, 46) * mm, "end": v(-140.63, 46) * mm});
            skLineSegment(sketch, "E166.2.3.1", {"start": v(-145.26, 46) * mm, "end": v(-145.26, 41.38) * mm});
            skLineSegment(sketch, "E166.2.3.2", {"start": v(-145.26, 41.38) * mm, "end": v(-140.63, 41.38) * mm});
            skLineSegment(sketch, "E166.2.3.3", {"start": v(-140.63, 46) * mm, "end": v(-140.63, 41.38) * mm});
            skLineSegment(sketch, "E166.2.4.0", {"start": v(-145.26, 33.3) * mm, "end": v(-140.63, 33.3) * mm});
            skLineSegment(sketch, "E166.2.4.1", {"start": v(-145.26, 33.3) * mm, "end": v(-145.26, 28.68) * mm});
            skLineSegment(sketch, "E166.2.4.2", {"start": v(-145.26, 28.68) * mm, "end": v(-140.63, 28.68) * mm});
            skLineSegment(sketch, "E166.2.4.3", {"start": v(-140.63, 33.3) * mm, "end": v(-140.63, 28.68) * mm});
            skLineSegment(sketch, "E166.2.5.0", {"start": v(-145.26, 20.6) * mm, "end": v(-140.63, 20.6) * mm});
            skLineSegment(sketch, "E166.2.5.1", {"start": v(-145.26, 20.6) * mm, "end": v(-145.26, 15.98) * mm});
            skLineSegment(sketch, "E166.2.5.2", {"start": v(-145.26, 15.98) * mm, "end": v(-140.63, 15.98) * mm});
            skLineSegment(sketch, "E166.2.5.3", {"start": v(-140.63, 20.6) * mm, "end": v(-140.63, 15.98) * mm});
            skLineSegment(sketch, "E166.2.6.0", {"start": v(-145.26, 7.9) * mm, "end": v(-140.63, 7.9) * mm});
            skLineSegment(sketch, "E166.2.6.1", {"start": v(-145.26, 7.9) * mm, "end": v(-145.26, 3.28) * mm});
            skLineSegment(sketch, "E166.2.6.2", {"start": v(-145.26, 3.28) * mm, "end": v(-140.63, 3.28) * mm});
            skLineSegment(sketch, "E166.2.6.3", {"start": v(-140.63, 7.9) * mm, "end": v(-140.63, 3.28) * mm});
            skLineSegment(sketch, "E166.2.7.0", {"start": v(-145.26, -4.8) * mm, "end": v(-140.63, -4.8) * mm});
            skLineSegment(sketch, "E166.2.7.1", {"start": v(-145.26, -4.8) * mm, "end": v(-145.26, -9.42) * mm});
            skLineSegment(sketch, "E166.2.7.2", {"start": v(-145.26, -9.42) * mm, "end": v(-140.63, -9.42) * mm});
            skLineSegment(sketch, "E166.2.7.3", {"start": v(-140.63, -4.8) * mm, "end": v(-140.63, -9.42) * mm});
            skLineSegment(sketch, "E166.2.8.0", {"start": v(-145.26, -17.5) * mm, "end": v(-140.63, -17.5) * mm});
            skLineSegment(sketch, "E166.2.8.1", {"start": v(-145.26, -17.5) * mm, "end": v(-145.26, -22.12) * mm});
            skLineSegment(sketch, "E166.2.8.2", {"start": v(-145.26, -22.12) * mm, "end": v(-140.63, -22.12) * mm});
            skLineSegment(sketch, "E166.2.8.3", {"start": v(-140.63, -17.5) * mm, "end": v(-140.63, -22.12) * mm});
            skLineSegment(sketch, "E166.2.9.0", {"start": v(-145.26, -30.2) * mm, "end": v(-140.63, -30.2) * mm});
            skLineSegment(sketch, "E166.2.9.1", {"start": v(-145.26, -30.2) * mm, "end": v(-145.26, -34.82) * mm});
            skLineSegment(sketch, "E166.2.9.2", {"start": v(-145.26, -34.82) * mm, "end": v(-140.63, -34.82) * mm});
            skLineSegment(sketch, "E166.2.9.3", {"start": v(-140.63, -30.2) * mm, "end": v(-140.63, -34.82) * mm});
            skLineSegment(sketch, "E166.2.10.0", {"start": v(-145.26, -42.9) * mm, "end": v(-140.63, -42.9) * mm});
            skLineSegment(sketch, "E166.2.10.1", {"start": v(-145.26, -42.9) * mm, "end": v(-145.26, -47.52) * mm});
            skLineSegment(sketch, "E166.2.10.2", {"start": v(-145.26, -47.52) * mm, "end": v(-140.63, -47.52) * mm});
            skLineSegment(sketch, "E166.2.10.3", {"start": v(-140.63, -42.9) * mm, "end": v(-140.63, -47.52) * mm});
            skLineSegment(sketch, "E166.2.11.0", {"start": v(-145.26, -55.6) * mm, "end": v(-140.63, -55.6) * mm});
            skLineSegment(sketch, "E166.2.11.1", {"start": v(-145.26, -55.6) * mm, "end": v(-145.26, -60.22) * mm});
            skLineSegment(sketch, "E166.2.11.2", {"start": v(-145.26, -60.22) * mm, "end": v(-140.63, -60.22) * mm});
            skLineSegment(sketch, "E166.2.11.3", {"start": v(-140.63, -55.6) * mm, "end": v(-140.63, -60.22) * mm});
            skLineSegment(sketch, "E166.2.12.0", {"start": v(-145.26, -68.3) * mm, "end": v(-140.63, -68.3) * mm});
            skLineSegment(sketch, "E166.2.12.1", {"start": v(-145.26, -68.3) * mm, "end": v(-145.26, -72.92) * mm});
            skLineSegment(sketch, "E166.2.12.2", {"start": v(-145.26, -72.92) * mm, "end": v(-140.63, -72.92) * mm});
            skLineSegment(sketch, "E166.2.12.3", {"start": v(-140.63, -68.3) * mm, "end": v(-140.63, -72.92) * mm});
            skLineSegment(sketch, "E166.3.0.0", {"start": v(-132.56, 84.1) * mm, "end": v(-127.93, 84.1) * mm});
            skLineSegment(sketch, "E166.3.0.1", {"start": v(-132.56, 84.1) * mm, "end": v(-132.56, 79.48) * mm});
            skLineSegment(sketch, "E166.3.0.2", {"start": v(-132.56, 79.48) * mm, "end": v(-127.93, 79.48) * mm});
            skLineSegment(sketch, "E166.3.0.3", {"start": v(-127.93, 84.1) * mm, "end": v(-127.93, 79.48) * mm});
            skLineSegment(sketch, "E166.3.1.0", {"start": v(-132.56, 71.4) * mm, "end": v(-127.93, 71.4) * mm});
            skLineSegment(sketch, "E166.3.1.1", {"start": v(-132.56, 71.4) * mm, "end": v(-132.56, 66.78) * mm});
            skLineSegment(sketch, "E166.3.1.2", {"start": v(-132.56, 66.78) * mm, "end": v(-127.93, 66.78) * mm});
            skLineSegment(sketch, "E166.3.1.3", {"start": v(-127.93, 71.4) * mm, "end": v(-127.93, 66.78) * mm});
            skLineSegment(sketch, "E166.3.3.0", {"start": v(-132.56, 46) * mm, "end": v(-127.93, 46) * mm});
            skLineSegment(sketch, "E166.3.3.1", {"start": v(-132.56, 46) * mm, "end": v(-132.56, 41.38) * mm});
            skLineSegment(sketch, "E166.3.3.2", {"start": v(-132.56, 41.38) * mm, "end": v(-127.93, 41.38) * mm});
            skLineSegment(sketch, "E166.3.3.3", {"start": v(-127.93, 46) * mm, "end": v(-127.93, 41.38) * mm});
            skLineSegment(sketch, "E166.3.4.0", {"start": v(-132.56, 33.3) * mm, "end": v(-127.93, 33.3) * mm});
            skLineSegment(sketch, "E166.3.4.1", {"start": v(-132.56, 33.3) * mm, "end": v(-132.56, 28.68) * mm});
            skLineSegment(sketch, "E166.3.4.2", {"start": v(-132.56, 28.68) * mm, "end": v(-127.93, 28.68) * mm});
            skLineSegment(sketch, "E166.3.4.3", {"start": v(-127.93, 33.3) * mm, "end": v(-127.93, 28.68) * mm});
            skLineSegment(sketch, "E166.3.5.0", {"start": v(-132.56, 20.6) * mm, "end": v(-127.93, 20.6) * mm});
            skLineSegment(sketch, "E166.3.5.1", {"start": v(-132.56, 20.6) * mm, "end": v(-132.56, 15.98) * mm});
            skLineSegment(sketch, "E166.3.5.2", {"start": v(-132.56, 15.98) * mm, "end": v(-127.93, 15.98) * mm});
            skLineSegment(sketch, "E166.3.5.3", {"start": v(-127.93, 20.6) * mm, "end": v(-127.93, 15.98) * mm});
            skLineSegment(sketch, "E166.3.6.0", {"start": v(-132.56, 7.9) * mm, "end": v(-127.93, 7.9) * mm});
            skLineSegment(sketch, "E166.3.6.1", {"start": v(-132.56, 7.9) * mm, "end": v(-132.56, 3.28) * mm});
            skLineSegment(sketch, "E166.3.6.2", {"start": v(-132.56, 3.28) * mm, "end": v(-127.93, 3.28) * mm});
            skLineSegment(sketch, "E166.3.6.3", {"start": v(-127.93, 7.9) * mm, "end": v(-127.93, 3.28) * mm});
            skLineSegment(sketch, "E166.3.7.0", {"start": v(-132.56, -4.8) * mm, "end": v(-127.93, -4.8) * mm});
            skLineSegment(sketch, "E166.3.7.1", {"start": v(-132.56, -4.8) * mm, "end": v(-132.56, -9.42) * mm});
            skLineSegment(sketch, "E166.3.7.2", {"start": v(-132.56, -9.42) * mm, "end": v(-127.93, -9.42) * mm});
            skLineSegment(sketch, "E166.3.7.3", {"start": v(-127.93, -4.8) * mm, "end": v(-127.93, -9.42) * mm});
            skLineSegment(sketch, "E166.3.8.0", {"start": v(-132.56, -17.5) * mm, "end": v(-127.93, -17.5) * mm});
            skLineSegment(sketch, "E166.3.8.1", {"start": v(-132.56, -17.5) * mm, "end": v(-132.56, -22.12) * mm});
            skLineSegment(sketch, "E166.3.8.2", {"start": v(-132.56, -22.12) * mm, "end": v(-127.93, -22.12) * mm});
            skLineSegment(sketch, "E166.3.8.3", {"start": v(-127.93, -17.5) * mm, "end": v(-127.93, -22.12) * mm});
            skLineSegment(sketch, "E166.3.9.0", {"start": v(-132.56, -30.2) * mm, "end": v(-127.93, -30.2) * mm});
            skLineSegment(sketch, "E166.3.9.1", {"start": v(-132.56, -30.2) * mm, "end": v(-132.56, -34.82) * mm});
            skLineSegment(sketch, "E166.3.9.2", {"start": v(-132.56, -34.82) * mm, "end": v(-127.93, -34.82) * mm});
            skLineSegment(sketch, "E166.3.9.3", {"start": v(-127.93, -30.2) * mm, "end": v(-127.93, -34.82) * mm});
            skLineSegment(sketch, "E166.3.11.0", {"start": v(-132.56, -55.6) * mm, "end": v(-127.93, -55.6) * mm});
            skLineSegment(sketch, "E166.3.11.1", {"start": v(-132.56, -55.6) * mm, "end": v(-132.56, -60.22) * mm});
            skLineSegment(sketch, "E166.3.11.2", {"start": v(-132.56, -60.22) * mm, "end": v(-127.93, -60.22) * mm});
            skLineSegment(sketch, "E166.3.11.3", {"start": v(-127.93, -55.6) * mm, "end": v(-127.93, -60.22) * mm});
            skLineSegment(sketch, "E166.3.12.0", {"start": v(-132.56, -68.3) * mm, "end": v(-127.93, -68.3) * mm});
            skLineSegment(sketch, "E166.3.12.1", {"start": v(-132.56, -68.3) * mm, "end": v(-132.56, -72.92) * mm});
            skLineSegment(sketch, "E166.3.12.2", {"start": v(-132.56, -72.92) * mm, "end": v(-127.93, -72.92) * mm});
            skLineSegment(sketch, "E166.3.12.3", {"start": v(-127.93, -68.3) * mm, "end": v(-127.93, -72.92) * mm});
            skLineSegment(sketch, "E166.4.0.0", {"start": v(-119.86, 84.1) * mm, "end": v(-115.23, 84.1) * mm});
            skLineSegment(sketch, "E166.4.0.1", {"start": v(-119.86, 84.1) * mm, "end": v(-119.86, 79.48) * mm});
            skLineSegment(sketch, "E166.4.0.2", {"start": v(-119.86, 79.48) * mm, "end": v(-115.23, 79.48) * mm});
            skLineSegment(sketch, "E166.4.0.3", {"start": v(-115.23, 84.1) * mm, "end": v(-115.23, 79.48) * mm});
            skLineSegment(sketch, "E166.4.2.0", {"start": v(-119.86, 58.7) * mm, "end": v(-115.23, 58.7) * mm});
            skLineSegment(sketch, "E166.4.2.1", {"start": v(-119.86, 58.7) * mm, "end": v(-119.86, 54.08) * mm});
            skLineSegment(sketch, "E166.4.2.2", {"start": v(-119.86, 54.08) * mm, "end": v(-115.23, 54.08) * mm});
            skLineSegment(sketch, "E166.4.2.3", {"start": v(-115.23, 58.7) * mm, "end": v(-115.23, 54.08) * mm});
            skLineSegment(sketch, "E166.4.3.0", {"start": v(-119.86, 46) * mm, "end": v(-115.23, 46) * mm});
            skLineSegment(sketch, "E166.4.3.1", {"start": v(-119.86, 46) * mm, "end": v(-119.86, 41.38) * mm});
            skLineSegment(sketch, "E166.4.3.2", {"start": v(-119.86, 41.38) * mm, "end": v(-115.23, 41.38) * mm});
            skLineSegment(sketch, "E166.4.3.3", {"start": v(-115.23, 46) * mm, "end": v(-115.23, 41.38) * mm});
            skLineSegment(sketch, "E166.4.4.0", {"start": v(-119.86, 33.3) * mm, "end": v(-115.23, 33.3) * mm});
            skLineSegment(sketch, "E166.4.4.1", {"start": v(-119.86, 33.3) * mm, "end": v(-119.86, 28.68) * mm});
            skLineSegment(sketch, "E166.4.4.2", {"start": v(-119.86, 28.68) * mm, "end": v(-115.23, 28.68) * mm});
            skLineSegment(sketch, "E166.4.4.3", {"start": v(-115.23, 33.3) * mm, "end": v(-115.23, 28.68) * mm});
            skLineSegment(sketch, "E166.4.5.0", {"start": v(-119.86, 20.6) * mm, "end": v(-115.23, 20.6) * mm});
            skLineSegment(sketch, "E166.4.5.1", {"start": v(-119.86, 20.6) * mm, "end": v(-119.86, 15.98) * mm});
            skLineSegment(sketch, "E166.4.5.2", {"start": v(-119.86, 15.98) * mm, "end": v(-115.23, 15.98) * mm});
            skLineSegment(sketch, "E166.4.5.3", {"start": v(-115.23, 20.6) * mm, "end": v(-115.23, 15.98) * mm});
            skLineSegment(sketch, "E166.4.6.0", {"start": v(-119.86, 7.9) * mm, "end": v(-115.23, 7.9) * mm});
            skLineSegment(sketch, "E166.4.6.1", {"start": v(-119.86, 7.9) * mm, "end": v(-119.86, 3.28) * mm});
            skLineSegment(sketch, "E166.4.6.2", {"start": v(-119.86, 3.28) * mm, "end": v(-115.23, 3.28) * mm});
            skLineSegment(sketch, "E166.4.6.3", {"start": v(-115.23, 7.9) * mm, "end": v(-115.23, 3.28) * mm});
            skLineSegment(sketch, "E166.4.7.0", {"start": v(-119.86, -4.8) * mm, "end": v(-115.23, -4.8) * mm});
            skLineSegment(sketch, "E166.4.7.1", {"start": v(-119.86, -4.8) * mm, "end": v(-119.86, -9.42) * mm});
            skLineSegment(sketch, "E166.4.7.2", {"start": v(-119.86, -9.42) * mm, "end": v(-115.23, -9.42) * mm});
            skLineSegment(sketch, "E166.4.7.3", {"start": v(-115.23, -4.8) * mm, "end": v(-115.23, -9.42) * mm});
            skLineSegment(sketch, "E166.4.8.0", {"start": v(-119.86, -17.5) * mm, "end": v(-115.23, -17.5) * mm});
            skLineSegment(sketch, "E166.4.8.1", {"start": v(-119.86, -17.5) * mm, "end": v(-119.86, -22.12) * mm});
            skLineSegment(sketch, "E166.4.8.2", {"start": v(-119.86, -22.12) * mm, "end": v(-115.23, -22.12) * mm});
            skLineSegment(sketch, "E166.4.8.3", {"start": v(-115.23, -17.5) * mm, "end": v(-115.23, -22.12) * mm});
            skLineSegment(sketch, "E166.4.9.0", {"start": v(-119.86, -30.2) * mm, "end": v(-115.23, -30.2) * mm});
            skLineSegment(sketch, "E166.4.9.1", {"start": v(-119.86, -30.2) * mm, "end": v(-119.86, -34.82) * mm});
            skLineSegment(sketch, "E166.4.9.2", {"start": v(-119.86, -34.82) * mm, "end": v(-115.23, -34.82) * mm});
            skLineSegment(sketch, "E166.4.9.3", {"start": v(-115.23, -30.2) * mm, "end": v(-115.23, -34.82) * mm});
            skLineSegment(sketch, "E166.4.10.0", {"start": v(-119.86, -42.9) * mm, "end": v(-115.23, -42.9) * mm});
            skLineSegment(sketch, "E166.4.10.1", {"start": v(-119.86, -42.9) * mm, "end": v(-119.86, -47.52) * mm});
            skLineSegment(sketch, "E166.4.10.2", {"start": v(-119.86, -47.52) * mm, "end": v(-115.23, -47.52) * mm});
            skLineSegment(sketch, "E166.4.10.3", {"start": v(-115.23, -42.9) * mm, "end": v(-115.23, -47.52) * mm});
            skLineSegment(sketch, "E166.4.12.0", {"start": v(-119.86, -68.3) * mm, "end": v(-115.23, -68.3) * mm});
            skLineSegment(sketch, "E166.4.12.1", {"start": v(-119.86, -68.3) * mm, "end": v(-119.86, -72.92) * mm});
            skLineSegment(sketch, "E166.4.12.2", {"start": v(-119.86, -72.92) * mm, "end": v(-115.23, -72.92) * mm});
            skLineSegment(sketch, "E166.4.12.3", {"start": v(-115.23, -68.3) * mm, "end": v(-115.23, -72.92) * mm});
            skLineSegment(sketch, "E166.5.0.0", {"start": v(-107.16, 84.1) * mm, "end": v(-102.53, 84.1) * mm});
            skLineSegment(sketch, "E166.5.0.1", {"start": v(-107.16, 84.1) * mm, "end": v(-107.16, 79.48) * mm});
            skLineSegment(sketch, "E166.5.0.2", {"start": v(-107.16, 79.48) * mm, "end": v(-102.53, 79.48) * mm});
            skLineSegment(sketch, "E166.5.0.3", {"start": v(-102.53, 84.1) * mm, "end": v(-102.53, 79.48) * mm});
            skLineSegment(sketch, "E166.5.1.0", {"start": v(-107.16, 71.4) * mm, "end": v(-102.53, 71.4) * mm});
            skLineSegment(sketch, "E166.5.1.1", {"start": v(-107.16, 71.4) * mm, "end": v(-107.16, 66.78) * mm});
            skLineSegment(sketch, "E166.5.1.2", {"start": v(-107.16, 66.78) * mm, "end": v(-102.53, 66.78) * mm});
            skLineSegment(sketch, "E166.5.1.3", {"start": v(-102.53, 71.4) * mm, "end": v(-102.53, 66.78) * mm});
            skLineSegment(sketch, "E166.5.2.0", {"start": v(-107.16, 58.7) * mm, "end": v(-102.53, 58.7) * mm});
            skLineSegment(sketch, "E166.5.2.1", {"start": v(-107.16, 58.7) * mm, "end": v(-107.16, 54.08) * mm});
            skLineSegment(sketch, "E166.5.2.2", {"start": v(-107.16, 54.08) * mm, "end": v(-102.53, 54.08) * mm});
            skLineSegment(sketch, "E166.5.2.3", {"start": v(-102.53, 58.7) * mm, "end": v(-102.53, 54.08) * mm});
            skLineSegment(sketch, "E166.5.3.0", {"start": v(-107.16, 46) * mm, "end": v(-102.53, 46) * mm});
            skLineSegment(sketch, "E166.5.3.1", {"start": v(-107.16, 46) * mm, "end": v(-107.16, 41.38) * mm});
            skLineSegment(sketch, "E166.5.3.2", {"start": v(-107.16, 41.38) * mm, "end": v(-102.53, 41.38) * mm});
            skLineSegment(sketch, "E166.5.3.3", {"start": v(-102.53, 46) * mm, "end": v(-102.53, 41.38) * mm});
            skLineSegment(sketch, "E166.5.4.0", {"start": v(-107.16, 33.3) * mm, "end": v(-102.53, 33.3) * mm});
            skLineSegment(sketch, "E166.5.4.1", {"start": v(-107.16, 33.3) * mm, "end": v(-107.16, 28.68) * mm});
            skLineSegment(sketch, "E166.5.4.2", {"start": v(-107.16, 28.68) * mm, "end": v(-102.53, 28.68) * mm});
            skLineSegment(sketch, "E166.5.4.3", {"start": v(-102.53, 33.3) * mm, "end": v(-102.53, 28.68) * mm});
            skLineSegment(sketch, "E166.5.5.0", {"start": v(-107.16, 20.6) * mm, "end": v(-102.53, 20.6) * mm});
            skLineSegment(sketch, "E166.5.5.1", {"start": v(-107.16, 20.6) * mm, "end": v(-107.16, 15.98) * mm});
            skLineSegment(sketch, "E166.5.5.2", {"start": v(-107.16, 15.98) * mm, "end": v(-102.53, 15.98) * mm});
            skLineSegment(sketch, "E166.5.5.3", {"start": v(-102.53, 20.6) * mm, "end": v(-102.53, 15.98) * mm});
            skLineSegment(sketch, "E166.5.6.0", {"start": v(-107.16, 7.9) * mm, "end": v(-102.53, 7.9) * mm});
            skLineSegment(sketch, "E166.5.6.1", {"start": v(-107.16, 7.9) * mm, "end": v(-107.16, 3.28) * mm});
            skLineSegment(sketch, "E166.5.6.2", {"start": v(-107.16, 3.28) * mm, "end": v(-102.53, 3.28) * mm});
            skLineSegment(sketch, "E166.5.6.3", {"start": v(-102.53, 7.9) * mm, "end": v(-102.53, 3.28) * mm});
            skLineSegment(sketch, "E166.5.7.0", {"start": v(-107.16, -4.8) * mm, "end": v(-102.53, -4.8) * mm});
            skLineSegment(sketch, "E166.5.7.1", {"start": v(-107.16, -4.8) * mm, "end": v(-107.16, -9.42) * mm});
            skLineSegment(sketch, "E166.5.7.2", {"start": v(-107.16, -9.42) * mm, "end": v(-102.53, -9.42) * mm});
            skLineSegment(sketch, "E166.5.7.3", {"start": v(-102.53, -4.8) * mm, "end": v(-102.53, -9.42) * mm});
            skLineSegment(sketch, "E166.5.8.0", {"start": v(-107.16, -17.5) * mm, "end": v(-102.53, -17.5) * mm});
            skLineSegment(sketch, "E166.5.8.1", {"start": v(-107.16, -17.5) * mm, "end": v(-107.16, -22.12) * mm});
            skLineSegment(sketch, "E166.5.8.2", {"start": v(-107.16, -22.12) * mm, "end": v(-102.53, -22.12) * mm});
            skLineSegment(sketch, "E166.5.8.3", {"start": v(-102.53, -17.5) * mm, "end": v(-102.53, -22.12) * mm});
            skLineSegment(sketch, "E166.5.9.0", {"start": v(-107.16, -30.2) * mm, "end": v(-102.53, -30.2) * mm});
            skLineSegment(sketch, "E166.5.9.1", {"start": v(-107.16, -30.2) * mm, "end": v(-107.16, -34.82) * mm});
            skLineSegment(sketch, "E166.5.9.2", {"start": v(-107.16, -34.82) * mm, "end": v(-102.53, -34.82) * mm});
            skLineSegment(sketch, "E166.5.9.3", {"start": v(-102.53, -30.2) * mm, "end": v(-102.53, -34.82) * mm});
            skLineSegment(sketch, "E166.5.10.0", {"start": v(-107.16, -42.9) * mm, "end": v(-102.53, -42.9) * mm});
            skLineSegment(sketch, "E166.5.10.1", {"start": v(-107.16, -42.9) * mm, "end": v(-107.16, -47.52) * mm});
            skLineSegment(sketch, "E166.5.10.2", {"start": v(-107.16, -47.52) * mm, "end": v(-102.53, -47.52) * mm});
            skLineSegment(sketch, "E166.5.10.3", {"start": v(-102.53, -42.9) * mm, "end": v(-102.53, -47.52) * mm});
            skLineSegment(sketch, "E166.5.11.0", {"start": v(-107.16, -55.6) * mm, "end": v(-102.53, -55.6) * mm});
            skLineSegment(sketch, "E166.5.11.1", {"start": v(-107.16, -55.6) * mm, "end": v(-107.16, -60.22) * mm});
            skLineSegment(sketch, "E166.5.11.2", {"start": v(-107.16, -60.22) * mm, "end": v(-102.53, -60.22) * mm});
            skLineSegment(sketch, "E166.5.11.3", {"start": v(-102.53, -55.6) * mm, "end": v(-102.53, -60.22) * mm});
            skLineSegment(sketch, "E166.5.12.0", {"start": v(-107.16, -68.3) * mm, "end": v(-102.53, -68.3) * mm});
            skLineSegment(sketch, "E166.5.12.1", {"start": v(-107.16, -68.3) * mm, "end": v(-107.16, -72.92) * mm});
            skLineSegment(sketch, "E166.5.12.2", {"start": v(-107.16, -72.92) * mm, "end": v(-102.53, -72.92) * mm});
            skLineSegment(sketch, "E166.5.12.3", {"start": v(-102.53, -68.3) * mm, "end": v(-102.53, -72.92) * mm});
            skLineSegment(sketch, "E166.6.0.0", {"start": v(-94.46, 84.1) * mm, "end": v(-89.83, 84.1) * mm});
            skLineSegment(sketch, "E166.6.0.1", {"start": v(-94.46, 84.1) * mm, "end": v(-94.46, 79.48) * mm});
            skLineSegment(sketch, "E166.6.0.2", {"start": v(-94.46, 79.48) * mm, "end": v(-89.83, 79.48) * mm});
            skLineSegment(sketch, "E166.6.0.3", {"start": v(-89.83, 84.1) * mm, "end": v(-89.83, 79.48) * mm});
            skLineSegment(sketch, "E166.6.1.0", {"start": v(-94.46, 71.4) * mm, "end": v(-89.83, 71.4) * mm});
            skLineSegment(sketch, "E166.6.1.1", {"start": v(-94.46, 71.4) * mm, "end": v(-94.46, 66.78) * mm});
            skLineSegment(sketch, "E166.6.1.2", {"start": v(-94.46, 66.78) * mm, "end": v(-89.83, 66.78) * mm});
            skLineSegment(sketch, "E166.6.1.3", {"start": v(-89.83, 71.4) * mm, "end": v(-89.83, 66.78) * mm});
            skLineSegment(sketch, "E166.6.2.0", {"start": v(-94.46, 58.7) * mm, "end": v(-89.83, 58.7) * mm});
            skLineSegment(sketch, "E166.6.2.1", {"start": v(-94.46, 58.7) * mm, "end": v(-94.46, 54.08) * mm});
            skLineSegment(sketch, "E166.6.2.2", {"start": v(-94.46, 54.08) * mm, "end": v(-89.83, 54.08) * mm});
            skLineSegment(sketch, "E166.6.2.3", {"start": v(-89.83, 58.7) * mm, "end": v(-89.83, 54.08) * mm});
            skLineSegment(sketch, "E166.6.3.0", {"start": v(-94.46, 46) * mm, "end": v(-89.83, 46) * mm});
            skLineSegment(sketch, "E166.6.3.1", {"start": v(-94.46, 46) * mm, "end": v(-94.46, 41.38) * mm});
            skLineSegment(sketch, "E166.6.3.2", {"start": v(-94.46, 41.38) * mm, "end": v(-89.83, 41.38) * mm});
            skLineSegment(sketch, "E166.6.3.3", {"start": v(-89.83, 46) * mm, "end": v(-89.83, 41.38) * mm});
            skLineSegment(sketch, "E166.6.4.0", {"start": v(-94.46, 33.3) * mm, "end": v(-89.83, 33.3) * mm});
            skLineSegment(sketch, "E166.6.4.1", {"start": v(-94.46, 33.3) * mm, "end": v(-94.46, 28.68) * mm});
            skLineSegment(sketch, "E166.6.4.2", {"start": v(-94.46, 28.68) * mm, "end": v(-89.83, 28.68) * mm});
            skLineSegment(sketch, "E166.6.4.3", {"start": v(-89.83, 33.3) * mm, "end": v(-89.83, 28.68) * mm});
            skLineSegment(sketch, "E166.6.5.0", {"start": v(-94.46, 20.6) * mm, "end": v(-89.83, 20.6) * mm});
            skLineSegment(sketch, "E166.6.5.1", {"start": v(-94.46, 20.6) * mm, "end": v(-94.46, 15.98) * mm});
            skLineSegment(sketch, "E166.6.5.2", {"start": v(-94.46, 15.98) * mm, "end": v(-89.83, 15.98) * mm});
            skLineSegment(sketch, "E166.6.5.3", {"start": v(-89.83, 20.6) * mm, "end": v(-89.83, 15.98) * mm});
            skLineSegment(sketch, "E166.6.6.0", {"start": v(-94.46, 7.9) * mm, "end": v(-89.83, 7.9) * mm});
            skLineSegment(sketch, "E166.6.6.1", {"start": v(-94.46, 7.9) * mm, "end": v(-94.46, 3.28) * mm});
            skLineSegment(sketch, "E166.6.6.2", {"start": v(-94.46, 3.28) * mm, "end": v(-89.83, 3.28) * mm});
            skLineSegment(sketch, "E166.6.6.3", {"start": v(-89.83, 7.9) * mm, "end": v(-89.83, 3.28) * mm});
            skLineSegment(sketch, "E166.6.7.0", {"start": v(-94.46, -4.8) * mm, "end": v(-89.83, -4.8) * mm});
            skLineSegment(sketch, "E166.6.7.1", {"start": v(-94.46, -4.8) * mm, "end": v(-94.46, -9.42) * mm});
            skLineSegment(sketch, "E166.6.7.2", {"start": v(-94.46, -9.42) * mm, "end": v(-89.83, -9.42) * mm});
            skLineSegment(sketch, "E166.6.7.3", {"start": v(-89.83, -4.8) * mm, "end": v(-89.83, -9.42) * mm});
            skLineSegment(sketch, "E166.6.8.0", {"start": v(-94.46, -17.5) * mm, "end": v(-89.83, -17.5) * mm});
            skLineSegment(sketch, "E166.6.8.1", {"start": v(-94.46, -17.5) * mm, "end": v(-94.46, -22.12) * mm});
            skLineSegment(sketch, "E166.6.8.2", {"start": v(-94.46, -22.12) * mm, "end": v(-89.83, -22.12) * mm});
            skLineSegment(sketch, "E166.6.8.3", {"start": v(-89.83, -17.5) * mm, "end": v(-89.83, -22.12) * mm});
            skLineSegment(sketch, "E166.6.9.0", {"start": v(-94.46, -30.2) * mm, "end": v(-89.83, -30.2) * mm});
            skLineSegment(sketch, "E166.6.9.1", {"start": v(-94.46, -30.2) * mm, "end": v(-94.46, -34.82) * mm});
            skLineSegment(sketch, "E166.6.9.2", {"start": v(-94.46, -34.82) * mm, "end": v(-89.83, -34.82) * mm});
            skLineSegment(sketch, "E166.6.9.3", {"start": v(-89.83, -30.2) * mm, "end": v(-89.83, -34.82) * mm});
            skLineSegment(sketch, "E166.6.10.0", {"start": v(-94.46, -42.9) * mm, "end": v(-89.83, -42.9) * mm});
            skLineSegment(sketch, "E166.6.10.1", {"start": v(-94.46, -42.9) * mm, "end": v(-94.46, -47.52) * mm});
            skLineSegment(sketch, "E166.6.10.2", {"start": v(-94.46, -47.52) * mm, "end": v(-89.83, -47.52) * mm});
            skLineSegment(sketch, "E166.6.10.3", {"start": v(-89.83, -42.9) * mm, "end": v(-89.83, -47.52) * mm});
            skLineSegment(sketch, "E166.6.11.0", {"start": v(-94.46, -55.6) * mm, "end": v(-89.83, -55.6) * mm});
            skLineSegment(sketch, "E166.6.11.1", {"start": v(-94.46, -55.6) * mm, "end": v(-94.46, -60.22) * mm});
            skLineSegment(sketch, "E166.6.11.2", {"start": v(-94.46, -60.22) * mm, "end": v(-89.83, -60.22) * mm});
            skLineSegment(sketch, "E166.6.11.3", {"start": v(-89.83, -55.6) * mm, "end": v(-89.83, -60.22) * mm});
            skLineSegment(sketch, "E166.6.12.0", {"start": v(-94.46, -68.3) * mm, "end": v(-89.83, -68.3) * mm});
            skLineSegment(sketch, "E166.6.12.1", {"start": v(-94.46, -68.3) * mm, "end": v(-94.46, -72.92) * mm});
            skLineSegment(sketch, "E166.6.12.2", {"start": v(-94.46, -72.92) * mm, "end": v(-89.83, -72.92) * mm});
            skLineSegment(sketch, "E166.6.12.3", {"start": v(-89.83, -68.3) * mm, "end": v(-89.83, -72.92) * mm});
            skLineSegment(sketch, "E166.7.0.0", {"start": v(-81.76, 84.1) * mm, "end": v(-77.13, 84.1) * mm});
            skLineSegment(sketch, "E166.7.0.1", {"start": v(-81.76, 84.1) * mm, "end": v(-81.76, 79.48) * mm});
            skLineSegment(sketch, "E166.7.0.2", {"start": v(-81.76, 79.48) * mm, "end": v(-77.13, 79.48) * mm});
            skLineSegment(sketch, "E166.7.0.3", {"start": v(-77.13, 84.1) * mm, "end": v(-77.13, 79.48) * mm});
            skLineSegment(sketch, "E166.7.1.0", {"start": v(-81.76, 71.4) * mm, "end": v(-77.13, 71.4) * mm});
            skLineSegment(sketch, "E166.7.1.1", {"start": v(-81.76, 71.4) * mm, "end": v(-81.76, 66.78) * mm});
            skLineSegment(sketch, "E166.7.1.2", {"start": v(-81.76, 66.78) * mm, "end": v(-77.13, 66.78) * mm});
            skLineSegment(sketch, "E166.7.1.3", {"start": v(-77.13, 71.4) * mm, "end": v(-77.13, 66.78) * mm});
            skLineSegment(sketch, "E166.7.2.0", {"start": v(-81.76, 58.7) * mm, "end": v(-77.13, 58.7) * mm});
            skLineSegment(sketch, "E166.7.2.1", {"start": v(-81.76, 58.7) * mm, "end": v(-81.76, 54.08) * mm});
            skLineSegment(sketch, "E166.7.2.2", {"start": v(-81.76, 54.08) * mm, "end": v(-77.13, 54.08) * mm});
            skLineSegment(sketch, "E166.7.2.3", {"start": v(-77.13, 58.7) * mm, "end": v(-77.13, 54.08) * mm});
            skLineSegment(sketch, "E166.7.3.0", {"start": v(-81.76, 46) * mm, "end": v(-77.13, 46) * mm});
            skLineSegment(sketch, "E166.7.3.1", {"start": v(-81.76, 46) * mm, "end": v(-81.76, 41.38) * mm});
            skLineSegment(sketch, "E166.7.3.2", {"start": v(-81.76, 41.38) * mm, "end": v(-77.13, 41.38) * mm});
            skLineSegment(sketch, "E166.7.3.3", {"start": v(-77.13, 46) * mm, "end": v(-77.13, 41.38) * mm});
            skLineSegment(sketch, "E166.7.4.0", {"start": v(-81.76, 33.3) * mm, "end": v(-77.13, 33.3) * mm});
            skLineSegment(sketch, "E166.7.4.1", {"start": v(-81.76, 33.3) * mm, "end": v(-81.76, 28.68) * mm});
            skLineSegment(sketch, "E166.7.4.2", {"start": v(-81.76, 28.68) * mm, "end": v(-77.13, 28.68) * mm});
            skLineSegment(sketch, "E166.7.5.0", {"start": v(-81.76, 20.6) * mm, "end": v(-77.13, 20.6) * mm});
            skLineSegment(sketch, "E166.7.5.1", {"start": v(-81.76, 20.6) * mm, "end": v(-81.76, 15.98) * mm});
            skLineSegment(sketch, "E166.7.5.2", {"start": v(-81.76, 15.98) * mm, "end": v(-77.13, 15.98) * mm});
            skLineSegment(sketch, "E166.7.5.3", {"start": v(-77.13, 20.6) * mm, "end": v(-77.13, 15.98) * mm});
            skLineSegment(sketch, "E166.7.6.0", {"start": v(-81.76, 7.9) * mm, "end": v(-77.13, 7.9) * mm});
            skLineSegment(sketch, "E166.7.6.1", {"start": v(-81.76, 7.9) * mm, "end": v(-81.76, 3.28) * mm});
            skLineSegment(sketch, "E166.7.6.2", {"start": v(-81.76, 3.28) * mm, "end": v(-77.13, 3.28) * mm});
            skLineSegment(sketch, "E166.7.6.3", {"start": v(-77.13, 7.9) * mm, "end": v(-77.13, 3.28) * mm});
            skLineSegment(sketch, "E166.7.7.0", {"start": v(-81.76, -4.8) * mm, "end": v(-77.13, -4.8) * mm});
            skLineSegment(sketch, "E166.7.7.1", {"start": v(-81.76, -4.8) * mm, "end": v(-81.76, -9.42) * mm});
            skLineSegment(sketch, "E166.7.7.2", {"start": v(-81.76, -9.42) * mm, "end": v(-77.13, -9.42) * mm});
            skLineSegment(sketch, "E166.7.7.3", {"start": v(-77.13, -4.8) * mm, "end": v(-77.13, -9.42) * mm});
            skLineSegment(sketch, "E166.7.8.0", {"start": v(-81.76, -17.5) * mm, "end": v(-77.13, -17.5) * mm});
            skLineSegment(sketch, "E166.7.8.1", {"start": v(-81.76, -17.5) * mm, "end": v(-81.76, -22.12) * mm});
            skLineSegment(sketch, "E166.7.8.2", {"start": v(-81.76, -22.12) * mm, "end": v(-77.13, -22.12) * mm});
            skLineSegment(sketch, "E166.7.8.3", {"start": v(-77.13, -17.5) * mm, "end": v(-77.13, -22.12) * mm});
            skLineSegment(sketch, "E166.7.9.0", {"start": v(-81.76, -30.2) * mm, "end": v(-77.13, -30.2) * mm});
            skLineSegment(sketch, "E166.7.9.1", {"start": v(-81.76, -30.2) * mm, "end": v(-81.76, -34.82) * mm});
            skLineSegment(sketch, "E166.7.9.2", {"start": v(-81.76, -34.82) * mm, "end": v(-77.13, -34.82) * mm});
            skLineSegment(sketch, "E166.7.9.3", {"start": v(-77.13, -30.2) * mm, "end": v(-77.13, -34.82) * mm});
            skLineSegment(sketch, "E166.7.10.0", {"start": v(-81.76, -42.9) * mm, "end": v(-77.13, -42.9) * mm});
            skLineSegment(sketch, "E166.7.10.1", {"start": v(-81.76, -42.9) * mm, "end": v(-81.76, -47.52) * mm});
            skLineSegment(sketch, "E166.7.10.2", {"start": v(-81.76, -47.52) * mm, "end": v(-77.13, -47.52) * mm});
            skLineSegment(sketch, "E166.7.10.3", {"start": v(-77.13, -42.9) * mm, "end": v(-77.13, -47.52) * mm});
            skLineSegment(sketch, "E166.7.11.0", {"start": v(-81.76, -55.6) * mm, "end": v(-77.13, -55.6) * mm});
            skLineSegment(sketch, "E166.7.11.1", {"start": v(-81.76, -55.6) * mm, "end": v(-81.76, -60.22) * mm});
            skLineSegment(sketch, "E166.7.11.2", {"start": v(-81.76, -60.22) * mm, "end": v(-77.13, -60.22) * mm});
            skLineSegment(sketch, "E166.7.11.3", {"start": v(-77.13, -55.6) * mm, "end": v(-77.13, -60.22) * mm});
            skLineSegment(sketch, "E166.7.12.0", {"start": v(-81.76, -68.3) * mm, "end": v(-77.13, -68.3) * mm});
            skLineSegment(sketch, "E166.7.12.1", {"start": v(-81.76, -68.3) * mm, "end": v(-81.76, -72.92) * mm});
            skLineSegment(sketch, "E166.7.12.2", {"start": v(-81.76, -72.92) * mm, "end": v(-77.13, -72.92) * mm});
            skLineSegment(sketch, "E166.7.12.3", {"start": v(-77.13, -68.3) * mm, "end": v(-77.13, -72.92) * mm});
            skLineSegment(sketch, "E166.8.0.0", {"start": v(-69.06, 84.1) * mm, "end": v(-64.43, 84.1) * mm});
            skLineSegment(sketch, "E166.8.0.1", {"start": v(-69.06, 84.1) * mm, "end": v(-69.06, 79.48) * mm});
            skLineSegment(sketch, "E166.8.0.2", {"start": v(-69.06, 79.48) * mm, "end": v(-64.43, 79.48) * mm});
            skLineSegment(sketch, "E166.8.0.3", {"start": v(-64.43, 84.1) * mm, "end": v(-64.43, 79.48) * mm});
            skLineSegment(sketch, "E166.8.1.0", {"start": v(-69.06, 71.4) * mm, "end": v(-64.43, 71.4) * mm});
            skLineSegment(sketch, "E166.8.1.1", {"start": v(-69.06, 71.4) * mm, "end": v(-69.06, 66.78) * mm});
            skLineSegment(sketch, "E166.8.1.2", {"start": v(-69.06, 66.78) * mm, "end": v(-64.43, 66.78) * mm});
            skLineSegment(sketch, "E166.8.1.3", {"start": v(-64.43, 71.4) * mm, "end": v(-64.43, 66.78) * mm});
            skLineSegment(sketch, "E166.8.2.0", {"start": v(-69.06, 58.7) * mm, "end": v(-64.43, 58.7) * mm});
            skLineSegment(sketch, "E166.8.2.1", {"start": v(-69.06, 58.7) * mm, "end": v(-69.06, 54.08) * mm});
            skLineSegment(sketch, "E166.8.2.2", {"start": v(-69.06, 54.08) * mm, "end": v(-64.43, 54.08) * mm});
            skLineSegment(sketch, "E166.8.2.3", {"start": v(-64.43, 58.7) * mm, "end": v(-64.43, 54.08) * mm});
            skLineSegment(sketch, "E166.8.3.0", {"start": v(-69.06, 46) * mm, "end": v(-64.43, 46) * mm});
            skLineSegment(sketch, "E166.8.3.1", {"start": v(-69.06, 46) * mm, "end": v(-69.06, 41.38) * mm});
            skLineSegment(sketch, "E166.8.3.2", {"start": v(-69.06, 41.38) * mm, "end": v(-64.43, 41.38) * mm});
            skLineSegment(sketch, "E166.8.3.3", {"start": v(-64.43, 46) * mm, "end": v(-64.43, 41.38) * mm});
            skLineSegment(sketch, "E166.8.5.1", {"start": v(-69.06, 20.6) * mm, "end": v(-69.06, 15.98) * mm});
            skLineSegment(sketch, "E166.8.5.2", {"start": v(-69.06, 15.98) * mm, "end": v(-64.43, 15.98) * mm});
            skLineSegment(sketch, "E166.8.5.3", {"start": v(-64.43, 20.6) * mm, "end": v(-64.43, 15.98) * mm});
            skLineSegment(sketch, "E166.8.6.0", {"start": v(-69.06, 7.9) * mm, "end": v(-64.43, 7.9) * mm});
            skLineSegment(sketch, "E166.8.6.1", {"start": v(-69.06, 7.9) * mm, "end": v(-69.06, 3.28) * mm});
            skLineSegment(sketch, "E166.8.6.2", {"start": v(-69.06, 3.28) * mm, "end": v(-64.43, 3.28) * mm});
            skLineSegment(sketch, "E166.8.6.3", {"start": v(-64.43, 7.9) * mm, "end": v(-64.43, 3.28) * mm});
            skLineSegment(sketch, "E166.8.7.0", {"start": v(-69.06, -4.8) * mm, "end": v(-64.43, -4.8) * mm});
            skLineSegment(sketch, "E166.8.7.1", {"start": v(-69.06, -4.8) * mm, "end": v(-69.06, -9.42) * mm});
            skLineSegment(sketch, "E166.8.7.2", {"start": v(-69.06, -9.42) * mm, "end": v(-64.43, -9.42) * mm});
            skLineSegment(sketch, "E166.8.7.3", {"start": v(-64.43, -4.8) * mm, "end": v(-64.43, -9.42) * mm});
            skLineSegment(sketch, "E166.8.8.0", {"start": v(-69.06, -17.5) * mm, "end": v(-64.43, -17.5) * mm});
            skLineSegment(sketch, "E166.8.8.1", {"start": v(-69.06, -17.5) * mm, "end": v(-69.06, -22.12) * mm});
            skLineSegment(sketch, "E166.8.8.2", {"start": v(-69.06, -22.12) * mm, "end": v(-64.43, -22.12) * mm});
            skLineSegment(sketch, "E166.8.8.3", {"start": v(-64.43, -17.5) * mm, "end": v(-64.43, -22.12) * mm});
            skLineSegment(sketch, "E166.8.9.0", {"start": v(-69.06, -30.2) * mm, "end": v(-64.43, -30.2) * mm});
            skLineSegment(sketch, "E166.8.9.1", {"start": v(-69.06, -30.2) * mm, "end": v(-69.06, -34.82) * mm});
            skLineSegment(sketch, "E166.8.9.2", {"start": v(-69.06, -34.82) * mm, "end": v(-64.43, -34.82) * mm});
            skLineSegment(sketch, "E166.8.9.3", {"start": v(-64.43, -30.2) * mm, "end": v(-64.43, -34.82) * mm});
            skLineSegment(sketch, "E166.8.10.0", {"start": v(-69.06, -42.9) * mm, "end": v(-64.43, -42.9) * mm});
            skLineSegment(sketch, "E166.8.10.1", {"start": v(-69.06, -42.9) * mm, "end": v(-69.06, -47.52) * mm});
            skLineSegment(sketch, "E166.8.10.2", {"start": v(-69.06, -47.52) * mm, "end": v(-64.43, -47.52) * mm});
            skLineSegment(sketch, "E166.8.10.3", {"start": v(-64.43, -42.9) * mm, "end": v(-64.43, -47.52) * mm});
            skLineSegment(sketch, "E166.8.11.0", {"start": v(-69.06, -55.6) * mm, "end": v(-64.43, -55.6) * mm});
            skLineSegment(sketch, "E166.8.11.1", {"start": v(-69.06, -55.6) * mm, "end": v(-69.06, -60.22) * mm});
            skLineSegment(sketch, "E166.8.11.2", {"start": v(-69.06, -60.22) * mm, "end": v(-64.43, -60.22) * mm});
            skLineSegment(sketch, "E166.8.11.3", {"start": v(-64.43, -55.6) * mm, "end": v(-64.43, -60.22) * mm});
            skLineSegment(sketch, "E166.8.12.0", {"start": v(-69.06, -68.3) * mm, "end": v(-64.43, -68.3) * mm});
            skLineSegment(sketch, "E166.8.12.1", {"start": v(-69.06, -68.3) * mm, "end": v(-69.06, -72.92) * mm});
            skLineSegment(sketch, "E166.8.12.2", {"start": v(-69.06, -72.92) * mm, "end": v(-64.43, -72.92) * mm});
            skLineSegment(sketch, "E166.8.12.3", {"start": v(-64.43, -68.3) * mm, "end": v(-64.43, -72.92) * mm});
            skLineSegment(sketch, "E166.9.0.0", {"start": v(-56.36, 84.1) * mm, "end": v(-51.73, 84.1) * mm});
            skLineSegment(sketch, "E166.9.0.1", {"start": v(-56.36, 84.1) * mm, "end": v(-56.36, 79.48) * mm});
            skLineSegment(sketch, "E166.9.0.2", {"start": v(-56.36, 79.48) * mm, "end": v(-51.73, 79.48) * mm});
            skLineSegment(sketch, "E166.9.0.3", {"start": v(-51.73, 84.1) * mm, "end": v(-51.73, 79.48) * mm});
            skLineSegment(sketch, "E166.9.1.0", {"start": v(-56.36, 71.4) * mm, "end": v(-51.73, 71.4) * mm});
            skLineSegment(sketch, "E166.9.1.1", {"start": v(-56.36, 71.4) * mm, "end": v(-56.36, 66.78) * mm});
            skLineSegment(sketch, "E166.9.1.2", {"start": v(-56.36, 66.78) * mm, "end": v(-51.73, 66.78) * mm});
            skLineSegment(sketch, "E166.9.1.3", {"start": v(-51.73, 71.4) * mm, "end": v(-51.73, 66.78) * mm});
            skLineSegment(sketch, "E166.9.2.0", {"start": v(-56.36, 58.7) * mm, "end": v(-51.73, 58.7) * mm});
            skLineSegment(sketch, "E166.9.2.1", {"start": v(-56.36, 58.7) * mm, "end": v(-56.36, 54.08) * mm});
            skLineSegment(sketch, "E166.9.2.2", {"start": v(-56.36, 54.08) * mm, "end": v(-51.73, 54.08) * mm});
            skLineSegment(sketch, "E166.9.2.3", {"start": v(-51.73, 58.7) * mm, "end": v(-51.73, 54.08) * mm});
            skLineSegment(sketch, "E166.9.3.0", {"start": v(-56.36, 46) * mm, "end": v(-51.73, 46) * mm});
            skLineSegment(sketch, "E166.9.3.1", {"start": v(-56.36, 46) * mm, "end": v(-56.36, 41.38) * mm});
            skLineSegment(sketch, "E166.9.3.2", {"start": v(-56.36, 41.38) * mm, "end": v(-51.73, 41.38) * mm});
            skLineSegment(sketch, "E166.9.3.3", {"start": v(-51.73, 46) * mm, "end": v(-51.73, 41.38) * mm});
            skLineSegment(sketch, "E166.9.5.1", {"start": v(-56.36, 20.6) * mm, "end": v(-56.36, 15.98) * mm});
            skLineSegment(sketch, "E166.9.5.2", {"start": v(-56.36, 15.98) * mm, "end": v(-51.73, 15.98) * mm});
            skLineSegment(sketch, "E166.9.5.3", {"start": v(-51.73, 20.6) * mm, "end": v(-51.73, 15.98) * mm});
            skLineSegment(sketch, "E166.9.6.0", {"start": v(-56.36, 7.9) * mm, "end": v(-51.73, 7.9) * mm});
            skLineSegment(sketch, "E166.9.6.1", {"start": v(-56.36, 7.9) * mm, "end": v(-56.36, 3.28) * mm});
            skLineSegment(sketch, "E166.9.6.2", {"start": v(-56.36, 3.28) * mm, "end": v(-51.73, 3.28) * mm});
            skLineSegment(sketch, "E166.9.6.3", {"start": v(-51.73, 7.9) * mm, "end": v(-51.73, 3.28) * mm});
            skLineSegment(sketch, "E166.9.7.0", {"start": v(-56.36, -4.8) * mm, "end": v(-51.73, -4.8) * mm});
            skLineSegment(sketch, "E166.9.7.1", {"start": v(-56.36, -4.8) * mm, "end": v(-56.36, -9.42) * mm});
            skLineSegment(sketch, "E166.9.7.2", {"start": v(-56.36, -9.42) * mm, "end": v(-51.73, -9.42) * mm});
            skLineSegment(sketch, "E166.9.7.3", {"start": v(-51.73, -4.8) * mm, "end": v(-51.73, -9.42) * mm});
            skLineSegment(sketch, "E166.9.8.0", {"start": v(-56.36, -17.5) * mm, "end": v(-51.73, -17.5) * mm});
            skLineSegment(sketch, "E166.9.8.1", {"start": v(-56.36, -17.5) * mm, "end": v(-56.36, -22.12) * mm});
            skLineSegment(sketch, "E166.9.8.2", {"start": v(-56.36, -22.12) * mm, "end": v(-51.73, -22.12) * mm});
            skLineSegment(sketch, "E166.9.8.3", {"start": v(-51.73, -17.5) * mm, "end": v(-51.73, -22.12) * mm});
            skLineSegment(sketch, "E166.9.9.0", {"start": v(-56.36, -30.2) * mm, "end": v(-51.73, -30.2) * mm});
            skLineSegment(sketch, "E166.9.9.1", {"start": v(-56.36, -30.2) * mm, "end": v(-56.36, -34.82) * mm});
            skLineSegment(sketch, "E166.9.9.2", {"start": v(-56.36, -34.82) * mm, "end": v(-51.73, -34.82) * mm});
            skLineSegment(sketch, "E166.9.9.3", {"start": v(-51.73, -30.2) * mm, "end": v(-51.73, -34.82) * mm});
            skLineSegment(sketch, "E166.9.10.0", {"start": v(-56.36, -42.9) * mm, "end": v(-51.73, -42.9) * mm});
            skLineSegment(sketch, "E166.9.10.1", {"start": v(-56.36, -42.9) * mm, "end": v(-56.36, -47.52) * mm});
            skLineSegment(sketch, "E166.9.10.2", {"start": v(-56.36, -47.52) * mm, "end": v(-51.73, -47.52) * mm});
            skLineSegment(sketch, "E166.9.10.3", {"start": v(-51.73, -42.9) * mm, "end": v(-51.73, -47.52) * mm});
            skLineSegment(sketch, "E166.9.11.0", {"start": v(-56.36, -55.6) * mm, "end": v(-51.73, -55.6) * mm});
            skLineSegment(sketch, "E166.9.11.1", {"start": v(-56.36, -55.6) * mm, "end": v(-56.36, -60.22) * mm});
            skLineSegment(sketch, "E166.9.11.2", {"start": v(-56.36, -60.22) * mm, "end": v(-51.73, -60.22) * mm});
            skLineSegment(sketch, "E166.9.11.3", {"start": v(-51.73, -55.6) * mm, "end": v(-51.73, -60.22) * mm});
            skLineSegment(sketch, "E166.9.12.0", {"start": v(-56.36, -68.3) * mm, "end": v(-51.73, -68.3) * mm});
            skLineSegment(sketch, "E166.9.12.1", {"start": v(-56.36, -68.3) * mm, "end": v(-56.36, -72.92) * mm});
            skLineSegment(sketch, "E166.9.12.2", {"start": v(-56.36, -72.92) * mm, "end": v(-51.73, -72.92) * mm});
            skLineSegment(sketch, "E166.9.12.3", {"start": v(-51.73, -68.3) * mm, "end": v(-51.73, -72.92) * mm});
            skLineSegment(sketch, "E166.10.0.0", {"start": v(-43.66, 84.1) * mm, "end": v(-39.03, 84.1) * mm});
            skLineSegment(sketch, "E166.10.0.1", {"start": v(-43.66, 84.1) * mm, "end": v(-43.66, 79.48) * mm});
            skLineSegment(sketch, "E166.10.0.2", {"start": v(-43.66, 79.48) * mm, "end": v(-39.03, 79.48) * mm});
            skLineSegment(sketch, "E166.10.0.3", {"start": v(-39.03, 84.1) * mm, "end": v(-39.03, 79.48) * mm});
            skLineSegment(sketch, "E166.10.1.0", {"start": v(-43.66, 71.4) * mm, "end": v(-39.03, 71.4) * mm});
            skLineSegment(sketch, "E166.10.1.1", {"start": v(-43.66, 71.4) * mm, "end": v(-43.66, 66.78) * mm});
            skLineSegment(sketch, "E166.10.1.2", {"start": v(-43.66, 66.78) * mm, "end": v(-39.03, 66.78) * mm});
            skLineSegment(sketch, "E166.10.1.3", {"start": v(-39.03, 71.4) * mm, "end": v(-39.03, 66.78) * mm});
            skLineSegment(sketch, "E166.10.2.0", {"start": v(-43.66, 58.7) * mm, "end": v(-39.03, 58.7) * mm});
            skLineSegment(sketch, "E166.10.2.1", {"start": v(-43.66, 58.7) * mm, "end": v(-43.66, 54.08) * mm});
            skLineSegment(sketch, "E166.10.2.2", {"start": v(-43.66, 54.08) * mm, "end": v(-39.03, 54.08) * mm});
            skLineSegment(sketch, "E166.10.2.3", {"start": v(-39.03, 58.7) * mm, "end": v(-39.03, 54.08) * mm});
            skLineSegment(sketch, "E166.10.3.0", {"start": v(-43.66, 46) * mm, "end": v(-39.03, 46) * mm});
            skLineSegment(sketch, "E166.10.3.1", {"start": v(-43.66, 46) * mm, "end": v(-43.66, 41.38) * mm});
            skLineSegment(sketch, "E166.10.3.2", {"start": v(-43.66, 41.38) * mm, "end": v(-39.03, 41.38) * mm});
            skLineSegment(sketch, "E166.10.3.3", {"start": v(-39.03, 46) * mm, "end": v(-39.03, 41.38) * mm});
            skLineSegment(sketch, "E166.10.5.1", {"start": v(-43.66, 20.6) * mm, "end": v(-43.66, 15.98) * mm});
            skLineSegment(sketch, "E166.10.5.2", {"start": v(-43.66, 15.98) * mm, "end": v(-39.03, 15.98) * mm});
            skLineSegment(sketch, "E166.10.5.3", {"start": v(-39.03, 20.6) * mm, "end": v(-39.03, 15.98) * mm});
            skLineSegment(sketch, "E166.10.6.0", {"start": v(-43.66, 7.9) * mm, "end": v(-39.03, 7.9) * mm});
            skLineSegment(sketch, "E166.10.6.1", {"start": v(-43.66, 7.9) * mm, "end": v(-43.66, 3.28) * mm});
            skLineSegment(sketch, "E166.10.6.2", {"start": v(-43.66, 3.28) * mm, "end": v(-39.03, 3.28) * mm});
            skLineSegment(sketch, "E166.10.6.3", {"start": v(-39.03, 7.9) * mm, "end": v(-39.03, 3.28) * mm});
            skLineSegment(sketch, "E166.10.7.0", {"start": v(-43.66, -4.8) * mm, "end": v(-39.03, -4.8) * mm});
            skLineSegment(sketch, "E166.10.7.1", {"start": v(-43.66, -4.8) * mm, "end": v(-43.66, -9.42) * mm});
            skLineSegment(sketch, "E166.10.7.2", {"start": v(-43.66, -9.42) * mm, "end": v(-39.03, -9.42) * mm});
            skLineSegment(sketch, "E166.10.7.3", {"start": v(-39.03, -4.8) * mm, "end": v(-39.03, -9.42) * mm});
            skLineSegment(sketch, "E166.10.8.0", {"start": v(-43.66, -17.5) * mm, "end": v(-39.03, -17.5) * mm});
            skLineSegment(sketch, "E166.10.8.1", {"start": v(-43.66, -17.5) * mm, "end": v(-43.66, -22.12) * mm});
            skLineSegment(sketch, "E166.10.8.2", {"start": v(-43.66, -22.12) * mm, "end": v(-39.03, -22.12) * mm});
            skLineSegment(sketch, "E166.10.8.3", {"start": v(-39.03, -17.5) * mm, "end": v(-39.03, -22.12) * mm});
            skLineSegment(sketch, "E166.10.9.0", {"start": v(-43.66, -30.2) * mm, "end": v(-39.03, -30.2) * mm});
            skLineSegment(sketch, "E166.10.9.1", {"start": v(-43.66, -30.2) * mm, "end": v(-43.66, -34.82) * mm});
            skLineSegment(sketch, "E166.10.9.2", {"start": v(-43.66, -34.82) * mm, "end": v(-39.03, -34.82) * mm});
            skLineSegment(sketch, "E166.10.9.3", {"start": v(-39.03, -30.2) * mm, "end": v(-39.03, -34.82) * mm});
            skLineSegment(sketch, "E166.10.10.0", {"start": v(-43.66, -42.9) * mm, "end": v(-39.03, -42.9) * mm});
            skLineSegment(sketch, "E166.10.10.1", {"start": v(-43.66, -42.9) * mm, "end": v(-43.66, -47.52) * mm});
            skLineSegment(sketch, "E166.10.10.2", {"start": v(-43.66, -47.52) * mm, "end": v(-39.03, -47.52) * mm});
            skLineSegment(sketch, "E166.10.10.3", {"start": v(-39.03, -42.9) * mm, "end": v(-39.03, -47.52) * mm});
            skLineSegment(sketch, "E166.10.11.0", {"start": v(-43.66, -55.6) * mm, "end": v(-39.03, -55.6) * mm});
            skLineSegment(sketch, "E166.10.11.1", {"start": v(-43.66, -55.6) * mm, "end": v(-43.66, -60.22) * mm});
            skLineSegment(sketch, "E166.10.11.2", {"start": v(-43.66, -60.22) * mm, "end": v(-39.03, -60.22) * mm});
            skLineSegment(sketch, "E166.10.11.3", {"start": v(-39.03, -55.6) * mm, "end": v(-39.03, -60.22) * mm});
            skLineSegment(sketch, "E166.10.12.0", {"start": v(-43.66, -68.3) * mm, "end": v(-39.03, -68.3) * mm});
            skLineSegment(sketch, "E166.10.12.1", {"start": v(-43.66, -68.3) * mm, "end": v(-43.66, -72.92) * mm});
            skLineSegment(sketch, "E166.10.12.2", {"start": v(-43.66, -72.92) * mm, "end": v(-39.03, -72.92) * mm});
            skLineSegment(sketch, "E166.10.12.3", {"start": v(-39.03, -68.3) * mm, "end": v(-39.03, -72.92) * mm});
            skLineSegment(sketch, "E166.11.0.0", {"start": v(-30.96, 84.1) * mm, "end": v(-26.33, 84.1) * mm});
            skLineSegment(sketch, "E166.11.0.1", {"start": v(-30.96, 84.1) * mm, "end": v(-30.96, 79.48) * mm});
            skLineSegment(sketch, "E166.11.0.2", {"start": v(-30.96, 79.48) * mm, "end": v(-26.33, 79.48) * mm});
            skLineSegment(sketch, "E166.11.0.3", {"start": v(-26.33, 84.1) * mm, "end": v(-26.33, 79.48) * mm});
            skLineSegment(sketch, "E166.11.1.0", {"start": v(-30.96, 71.4) * mm, "end": v(-26.33, 71.4) * mm});
            skLineSegment(sketch, "E166.11.1.1", {"start": v(-30.96, 71.4) * mm, "end": v(-30.96, 66.78) * mm});
            skLineSegment(sketch, "E166.11.1.2", {"start": v(-30.96, 66.78) * mm, "end": v(-26.33, 66.78) * mm});
            skLineSegment(sketch, "E166.11.1.3", {"start": v(-26.33, 71.4) * mm, "end": v(-26.33, 66.78) * mm});
            skLineSegment(sketch, "E166.11.2.0", {"start": v(-30.96, 58.7) * mm, "end": v(-26.33, 58.7) * mm});
            skLineSegment(sketch, "E166.11.2.1", {"start": v(-30.96, 58.7) * mm, "end": v(-30.96, 54.08) * mm});
            skLineSegment(sketch, "E166.11.2.2", {"start": v(-30.96, 54.08) * mm, "end": v(-26.33, 54.08) * mm});
            skLineSegment(sketch, "E166.11.2.3", {"start": v(-26.33, 58.7) * mm, "end": v(-26.33, 54.08) * mm});
            skLineSegment(sketch, "E166.11.3.0", {"start": v(-30.96, 46) * mm, "end": v(-26.33, 46) * mm});
            skLineSegment(sketch, "E166.11.3.1", {"start": v(-30.96, 46) * mm, "end": v(-30.96, 41.38) * mm});
            skLineSegment(sketch, "E166.11.3.2", {"start": v(-30.96, 41.38) * mm, "end": v(-26.33, 41.38) * mm});
            skLineSegment(sketch, "E166.11.3.3", {"start": v(-26.33, 46) * mm, "end": v(-26.33, 41.38) * mm});
            skLineSegment(sketch, "E166.11.5.1", {"start": v(-30.96, 20.6) * mm, "end": v(-30.96, 15.98) * mm});
            skLineSegment(sketch, "E166.11.5.2", {"start": v(-30.96, 15.98) * mm, "end": v(-26.33, 15.98) * mm});
            skLineSegment(sketch, "E166.11.5.3", {"start": v(-26.33, 20.6) * mm, "end": v(-26.33, 15.98) * mm});
            skLineSegment(sketch, "E166.11.6.0", {"start": v(-30.96, 7.9) * mm, "end": v(-26.33, 7.9) * mm});
            skLineSegment(sketch, "E166.11.6.1", {"start": v(-30.96, 7.9) * mm, "end": v(-30.96, 3.28) * mm});
            skLineSegment(sketch, "E166.11.6.2", {"start": v(-30.96, 3.28) * mm, "end": v(-26.33, 3.28) * mm});
            skLineSegment(sketch, "E166.11.6.3", {"start": v(-26.33, 7.9) * mm, "end": v(-26.33, 3.28) * mm});
            skLineSegment(sketch, "E166.11.7.0", {"start": v(-30.96, -4.8) * mm, "end": v(-26.33, -4.8) * mm});
            skLineSegment(sketch, "E166.11.7.1", {"start": v(-30.96, -4.8) * mm, "end": v(-30.96, -9.42) * mm});
            skLineSegment(sketch, "E166.11.7.2", {"start": v(-30.96, -9.42) * mm, "end": v(-26.33, -9.42) * mm});
            skLineSegment(sketch, "E166.11.7.3", {"start": v(-26.33, -4.8) * mm, "end": v(-26.33, -9.42) * mm});
            skLineSegment(sketch, "E166.11.8.0", {"start": v(-30.96, -17.5) * mm, "end": v(-26.33, -17.5) * mm});
            skLineSegment(sketch, "E166.11.8.1", {"start": v(-30.96, -17.5) * mm, "end": v(-30.96, -22.12) * mm});
            skLineSegment(sketch, "E166.11.8.2", {"start": v(-30.96, -22.12) * mm, "end": v(-26.33, -22.12) * mm});
            skLineSegment(sketch, "E166.11.8.3", {"start": v(-26.33, -17.5) * mm, "end": v(-26.33, -22.12) * mm});
            skLineSegment(sketch, "E166.11.9.0", {"start": v(-30.96, -30.2) * mm, "end": v(-26.33, -30.2) * mm});
            skLineSegment(sketch, "E166.11.9.1", {"start": v(-30.96, -30.2) * mm, "end": v(-30.96, -34.82) * mm});
            skLineSegment(sketch, "E166.11.9.2", {"start": v(-30.96, -34.82) * mm, "end": v(-26.33, -34.82) * mm});
            skLineSegment(sketch, "E166.11.9.3", {"start": v(-26.33, -30.2) * mm, "end": v(-26.33, -34.82) * mm});
            skLineSegment(sketch, "E166.11.10.0", {"start": v(-30.96, -42.9) * mm, "end": v(-26.33, -42.9) * mm});
            skLineSegment(sketch, "E166.11.10.1", {"start": v(-30.96, -42.9) * mm, "end": v(-30.96, -47.52) * mm});
            skLineSegment(sketch, "E166.11.10.2", {"start": v(-30.96, -47.52) * mm, "end": v(-26.33, -47.52) * mm});
            skLineSegment(sketch, "E166.11.10.3", {"start": v(-26.33, -42.9) * mm, "end": v(-26.33, -47.52) * mm});
            skLineSegment(sketch, "E166.11.11.0", {"start": v(-30.96, -55.6) * mm, "end": v(-26.33, -55.6) * mm});
            skLineSegment(sketch, "E166.11.11.1", {"start": v(-30.96, -55.6) * mm, "end": v(-30.96, -60.22) * mm});
            skLineSegment(sketch, "E166.11.11.2", {"start": v(-30.96, -60.22) * mm, "end": v(-26.33, -60.22) * mm});
            skLineSegment(sketch, "E166.11.11.3", {"start": v(-26.33, -55.6) * mm, "end": v(-26.33, -60.22) * mm});
            skLineSegment(sketch, "E166.11.12.0", {"start": v(-30.96, -68.3) * mm, "end": v(-26.33, -68.3) * mm});
            skLineSegment(sketch, "E166.11.12.1", {"start": v(-30.96, -68.3) * mm, "end": v(-30.96, -72.92) * mm});
            skLineSegment(sketch, "E166.11.12.2", {"start": v(-30.96, -72.92) * mm, "end": v(-26.33, -72.92) * mm});
            skLineSegment(sketch, "E166.11.12.3", {"start": v(-26.33, -68.3) * mm, "end": v(-26.33, -72.92) * mm});
            skLineSegment(sketch, "E166.12.0.0", {"start": v(-18.26, 84.1) * mm, "end": v(-13.63, 84.1) * mm});
            skLineSegment(sketch, "E166.12.0.1", {"start": v(-18.26, 84.1) * mm, "end": v(-18.26, 79.48) * mm});
            skLineSegment(sketch, "E166.12.0.2", {"start": v(-18.26, 79.48) * mm, "end": v(-13.63, 79.48) * mm});
            skLineSegment(sketch, "E166.12.0.3", {"start": v(-13.63, 84.1) * mm, "end": v(-13.63, 79.48) * mm});
            skLineSegment(sketch, "E166.12.1.0", {"start": v(-18.26, 71.4) * mm, "end": v(-13.63, 71.4) * mm});
            skLineSegment(sketch, "E166.12.1.1", {"start": v(-18.26, 71.4) * mm, "end": v(-18.26, 66.78) * mm});
            skLineSegment(sketch, "E166.12.1.2", {"start": v(-18.26, 66.78) * mm, "end": v(-13.63, 66.78) * mm});
            skLineSegment(sketch, "E166.12.1.3", {"start": v(-13.63, 71.4) * mm, "end": v(-13.63, 66.78) * mm});
            skLineSegment(sketch, "E166.12.2.0", {"start": v(-18.26, 58.7) * mm, "end": v(-13.63, 58.7) * mm});
            skLineSegment(sketch, "E166.12.2.1", {"start": v(-18.26, 58.7) * mm, "end": v(-18.26, 54.08) * mm});
            skLineSegment(sketch, "E166.12.2.2", {"start": v(-18.26, 54.08) * mm, "end": v(-13.63, 54.08) * mm});
            skLineSegment(sketch, "E166.12.2.3", {"start": v(-13.63, 58.7) * mm, "end": v(-13.63, 54.08) * mm});
            skLineSegment(sketch, "E166.12.3.0", {"start": v(-18.26, 46) * mm, "end": v(-13.63, 46) * mm});
            skLineSegment(sketch, "E166.12.3.1", {"start": v(-18.26, 46) * mm, "end": v(-18.26, 41.38) * mm});
            skLineSegment(sketch, "E166.12.3.2", {"start": v(-18.26, 41.38) * mm, "end": v(-13.63, 41.38) * mm});
            skLineSegment(sketch, "E166.12.3.3", {"start": v(-13.63, 46) * mm, "end": v(-13.63, 41.38) * mm});
            skLineSegment(sketch, "E166.12.5.1", {"start": v(-18.26, 20.6) * mm, "end": v(-18.26, 15.98) * mm});
            skLineSegment(sketch, "E166.12.5.2", {"start": v(-18.26, 15.98) * mm, "end": v(-13.63, 15.98) * mm});
            skLineSegment(sketch, "E166.12.5.3", {"start": v(-13.63, 20.6) * mm, "end": v(-13.63, 15.98) * mm});
            skLineSegment(sketch, "E166.12.6.0", {"start": v(-18.26, 7.9) * mm, "end": v(-13.63, 7.9) * mm});
            skLineSegment(sketch, "E166.12.6.1", {"start": v(-18.26, 7.9) * mm, "end": v(-18.26, 3.28) * mm});
            skLineSegment(sketch, "E166.12.6.2", {"start": v(-18.26, 3.28) * mm, "end": v(-13.63, 3.28) * mm});
            skLineSegment(sketch, "E166.12.6.3", {"start": v(-13.63, 7.9) * mm, "end": v(-13.63, 3.28) * mm});
            skLineSegment(sketch, "E166.12.7.0", {"start": v(-18.26, -4.8) * mm, "end": v(-13.63, -4.8) * mm});
            skLineSegment(sketch, "E166.12.7.1", {"start": v(-18.26, -4.8) * mm, "end": v(-18.26, -9.42) * mm});
            skLineSegment(sketch, "E166.12.7.2", {"start": v(-18.26, -9.42) * mm, "end": v(-13.63, -9.42) * mm});
            skLineSegment(sketch, "E166.12.7.3", {"start": v(-13.63, -4.8) * mm, "end": v(-13.63, -9.42) * mm});
            skLineSegment(sketch, "E166.12.8.0", {"start": v(-18.26, -17.5) * mm, "end": v(-13.63, -17.5) * mm});
            skLineSegment(sketch, "E166.12.8.1", {"start": v(-18.26, -17.5) * mm, "end": v(-18.26, -22.12) * mm});
            skLineSegment(sketch, "E166.12.8.2", {"start": v(-18.26, -22.12) * mm, "end": v(-13.63, -22.12) * mm});
            skLineSegment(sketch, "E166.12.8.3", {"start": v(-13.63, -17.5) * mm, "end": v(-13.63, -22.12) * mm});
            skLineSegment(sketch, "E166.12.9.0", {"start": v(-18.26, -30.2) * mm, "end": v(-13.63, -30.2) * mm});
            skLineSegment(sketch, "E166.12.9.1", {"start": v(-18.26, -30.2) * mm, "end": v(-18.26, -34.82) * mm});
            skLineSegment(sketch, "E166.12.9.2", {"start": v(-18.26, -34.82) * mm, "end": v(-13.63, -34.82) * mm});
            skLineSegment(sketch, "E166.12.9.3", {"start": v(-13.63, -30.2) * mm, "end": v(-13.63, -34.82) * mm});
            skLineSegment(sketch, "E166.12.10.0", {"start": v(-18.26, -42.9) * mm, "end": v(-13.63, -42.9) * mm});
            skLineSegment(sketch, "E166.12.10.1", {"start": v(-18.26, -42.9) * mm, "end": v(-18.26, -47.52) * mm});
            skLineSegment(sketch, "E166.12.10.2", {"start": v(-18.26, -47.52) * mm, "end": v(-13.63, -47.52) * mm});
            skLineSegment(sketch, "E166.12.10.3", {"start": v(-13.63, -42.9) * mm, "end": v(-13.63, -47.52) * mm});
            skLineSegment(sketch, "E166.12.11.0", {"start": v(-18.26, -55.6) * mm, "end": v(-13.63, -55.6) * mm});
            skLineSegment(sketch, "E166.12.11.1", {"start": v(-18.26, -55.6) * mm, "end": v(-18.26, -60.22) * mm});
            skLineSegment(sketch, "E166.12.11.2", {"start": v(-18.26, -60.22) * mm, "end": v(-13.63, -60.22) * mm});
            skLineSegment(sketch, "E166.12.11.3", {"start": v(-13.63, -55.6) * mm, "end": v(-13.63, -60.22) * mm});
            skLineSegment(sketch, "E166.12.12.0", {"start": v(-18.26, -68.3) * mm, "end": v(-13.63, -68.3) * mm});
            skLineSegment(sketch, "E166.12.12.1", {"start": v(-18.26, -68.3) * mm, "end": v(-18.26, -72.92) * mm});
            skLineSegment(sketch, "E166.12.12.2", {"start": v(-18.26, -72.92) * mm, "end": v(-13.63, -72.92) * mm});
            skLineSegment(sketch, "E166.12.12.3", {"start": v(-13.63, -68.3) * mm, "end": v(-13.63, -72.92) * mm});
            skLineSegment(sketch, "E166.13.0.0", {"start": v(-5.56, 84.1) * mm, "end": v(-0.93, 84.1) * mm});
            skLineSegment(sketch, "E166.13.0.1", {"start": v(-5.56, 84.1) * mm, "end": v(-5.56, 79.48) * mm});
            skLineSegment(sketch, "E166.13.0.2", {"start": v(-5.56, 79.48) * mm, "end": v(-0.93, 79.48) * mm});
            skLineSegment(sketch, "E166.13.0.3", {"start": v(-0.93, 84.1) * mm, "end": v(-0.93, 79.48) * mm});
            skLineSegment(sketch, "E166.13.1.0", {"start": v(-5.56, 71.4) * mm, "end": v(-0.93, 71.4) * mm});
            skLineSegment(sketch, "E166.13.1.1", {"start": v(-5.56, 71.4) * mm, "end": v(-5.56, 66.78) * mm});
            skLineSegment(sketch, "E166.13.1.2", {"start": v(-5.56, 66.78) * mm, "end": v(-0.93, 66.78) * mm});
            skLineSegment(sketch, "E166.13.1.3", {"start": v(-0.93, 71.4) * mm, "end": v(-0.93, 66.78) * mm});
            skLineSegment(sketch, "E166.13.2.0", {"start": v(-5.56, 58.7) * mm, "end": v(-0.93, 58.7) * mm});
            skLineSegment(sketch, "E166.13.2.1", {"start": v(-5.56, 58.7) * mm, "end": v(-5.56, 54.08) * mm});
            skLineSegment(sketch, "E166.13.2.2", {"start": v(-5.56, 54.08) * mm, "end": v(-0.93, 54.08) * mm});
            skLineSegment(sketch, "E166.13.2.3", {"start": v(-0.93, 58.7) * mm, "end": v(-0.93, 54.08) * mm});
            skLineSegment(sketch, "E166.13.3.0", {"start": v(-5.56, 46) * mm, "end": v(-0.93, 46) * mm});
            skLineSegment(sketch, "E166.13.3.1", {"start": v(-5.56, 46) * mm, "end": v(-5.56, 41.38) * mm});
            skLineSegment(sketch, "E166.13.3.2", {"start": v(-5.56, 41.38) * mm, "end": v(-0.93, 41.38) * mm});
            skLineSegment(sketch, "E166.13.3.3", {"start": v(-0.93, 46) * mm, "end": v(-0.93, 41.38) * mm});
            skLineSegment(sketch, "E166.13.4.0", {"start": v(-5.56, 33.3) * mm, "end": v(-0.93, 33.3) * mm});
            skLineSegment(sketch, "E166.13.4.1", {"start": v(-5.56, 33.3) * mm, "end": v(-5.56, 28.68) * mm});
            skLineSegment(sketch, "E166.13.4.2", {"start": v(-5.56, 28.68) * mm, "end": v(-0.93, 28.68) * mm});
            skLineSegment(sketch, "E166.13.4.3", {"start": v(-0.93, 33.3) * mm, "end": v(-0.93, 28.68) * mm});
            skLineSegment(sketch, "E166.13.5.0", {"start": v(-5.56, 20.6) * mm, "end": v(-0.93, 20.6) * mm});
            skLineSegment(sketch, "E166.13.5.1", {"start": v(-5.56, 20.6) * mm, "end": v(-5.56, 15.98) * mm});
            skLineSegment(sketch, "E166.13.5.2", {"start": v(-5.56, 15.98) * mm, "end": v(-0.93, 15.98) * mm});
            skLineSegment(sketch, "E166.13.5.3", {"start": v(-0.93, 20.6) * mm, "end": v(-0.93, 15.98) * mm});
            skLineSegment(sketch, "E166.13.6.0", {"start": v(-5.56, 7.9) * mm, "end": v(-0.93, 7.9) * mm});
            skLineSegment(sketch, "E166.13.6.1", {"start": v(-5.56, 7.9) * mm, "end": v(-5.56, 3.28) * mm});
            skLineSegment(sketch, "E166.13.6.2", {"start": v(-5.56, 3.28) * mm, "end": v(-0.93, 3.28) * mm});
            skLineSegment(sketch, "E166.13.6.3", {"start": v(-0.93, 7.9) * mm, "end": v(-0.93, 3.28) * mm});
            skLineSegment(sketch, "E166.13.7.0", {"start": v(-5.56, -4.8) * mm, "end": v(-0.93, -4.8) * mm});
            skLineSegment(sketch, "E166.13.7.1", {"start": v(-5.56, -4.8) * mm, "end": v(-5.56, -9.42) * mm});
            skLineSegment(sketch, "E166.13.7.2", {"start": v(-5.56, -9.42) * mm, "end": v(-0.93, -9.42) * mm});
            skLineSegment(sketch, "E166.13.7.3", {"start": v(-0.93, -4.8) * mm, "end": v(-0.93, -9.42) * mm});
            skLineSegment(sketch, "E166.13.8.0", {"start": v(-5.56, -17.5) * mm, "end": v(-0.93, -17.5) * mm});
            skLineSegment(sketch, "E166.13.8.1", {"start": v(-5.56, -17.5) * mm, "end": v(-5.56, -22.12) * mm});
            skLineSegment(sketch, "E166.13.8.2", {"start": v(-5.56, -22.12) * mm, "end": v(-0.93, -22.12) * mm});
            skLineSegment(sketch, "E166.13.8.3", {"start": v(-0.93, -17.5) * mm, "end": v(-0.93, -22.12) * mm});
            skLineSegment(sketch, "E166.13.9.0", {"start": v(-5.56, -30.2) * mm, "end": v(-0.93, -30.2) * mm});
            skLineSegment(sketch, "E166.13.9.1", {"start": v(-5.56, -30.2) * mm, "end": v(-5.56, -34.82) * mm});
            skLineSegment(sketch, "E166.13.9.2", {"start": v(-5.56, -34.82) * mm, "end": v(-0.93, -34.82) * mm});
            skLineSegment(sketch, "E166.13.9.3", {"start": v(-0.93, -30.2) * mm, "end": v(-0.93, -34.82) * mm});
            skLineSegment(sketch, "E166.13.10.0", {"start": v(-5.56, -42.9) * mm, "end": v(-0.93, -42.9) * mm});
            skLineSegment(sketch, "E166.13.10.1", {"start": v(-5.56, -42.9) * mm, "end": v(-5.56, -47.52) * mm});
            skLineSegment(sketch, "E166.13.10.2", {"start": v(-5.56, -47.52) * mm, "end": v(-0.93, -47.52) * mm});
            skLineSegment(sketch, "E166.13.10.3", {"start": v(-0.93, -42.9) * mm, "end": v(-0.93, -47.52) * mm});
            skLineSegment(sketch, "E166.13.11.0", {"start": v(-5.56, -55.6) * mm, "end": v(-0.93, -55.6) * mm});
            skLineSegment(sketch, "E166.13.11.1", {"start": v(-5.56, -55.6) * mm, "end": v(-5.56, -60.22) * mm});
            skLineSegment(sketch, "E166.13.11.2", {"start": v(-5.56, -60.22) * mm, "end": v(-0.93, -60.22) * mm});
            skLineSegment(sketch, "E166.13.11.3", {"start": v(-0.93, -55.6) * mm, "end": v(-0.93, -60.22) * mm});
            skLineSegment(sketch, "E166.13.12.0", {"start": v(-5.56, -68.3) * mm, "end": v(-0.93, -68.3) * mm});
            skLineSegment(sketch, "E166.13.12.1", {"start": v(-5.56, -68.3) * mm, "end": v(-5.56, -72.92) * mm});
            skLineSegment(sketch, "E166.13.12.2", {"start": v(-5.56, -72.92) * mm, "end": v(-0.93, -72.92) * mm});
            skLineSegment(sketch, "E166.13.12.3", {"start": v(-0.93, -68.3) * mm, "end": v(-0.93, -72.92) * mm});
            skLineSegment(sketch, "E166.14.0.0", {"start": v(7.14, 84.1) * mm, "end": v(11.77, 84.1) * mm});
            skLineSegment(sketch, "E166.14.0.1", {"start": v(7.14, 84.1) * mm, "end": v(7.14, 79.48) * mm});
            skLineSegment(sketch, "E166.14.0.2", {"start": v(7.14, 79.48) * mm, "end": v(11.77, 79.48) * mm});
            skLineSegment(sketch, "E166.14.0.3", {"start": v(11.77, 84.1) * mm, "end": v(11.77, 79.48) * mm});
            skLineSegment(sketch, "E166.14.1.0", {"start": v(7.14, 71.4) * mm, "end": v(11.77, 71.4) * mm});
            skLineSegment(sketch, "E166.14.1.1", {"start": v(7.14, 71.4) * mm, "end": v(7.14, 66.78) * mm});
            skLineSegment(sketch, "E166.14.1.2", {"start": v(7.14, 66.78) * mm, "end": v(11.77, 66.78) * mm});
            skLineSegment(sketch, "E166.14.1.3", {"start": v(11.77, 71.4) * mm, "end": v(11.77, 66.78) * mm});
            skLineSegment(sketch, "E166.14.2.0", {"start": v(7.14, 58.7) * mm, "end": v(11.77, 58.7) * mm});
            skLineSegment(sketch, "E166.14.2.1", {"start": v(7.14, 58.7) * mm, "end": v(7.14, 54.08) * mm});
            skLineSegment(sketch, "E166.14.2.2", {"start": v(7.14, 54.08) * mm, "end": v(11.77, 54.08) * mm});
            skLineSegment(sketch, "E166.14.2.3", {"start": v(11.77, 58.7) * mm, "end": v(11.77, 54.08) * mm});
            skLineSegment(sketch, "E166.14.3.0", {"start": v(7.14, 46) * mm, "end": v(11.77, 46) * mm});
            skLineSegment(sketch, "E166.14.3.1", {"start": v(7.14, 46) * mm, "end": v(7.14, 41.38) * mm});
            skLineSegment(sketch, "E166.14.3.2", {"start": v(7.14, 41.38) * mm, "end": v(11.77, 41.38) * mm});
            skLineSegment(sketch, "E166.14.3.3", {"start": v(11.77, 46) * mm, "end": v(11.77, 41.38) * mm});
            skLineSegment(sketch, "E166.14.4.0", {"start": v(7.14, 33.3) * mm, "end": v(11.77, 33.3) * mm});
            skLineSegment(sketch, "E166.14.4.1", {"start": v(7.14, 33.3) * mm, "end": v(7.14, 28.68) * mm});
            skLineSegment(sketch, "E166.14.4.2", {"start": v(7.14, 28.68) * mm, "end": v(11.77, 28.68) * mm});
            skLineSegment(sketch, "E166.14.4.3", {"start": v(11.77, 33.3) * mm, "end": v(11.77, 28.68) * mm});
            skLineSegment(sketch, "E166.14.5.0", {"start": v(7.14, 20.6) * mm, "end": v(11.77, 20.6) * mm});
            skLineSegment(sketch, "E166.14.5.1", {"start": v(7.14, 20.6) * mm, "end": v(7.14, 15.98) * mm});
            skLineSegment(sketch, "E166.14.5.2", {"start": v(7.14, 15.98) * mm, "end": v(11.77, 15.98) * mm});
            skLineSegment(sketch, "E166.14.5.3", {"start": v(11.77, 20.6) * mm, "end": v(11.77, 15.98) * mm});
            skLineSegment(sketch, "E166.14.6.0", {"start": v(7.14, 7.9) * mm, "end": v(11.77, 7.9) * mm});
            skLineSegment(sketch, "E166.14.6.1", {"start": v(7.14, 7.9) * mm, "end": v(7.14, 3.28) * mm});
            skLineSegment(sketch, "E166.14.6.2", {"start": v(7.14, 3.28) * mm, "end": v(11.77, 3.28) * mm});
            skLineSegment(sketch, "E166.14.6.3", {"start": v(11.77, 7.9) * mm, "end": v(11.77, 3.28) * mm});
            skLineSegment(sketch, "E166.14.7.0", {"start": v(7.14, -4.8) * mm, "end": v(11.77, -4.8) * mm});
            skLineSegment(sketch, "E166.14.7.1", {"start": v(7.14, -4.8) * mm, "end": v(7.14, -9.42) * mm});
            skLineSegment(sketch, "E166.14.7.2", {"start": v(7.14, -9.42) * mm, "end": v(11.77, -9.42) * mm});
            skLineSegment(sketch, "E166.14.7.3", {"start": v(11.77, -4.8) * mm, "end": v(11.77, -9.42) * mm});
            skLineSegment(sketch, "E166.14.8.0", {"start": v(7.14, -17.5) * mm, "end": v(11.77, -17.5) * mm});
            skLineSegment(sketch, "E166.14.8.1", {"start": v(7.14, -17.5) * mm, "end": v(7.14, -22.12) * mm});
            skLineSegment(sketch, "E166.14.8.2", {"start": v(7.14, -22.12) * mm, "end": v(11.77, -22.12) * mm});
            skLineSegment(sketch, "E166.14.8.3", {"start": v(11.77, -17.5) * mm, "end": v(11.77, -22.12) * mm});
            skLineSegment(sketch, "E166.14.9.0", {"start": v(7.14, -30.2) * mm, "end": v(11.77, -30.2) * mm});
            skLineSegment(sketch, "E166.14.9.1", {"start": v(7.14, -30.2) * mm, "end": v(7.14, -34.82) * mm});
            skLineSegment(sketch, "E166.14.9.2", {"start": v(7.14, -34.82) * mm, "end": v(11.77, -34.82) * mm});
            skLineSegment(sketch, "E166.14.9.3", {"start": v(11.77, -30.2) * mm, "end": v(11.77, -34.82) * mm});
            skLineSegment(sketch, "E166.14.10.0", {"start": v(7.14, -42.9) * mm, "end": v(11.77, -42.9) * mm});
            skLineSegment(sketch, "E166.14.10.1", {"start": v(7.14, -42.9) * mm, "end": v(7.14, -47.52) * mm});
            skLineSegment(sketch, "E166.14.10.2", {"start": v(7.14, -47.52) * mm, "end": v(11.77, -47.52) * mm});
            skLineSegment(sketch, "E166.14.10.3", {"start": v(11.77, -42.9) * mm, "end": v(11.77, -47.52) * mm});
            skLineSegment(sketch, "E166.14.11.0", {"start": v(7.14, -55.6) * mm, "end": v(11.77, -55.6) * mm});
            skLineSegment(sketch, "E166.14.11.1", {"start": v(7.14, -55.6) * mm, "end": v(7.14, -60.22) * mm});
            skLineSegment(sketch, "E166.14.11.2", {"start": v(7.14, -60.22) * mm, "end": v(11.77, -60.22) * mm});
            skLineSegment(sketch, "E166.14.11.3", {"start": v(11.77, -55.6) * mm, "end": v(11.77, -60.22) * mm});
            skLineSegment(sketch, "E166.14.12.0", {"start": v(7.14, -68.3) * mm, "end": v(11.77, -68.3) * mm});
            skLineSegment(sketch, "E166.14.12.1", {"start": v(7.14, -68.3) * mm, "end": v(7.14, -72.92) * mm});
            skLineSegment(sketch, "E166.14.12.2", {"start": v(7.14, -72.92) * mm, "end": v(11.77, -72.92) * mm});
            skLineSegment(sketch, "E166.14.12.3", {"start": v(11.77, -68.3) * mm, "end": v(11.77, -72.92) * mm});
            skLineSegment(sketch, "E166.15.0.0", {"start": v(19.84, 84.1) * mm, "end": v(24.47, 84.1) * mm});
            skLineSegment(sketch, "E166.15.0.1", {"start": v(19.84, 84.1) * mm, "end": v(19.84, 79.48) * mm});
            skLineSegment(sketch, "E166.15.0.2", {"start": v(19.84, 79.48) * mm, "end": v(24.47, 79.48) * mm});
            skLineSegment(sketch, "E166.15.0.3", {"start": v(24.47, 84.1) * mm, "end": v(24.47, 79.48) * mm});
            skLineSegment(sketch, "E166.15.1.0", {"start": v(19.84, 71.4) * mm, "end": v(24.47, 71.4) * mm});
            skLineSegment(sketch, "E166.15.1.1", {"start": v(19.84, 71.4) * mm, "end": v(19.84, 66.78) * mm});
            skLineSegment(sketch, "E166.15.1.2", {"start": v(19.84, 66.78) * mm, "end": v(24.47, 66.78) * mm});
            skLineSegment(sketch, "E166.15.1.3", {"start": v(24.47, 71.4) * mm, "end": v(24.47, 66.78) * mm});
            skLineSegment(sketch, "E166.15.2.0", {"start": v(19.84, 58.7) * mm, "end": v(24.47, 58.7) * mm});
            skLineSegment(sketch, "E166.15.2.1", {"start": v(19.84, 58.7) * mm, "end": v(19.84, 54.08) * mm});
            skLineSegment(sketch, "E166.15.2.2", {"start": v(19.84, 54.08) * mm, "end": v(24.47, 54.08) * mm});
            skLineSegment(sketch, "E166.15.2.3", {"start": v(24.47, 58.7) * mm, "end": v(24.47, 54.08) * mm});
            skLineSegment(sketch, "E166.15.3.0", {"start": v(19.84, 46) * mm, "end": v(24.47, 46) * mm});
            skLineSegment(sketch, "E166.15.3.1", {"start": v(19.84, 46) * mm, "end": v(19.84, 41.38) * mm});
            skLineSegment(sketch, "E166.15.3.2", {"start": v(19.84, 41.38) * mm, "end": v(24.47, 41.38) * mm});
            skLineSegment(sketch, "E166.15.3.3", {"start": v(24.47, 46) * mm, "end": v(24.47, 41.38) * mm});
            skLineSegment(sketch, "E166.15.4.0", {"start": v(19.84, 33.3) * mm, "end": v(24.47, 33.3) * mm});
            skLineSegment(sketch, "E166.15.4.1", {"start": v(19.84, 33.3) * mm, "end": v(19.84, 28.68) * mm});
            skLineSegment(sketch, "E166.15.4.2", {"start": v(19.84, 28.68) * mm, "end": v(24.47, 28.68) * mm});
            skLineSegment(sketch, "E166.15.4.3", {"start": v(24.47, 33.3) * mm, "end": v(24.47, 28.68) * mm});
            skLineSegment(sketch, "E166.15.5.0", {"start": v(19.84, 20.6) * mm, "end": v(24.47, 20.6) * mm});
            skLineSegment(sketch, "E166.15.5.1", {"start": v(19.84, 20.6) * mm, "end": v(19.84, 15.98) * mm});
            skLineSegment(sketch, "E166.15.5.2", {"start": v(19.84, 15.98) * mm, "end": v(24.47, 15.98) * mm});
            skLineSegment(sketch, "E166.15.5.3", {"start": v(24.47, 20.6) * mm, "end": v(24.47, 15.98) * mm});
            skLineSegment(sketch, "E166.15.6.0", {"start": v(19.84, 7.9) * mm, "end": v(24.47, 7.9) * mm});
            skLineSegment(sketch, "E166.15.6.1", {"start": v(19.84, 7.9) * mm, "end": v(19.84, 3.28) * mm});
            skLineSegment(sketch, "E166.15.6.2", {"start": v(19.84, 3.28) * mm, "end": v(24.47, 3.28) * mm});
            skLineSegment(sketch, "E166.15.6.3", {"start": v(24.47, 7.9) * mm, "end": v(24.47, 3.28) * mm});
            skLineSegment(sketch, "E166.15.7.0", {"start": v(19.84, -4.8) * mm, "end": v(24.47, -4.8) * mm});
            skLineSegment(sketch, "E166.15.7.1", {"start": v(19.84, -4.8) * mm, "end": v(19.84, -9.42) * mm});
            skLineSegment(sketch, "E166.15.7.2", {"start": v(19.84, -9.42) * mm, "end": v(24.47, -9.42) * mm});
            skLineSegment(sketch, "E166.15.7.3", {"start": v(24.47, -4.8) * mm, "end": v(24.47, -9.42) * mm});
            skLineSegment(sketch, "E166.15.8.0", {"start": v(19.84, -17.5) * mm, "end": v(24.47, -17.5) * mm});
            skLineSegment(sketch, "E166.15.8.1", {"start": v(19.84, -17.5) * mm, "end": v(19.84, -22.12) * mm});
            skLineSegment(sketch, "E166.15.8.2", {"start": v(19.84, -22.12) * mm, "end": v(24.47, -22.12) * mm});
            skLineSegment(sketch, "E166.15.8.3", {"start": v(24.47, -17.5) * mm, "end": v(24.47, -22.12) * mm});
            skLineSegment(sketch, "E166.15.9.0", {"start": v(19.84, -30.2) * mm, "end": v(24.47, -30.2) * mm});
            skLineSegment(sketch, "E166.15.9.1", {"start": v(19.84, -30.2) * mm, "end": v(19.84, -34.82) * mm});
            skLineSegment(sketch, "E166.15.9.2", {"start": v(19.84, -34.82) * mm, "end": v(24.47, -34.82) * mm});
            skLineSegment(sketch, "E166.15.9.3", {"start": v(24.47, -30.2) * mm, "end": v(24.47, -34.82) * mm});
            skLineSegment(sketch, "E166.15.10.0", {"start": v(19.84, -42.9) * mm, "end": v(24.47, -42.9) * mm});
            skLineSegment(sketch, "E166.15.10.1", {"start": v(19.84, -42.9) * mm, "end": v(19.84, -47.52) * mm});
            skLineSegment(sketch, "E166.15.10.2", {"start": v(19.84, -47.52) * mm, "end": v(24.47, -47.52) * mm});
            skLineSegment(sketch, "E166.15.10.3", {"start": v(24.47, -42.9) * mm, "end": v(24.47, -47.52) * mm});
            skLineSegment(sketch, "E166.15.11.0", {"start": v(19.84, -55.6) * mm, "end": v(24.47, -55.6) * mm});
            skLineSegment(sketch, "E166.15.11.1", {"start": v(19.84, -55.6) * mm, "end": v(19.84, -60.22) * mm});
            skLineSegment(sketch, "E166.15.11.2", {"start": v(19.84, -60.22) * mm, "end": v(24.47, -60.22) * mm});
            skLineSegment(sketch, "E166.15.11.3", {"start": v(24.47, -55.6) * mm, "end": v(24.47, -60.22) * mm});
            skLineSegment(sketch, "E166.15.12.0", {"start": v(19.84, -68.3) * mm, "end": v(24.47, -68.3) * mm});
            skLineSegment(sketch, "E166.15.12.1", {"start": v(19.84, -68.3) * mm, "end": v(19.84, -72.92) * mm});
            skLineSegment(sketch, "E166.15.12.2", {"start": v(19.84, -72.92) * mm, "end": v(24.47, -72.92) * mm});
            skLineSegment(sketch, "E166.15.12.3", {"start": v(24.47, -68.3) * mm, "end": v(24.47, -72.92) * mm});
            skLineSegment(sketch, "E166.16.0.0", {"start": v(32.54, 84.1) * mm, "end": v(37.17, 84.1) * mm});
            skLineSegment(sketch, "E166.16.0.1", {"start": v(32.54, 84.1) * mm, "end": v(32.54, 79.48) * mm});
            skLineSegment(sketch, "E166.16.0.2", {"start": v(32.54, 79.48) * mm, "end": v(37.17, 79.48) * mm});
            skLineSegment(sketch, "E166.16.0.3", {"start": v(37.17, 84.1) * mm, "end": v(37.17, 79.48) * mm});
            skLineSegment(sketch, "E166.16.2.0", {"start": v(32.54, 58.7) * mm, "end": v(37.17, 58.7) * mm});
            skLineSegment(sketch, "E166.16.2.1", {"start": v(32.54, 58.7) * mm, "end": v(32.54, 54.08) * mm});
            skLineSegment(sketch, "E166.16.2.2", {"start": v(32.54, 54.08) * mm, "end": v(37.17, 54.08) * mm});
            skLineSegment(sketch, "E166.16.2.3", {"start": v(37.17, 58.7) * mm, "end": v(37.17, 54.08) * mm});
            skLineSegment(sketch, "E166.16.3.0", {"start": v(32.54, 46) * mm, "end": v(37.17, 46) * mm});
            skLineSegment(sketch, "E166.16.3.1", {"start": v(32.54, 46) * mm, "end": v(32.54, 41.38) * mm});
            skLineSegment(sketch, "E166.16.3.2", {"start": v(32.54, 41.38) * mm, "end": v(37.17, 41.38) * mm});
            skLineSegment(sketch, "E166.16.3.3", {"start": v(37.17, 46) * mm, "end": v(37.17, 41.38) * mm});
            skLineSegment(sketch, "E166.16.4.0", {"start": v(32.54, 33.3) * mm, "end": v(37.17, 33.3) * mm});
            skLineSegment(sketch, "E166.16.4.1", {"start": v(32.54, 33.3) * mm, "end": v(32.54, 28.68) * mm});
            skLineSegment(sketch, "E166.16.4.2", {"start": v(32.54, 28.68) * mm, "end": v(37.17, 28.68) * mm});
            skLineSegment(sketch, "E166.16.4.3", {"start": v(37.17, 33.3) * mm, "end": v(37.17, 28.68) * mm});
            skLineSegment(sketch, "E166.16.5.0", {"start": v(32.54, 20.6) * mm, "end": v(37.17, 20.6) * mm});
            skLineSegment(sketch, "E166.16.5.1", {"start": v(32.54, 20.6) * mm, "end": v(32.54, 15.98) * mm});
            skLineSegment(sketch, "E166.16.5.2", {"start": v(32.54, 15.98) * mm, "end": v(37.17, 15.98) * mm});
            skLineSegment(sketch, "E166.16.5.3", {"start": v(37.17, 20.6) * mm, "end": v(37.17, 15.98) * mm});
            skLineSegment(sketch, "E166.16.6.0", {"start": v(32.54, 7.9) * mm, "end": v(37.17, 7.9) * mm});
            skLineSegment(sketch, "E166.16.6.1", {"start": v(32.54, 7.9) * mm, "end": v(32.54, 3.28) * mm});
            skLineSegment(sketch, "E166.16.6.2", {"start": v(32.54, 3.28) * mm, "end": v(37.17, 3.28) * mm});
            skLineSegment(sketch, "E166.16.6.3", {"start": v(37.17, 7.9) * mm, "end": v(37.17, 3.28) * mm});
            skLineSegment(sketch, "E166.16.7.0", {"start": v(32.54, -4.8) * mm, "end": v(37.17, -4.8) * mm});
            skLineSegment(sketch, "E166.16.7.1", {"start": v(32.54, -4.8) * mm, "end": v(32.54, -9.42) * mm});
            skLineSegment(sketch, "E166.16.7.2", {"start": v(32.54, -9.42) * mm, "end": v(37.17, -9.42) * mm});
            skLineSegment(sketch, "E166.16.7.3", {"start": v(37.17, -4.8) * mm, "end": v(37.17, -9.42) * mm});
            skLineSegment(sketch, "E166.16.8.0", {"start": v(32.54, -17.5) * mm, "end": v(37.17, -17.5) * mm});
            skLineSegment(sketch, "E166.16.8.1", {"start": v(32.54, -17.5) * mm, "end": v(32.54, -22.12) * mm});
            skLineSegment(sketch, "E166.16.8.2", {"start": v(32.54, -22.12) * mm, "end": v(37.17, -22.12) * mm});
            skLineSegment(sketch, "E166.16.8.3", {"start": v(37.17, -17.5) * mm, "end": v(37.17, -22.12) * mm});
            skLineSegment(sketch, "E166.16.9.0", {"start": v(32.54, -30.2) * mm, "end": v(37.17, -30.2) * mm});
            skLineSegment(sketch, "E166.16.9.1", {"start": v(32.54, -30.2) * mm, "end": v(32.54, -34.82) * mm});
            skLineSegment(sketch, "E166.16.9.2", {"start": v(32.54, -34.82) * mm, "end": v(37.17, -34.82) * mm});
            skLineSegment(sketch, "E166.16.9.3", {"start": v(37.17, -30.2) * mm, "end": v(37.17, -34.82) * mm});
            skLineSegment(sketch, "E166.16.10.0", {"start": v(32.54, -42.9) * mm, "end": v(37.17, -42.9) * mm});
            skLineSegment(sketch, "E166.16.10.1", {"start": v(32.54, -42.9) * mm, "end": v(32.54, -47.52) * mm});
            skLineSegment(sketch, "E166.16.10.2", {"start": v(32.54, -47.52) * mm, "end": v(37.17, -47.52) * mm});
            skLineSegment(sketch, "E166.16.10.3", {"start": v(37.17, -42.9) * mm, "end": v(37.17, -47.52) * mm});
            skLineSegment(sketch, "E166.16.12.0", {"start": v(32.54, -68.3) * mm, "end": v(37.17, -68.3) * mm});
            skLineSegment(sketch, "E166.16.12.1", {"start": v(32.54, -68.3) * mm, "end": v(32.54, -72.92) * mm});
            skLineSegment(sketch, "E166.16.12.2", {"start": v(32.54, -72.92) * mm, "end": v(37.17, -72.92) * mm});
            skLineSegment(sketch, "E166.16.12.3", {"start": v(37.17, -68.3) * mm, "end": v(37.17, -72.92) * mm});
            skLineSegment(sketch, "E166.17.0.0", {"start": v(45.24, 84.1) * mm, "end": v(49.87, 84.1) * mm});
            skLineSegment(sketch, "E166.17.0.1", {"start": v(45.24, 84.1) * mm, "end": v(45.24, 79.48) * mm});
            skLineSegment(sketch, "E166.17.0.2", {"start": v(45.24, 79.48) * mm, "end": v(49.87, 79.48) * mm});
            skLineSegment(sketch, "E166.17.0.3", {"start": v(49.87, 84.1) * mm, "end": v(49.87, 79.48) * mm});
            skLineSegment(sketch, "E166.17.1.0", {"start": v(45.24, 71.4) * mm, "end": v(49.87, 71.4) * mm});
            skLineSegment(sketch, "E166.17.1.1", {"start": v(45.24, 71.4) * mm, "end": v(45.24, 66.78) * mm});
            skLineSegment(sketch, "E166.17.1.2", {"start": v(45.24, 66.78) * mm, "end": v(49.87, 66.78) * mm});
            skLineSegment(sketch, "E166.17.1.3", {"start": v(49.87, 71.4) * mm, "end": v(49.87, 66.78) * mm});
            skLineSegment(sketch, "E166.17.3.0", {"start": v(45.24, 46) * mm, "end": v(49.87, 46) * mm});
            skLineSegment(sketch, "E166.17.3.1", {"start": v(45.24, 46) * mm, "end": v(45.24, 41.38) * mm});
            skLineSegment(sketch, "E166.17.3.2", {"start": v(45.24, 41.38) * mm, "end": v(49.87, 41.38) * mm});
            skLineSegment(sketch, "E166.17.3.3", {"start": v(49.87, 46) * mm, "end": v(49.87, 41.38) * mm});
            skLineSegment(sketch, "E166.17.4.0", {"start": v(45.24, 33.3) * mm, "end": v(49.87, 33.3) * mm});
            skLineSegment(sketch, "E166.17.4.1", {"start": v(45.24, 33.3) * mm, "end": v(45.24, 28.68) * mm});
            skLineSegment(sketch, "E166.17.4.2", {"start": v(45.24, 28.68) * mm, "end": v(49.87, 28.68) * mm});
            skLineSegment(sketch, "E166.17.4.3", {"start": v(49.87, 33.3) * mm, "end": v(49.87, 28.68) * mm});
            skLineSegment(sketch, "E166.17.5.0", {"start": v(45.24, 20.6) * mm, "end": v(49.87, 20.6) * mm});
            skLineSegment(sketch, "E166.17.5.1", {"start": v(45.24, 20.6) * mm, "end": v(45.24, 15.98) * mm});
            skLineSegment(sketch, "E166.17.5.2", {"start": v(45.24, 15.98) * mm, "end": v(49.87, 15.98) * mm});
            skLineSegment(sketch, "E166.17.5.3", {"start": v(49.87, 20.6) * mm, "end": v(49.87, 15.98) * mm});
            skLineSegment(sketch, "E166.17.6.0", {"start": v(45.24, 7.9) * mm, "end": v(49.87, 7.9) * mm});
            skLineSegment(sketch, "E166.17.6.1", {"start": v(45.24, 7.9) * mm, "end": v(45.24, 3.28) * mm});
            skLineSegment(sketch, "E166.17.6.2", {"start": v(45.24, 3.28) * mm, "end": v(49.87, 3.28) * mm});
            skLineSegment(sketch, "E166.17.6.3", {"start": v(49.87, 7.9) * mm, "end": v(49.87, 3.28) * mm});
            skLineSegment(sketch, "E166.17.7.0", {"start": v(45.24, -4.8) * mm, "end": v(49.87, -4.8) * mm});
            skLineSegment(sketch, "E166.17.7.1", {"start": v(45.24, -4.8) * mm, "end": v(45.24, -9.42) * mm});
            skLineSegment(sketch, "E166.17.7.2", {"start": v(45.24, -9.42) * mm, "end": v(49.87, -9.42) * mm});
            skLineSegment(sketch, "E166.17.7.3", {"start": v(49.87, -4.8) * mm, "end": v(49.87, -9.42) * mm});
            skLineSegment(sketch, "E166.17.8.0", {"start": v(45.24, -17.5) * mm, "end": v(49.87, -17.5) * mm});
            skLineSegment(sketch, "E166.17.8.1", {"start": v(45.24, -17.5) * mm, "end": v(45.24, -22.12) * mm});
            skLineSegment(sketch, "E166.17.8.2", {"start": v(45.24, -22.12) * mm, "end": v(49.87, -22.12) * mm});
            skLineSegment(sketch, "E166.17.8.3", {"start": v(49.87, -17.5) * mm, "end": v(49.87, -22.12) * mm});
            skLineSegment(sketch, "E166.17.9.0", {"start": v(45.24, -30.2) * mm, "end": v(49.87, -30.2) * mm});
            skLineSegment(sketch, "E166.17.9.1", {"start": v(45.24, -30.2) * mm, "end": v(45.24, -34.82) * mm});
            skLineSegment(sketch, "E166.17.9.2", {"start": v(45.24, -34.82) * mm, "end": v(49.87, -34.82) * mm});
            skLineSegment(sketch, "E166.17.9.3", {"start": v(49.87, -30.2) * mm, "end": v(49.87, -34.82) * mm});
            skLineSegment(sketch, "E166.17.11.0", {"start": v(45.24, -55.6) * mm, "end": v(49.87, -55.6) * mm});
            skLineSegment(sketch, "E166.17.11.1", {"start": v(45.24, -55.6) * mm, "end": v(45.24, -60.22) * mm});
            skLineSegment(sketch, "E166.17.11.2", {"start": v(45.24, -60.22) * mm, "end": v(49.87, -60.22) * mm});
            skLineSegment(sketch, "E166.17.11.3", {"start": v(49.87, -55.6) * mm, "end": v(49.87, -60.22) * mm});
            skLineSegment(sketch, "E166.17.12.0", {"start": v(45.24, -68.3) * mm, "end": v(49.87, -68.3) * mm});
            skLineSegment(sketch, "E166.17.12.1", {"start": v(45.24, -68.3) * mm, "end": v(45.24, -72.92) * mm});
            skLineSegment(sketch, "E166.17.12.2", {"start": v(45.24, -72.92) * mm, "end": v(49.87, -72.92) * mm});
            skLineSegment(sketch, "E166.17.12.3", {"start": v(49.87, -68.3) * mm, "end": v(49.87, -72.92) * mm});
            skLineSegment(sketch, "E166.18.0.0", {"start": v(57.94, 84.1) * mm, "end": v(62.57, 84.1) * mm});
            skLineSegment(sketch, "E166.18.0.1", {"start": v(57.94, 84.1) * mm, "end": v(57.94, 79.48) * mm});
            skLineSegment(sketch, "E166.18.0.2", {"start": v(57.94, 79.48) * mm, "end": v(62.57, 79.48) * mm});
            skLineSegment(sketch, "E166.18.0.3", {"start": v(62.57, 84.1) * mm, "end": v(62.57, 79.48) * mm});
            skLineSegment(sketch, "E166.18.1.0", {"start": v(57.94, 71.4) * mm, "end": v(62.57, 71.4) * mm});
            skLineSegment(sketch, "E166.18.1.1", {"start": v(57.94, 71.4) * mm, "end": v(57.94, 66.78) * mm});
            skLineSegment(sketch, "E166.18.1.2", {"start": v(57.94, 66.78) * mm, "end": v(62.57, 66.78) * mm});
            skLineSegment(sketch, "E166.18.1.3", {"start": v(62.57, 71.4) * mm, "end": v(62.57, 66.78) * mm});
            skLineSegment(sketch, "E166.18.2.0", {"start": v(57.94, 58.7) * mm, "end": v(62.57, 58.7) * mm});
            skLineSegment(sketch, "E166.18.2.1", {"start": v(57.94, 58.7) * mm, "end": v(57.94, 54.08) * mm});
            skLineSegment(sketch, "E166.18.2.2", {"start": v(57.94, 54.08) * mm, "end": v(62.57, 54.08) * mm});
            skLineSegment(sketch, "E166.18.2.3", {"start": v(62.57, 58.7) * mm, "end": v(62.57, 54.08) * mm});
            skLineSegment(sketch, "E166.18.3.0", {"start": v(57.94, 46) * mm, "end": v(62.57, 46) * mm});
            skLineSegment(sketch, "E166.18.3.1", {"start": v(57.94, 46) * mm, "end": v(57.94, 41.38) * mm});
            skLineSegment(sketch, "E166.18.3.2", {"start": v(57.94, 41.38) * mm, "end": v(62.57, 41.38) * mm});
            skLineSegment(sketch, "E166.18.3.3", {"start": v(62.57, 46) * mm, "end": v(62.57, 41.38) * mm});
            skLineSegment(sketch, "E166.18.4.0", {"start": v(57.94, 33.3) * mm, "end": v(62.57, 33.3) * mm});
            skLineSegment(sketch, "E166.18.4.1", {"start": v(57.94, 33.3) * mm, "end": v(57.94, 28.68) * mm});
            skLineSegment(sketch, "E166.18.4.2", {"start": v(57.94, 28.68) * mm, "end": v(62.57, 28.68) * mm});
            skLineSegment(sketch, "E166.18.4.3", {"start": v(62.57, 33.3) * mm, "end": v(62.57, 28.68) * mm});
            skLineSegment(sketch, "E166.18.5.0", {"start": v(57.94, 20.6) * mm, "end": v(62.57, 20.6) * mm});
            skLineSegment(sketch, "E166.18.5.1", {"start": v(57.94, 20.6) * mm, "end": v(57.94, 15.98) * mm});
            skLineSegment(sketch, "E166.18.5.2", {"start": v(57.94, 15.98) * mm, "end": v(62.57, 15.98) * mm});
            skLineSegment(sketch, "E166.18.5.3", {"start": v(62.57, 20.6) * mm, "end": v(62.57, 15.98) * mm});
            skLineSegment(sketch, "E166.18.6.0", {"start": v(57.94, 7.9) * mm, "end": v(62.57, 7.9) * mm});
            skLineSegment(sketch, "E166.18.6.1", {"start": v(57.94, 7.9) * mm, "end": v(57.94, 3.28) * mm});
            skLineSegment(sketch, "E166.18.6.2", {"start": v(57.94, 3.28) * mm, "end": v(62.57, 3.28) * mm});
            skLineSegment(sketch, "E166.18.6.3", {"start": v(62.57, 7.9) * mm, "end": v(62.57, 3.28) * mm});
            skLineSegment(sketch, "E166.18.7.0", {"start": v(57.94, -4.8) * mm, "end": v(62.57, -4.8) * mm});
            skLineSegment(sketch, "E166.18.7.1", {"start": v(57.94, -4.8) * mm, "end": v(57.94, -9.42) * mm});
            skLineSegment(sketch, "E166.18.7.2", {"start": v(57.94, -9.42) * mm, "end": v(62.57, -9.42) * mm});
            skLineSegment(sketch, "E166.18.7.3", {"start": v(62.57, -4.8) * mm, "end": v(62.57, -9.42) * mm});
            skLineSegment(sketch, "E166.18.8.0", {"start": v(57.94, -17.5) * mm, "end": v(62.57, -17.5) * mm});
            skLineSegment(sketch, "E166.18.8.1", {"start": v(57.94, -17.5) * mm, "end": v(57.94, -22.12) * mm});
            skLineSegment(sketch, "E166.18.8.2", {"start": v(57.94, -22.12) * mm, "end": v(62.57, -22.12) * mm});
            skLineSegment(sketch, "E166.18.8.3", {"start": v(62.57, -17.5) * mm, "end": v(62.57, -22.12) * mm});
            skLineSegment(sketch, "E166.18.9.0", {"start": v(57.94, -30.2) * mm, "end": v(62.57, -30.2) * mm});
            skLineSegment(sketch, "E166.18.9.1", {"start": v(57.94, -30.2) * mm, "end": v(57.94, -34.82) * mm});
            skLineSegment(sketch, "E166.18.9.2", {"start": v(57.94, -34.82) * mm, "end": v(62.57, -34.82) * mm});
            skLineSegment(sketch, "E166.18.9.3", {"start": v(62.57, -30.2) * mm, "end": v(62.57, -34.82) * mm});
            skLineSegment(sketch, "E166.18.10.0", {"start": v(57.94, -42.9) * mm, "end": v(62.57, -42.9) * mm});
            skLineSegment(sketch, "E166.18.10.1", {"start": v(57.94, -42.9) * mm, "end": v(57.94, -47.52) * mm});
            skLineSegment(sketch, "E166.18.10.2", {"start": v(57.94, -47.52) * mm, "end": v(62.57, -47.52) * mm});
            skLineSegment(sketch, "E166.18.10.3", {"start": v(62.57, -42.9) * mm, "end": v(62.57, -47.52) * mm});
            skLineSegment(sketch, "E166.18.11.0", {"start": v(57.94, -55.6) * mm, "end": v(62.57, -55.6) * mm});
            skLineSegment(sketch, "E166.18.11.1", {"start": v(57.94, -55.6) * mm, "end": v(57.94, -60.22) * mm});
            skLineSegment(sketch, "E166.18.11.2", {"start": v(57.94, -60.22) * mm, "end": v(62.57, -60.22) * mm});
            skLineSegment(sketch, "E166.18.11.3", {"start": v(62.57, -55.6) * mm, "end": v(62.57, -60.22) * mm});
            skLineSegment(sketch, "E166.18.12.0", {"start": v(57.94, -68.3) * mm, "end": v(62.57, -68.3) * mm});
            skLineSegment(sketch, "E166.18.12.1", {"start": v(57.94, -68.3) * mm, "end": v(57.94, -72.92) * mm});
            skLineSegment(sketch, "E166.18.12.2", {"start": v(57.94, -72.92) * mm, "end": v(62.57, -72.92) * mm});
            skLineSegment(sketch, "E166.18.12.3", {"start": v(62.57, -68.3) * mm, "end": v(62.57, -72.92) * mm});
            skLineSegment(sketch, "E166.19.0.0", {"start": v(70.64, 84.1) * mm, "end": v(75.27, 84.1) * mm});
            skLineSegment(sketch, "E166.19.0.1", {"start": v(70.64, 84.1) * mm, "end": v(70.64, 79.48) * mm});
            skLineSegment(sketch, "E166.19.0.2", {"start": v(70.64, 79.48) * mm, "end": v(75.27, 79.48) * mm});
            skLineSegment(sketch, "E166.19.0.3", {"start": v(75.27, 84.1) * mm, "end": v(75.27, 79.48) * mm});
            skLineSegment(sketch, "E166.19.1.0", {"start": v(70.64, 71.4) * mm, "end": v(75.27, 71.4) * mm});
            skLineSegment(sketch, "E166.19.1.1", {"start": v(70.64, 71.4) * mm, "end": v(70.64, 66.78) * mm});
            skLineSegment(sketch, "E166.19.1.2", {"start": v(70.64, 66.78) * mm, "end": v(75.27, 66.78) * mm});
            skLineSegment(sketch, "E166.19.1.3", {"start": v(75.27, 71.4) * mm, "end": v(75.27, 66.78) * mm});
            skLineSegment(sketch, "E166.19.2.0", {"start": v(70.64, 58.7) * mm, "end": v(75.27, 58.7) * mm});
            skLineSegment(sketch, "E166.19.2.1", {"start": v(70.64, 58.7) * mm, "end": v(70.64, 54.08) * mm});
            skLineSegment(sketch, "E166.19.2.2", {"start": v(70.64, 54.08) * mm, "end": v(75.27, 54.08) * mm});
            skLineSegment(sketch, "E166.19.2.3", {"start": v(75.27, 58.7) * mm, "end": v(75.27, 54.08) * mm});
            skLineSegment(sketch, "E166.19.3.0", {"start": v(70.64, 46) * mm, "end": v(75.27, 46) * mm});
            skLineSegment(sketch, "E166.19.3.1", {"start": v(70.64, 46) * mm, "end": v(70.64, 41.38) * mm});
            skLineSegment(sketch, "E166.19.3.2", {"start": v(70.64, 41.38) * mm, "end": v(75.27, 41.38) * mm});
            skLineSegment(sketch, "E166.19.3.3", {"start": v(75.27, 46) * mm, "end": v(75.27, 41.38) * mm});
            skLineSegment(sketch, "E166.19.4.0", {"start": v(70.64, 33.3) * mm, "end": v(75.27, 33.3) * mm});
            skLineSegment(sketch, "E166.19.4.1", {"start": v(70.64, 33.3) * mm, "end": v(70.64, 28.68) * mm});
            skLineSegment(sketch, "E166.19.4.2", {"start": v(70.64, 28.68) * mm, "end": v(75.27, 28.68) * mm});
            skLineSegment(sketch, "E166.19.4.3", {"start": v(75.27, 33.3) * mm, "end": v(75.27, 28.68) * mm});
            skLineSegment(sketch, "E166.19.5.0", {"start": v(70.64, 20.6) * mm, "end": v(75.27, 20.6) * mm});
            skLineSegment(sketch, "E166.19.5.1", {"start": v(70.64, 20.6) * mm, "end": v(70.64, 15.98) * mm});
            skLineSegment(sketch, "E166.19.5.2", {"start": v(70.64, 15.98) * mm, "end": v(75.27, 15.98) * mm});
            skLineSegment(sketch, "E166.19.5.3", {"start": v(75.27, 20.6) * mm, "end": v(75.27, 15.98) * mm});
            skLineSegment(sketch, "E166.19.6.0", {"start": v(70.64, 7.9) * mm, "end": v(75.27, 7.9) * mm});
            skLineSegment(sketch, "E166.19.6.1", {"start": v(70.64, 7.9) * mm, "end": v(70.64, 3.28) * mm});
            skLineSegment(sketch, "E166.19.6.2", {"start": v(70.64, 3.28) * mm, "end": v(75.27, 3.28) * mm});
            skLineSegment(sketch, "E166.19.6.3", {"start": v(75.27, 7.9) * mm, "end": v(75.27, 3.28) * mm});
            skLineSegment(sketch, "E166.19.7.0", {"start": v(70.64, -4.8) * mm, "end": v(75.27, -4.8) * mm});
            skLineSegment(sketch, "E166.19.7.1", {"start": v(70.64, -4.8) * mm, "end": v(70.64, -9.42) * mm});
            skLineSegment(sketch, "E166.19.7.2", {"start": v(70.64, -9.42) * mm, "end": v(75.27, -9.42) * mm});
            skLineSegment(sketch, "E166.19.7.3", {"start": v(75.27, -4.8) * mm, "end": v(75.27, -9.42) * mm});
            skLineSegment(sketch, "E166.19.8.0", {"start": v(70.64, -17.5) * mm, "end": v(75.27, -17.5) * mm});
            skLineSegment(sketch, "E166.19.8.1", {"start": v(70.64, -17.5) * mm, "end": v(70.64, -22.12) * mm});
            skLineSegment(sketch, "E166.19.8.2", {"start": v(70.64, -22.12) * mm, "end": v(75.27, -22.12) * mm});
            skLineSegment(sketch, "E166.19.8.3", {"start": v(75.27, -17.5) * mm, "end": v(75.27, -22.12) * mm});
            skLineSegment(sketch, "E166.19.9.0", {"start": v(70.64, -30.2) * mm, "end": v(75.27, -30.2) * mm});
            skLineSegment(sketch, "E166.19.9.1", {"start": v(70.64, -30.2) * mm, "end": v(70.64, -34.82) * mm});
            skLineSegment(sketch, "E166.19.9.2", {"start": v(70.64, -34.82) * mm, "end": v(75.27, -34.82) * mm});
            skLineSegment(sketch, "E166.19.9.3", {"start": v(75.27, -30.2) * mm, "end": v(75.27, -34.82) * mm});
            skLineSegment(sketch, "E166.19.10.0", {"start": v(70.64, -42.9) * mm, "end": v(75.27, -42.9) * mm});
            skLineSegment(sketch, "E166.19.10.1", {"start": v(70.64, -42.9) * mm, "end": v(70.64, -47.52) * mm});
            skLineSegment(sketch, "E166.19.10.2", {"start": v(70.64, -47.52) * mm, "end": v(75.27, -47.52) * mm});
            skLineSegment(sketch, "E166.19.10.3", {"start": v(75.27, -42.9) * mm, "end": v(75.27, -47.52) * mm});
            skLineSegment(sketch, "E166.19.11.0", {"start": v(70.64, -55.6) * mm, "end": v(75.27, -55.6) * mm});
            skLineSegment(sketch, "E166.19.11.1", {"start": v(70.64, -55.6) * mm, "end": v(70.64, -60.22) * mm});
            skLineSegment(sketch, "E166.19.11.2", {"start": v(70.64, -60.22) * mm, "end": v(75.27, -60.22) * mm});
            skLineSegment(sketch, "E166.19.11.3", {"start": v(75.27, -55.6) * mm, "end": v(75.27, -60.22) * mm});
            skLineSegment(sketch, "E166.19.12.0", {"start": v(70.64, -68.3) * mm, "end": v(75.27, -68.3) * mm});
            skLineSegment(sketch, "E166.19.12.1", {"start": v(70.64, -68.3) * mm, "end": v(70.64, -72.92) * mm});
            skLineSegment(sketch, "E166.19.12.2", {"start": v(70.64, -72.92) * mm, "end": v(75.27, -72.92) * mm});
            skLineSegment(sketch, "E166.19.12.3", {"start": v(75.27, -68.3) * mm, "end": v(75.27, -72.92) * mm});
            skLineSegment(sketch, "E166.20.0.0", {"start": v(83.34, 84.1) * mm, "end": v(87.97, 84.1) * mm});
            skLineSegment(sketch, "E166.20.0.1", {"start": v(83.34, 84.1) * mm, "end": v(83.34, 79.48) * mm});
            skLineSegment(sketch, "E166.20.0.2", {"start": v(83.34, 79.48) * mm, "end": v(87.97, 79.48) * mm});
            skLineSegment(sketch, "E166.20.0.3", {"start": v(87.97, 84.1) * mm, "end": v(87.97, 79.48) * mm});
            skLineSegment(sketch, "E166.20.1.0", {"start": v(83.34, 71.4) * mm, "end": v(87.97, 71.4) * mm});
            skLineSegment(sketch, "E166.20.1.1", {"start": v(83.34, 71.4) * mm, "end": v(83.34, 66.78) * mm});
            skLineSegment(sketch, "E166.20.1.2", {"start": v(83.34, 66.78) * mm, "end": v(87.97, 66.78) * mm});
            skLineSegment(sketch, "E166.20.1.3", {"start": v(87.97, 71.4) * mm, "end": v(87.97, 66.78) * mm});
            skLineSegment(sketch, "E166.20.2.0", {"start": v(83.34, 58.7) * mm, "end": v(87.97, 58.7) * mm});
            skLineSegment(sketch, "E166.20.2.1", {"start": v(83.34, 58.7) * mm, "end": v(83.34, 54.08) * mm});
            skLineSegment(sketch, "E166.20.2.2", {"start": v(83.34, 54.08) * mm, "end": v(87.97, 54.08) * mm});
            skLineSegment(sketch, "E166.20.2.3", {"start": v(87.97, 58.7) * mm, "end": v(87.97, 54.08) * mm});
            skLineSegment(sketch, "E166.20.3.0", {"start": v(83.34, 46) * mm, "end": v(87.97, 46) * mm});
            skLineSegment(sketch, "E166.20.3.1", {"start": v(83.34, 46) * mm, "end": v(83.34, 41.38) * mm});
            skLineSegment(sketch, "E166.20.3.2", {"start": v(83.34, 41.38) * mm, "end": v(87.97, 41.38) * mm});
            skLineSegment(sketch, "E166.20.3.3", {"start": v(87.97, 46) * mm, "end": v(87.97, 41.38) * mm});
            skLineSegment(sketch, "E166.20.4.0", {"start": v(83.34, 33.3) * mm, "end": v(87.97, 33.3) * mm});
            skLineSegment(sketch, "E166.20.4.1", {"start": v(83.34, 33.3) * mm, "end": v(83.34, 28.68) * mm});
            skLineSegment(sketch, "E166.20.4.2", {"start": v(83.34, 28.68) * mm, "end": v(87.97, 28.68) * mm});
            skLineSegment(sketch, "E166.20.4.3", {"start": v(87.97, 33.3) * mm, "end": v(87.97, 28.68) * mm});
            skLineSegment(sketch, "E166.20.5.0", {"start": v(83.34, 20.6) * mm, "end": v(87.97, 20.6) * mm});
            skLineSegment(sketch, "E166.20.5.1", {"start": v(83.34, 20.6) * mm, "end": v(83.34, 15.98) * mm});
            skLineSegment(sketch, "E166.20.5.2", {"start": v(83.34, 15.98) * mm, "end": v(87.97, 15.98) * mm});
            skLineSegment(sketch, "E166.20.5.3", {"start": v(87.97, 20.6) * mm, "end": v(87.97, 15.98) * mm});
            skLineSegment(sketch, "E166.20.6.0", {"start": v(83.34, 7.9) * mm, "end": v(87.97, 7.9) * mm});
            skLineSegment(sketch, "E166.20.6.1", {"start": v(83.34, 7.9) * mm, "end": v(83.34, 3.28) * mm});
            skLineSegment(sketch, "E166.20.6.2", {"start": v(83.34, 3.28) * mm, "end": v(87.97, 3.28) * mm});
            skLineSegment(sketch, "E166.20.6.3", {"start": v(87.97, 7.9) * mm, "end": v(87.97, 3.28) * mm});
            skLineSegment(sketch, "E166.20.7.0", {"start": v(83.34, -4.8) * mm, "end": v(87.97, -4.8) * mm});
            skLineSegment(sketch, "E166.20.7.1", {"start": v(83.34, -4.8) * mm, "end": v(83.34, -9.42) * mm});
            skLineSegment(sketch, "E166.20.7.2", {"start": v(83.34, -9.42) * mm, "end": v(87.97, -9.42) * mm});
            skLineSegment(sketch, "E166.20.7.3", {"start": v(87.97, -4.8) * mm, "end": v(87.97, -9.42) * mm});
            skLineSegment(sketch, "E166.20.8.0", {"start": v(83.34, -17.5) * mm, "end": v(87.97, -17.5) * mm});
            skLineSegment(sketch, "E166.20.8.1", {"start": v(83.34, -17.5) * mm, "end": v(83.34, -22.12) * mm});
            skLineSegment(sketch, "E166.20.8.2", {"start": v(83.34, -22.12) * mm, "end": v(87.97, -22.12) * mm});
            skLineSegment(sketch, "E166.20.8.3", {"start": v(87.97, -17.5) * mm, "end": v(87.97, -22.12) * mm});
            skLineSegment(sketch, "E166.20.9.0", {"start": v(83.34, -30.2) * mm, "end": v(87.97, -30.2) * mm});
            skLineSegment(sketch, "E166.20.9.1", {"start": v(83.34, -30.2) * mm, "end": v(83.34, -34.82) * mm});
            skLineSegment(sketch, "E166.20.9.2", {"start": v(83.34, -34.82) * mm, "end": v(87.97, -34.82) * mm});
            skLineSegment(sketch, "E166.20.9.3", {"start": v(87.97, -30.2) * mm, "end": v(87.97, -34.82) * mm});
            skLineSegment(sketch, "E166.20.10.0", {"start": v(83.34, -42.9) * mm, "end": v(87.97, -42.9) * mm});
            skLineSegment(sketch, "E166.20.10.1", {"start": v(83.34, -42.9) * mm, "end": v(83.34, -47.52) * mm});
            skLineSegment(sketch, "E166.20.10.2", {"start": v(83.34, -47.52) * mm, "end": v(87.97, -47.52) * mm});
            skLineSegment(sketch, "E166.20.10.3", {"start": v(87.97, -42.9) * mm, "end": v(87.97, -47.52) * mm});
            skLineSegment(sketch, "E166.20.11.0", {"start": v(83.34, -55.6) * mm, "end": v(87.97, -55.6) * mm});
            skLineSegment(sketch, "E166.20.11.1", {"start": v(83.34, -55.6) * mm, "end": v(83.34, -60.22) * mm});
            skLineSegment(sketch, "E166.20.11.2", {"start": v(83.34, -60.22) * mm, "end": v(87.97, -60.22) * mm});
            skLineSegment(sketch, "E166.20.11.3", {"start": v(87.97, -55.6) * mm, "end": v(87.97, -60.22) * mm});
            skLineSegment(sketch, "E166.20.12.0", {"start": v(83.34, -68.3) * mm, "end": v(87.97, -68.3) * mm});
            skLineSegment(sketch, "E166.20.12.1", {"start": v(83.34, -68.3) * mm, "end": v(83.34, -72.92) * mm});
            skLineSegment(sketch, "E166.20.12.2", {"start": v(83.34, -72.92) * mm, "end": v(87.97, -72.92) * mm});
            skLineSegment(sketch, "E166.20.12.3", {"start": v(87.97, -68.3) * mm, "end": v(87.97, -72.92) * mm});
            skLineSegment(sketch, "E166.direction1", {"start": v(-170.66, 84.1) * mm, "end": v(-157.96, 84.1) * mm, "construction": true});
            skLineSegment(sketch, "E166.direction2", {"start": v(-170.66, 84.1) * mm, "end": v(-170.66, 71.4) * mm, "construction": true});
            skLineSegment(sketch, "E167", {"start": v(-177, 86.97) * mm, "end": v(-181.04, 86.97) * mm});
            skLineSegment(sketch, "E168", {"start": v(94.32, 86.46) * mm, "end": v(98.36, 86.46) * mm});
            skLineSegment(sketch, "E169", {"start": v(77.78, -79.27) * mm, "end": v(77.78, -83.3) * mm});
            skLineSegment(sketch, "E170", {"start": v(-77.13, 33.3) * mm, "end": v(-77.13, 28.68) * mm});
            skLineSegment(sketch, "E171", {"start": v(-69.06, 20.6) * mm, "end": v(-64.43, 20.6) * mm});
            skLineSegment(sketch, "E172", {"start": v(-56.36, 20.6) * mm, "end": v(-51.73, 20.6) * mm});
            skLineSegment(sketch, "E173", {"start": v(-43.66, 20.6) * mm, "end": v(-39.03, 20.6) * mm});
            skLineSegment(sketch, "E174", {"start": v(-30.96, 20.6) * mm, "end": v(-26.33, 20.6) * mm});
            skLineSegment(sketch, "E175", {"start": v(-18.26, 20.6) * mm, "end": v(-13.63, 20.6) * mm});
            skLineSegment(sketch, "E176", {"start": v(-11.9, 22.33) * mm, "end": v(-11.9, 26.95) * mm});
            skText(sketch, "E177", { "text": "K.S.A.", "fontName": "OpenSans-Italic.ttf"});
            skLineSegment(sketch, "E178", {"start": v(-83.48, 37.34) * mm, "end": v(-57.22, 37.34) * mm, "construction": true});
            skLineSegment(sketch, "E179", {"start": v(-31.82, 29.72) * mm, "end": v(-5.56, 29.72) * mm, "construction": true});
            skLineSegment(sketch, "E180", {"start": v(-47.7, 47.73) * mm, "end": v(-47.7, 34.92) * mm});
            skLineSegment(sketch, "E181", {"start": v(-47.94, 27.06) * mm, "end": v(-47.94, 14.25) * mm});
            const initialGuessF19  = {"E177": [-0.05722, 0.02706, 1, 0, 0.00786]};
            skSetInitialGuess(sketch, initialGuessF19);
            skSolve(sketch);
        }
        {
            var Q0;
            Q0 = qSketchRegion(id + "F19", true);
            extrude(context, id + "F20", {"entities" : qUnion([Q0]), "operationType" : NewBodyOperationType.REMOVE, "oppositeDirection" : true, "depth" : 3 * mm});
        }
    });
